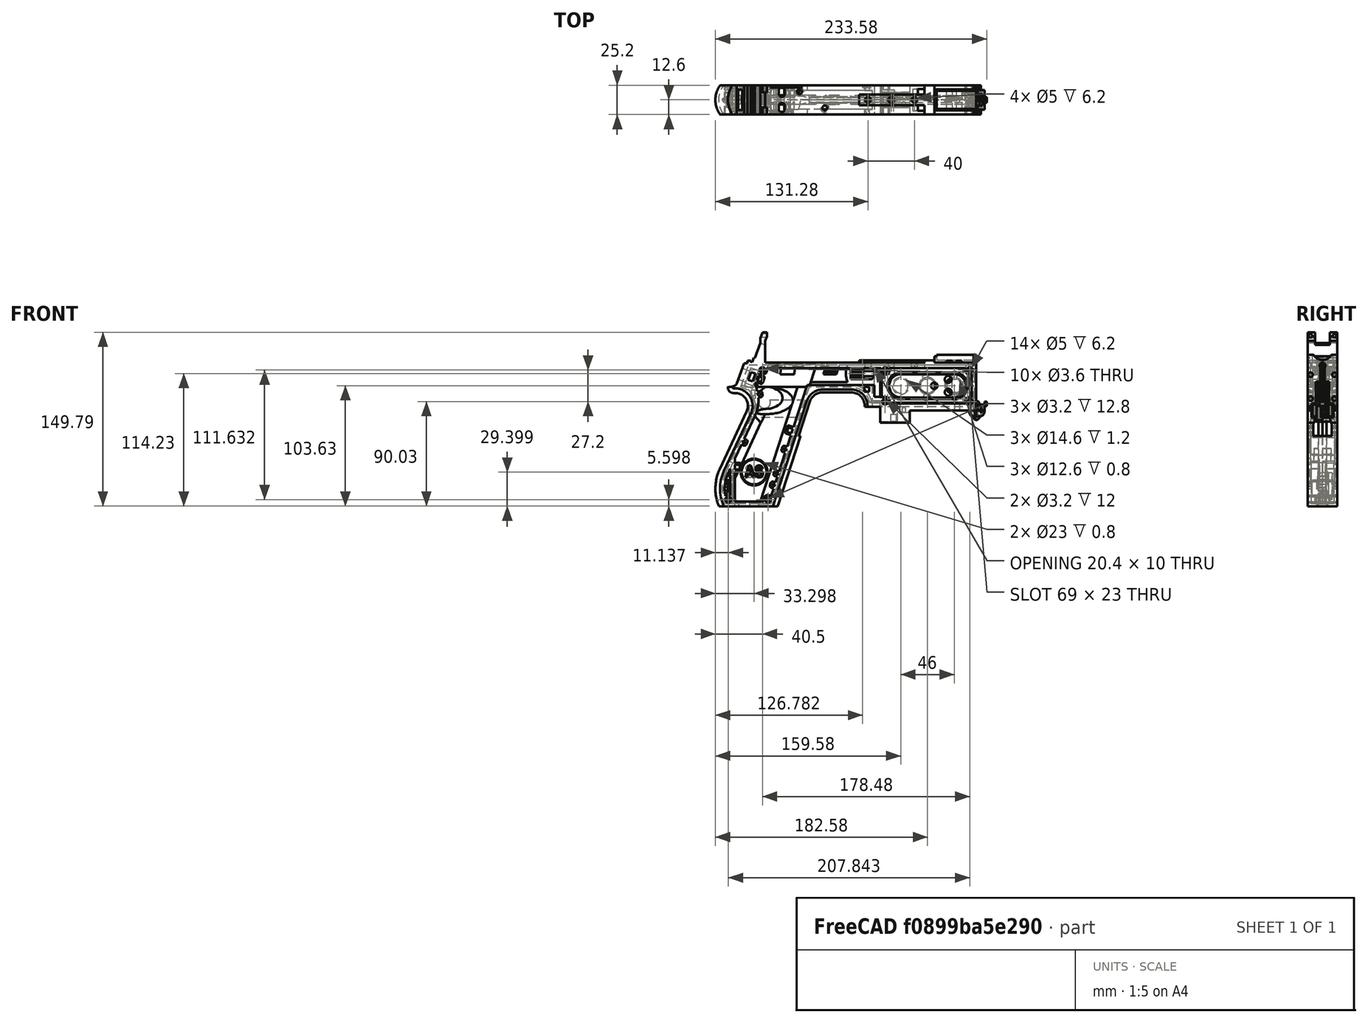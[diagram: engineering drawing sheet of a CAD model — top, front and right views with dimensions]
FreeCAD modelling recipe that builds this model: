
FCSTD DOCUMENT  (FreeCAD 1.0R39319 (Git))
Label: PICON-OF_ver_57
License: All rights reserved
LicenseURL: https://en.wikipedia.org/wiki/All_rights_reserved
objects: Sketcher::SketchObject×124, Part::Extrusion×63, Part::Cut×48, PartDesign::Pad×29, PartDesign::Pocket×21, PartDesign::Chamfer×15, PartDesign::Body×10, PartDesign::Fillet×6, Part::MultiFuse×5, Part::Part2DObjectPython×4, PartDesign::SubtractivePipe×4, PartDesign::SubtractiveLoft×4, PartDesign::Plane×3, PartDesign::SubShapeBinder×2, Part::Sweep×1, PartDesign::ShapeBinder×1, Mesh::Feature×1, PartDesign::Point×1, PartDesign::Groove×1
note: 626 computed .brp shape members not serialized (recipe doc carries the construction recipe); baked Part::Feature solids carry a one-line shape summary decoded from their .brp

FEATURE [Sketcher::SketchObject] Sketch  label="corpo principale"
  ArcFitTolerance = 1e-06
  AttacherType = Attacher::AttachEngine3D
  AttachmentSupport = -> [XZ_Plane]
  FullyConstrained = true
  MakeInternals = false
  MapMode = 5
  Placement = pos=(0,0,0) rot=(1,0,0;1.5708rad)
  sketch-geometry (65):
    g0: LineSegment StartX=0 StartY=0 StartZ=0 EndX=-57.2 EndY=0 EndZ=0
    g1: LineSegment StartX=-57.2 StartY=0 StartZ=0 EndX=-57.2 EndY=-10.4 EndZ=0
    g2: LineSegment StartX=-57.2 StartY=-10.4 StartZ=0 EndX=-82.8 EndY=-10.4 EndZ=0
    g3: LineSegment StartX=-82.8 StartY=-10.4 StartZ=0 EndX=-82.8 EndY=3.2 EndZ=0
    g4: LineSegment StartX=-82.8 StartY=3.2 StartZ=0 EndX=-93.6 EndY=3.2 EndZ=0
    g5: LineSegment StartX=-93.6 StartY=3.2 StartZ=0 EndX=-93.6 EndY=4 EndZ=0
    g6: LineSegment StartX=-107.6 StartY=18 StartZ=0 EndX=-132.428 EndY=18 EndZ=0
    g7: LineSegment StartX=-145.743 StartY=8.32624 StartZ=0 EndX=-175.232 EndY=-82.4316 EndZ=0
    g8: LineSegment StartX=-175.232 StartY=-82.4316 StartZ=0 EndX=-217.232 EndY=-82.4316 EndZ=0
    g9: LineSegment StartX=-217.232 StartY=-52.1862 StartZ=0 EndX=-193.988 EndY=-2.33927 EndZ=0
    g10: LineSegment StartX=-206.196 StartY=23.0857 StartZ=0 EndX=-199.861 EndY=40.4914 EndZ=0
    g11: LineSegment StartX=-199.861 StartY=40.4914 StartZ=0 EndX=-197.061 EndY=40.4914 EndZ=0
    g12: LineSegment StartX=-197.061 StartY=40.4914 StartZ=0 EndX=-197.061 EndY=42.8914 EndZ=0
    g13: LineSegment StartX=-197.061 StartY=42.8914 StartZ=0 EndX=-194.261 EndY=42.8914 EndZ=0
    g14: LineSegment StartX=-194.261 StartY=42.8914 StartZ=0 EndX=-194.535 EndY=42.1397 EndZ=0
    g15: LineSegment StartX=-194.535 StartY=42.1397 StartZ=0 EndX=-193.031 EndY=41.5924 EndZ=0
    g16: LineSegment StartX=-193.031 StartY=41.5924 StartZ=0 EndX=-191.663 EndY=45.3512 EndZ=0
    g17: LineSegment StartX=-191.663 StartY=45.3512 StartZ=0 EndX=-190.536 EndY=44.9408 EndZ=0
    g18: LineSegment StartX=-190.536 StartY=44.9408 StartZ=0 EndX=-185.747 EndY=58.0965 EndZ=0
    g19: LineSegment StartX=-185.747 StartY=58.0965 StartZ=0 EndX=-185.747 EndY=62.0965 EndZ=0
    g20: LineSegment StartX=-185.747 StartY=62.0965 StartZ=0 EndX=-183.832 EndY=67.3588 EndZ=0
    g21: LineSegment StartX=-183.832 StartY=67.3588 StartZ=0 EndX=-180.232 EndY=67.3588 EndZ=0
    g22: LineSegment StartX=-180.232 StartY=67.3588 StartZ=0 EndX=-180.232 EndY=63.7588 EndZ=0
    g23: LineSegment StartX=-180.232 StartY=63.7588 StartZ=0 EndX=-181.6 EndY=60 EndZ=0
    g24: LineSegment StartX=-181.6 StartY=60 StartZ=0 EndX=-181.6 EndY=41.2 EndZ=0
    g25: LineSegment StartX=-181.6 StartY=41.2 StartZ=0 EndX=-100.8 EndY=41.2 EndZ=0
    g26: LineSegment StartX=-36 StartY=43.2 StartZ=0 EndX=-36 EndY=41.2 EndZ=0
    g27: LineSegment StartX=0 StartY=48 StartZ=0 EndX=0 EndY=0 EndZ=0
    g28: LineSegment StartX=-209.901 StartY=19.85 StartZ=0 EndX=-209.901 EndY=20.1 EndZ=0
    g29: LineSegment StartX=-208.001 StartY=22 StartZ=0 EndX=-207.747 EndY=22 EndZ=0
    g30: LineSegment StartX=-207.583 StartY=19 StartZ=0 EndX=-209.051 EndY=19 EndZ=0
    g31: ArcOfCircle CenterX=-208.001 CenterY=20.1 CenterZ=0 NormalX=0 NormalY=0 NormalZ=1 AngleXU=0 Radius=1.9 StartAngle=1.5708 EndAngle=3.14159
    g32: GeomPoint [constr] X=-209.901 Y=22 Z=0
    g33: ArcOfCircle CenterX=-209.051 CenterY=19.85 CenterZ=0 NormalX=0 NormalY=0 NormalZ=1 AngleXU=0 Radius=0.85 StartAngle=3.14159 EndAngle=4.71239
    g34: GeomPoint [constr] X=-209.901 Y=19 Z=0
    g35: ArcOfCircle CenterX=-207.747 CenterY=23.65 CenterZ=0 NormalX=0 NormalY=0 NormalZ=1 AngleXU=0 Radius=1.65 StartAngle=4.71239 EndAngle=5.93412
    g36: GeomPoint [constr] X=-206.591 Y=22 Z=0
    g37: LineSegment StartX=-4 StartY=6 StartZ=0 EndX=-4 EndY=36.4 EndZ=0
    g38: LineSegment StartX=-4 StartY=36.4 StartZ=0 EndX=-185.2 EndY=36.4 EndZ=0
    g39: LineSegment StartX=-185.2 StartY=36.4 StartZ=0 EndX=-190.441 EndY=22 EndZ=0
    g40: LineSegment StartX=-214.575 StartY=-78.4316 StartZ=0 EndX=-178.142 EndY=-78.4316 EndZ=0
    g41: LineSegment StartX=-178.142 StartY=-78.4316 StartZ=0 EndX=-145.51 EndY=22 EndZ=0
    g42: LineSegment StartX=-145.51 StartY=22 StartZ=0 EndX=-87.91 EndY=22 EndZ=0
    g43: LineSegment StartX=-87.91 StartY=22 StartZ=0 EndX=-87.91 EndY=11.6 EndZ=0
    g44: LineSegment StartX=-87.91 StartY=11.6 StartZ=0 EndX=-80.11 EndY=11.6 EndZ=0
    g45: LineSegment StartX=-80.11 StartY=11.6 StartZ=0 EndX=-80.11 EndY=6 EndZ=0
    g46: LineSegment StartX=-80.11 StartY=6 StartZ=0 EndX=-4 EndY=6 EndZ=0
    g47: LineSegment StartX=-190.363 StartY=-4.02975 StartZ=0 EndX=-213.607 EndY=-53.8767 EndZ=0
    g48: ArcOfCircle CenterX=-132.428 CenterY=4 CenterZ=0 NormalX=0 NormalY=0 NormalZ=1 AngleXU=0 Radius=14 StartAngle=1.5708 EndAngle=2.82743
    g49: GeomPoint [constr] X=-142.6 Y=18 Z=0
    g50: ArcOfCircle CenterX=-107.6 CenterY=4 CenterZ=0 NormalX=0 NormalY=0 NormalZ=1 AngleXU=0 Radius=14 StartAngle=0 EndAngle=1.5708
    g51: GeomPoint [constr] X=-93.6 Y=18 Z=0
    g52: ArcOfCircle CenterX=-184.801 CenterY=-67.3089 CenterZ=0 NormalX=0 NormalY=0 NormalZ=1 AngleXU=0 Radius=35.7833 StartAngle=2.70526 EndAngle=3.57792
    g53: ArcOfCircle CenterX=-207.583 CenterY=4 CenterZ=0 NormalX=0 NormalY=0 NormalZ=1 AngleXU=0 Radius=15 StartAngle=5.84685 EndAngle=7.85398
    g54: LineSegment [constr] StartX=-213.607 StartY=-53.8767 StartZ=0 EndX=-217.232 EndY=-52.1862 EndZ=0
    g55: ArcOfCircle CenterX=-184.801 CenterY=-67.3089 CenterZ=0 NormalX=0 NormalY=0 NormalZ=1 AngleXU=0 Radius=31.7833 StartAngle=2.70526 EndAngle=3.49911
    g56: ArcOfCircle CenterX=-218.095 CenterY=8.90192 CenterZ=0 NormalX=0 NormalY=0 NormalZ=1 AngleXU=0 Radius=30.5989 StartAngle=5.84685 EndAngle=6.72553
    g57: LineSegment StartX=-44.6 StartY=43.2 StartZ=0 EndX=-36 EndY=43.2 EndZ=0
    g58: LineSegment StartX=-100.8 StartY=41.2 StartZ=0 EndX=-44.6 EndY=41.2 EndZ=0
    g59: LineSegment StartX=-44.6 StartY=41.2 StartZ=0 EndX=-44.6 EndY=43.2 EndZ=0
    g60: LineSegment StartX=-2.4 StartY=48 StartZ=0 EndX=0 EndY=48 EndZ=0
    g61: LineSegment StartX=-36 StartY=41.2 StartZ=0 EndX=-2.4 EndY=41.2 EndZ=0
    g62: LineSegment StartX=-2.4 StartY=41.2 StartZ=0 EndX=-2.4 EndY=48 EndZ=0
    g63: LineSegment [constr] StartX=-181.6 StartY=36.4 StartZ=0 EndX=-152.209 EndY=36.4 EndZ=0
    g64: LineSegment [constr] StartX=-181.6 StartY=36.4 StartZ=0 EndX=-130.41 EndY=36.4 EndZ=0
  constraints (183):
    c: Coincident(g-1,g0)
    c: PointOnObject(g0,g-1)
    c: Coincident(g0,g1)
    c: Vertical(g1)
    c: Coincident(g1,g2)
    c: Horizontal(g2)
    c: Coincident(g2,g3)
    c: Vertical(g3)
    c: Coincident(g3,g4)
    c: Coincident(g4,g5)
    c: Vertical(g5)
    c: Horizontal(g6)
    c: Coincident(g7,g8)
    c: Horizontal(g8)
    c: Coincident(g10,g11)
    c: Horizontal(g11)
    c: Coincident(g11,g12)
    c: Vertical(g12)
    c: Coincident(g12,g13)
    c: Horizontal(g13)
    c: Coincident(g13,g14)
    c: Coincident(g14,g15)
    c: Coincident(g15,g16)
    c: Coincident(g16,g17)
    c: Coincident(g17,g18)
    c: Coincident(g18,g19)
    c: Vertical(g19)
    c: Coincident(g19,g20)
    c: Coincident(g20,g21)
    c: Horizontal(g21)
    c: Coincident(g21,g22)
    c: Vertical(g22)
    c: Coincident(g22,g23)
    c: Coincident(g23,g24)
    c: Vertical(g24)
    c: Coincident(g24,g25)
    c: Horizontal(g25)
    c: Coincident(g57,g26)
    c: Vertical(g26)
    c: Coincident(g26,g61)
    c: PointOnObject(g60,g-2)
    c: Coincident(g60,g27)
    c: Coincident(g27,g0)
    c: DistanceY(g27,g27) = 48
    c: DistanceY(g1,g1) = 10.4
    c: DistanceX(g0,g0) = 57.2
    c: DistanceX(g2,g2) = 25.6
    c: Horizontal(g4)
    c: DistanceY(g3,g3) = 13.6
    c: DistanceX(g4,g4) = 10.8
    c: DistanceY(g5,g51) = 14.8
    c: DistanceX(g49,g51) = 49
    c: Distance(g7,g49) = 105.6
    c: DistanceX(g61,g60) = 36
    c: DistanceX(g25,g25) = 80.8
    c: DistanceY(g24,g24) = 18.8
    c: DistanceY(g22,g22) = 3.6
    c: Distance(g23) = 4
    c: Angle(g-1,g23) = 1.22173
    c: DistanceX(g21,g21) = 3.6
    c: Distance(g20) = 5.6
    c: Angle(g-1,g20) = 1.22173
    c: DistanceY(g19,g19) = 4
    c: Distance(g18) = 14
    c: Angle(g-1,g18) = 1.22173
    c: Distance(g17) = 1.2
    c: Distance(g16) = 4
    c: Angle(g16) = 1.22173
    c: Perpendicular(g18,g17)
    c: Distance(g15) = 1.6
    c: Perpendicular(g16,g15)
    c: Distance(g14) = 0.8
    c: DistanceX(g13,g13) = 2.8
    c: Perpendicular(g15,g14)
    c: DistanceY(g12,g12) = 2.4
    c: DistanceX(g11,g11) = 2.8
    c: Distance(g9) = 55
    c: Angle(g9,g-1) = 2.00713
    c: Horizontal(g29)
    c: Vertical(g28)
    c: Horizontal(g30)
    c: PointOnObject(g32,g29)
    c: PointOnObject(g32,g28)
    c: Tangent(g29,g31) = 1.5708
    c: Tangent(g28,g31) = 1.5708
    c: PointOnObject(g34,g28)
    c: PointOnObject(g34,g30)
    c: Tangent(g28,g33) = 1.5708
    c: Tangent(g30,g33) = 1.5708
    c: PointOnObject(g36,g29)
    c: PointOnObject(g36,g10)
    c: Tangent(g29,g35) = -1.5708
    c: Tangent(g10,g35) = -1.5708
    c: Angle(g-1,g10) = 1.22173
    c: Radius(g35) = 1.65
    c: Vertical(g37)
    c: Coincident(g37,g38)
    c: Horizontal(g38)
    c: Coincident(g38,g39)
    c: Horizontal(g40)
    c: Coincident(g40,g41)
    c: Coincident(g41,g42)
    c: Horizontal(g42)
    c: Coincident(g42,g43)
    c: Vertical(g43)
    c: Coincident(g43,g44)
    c: Horizontal(g44)
    c: Coincident(g44,g45)
    c: Vertical(g45)
    c: Coincident(g45,g46)
    c: Coincident(g46,g37)
    c: Horizontal(g46)
    c: DistanceY(g0,g37) = 6
    c: DistanceX(g37,g0) = 4
    c: DistanceY(g37,g25) = 4.8
    c: DistanceX(g38,g38) = 181.2
    c: DistanceX(g42,g42) = 57.6
    c: DistanceY(g49,g41) = 4
    c: DistanceX(g41,g49) = 2.91
    c: DistanceY(g43,g43) = 10.4
    c: DistanceX(g44,g44) = 7.8
    c: DistanceY(g7,g40) = 4
    c: Distance(g47) = 55
    c: Angle(g-1,g39) = 1.22173
    c: PointOnObject(g49,g7)
    c: PointOnObject(g49,g6)
    c: Tangent(g7,g48) = -1.5708
    c: Tangent(g6,g48) = -1.5708
    c: PointOnObject(g51,g5)
    c: PointOnObject(g51,g6)
    c: Tangent(g5,g50) = -1.5708
    c: Tangent(g6,g50) = -1.5708
    c: Radius(g50) = 14
    c: Radius(g48) = 14
    c: DistanceX(g8,g8) = 42
    c: Angle(g7,g-1) = 1.88496
    c: Parallel(g41,g7)
    c: Parallel(g47,g9)
    c: Coincident(g52,g8)
    c: Tangent(g52,g9) = 1.5708
    c: DistanceX(g9,g8) = 0
    c: Tangent(g53,g9) = -1.5708
    c: Tangent(g53,g30) = -1.5708
    c: Diameter(g53) = 30
    c: DistanceY(g53,g0) = -4
    c: Coincident(g54,g47)
    c: Distance(g54) = 4
    c: Coincident(g54,g9)
    c: Coincident(g55,g40)
    c: Tangent(g55,g47) = -1.5708
    c: Coincident(g52,g55)
    c: Coincident(g56,g39)
    c: Tangent(g56,g47) = 1.5708
    c: Horizontal(g57)
    c: DistanceX(g57,g57) = 8.6
    c: Coincident(g58,g25)
    c: Horizontal(g58)
    c: Coincident(g59,g58)
    c: Vertical(g59)
    c: DistanceY(g58,g57) = 2
    c: DistanceX(g58,g58) = 56.2
    c: Coincident(g59,g57)
    c: DistanceY(g41,g36) = 0
    c: DistanceY(g36,g39) = 0
    c: DistanceY(g28,g28) = 0.25
    c: DistanceX(g30,g36) = 2.46
    c: DistanceX(g28,g29) = 1.9
    c: Coincident(g62,g60)
    c: Horizontal(g60)
    c: DistanceX(g62,g27) = 2.4
    c: Coincident(g61,g62)
    c: DistanceY(g26,g26) = 2
    c: Vertical(g62)
    c: DistanceY(g61,g60) = 6.8
    c: Horizontal(g61)
    c: Distance(g63) = 29.391
    c: PointOnObject(g63,g38)
    c: PointOnObject(g63,g38)
    c: Distance(g64) = 51.19
    c: PointOnObject(g64,g38)
    c: PointOnObject(g64,g38)
    c: DistanceX(g24,g63) = 0
    c: DistanceX(g24,g64) = 0
FEATURE [Part::Extrusion] Extrude  label="Extrude corpo principale"
  Base = -> Sketch
  Dir = (0,-1,2e-16)
  DirMode = 2
  FaceMakerClass = Part::FaceMakerBullseye
  FaceMakerMode = 3
  LengthFwd = 25.2
  LengthRev = 12.6
  Solid = true
  Symmetric = true
FEATURE [Sketcher::SketchObject] Sketch002  label="scavo grilletto"
  ArcFitTolerance = 1e-06
  AttachmentSupport = -> [XZ_Plane]
  ExternalGeometry = -> [Sketch]
  FullyConstrained = true
  MakeInternals = false
  MapMode = 5
  Placement = pos=(0,0,0) rot=(1,0,0;1.5708rad)
  sketch-geometry (4):
    g0: LineSegment StartX=-89.51 StartY=22 StartZ=0 EndX=-152.71 EndY=22 EndZ=0
    g1: LineSegment StartX=-152.71 StartY=22 StartZ=0 EndX=-167.006 EndY=-22 EndZ=0
    g2: LineSegment StartX=-167.006 StartY=-22 StartZ=0 EndX=-89.51 EndY=-22 EndZ=0
    g3: LineSegment StartX=-89.51 StartY=-22 StartZ=0 EndX=-89.51 EndY=22 EndZ=0
  constraints (12):
    c: Horizontal(g0)
    c: Coincident(g0,g1)
    c: Coincident(g1,g2)
    c: Horizontal(g2)
    c: Coincident(g2,g3)
    c: Coincident(g3,g0)
    c: Vertical(g3)
    c: Angle(g1,g0) = 1.88496
    c: DistanceY(g3,g3) = 44
    c: DistanceX(g0,g0) = 63.2
    c: DistanceX(g0,g-3) = 1.6
    c: DistanceY(g-3,g0) = 0
FEATURE [Sketcher::SketchObject] Sketch004  label="traiettoria arrotondamento impugnatura anteriore"
  ArcFitTolerance = 1e-06
  AttachmentSupport = -> [XZ_Plane]
  ExternalGeometry = -> [Sketch]
  FullyConstrained = true
  MakeInternals = false
  MapMode = 5
  Placement = pos=(0,0,0) rot=(1,0,0;1.5708rad)
  sketch-geometry (13):
    g0: LineSegment StartX=-175.232 StartY=-82.4316 StartZ=0 EndX=-145.743 EndY=8.32624 EndZ=0
    g1: LineSegment StartX=-93.6 StartY=3.2 StartZ=0 EndX=-93.6 EndY=4 EndZ=0
    g2: LineSegment StartX=-132.428 StartY=18 StartZ=0 EndX=-107.6 EndY=18 EndZ=0
    g3: ArcOfCircle CenterX=-132.428 CenterY=4 CenterZ=0 NormalX=0 NormalY=0 NormalZ=1 AngleXU=0 Radius=14 StartAngle=1.5708 EndAngle=2.82743
    g4: ArcOfCircle CenterX=-107.6 CenterY=4 CenterZ=0 NormalX=0 NormalY=0 NormalZ=1 AngleXU=0 Radius=14 StartAngle=0 EndAngle=1.5708
    g5: LineSegment StartX=-175.232 StartY=-82.4316 StartZ=0 EndX=-217.232 EndY=-82.4316 EndZ=0
    g6: LineSegment StartX=-217.232 StartY=-52.1862 StartZ=0 EndX=-193.988 EndY=-2.33927 EndZ=0
    g7: LineSegment StartX=-209.051 StartY=19 StartZ=0 EndX=-207.583 EndY=19 EndZ=0
    g8: LineSegment StartX=-209.901 StartY=20.1 StartZ=0 EndX=-209.901 EndY=19.85 EndZ=0
    g9: ArcOfCircle CenterX=-184.801 CenterY=-67.3089 CenterZ=0 NormalX=0 NormalY=0 NormalZ=1 AngleXU=0 Radius=35.7833 StartAngle=2.70526 EndAngle=3.57792
    g10: ArcOfCircle CenterX=-207.583 CenterY=4 CenterZ=0 NormalX=0 NormalY=0 NormalZ=1 AngleXU=0 Radius=15 StartAngle=5.84685 EndAngle=7.85398
    g11: ArcOfCircle CenterX=-209.051 CenterY=19.85 CenterZ=0 NormalX=0 NormalY=0 NormalZ=1 AngleXU=0 Radius=0.85 StartAngle=3.14159 EndAngle=4.71239
    g12: ArcOfCircle CenterX=-208.001 CenterY=20.1 CenterZ=0 NormalX=0 NormalY=0 NormalZ=1 AngleXU=0 Radius=1.9 StartAngle=1.5708 EndAngle=3.14159
  constraints (26):
    c: Coincident(g0,g-3)
    c: Coincident(g0,g-6)
    c: Coincident(g1,g-8)
    c: Coincident(g1,g-7)
    c: Coincident(g2,g-5)
    c: Coincident(g2,g-4)
    c: Coincident(g3,g2)
    c: Tangent(g3,g0) = 1.5708
    c: Coincident(g4,g1)
    c: Tangent(g4,g2) = 1.5708
    c: Coincident(g5,g0)
    c: Coincident(g5,g-9)
    c: Coincident(g6,g-12)
    c: Coincident(g6,g-11)
    c: Coincident(g7,g-15)
    c: Coincident(g7,g-14)
    c: Coincident(g8,g-16)
    c: Coincident(g8,g-17)
    c: Tangent(g9,g6) = 1.5708
    c: Coincident(g9,g5)
    c: Coincident(g10,g7)
    c: Tangent(g10,g6) = -1.5708
    c: Tangent(g11,g7) = -1.5708
    c: Coincident(g11,g8)
    c: Tangent(g12,g8) = -1.5708
    c: Coincident(g12,g-17)
FEATURE [PartDesign::Plane] DatumPlane  label="Piano per disegno arrotondamento impugnatura"
  AttachmentSupport = -> [Sketch]
  Length = 73.6581
  MapMode = 7
  Placement = pos=(-145.743,1.8e-15,8.32624) rot=(0.154555,0.154555,0.97582;1.59527rad)
  ResizeMode = 0
  Width = 303.511
FEATURE [Sketcher::SketchObject] Sketch005  label="forma arrotondamento impugnatura anteriore"
  ArcFitTolerance = 1e-06
  AttachmentSupport = -> [DatumPlane]
  FullyConstrained = true
  MakeInternals = false
  MapMode = 5
  Placement = pos=(-145.743,1.8e-15,8.32624) rot=(0.154555,0.154555,0.97582;1.59527rad)
  sketch-geometry (5):
    g0: GeomPoint [constr] X=0 Y=-4 Z=0
    g1: GeomPoint [constr] X=-12.6 Y=7.1e-15 Z=0
    g2: GeomPoint [constr] X=12.6 Y=4.97e-14 Z=0
    g3: LineSegment StartX=-12.6 StartY=7.1e-15 StartZ=0 EndX=12.6 EndY=4.97e-14 EndZ=0
    g4: ArcOfCircle CenterX=-3.88e-14 CenterY=17.845 CenterZ=0 NormalX=0 NormalY=0 NormalZ=1 AngleXU=0 Radius=21.845 StartAngle=4.09759 EndAngle=5.32718
  constraints (11):
    c: DistanceY(g0,g-1) = 4
    c: DistanceX(g-1,g0) = 0
    c: DistanceX(g1,g-1) = 12.6
    c: DistanceX(g-1,g2) = 12.6
    c: DistanceY(g-1,g2) = 0
    c: DistanceY(g-1,g1) = 0
    c: Coincident(g3,g1)
    c: Coincident(g3,g2)
    c: Coincident(g4,g1)
    c: Coincident(g4,g2)
    c: PointOnObject(g0,g4)
FEATURE [Part::Sweep] Sweep  label="Sweep impugnatura"
  Frenet = true
  Sections = -> [Sketch005]
  Solid = true
  Spine = -> Sketch [Edge32,Edge33,Edge34,Edge35,Edge36,Edge37,Edge38,Edge39,Edge40,Edge41,Edge42,Edge43,Edge44]
  Transition = 1
FEATURE [Sketcher::SketchObject] Sketch008  label="buchi e pulizie varie"
  ArcFitTolerance = 1e-06
  AttachmentSupport = -> [XZ_Plane]
  ExternalGeometry = -> [Sketch]
  FullyConstrained = true
  MakeInternals = false
  MapMode = 5
  Placement = pos=(0,0,0) rot=(1,0,0;1.5708rad)
  sketch-geometry (26):
    g0: LineSegment StartX=-96.278 StartY=20.155 StartZ=0 EndX=-92.278 EndY=20.155 EndZ=0
    g1: LineSegment StartX=-92.278 StartY=20.155 StartZ=0 EndX=-92.278 EndY=16.155 EndZ=0
    g2: LineSegment StartX=-92.278 StartY=16.155 StartZ=0 EndX=-96.278 EndY=16.155 EndZ=0
    g3: LineSegment StartX=-96.278 StartY=16.155 StartZ=0 EndX=-96.278 EndY=20.155 EndZ=0
    g4: LineSegment StartX=-222.232 StartY=-82.4316 StartZ=0 EndX=-170.232 EndY=-82.4316 EndZ=0
    g5: LineSegment StartX=-170.232 StartY=-82.4316 StartZ=0 EndX=-170.232 EndY=-86.4316 EndZ=0
    g6: LineSegment StartX=-170.232 StartY=-86.4316 StartZ=0 EndX=-222.232 EndY=-86.4316 EndZ=0
    g7: LineSegment StartX=-222.232 StartY=-86.4316 StartZ=0 EndX=-222.232 EndY=-82.4316 EndZ=0
    g8: LineSegment StartX=-213.901 StartY=20.1 StartZ=0 EndX=-213.901 EndY=26 EndZ=0
    g9: LineSegment StartX=-213.901 StartY=26 StartZ=0 EndX=-206.196 EndY=26 EndZ=0
    g10: LineSegment StartX=-17.4 StartY=42.8 StartZ=0 EndX=-12.4 EndY=42.8 EndZ=0
    g11: LineSegment StartX=-12.4 StartY=42.8 StartZ=0 EndX=-12.4 EndY=41.2 EndZ=0
    g12: LineSegment StartX=-12.4 StartY=41.2 StartZ=0 EndX=-17.4 EndY=41.2 EndZ=0
    g13: LineSegment StartX=-17.4 StartY=41.2 StartZ=0 EndX=-17.4 EndY=42.8 EndZ=0
    g14: LineSegment StartX=-25.9 StartY=42.8 StartZ=0 EndX=-20.9 EndY=42.8 EndZ=0
    g15: LineSegment StartX=-20.9 StartY=42.8 StartZ=0 EndX=-20.9 EndY=41.2 EndZ=0
    g16: LineSegment StartX=-20.9 StartY=41.2 StartZ=0 EndX=-25.9 EndY=41.2 EndZ=0
    g17: LineSegment StartX=-25.9 StartY=41.2 StartZ=0 EndX=-25.9 EndY=42.8 EndZ=0
    g18: GeomPoint [constr] X=-206.196 Y=23.0857 Z=0
    g19: GeomPoint [constr] X=-213.901 Y=20.1 Z=0
    g20: BSplineCurve PolesCount=4 KnotsCount=2 Degree=3 IsPeriodic=0
    g21-g24: Circle [constr] x4 (B-spline internal-alignment scaffolding for g20; pole/knot coordinates omitted)
    g25: LineSegment StartX=-206.196 StartY=26 StartZ=0 EndX=-206.196 EndY=23.0857 EndZ=0
  constraints (73):
    c: Horizontal(g0)
    c: Coincident(g1,g0)
    c: Vertical(g1)
    c: Coincident(g2,g1)
    c: Horizontal(g2)
    c: Coincident(g3,g2)
    c: Coincident(g3,g0)
    c: Vertical(g3)
    c: DistanceX(g0,g-4) = 4.368
    c: DistanceY(g0,g-4) = 1.845
    c: DistanceY(g1,g1) = 4
    c: DistanceX(g2,g2) = 4
    c: Horizontal(g4)
    c: Coincident(g5,g4)
    c: Vertical(g5)
    c: Coincident(g6,g5)
    c: Horizontal(g6)
    c: Coincident(g7,g6)
    c: Coincident(g7,g4)
    c: Vertical(g7)
    c: DistanceY(g7,g7) = 4
    c: DistanceX(g4,g-5) = 5
    c: DistanceX(g-5,g4) = 5
    c: DistanceY(g4,g-5) = 0
    c: Coincident(g9,g8)
    c: Parallel(g9,g-6)
    c: DistanceX(g8,g-8) = 4
    c: Horizontal(g10)
    c: Coincident(g11,g10)
    c: Vertical(g11)
    c: Coincident(g12,g11)
    c: Horizontal(g12)
    c: Coincident(g13,g12)
    c: Coincident(g13,g10)
    c: Vertical(g13)
    c: Horizontal(g14)
    c: Coincident(g15,g14)
    c: Vertical(g15)
    c: Coincident(g16,g15)
    c: Horizontal(g16)
    c: Coincident(g17,g16)
    c: Coincident(g17,g14)
    c: Vertical(g17)
    c: DistanceY(g11,g10) = 1.6
    c: DistanceX(g10,g10) = 5
    c: DistanceY(g15,g14) = 1.6
    c: DistanceX(g14,g14) = 5
    c: DistanceX(g15,g12) = 3.5
    c: DistanceX(g11,g-9) = 10
    c: DistanceY(g-9,g11) = 0
    c: DistanceY(g-9,g15) = 0
    c: Perpendicular(g8,g9)
    c: DistanceY(g-7,g9) = 4
    c: DistanceY(g8,g-8) = 0
    c: InternalAlignment(g18,g20)
    c: InternalAlignment(g19,g20)
    c: InternalAlignment(g21,g20)
    c: Weight(g21) = 1
    c: InternalAlignment(g22,g20)
    c: Equal(g22,g21)
    c: InternalAlignment(g23,g20)
    c: Equal(g23,g21)
    c: InternalAlignment(g24,g20)
    c: Equal(g24,g21)
    c: Coincident(g18,g-12)
    c: Coincident(g19,g8)
    c: Coincident(g25,g9)
    c: Coincident(g25,g20)
    c: Vertical(g25)
    c: DistanceY(g20,g23) = 0
    c: DistanceY(g22,g18) = 2.26
    c: DistanceX(g22,g18) = 0.93
    c: DistanceX(g20,g23) = 2.9
FEATURE [Part::Extrusion] Extrude004  label="Extrude Buchi e pulizie varie"
  Base = -> Sketch008
  Dir = (0,-1,2e-16)
  DirMode = 2
  FaceMakerClass = Part::FaceMakerBullseye
  FaceMakerMode = 3
  LengthFwd = 25.2
  LengthRev = 0
  Solid = true
  Symmetric = true
FEATURE [Sketcher::SketchObject] Sketch009  label="rinforzi"
  ArcFitTolerance = 1e-06
  AttachmentSupport = -> [XZ_Plane]
  ExternalGeometry = -> [Sketch]
  FullyConstrained = true
  MakeInternals = false
  MapMode = 5
  Placement = pos=(0,0,0) rot=(1,0,0;1.5708rad)
  sketch-geometry (9):
    g0: LineSegment StartX=-87.91 StartY=22 StartZ=0 EndX=-87.91 EndY=36.4 EndZ=0
    g1: LineSegment StartX=-87.91 StartY=36.4 StartZ=0 EndX=-97.91 EndY=36.4 EndZ=0
    g2: LineSegment StartX=-97.91 StartY=36.4 StartZ=0 EndX=-97.91 EndY=22 EndZ=0
    g3: LineSegment StartX=-97.91 StartY=22 StartZ=0 EndX=-87.91 EndY=22 EndZ=0
    g4: LineSegment StartX=-149.713 StartY=9.06563 StartZ=0 EndX=-154.586 EndY=-5.93437 EndZ=0
    g5: LineSegment StartX=-154.586 StartY=-5.93437 StartZ=0 EndX=-191.863 EndY=-5.93437 EndZ=0
    g6: LineSegment StartX=-191.863 StartY=-5.93437 StartZ=0 EndX=-191.863 EndY=9.06563 EndZ=0
    g7: LineSegment StartX=-191.863 StartY=9.06563 StartZ=0 EndX=-149.713 EndY=9.06563 EndZ=0
    g8: LineSegment [constr] StartX=-145.51 StartY=22 StartZ=0 EndX=-149.713 EndY=9.06563 EndZ=0
  constraints (25):
    c: Vertical(g0)
    c: Coincident(g1,g0)
    c: Horizontal(g1)
    c: Coincident(g2,g1)
    c: Vertical(g2)
    c: Coincident(g3,g2)
    c: Coincident(g3,g0)
    c: Horizontal(g3)
    c: Coincident(g0,g-4)
    c: DistanceX(g3,g3) = 10
    c: DistanceY(g0,g-3) = 0
    c: Coincident(g5,g4)
    c: Horizontal(g5)
    c: Coincident(g6,g5)
    c: Vertical(g6)
    c: Coincident(g7,g6)
    c: Coincident(g7,g4)
    c: Horizontal(g7)
    c: Distance(g8) = 13.6
    c: Parallel(g-6,g8)
    c: Coincident(g-6,g8)
    c: Parallel(g4,g-6)
    c: DistanceY(g4,g4) = 15
    c: Coincident(g4,g8)
    c: DistanceX(g-5,g5) = -1.5
FEATURE [Part::Extrusion] Extrude001  label="Extrude scavo grilletto"
  Base = -> Sketch002
  Dir = (0,-1,2e-16)
  DirMode = 2
  FaceMakerClass = Part::FaceMakerBullseye
  FaceMakerMode = 3
  LengthFwd = 16
  LengthRev = 0
  Solid = true
  Symmetric = true
FEATURE [Part::Extrusion] Extrude005  label="Extrude Rinforzi"
  Base = -> Sketch009
  Dir = (0,-1,2e-16)
  DirMode = 2
  FaceMakerClass = Part::FaceMakerBullseye
  FaceMakerMode = 3
  LengthFwd = 2
  LengthRev = 0
  Placement = pos=(0,12.6,0) rot=(0,0,1;0rad)
  Solid = true
  Symmetric = false
FEATURE [PartDesign::ShapeBinder] CopyCut
  TraceSupport = false
FEATURE [PartDesign::Plane] DatumPlane001
  AttachmentSupport = -> [CopyCut]
  Length = 283.944
  MapMode = 5
  Placement = pos=(0,12.6,0) rot=(0,0.707107,0.707107;3.14159rad)
  ResizeMode = 0
  Width = 188.15
FEATURE [Sketcher::SketchObject] Sketch010  label="buco neopixel"
  ArcFitTolerance = 1e-06
  AttachmentSupport = -> [XZ_Plane]
  ExternalGeometry = -> [Sketch]
  FullyConstrained = true
  MakeInternals = false
  MapMode = 5
  Placement = pos=(0,0,0) rot=(1,0,0;1.5708rad)
  sketch-geometry (5):
    g0: LineSegment [constr] StartX=-199.861 StartY=40.4914 StartZ=0 EndX=-201.368 EndY=36.3521 EndZ=0
    g1: LineSegment StartX=-201.368 StartY=36.3521 StartZ=0 EndX=-204.932 EndY=26.5605 EndZ=0
    g2: LineSegment StartX=-201.368 StartY=36.3521 StartZ=0 EndX=-180.2 EndY=28.6477 EndZ=0
    g3: LineSegment StartX=-180.2 StartY=28.6477 StartZ=0 EndX=-183.764 EndY=18.8561 EndZ=0
    g4: LineSegment StartX=-183.764 StartY=18.8561 StartZ=0 EndX=-204.932 EndY=26.5605 EndZ=0
  constraints (14):
    c: Parallel(g0,g-3)
    c: Distance(g0) = 4.405
    c: Coincident(g0,g-3)
    c: Coincident(g2,g1)
    c: Coincident(g3,g2)
    c: Coincident(g4,g3)
    c: Coincident(g4,g1)
    c: Parallel(g1,g-3)
    c: Distance(g1) = 10.42
    c: Coincident(g1,g0)
    c: Parallel(g2,g4)
    c: Perpendicular(g1,g2)
    c: DistanceX(g-4,g2) = 5
    c: Parallel(g3,g1)
FEATURE [Part::Extrusion] Extrude006  label="Extrude buco neopixel"
  Base = -> Sketch010
  Dir = (0,-1,2e-16)
  DirMode = 2
  FaceMakerClass = Part::FaceMakerBullseye
  FaceMakerMode = 3
  LengthFwd = 17.2
  LengthRev = 0
  Solid = true
  Symmetric = true
FEATURE [Sketcher::SketchObject] Sketch011  label="fermo grilletto"
  ArcFitTolerance = 1e-06
  AttachmentSupport = -> [XZ_Plane]
  ExternalGeometry = -> [Sketch]
  FullyConstrained = true
  MakeInternals = false
  MapMode = 5
  Placement = pos=(0,0,0) rot=(1,0,0;1.5708rad)
  sketch-geometry (18):
    g0: LineSegment [constr] StartX=-145.51 StartY=22 StartZ=0 EndX=-157.347 EndY=-14.4293 EndZ=0
    g1: LineSegment [constr] StartX=-157.347 StartY=-14.4293 StartZ=0 EndX=-157.841 EndY=-15.951 EndZ=0
    g2: LineSegment StartX=-161.151 StartY=-13.1932 StartZ=0 EndX=-155.825 EndY=-14.9237 EndZ=0
    g3: LineSegment StartX=-163.167 StartY=-14.2205 StartZ=0 EndX=-164.403 EndY=-18.0247 EndZ=0
    g4: LineSegment StartX=-163.376 StartY=-20.0408 StartZ=0 EndX=-158.05 EndY=-21.7713 EndZ=0
    g5: LineSegment StartX=-158.05 StartY=-21.7713 StartZ=0 EndX=-155.825 EndY=-14.9237 EndZ=0
    g6: LineSegment StartX=-161.645 StartY=-14.7149 StartZ=0 EndX=-157.841 EndY=-15.951 EndZ=0
    g7: LineSegment StartX=-157.841 StartY=-15.951 StartZ=0 EndX=-159.077 EndY=-19.7552 EndZ=0
    g8: LineSegment StartX=-159.077 StartY=-19.7552 StartZ=0 EndX=-162.881 EndY=-18.5191 EndZ=0
    g9: LineSegment StartX=-162.881 StartY=-18.5191 StartZ=0 EndX=-161.645 EndY=-14.7149 EndZ=0
    g10: LineSegment [constr] StartX=-161.645 StartY=-14.7149 StartZ=0 EndX=-161.151 EndY=-13.1932 EndZ=0
    g11: LineSegment [constr] StartX=-159.077 StartY=-19.7552 StartZ=0 EndX=-157.555 EndY=-20.2496 EndZ=0
    g12: LineSegment [constr] StartX=-159.077 StartY=-19.7552 StartZ=0 EndX=-159.572 EndY=-21.2769 EndZ=0
    g13: LineSegment [constr] StartX=-161.645 StartY=-14.7149 StartZ=0 EndX=-163.167 EndY=-14.2205 EndZ=0
    g14: ArcOfCircle CenterX=-161.645 CenterY=-14.7149 CenterZ=0 NormalX=0 NormalY=0 NormalZ=1 AngleXU=0 Radius=1.6 StartAngle=1.25664 EndAngle=2.82743
    g15: GeomPoint [constr] X=-162.673 Y=-12.6988 Z=0
    g16: ArcOfCircle CenterX=-162.881 CenterY=-18.5191 CenterZ=0 NormalX=0 NormalY=0 NormalZ=1 AngleXU=0 Radius=1.6 StartAngle=2.82743 EndAngle=4.39823
    g17: GeomPoint [constr] X=-164.897 Y=-19.5464 Z=0
  constraints (48):
    c: Parallel(g0,g-3)
    c: Distance(g0) = 38.304
    c: Coincident(g0,g-3)
    c: Parallel(g1,g-3)
    c: Distance(g1) = 1.6
    c: Coincident(g1,g0)
    c: Coincident(g5,g4)
    c: Coincident(g5,g2)
    c: Coincident(g7,g6)
    c: Coincident(g8,g7)
    c: Coincident(g9,g8)
    c: Coincident(g9,g6)
    c: Parallel(g7,g-3)
    c: Parallel(g9,g7)
    c: Perpendicular(g6,g7)
    c: Parallel(g6,g8)
    c: Distance(g6) = 4
    c: Distance(g9) = 4
    c: Parallel(g5,g7)
    c: Parallel(g9,g3)
    c: Parallel(g2,g6)
    c: Parallel(g4,g8)
    c: Parallel(g13,g6)
    c: Parallel(g10,g9)
    c: Parallel(g11,g8)
    c: Parallel(g12,g7)
    c: Distance(g10) = 1.6
    c: Distance(g13) = 1.6
    c: Distance(g12) = 1.6
    c: Distance(g11) = 1.6
    c: Coincident(g10,g6)
    c: Coincident(g13,g6)
    c: Coincident(g12,g7)
    c: Coincident(g11,g7)
    c: Distance(g10,g15) = 1.6
    c: Distance(g15,g13) = 1.6
    c: Distance(g4,g12) = 1.6
    c: Distance(g4,g11) = 1.6
    c: PointOnObject(g15,g2)
    c: Tangent(g3,g14) = -1.5708
    c: Tangent(g2,g14) = 1.5708
    c: PointOnObject(g17,g4)
    c: PointOnObject(g17,g3)
    c: Tangent(g4,g16) = -1.5708
    c: Tangent(g3,g16) = -1.5708
    c: Equal(g16,g14)
    c: Coincident(g16,g8)
    c: Coincident(g6,g1)
FEATURE [Part::Extrusion] Extrude007  label="Extrude fermo grilletto"
  Base = -> Sketch011
  Dir = (0,-1,2e-16)
  DirMode = 2
  FaceMakerClass = Part::FaceMakerBullseye
  FaceMakerMode = 3
  LengthFwd = 25.2
  LengthRev = 0
  Solid = true
  Symmetric = true
FEATURE [Sketcher::SketchObject] Sketch012  label="buco oled"
  ArcFitTolerance = 1e-06
  AttachmentSupport = -> [XZ_Plane]
  ExternalGeometry = -> [Sketch]
  FullyConstrained = true
  MakeInternals = false
  MapMode = 5
  Placement = pos=(0,0,0) rot=(1,0,0;1.5708rad)
  sketch-geometry (4):
    g0: LineSegment StartX=-185.747 StartY=58.0965 StartZ=0 EndX=-180.232 EndY=56.0891 EndZ=0
    g1: LineSegment StartX=-185.747 StartY=58.0965 StartZ=0 EndX=-185.747 EndY=67.3588 EndZ=0
    g2: LineSegment StartX=-185.747 StartY=67.3588 StartZ=0 EndX=-180.232 EndY=67.3588 EndZ=0
    g3: LineSegment StartX=-180.232 StartY=67.3588 StartZ=0 EndX=-180.232 EndY=56.0891 EndZ=0
  constraints (10):
    c: Coincident(g1,g0)
    c: Coincident(g2,g1)
    c: Coincident(g3,g2)
    c: Coincident(g3,g0)
    c: Parallel(g1,g-5)
    c: Perpendicular(g-3,g0)
    c: Parallel(g2,g-6)
    c: Parallel(g3,g-4)
    c: Coincident(g0,g-5)
    c: Coincident(g2,g-6)
FEATURE [Part::Extrusion] Extrude008  label="Extrude buco oled"
  Base = -> Sketch012
  Dir = (0,-1,2e-16)
  DirMode = 2
  FaceMakerClass = Part::FaceMakerBullseye
  FaceMakerMode = 3
  LengthFwd = 12.8
  LengthRev = 0
  Solid = true
  Symmetric = true
FEATURE [Sketcher::SketchObject] Sketch013  label="buco pompa"
  ArcFitTolerance = 1e-06
  AttachmentSupport = -> [XZ_Plane]
  ExternalGeometry = -> [Sketch]
  FullyConstrained = true
  MakeInternals = false
  MapMode = 5
  Placement = pos=(0,0,0) rot=(1,0,0;1.5708rad)
  sketch-geometry (8):
    g0: LineSegment StartX=-82.8 StartY=-10.4 StartZ=0 EndX=-82.8 EndY=-9.6 EndZ=0
    g1: LineSegment StartX=-82.8 StartY=-9.6 StartZ=0 EndX=-67.9 EndY=-9.6 EndZ=0
    g2: LineSegment StartX=-67.9 StartY=-9.6 StartZ=0 EndX=-67.9 EndY=6 EndZ=0
    g3: LineSegment StartX=-67.9 StartY=6 StartZ=0 EndX=-65.9 EndY=6 EndZ=0
    g4: LineSegment StartX=-65.9 StartY=6 StartZ=0 EndX=-65.9 EndY=-1.7 EndZ=0
    g5: LineSegment StartX=-65.9 StartY=-1.7 StartZ=0 EndX=-57.2 EndY=-1.7 EndZ=0
    g6: LineSegment StartX=-57.2 StartY=-1.7 StartZ=0 EndX=-57.2 EndY=-10.4 EndZ=0
    g7: LineSegment StartX=-57.2 StartY=-10.4 StartZ=0 EndX=-82.8 EndY=-10.4 EndZ=0
  constraints (22):
    c: Vertical(g0)
    c: Coincident(g1,g0)
    c: Horizontal(g1)
    c: Coincident(g2,g1)
    c: Vertical(g2)
    c: Coincident(g3,g2)
    c: Horizontal(g3)
    c: Coincident(g4,g3)
    c: Vertical(g4)
    c: Coincident(g5,g4)
    c: Horizontal(g5)
    c: Coincident(g6,g5)
    c: Vertical(g6)
    c: Coincident(g7,g6)
    c: Coincident(g7,g0)
    c: DistanceY(g0,g0) = 0.8
    c: DistanceY(g6,g6) = 8.7
    c: DistanceX(g1,g1) = 14.9
    c: DistanceX(g3,g3) = 2
    c: Coincident(g0,g-4)
    c: DistanceY(g2,g-6) = 0
    c: Coincident(g6,g-5)
FEATURE [Part::Extrusion] Extrude009  label="Extrude buco pompa"
  Base = -> Sketch013
  Dir = (0,-1,2e-16)
  DirMode = 2
  FaceMakerClass = Part::FaceMakerBullseye
  FaceMakerMode = 3
  LengthFwd = 13.2
  LengthRev = 0
  Solid = true
  Symmetric = true
FEATURE [Sketcher::SketchObject] Sketch014  label="buco frontale"
  ArcFitTolerance = 1e-06
  AttachmentSupport = -> [XZ_Plane]
  ExternalGeometry = -> [Sketch]
  FullyConstrained = true
  MakeInternals = false
  MapMode = 5
  Placement = pos=(0,0,0) rot=(1,0,0;1.5708rad)
  sketch-geometry (10):
    g0: LineSegment StartX=0 StartY=0 StartZ=0 EndX=0 EndY=24.671 EndZ=0
    g1: LineSegment StartX=0 StartY=24.671 StartZ=0 EndX=-4 EndY=24.671 EndZ=0
    g2: LineSegment StartX=-4 StartY=24.671 StartZ=0 EndX=-4 EndY=16 EndZ=0
    g3: LineSegment StartX=-4 StartY=16 StartZ=0 EndX=-2.4 EndY=16 EndZ=0
    g4: LineSegment StartX=-2.4 StartY=16 StartZ=0 EndX=-2.4 EndY=10 EndZ=0
    g5: LineSegment StartX=-2.4 StartY=10 StartZ=0 EndX=-12 EndY=10 EndZ=0
    g6: LineSegment StartX=-12 StartY=10 StartZ=0 EndX=-12 EndY=6 EndZ=0
    g7: LineSegment StartX=-12 StartY=6 StartZ=0 EndX=-2.4 EndY=6 EndZ=0
    g8: LineSegment StartX=-2.4 StartY=6 StartZ=0 EndX=-2.4 EndY=0 EndZ=0
    g9: LineSegment StartX=-2.4 StartY=0 StartZ=0 EndX=0 EndY=0 EndZ=0
  constraints (29):
    c: Vertical(g0)
    c: Coincident(g1,g0)
    c: Horizontal(g1)
    c: Coincident(g2,g1)
    c: Vertical(g2)
    c: Coincident(g3,g2)
    c: Horizontal(g3)
    c: Coincident(g4,g3)
    c: Vertical(g4)
    c: Coincident(g5,g4)
    c: Horizontal(g5)
    c: Coincident(g6,g5)
    c: Vertical(g6)
    c: Coincident(g7,g6)
    c: Coincident(g8,g7)
    c: Vertical(g8)
    c: Coincident(g9,g8)
    c: Coincident(g9,g0)
    c: Horizontal(g9)
    c: DistanceY(g0,g0) = 24.671
    c: Horizontal(g7)
    c: DistanceY(g6,g6) = 4
    c: DistanceY(g4,g4) = 6
    c: DistanceX(g9,g9) = 2.4
    c: Coincident(g0,g-1)
    c: DistanceY(g-3,g7) = 0
    c: DistanceX(g8,g4) = 0
    c: DistanceX(g-3,g1) = 0
    c: DistanceX(g6,g-3) = 8
FEATURE [Part::Extrusion] Extrude010  label="Extrude buco frontale"
  Base = -> Sketch014
  Dir = (0,-1,2e-16)
  DirMode = 2
  FaceMakerClass = Part::FaceMakerBullseye
  FaceMakerMode = 3
  LengthFwd = 11.2
  LengthRev = 0
  Solid = true
  Symmetric = true
FEATURE [Sketcher::SketchObject] Sketch015  label="guida rail"
  ArcFitTolerance = 1e-06
  AttachmentSupport = -> [XZ_Plane]
  ExternalGeometry = -> [Sketch]
  FullyConstrained = true
  MakeInternals = false
  MapMode = 5
  Placement = pos=(0,0,0) rot=(1,0,0;1.5708rad)
  sketch-geometry (4):
    g0: LineSegment StartX=-100.8 StartY=43.2 StartZ=0 EndX=-44.6 EndY=43.2 EndZ=0
    g1: LineSegment StartX=-44.6 StartY=43.2 StartZ=0 EndX=-44.6 EndY=41.2 EndZ=0
    g2: LineSegment StartX=-44.6 StartY=41.2 StartZ=0 EndX=-100.8 EndY=41.2 EndZ=0
    g3: LineSegment StartX=-100.8 StartY=41.2 StartZ=0 EndX=-100.8 EndY=43.2 EndZ=0
  constraints (9):
    c: Horizontal(g0)
    c: Coincident(g1,g0)
    c: Coincident(g2,g1)
    c: Coincident(g3,g2)
    c: Coincident(g3,g0)
    c: Vertical(g3)
    c: Coincident(g2,g-3)
    c: Coincident(g1,g-3)
    c: Coincident(g0,g-4)
FEATURE [Part::Extrusion] Extrude011  label="Extrude guida rail"
  Base = -> Sketch015
  Dir = (0,-1,2e-16)
  DirMode = 2
  FaceMakerClass = Part::FaceMakerBullseye
  FaceMakerMode = 3
  LengthFwd = 9
  LengthRev = 0
  Solid = true
  Symmetric = true
FEATURE [Sketcher::SketchObject] Sketch016  label="guide per coperture laterali"
  ArcFitTolerance = 1e-06
  AttachmentSupport = -> [XZ_Plane]
  ExternalGeometry = -> [Sketch]
  FullyConstrained = true
  MakeInternals = false
  MapMode = 5
  Placement = pos=(0,0,0) rot=(1,0,0;1.5708rad)
  sketch-geometry (14):
    g0: Circle CenterX=-5.6 CenterY=7.6 CenterZ=0 NormalX=0 NormalY=0 NormalZ=1 AngleXU=0 Radius=1.6
    g1: Circle CenterX=-5.6 CenterY=7.6 CenterZ=0 NormalX=0 NormalY=0 NormalZ=1 AngleXU=0 Radius=4
    g2: Circle CenterX=-5.6 CenterY=34.8 CenterZ=0 NormalX=0 NormalY=0 NormalZ=1 AngleXU=0 Radius=1.6
    g3: Circle CenterX=-5.6 CenterY=34.8 CenterZ=0 NormalX=0 NormalY=0 NormalZ=1 AngleXU=0 Radius=4
    g4: Circle CenterX=-184.08 CenterY=34.8 CenterZ=0 NormalX=0 NormalY=0 NormalZ=1 AngleXU=0 Radius=1.6
    g5: Circle CenterX=-184.08 CenterY=34.8 CenterZ=0 NormalX=0 NormalY=0 NormalZ=1 AngleXU=0 Radius=4
    g6: Circle CenterX=-179.305 CenterY=-76.8316 CenterZ=0 NormalX=0 NormalY=0 NormalZ=1 AngleXU=0 Radius=1.6
    g7: Circle CenterX=-179.305 CenterY=-76.8316 CenterZ=0 NormalX=0 NormalY=0 NormalZ=1 AngleXU=0 Radius=4
    g8: Circle CenterX=-213.443 CenterY=-76.8316 CenterZ=0 NormalX=0 NormalY=0 NormalZ=1 AngleXU=0 Radius=1.6
    g9: Circle CenterX=-213.443 CenterY=-76.8316 CenterZ=0 NormalX=0 NormalY=0 NormalZ=1 AngleXU=0 Radius=4
    g10: Circle CenterX=-78.51 CenterY=7.6 CenterZ=0 NormalX=0 NormalY=0 NormalZ=1 AngleXU=0 Radius=1.6
    g11: Circle CenterX=-78.51 CenterY=7.6 CenterZ=0 NormalX=0 NormalY=0 NormalZ=1 AngleXU=0 Radius=4
    g12: Circle CenterX=-78.51 CenterY=34.8 CenterZ=0 NormalX=0 NormalY=0 NormalZ=1 AngleXU=0 Radius=1.6
    g13: Circle CenterX=-78.51 CenterY=34.8 CenterZ=0 NormalX=0 NormalY=0 NormalZ=1 AngleXU=0 Radius=4
  constraints (35):
    c: Diameter(g0) = 3.2
    c: Diameter(g1) = 8
    c: Coincident(g0,g1)
    c: Diameter(g2) = 3.2
    c: Diameter(g3) = 8
    c: Coincident(g3,g2)
    c: Tangent(g2,g-7)
    c: Diameter(g4) = 3.2
    c: Diameter(g5) = 8
    c: Coincident(g5,g4)
    c: Tangent(g4,g-7)
    c: Tangent(g4,g-8)
    c: Diameter(g6) = 3.2
    c: Diameter(g7) = 8
    c: Coincident(g7,g6)
    c: Tangent(g6,g-9)
    c: Tangent(g6,g-10)
    c: Diameter(g8) = 3.2
    c: Diameter(g9) = 8
    c: Coincident(g9,g8)
    c: Tangent(g8,g-10)
    c: Tangent(g8,g-11)
    c: Diameter(g10) = 3.2
    c: Diameter(g11) = 8
    c: Diameter(g12) = 3.2
    c: Diameter(g13) = 8
    c: Coincident(g12,g13)
    c: Coincident(g10,g11)
    c: Tangent(g12,g-7)
    c: DistanceX(g12,g10) = 0
    c: Tangent(g2,g-6)
    c: Tangent(g0,g-6)
    c: Tangent(g0,g-3)
    c: Tangent(g10,g-3)
    c: Tangent(g10,g-4)
FEATURE [Part::Extrusion] Extrude012  label="extrude guide per coperture laterali"
  Base = -> Sketch016
  Dir = (0,-1,2e-16)
  DirMode = 2
  FaceMakerClass = Part::FaceMakerBullseye
  FaceMakerMode = 3
  LengthFwd = 25.2
  LengthRev = 0
  Solid = true
  Symmetric = true
FEATURE [Sketcher::SketchObject] Sketch017  label="supporto CAM"
  ArcFitTolerance = 1e-06
  AttachmentSupport = -> [XZ_Plane]
  ExternalGeometry = -> [Sketch]
  FullyConstrained = true
  MakeInternals = false
  MapMode = 5
  Placement = pos=(0,0,0) rot=(1,0,0;1.5708rad)
  sketch-geometry (6):
    g0: LineSegment StartX=-2.4 StartY=48 StartZ=0 EndX=-2.4 EndY=41.2 EndZ=0
    g1: LineSegment StartX=-2.4 StartY=48 StartZ=0 EndX=-34 EndY=48 EndZ=0
    g2: LineSegment StartX=-34 StartY=48 StartZ=0 EndX=-34 EndY=46.72 EndZ=0
    g3: LineSegment StartX=-34 StartY=46.72 StartZ=0 EndX=-36 EndY=46.72 EndZ=0
    g4: LineSegment StartX=-36 StartY=46.72 StartZ=0 EndX=-36 EndY=41.2 EndZ=0
    g5: LineSegment StartX=-36 StartY=41.2 StartZ=0 EndX=-2.4 EndY=41.2 EndZ=0
  constraints (15):
    c: Coincident(g1,g0)
    c: Horizontal(g1)
    c: Coincident(g2,g1)
    c: Vertical(g2)
    c: Coincident(g3,g2)
    c: Horizontal(g3)
    c: Coincident(g4,g3)
    c: Coincident(g5,g4)
    c: DistanceX(g1,g0) = 31.6
    c: Coincident(g5,g0)
    c: Vertical(g4)
    c: DistanceY(g2,g1) = 1.28
    c: Coincident(g0,g-3)
    c: Coincident(g0,g-3)
    c: Coincident(g4,g-4)
FEATURE [Part::Extrusion] Extrude013  label="Extrude supporto CAM"
  Base = -> Sketch017
  Dir = (0,-1,2e-16)
  DirMode = 2
  FaceMakerClass = Part::FaceMakerBullseye
  FaceMakerMode = 3
  LengthFwd = 17.8
  LengthRev = 0
  Solid = true
  Symmetric = true
FEATURE [Sketcher::SketchObject] Sketch018  label="Scavo CAM"
  ArcFitTolerance = 1e-06
  AttachmentSupport = -> [YZ_Plane]
  ExternalGeometry = -> [Sketch]
  FullyConstrained = true
  MakeInternals = false
  MapMode = 5
  Placement = pos=(0,0,0) rot=(0.57735,0.57735,0.57735;2.0944rad)
  sketch-geometry (4):
    g0: LineSegment StartX=-7.73 StartY=48 StartZ=0 EndX=7.73 EndY=48 EndZ=0
    g1: LineSegment [constr] StartX=1.07e-14 StartY=48 StartZ=0 EndX=0 EndY=43.5155 EndZ=0
    g2: ArcOfCircle CenterX=9e-15 CenterY=52.42 CenterZ=0 NormalX=0 NormalY=0 NormalZ=1 AngleXU=0 Radius=8.90445 StartAngle=3.66102 EndAngle=5.76376
    g3: Circle [constr] CenterX=9e-15 CenterY=52.42 CenterZ=0 NormalX=0 NormalY=0 NormalZ=1 AngleXU=0 Radius=8.9
  constraints (13):
    c: Horizontal(g0)
    c: DistanceY(g-3,g0) = 0
    c: DistanceX(g0,g0) = 15.46
    c: DistanceX(g0,g-3) = 7.73
    c: DistanceX(g-3) = 0
    c: Coincident(g1,g-3)
    c: PointOnObject(g1,g-2)
    c: Coincident(g2,g0)
    c: Coincident(g2,g0)
    c: PointOnObject(g1,g2)
    c: Diameter(g3) = 17.8
    c: DistanceY(g1,g3) = 4.42
    c: Coincident(g2,g3)
FEATURE [Part::Extrusion] Extrude014  label="Extrude Scavo CAM"
  Base = -> Sketch018
  Dir = (1,0,0)
  DirMode = 2
  FaceMakerClass = Part::FaceMakerBullseye
  FaceMakerMode = 3
  LengthFwd = -34
  LengthRev = 0
  Solid = true
  Symmetric = false
FEATURE [Sketcher::SketchObject] Sketch019  label="scavo rumble"
  ArcFitTolerance = 1e-06
  AttachmentSupport = -> [XZ_Plane]
  ExternalGeometry = -> [Sketch]
  FullyConstrained = true
  MakeInternals = false
  MapMode = 5
  Placement = pos=(0,0,0) rot=(1,0,0;1.5708rad)
  sketch-geometry (6):
    g0: LineSegment StartX=-168.716 StartY=-37.1227 StartZ=0 EndX=-163.58 EndY=-38.7914 EndZ=0
    g1: LineSegment StartX=-163.58 StartY=-38.7914 StartZ=0 EndX=-170.687 EndY=-60.6657 EndZ=0
    g2: LineSegment StartX=-170.687 StartY=-60.6657 StartZ=0 EndX=-175.823 EndY=-58.997 EndZ=0
    g3: LineSegment StartX=-175.823 StartY=-58.997 StartZ=0 EndX=-168.716 EndY=-37.1227 EndZ=0
    g4: LineSegment [constr] StartX=-145.51 StartY=22 StartZ=0 EndX=-165.102 EndY=-38.297 EndZ=0
    g5: LineSegment [constr] StartX=-163.58 StartY=-38.7914 StartZ=0 EndX=-165.102 EndY=-38.297 EndZ=0
  constraints (17):
    c: Coincident(g1,g0)
    c: Coincident(g2,g1)
    c: Coincident(g3,g2)
    c: Coincident(g3,g0)
    c: Parallel(g3,g-3)
    c: Parallel(g3,g1)
    c: Perpendicular(g3,g0)
    c: Perpendicular(g2,g3)
    c: Distance(g2,g0) = 23
    c: Parallel(g4,g-3)
    c: Distance(g4) = 63.4
    c: Coincident(g4,g-3)
    c: Parallel(g5,g0)
    c: Coincident(g5,g0)
    c: Coincident(g5,g4)
    c: Distance(g4,g0) = 3.8
    c: Distance(g4,g0) = 1.6
FEATURE [Part::Extrusion] Extrude015  label="scavo rumble001"
  Base = -> Sketch019
  Dir = (0,-1,2e-16)
  DirMode = 2
  FaceMakerClass = Part::FaceMakerBullseye
  FaceMakerMode = 3
  LengthFwd = 21
  LengthRev = 0
  Solid = true
  Symmetric = true
FEATURE [Sketcher::SketchObject] Sketch020  label="fermo rumble"
  ArcFitTolerance = 1e-06
  AttachmentSupport = -> [XZ_Plane]
  ExternalGeometry = -> [Sketch019,Sketch]
  FullyConstrained = true
  MakeInternals = false
  MapMode = 5
  Placement = pos=(0,0,0) rot=(1,0,0;1.5708rad)
  sketch-geometry (16):
    g0: LineSegment [constr] StartX=-170.849 StartY=-55.9866 StartZ=0 EndX=-172.209 EndY=-60.1713 EndZ=0
    g1: LineSegment [constr] StartX=-172.209 StartY=-60.1713 StartZ=0 EndX=-170.687 EndY=-60.6657 EndZ=0
    g2: LineSegment StartX=-172.262 StartY=-53.2145 StartZ=0 EndX=-170.17 EndY=-53.8943 EndZ=0
    g3: LineSegment StartX=-170.17 StartY=-53.8943 StartZ=0 EndX=-170.849 EndY=-55.9866 EndZ=0
    g4: LineSegment StartX=-170.849 StartY=-55.9866 StartZ=0 EndX=-172.942 EndY=-55.3068 EndZ=0
    g5: LineSegment StartX=-172.942 StartY=-55.3068 StartZ=0 EndX=-172.262 EndY=-53.2145 EndZ=0
    g6: LineSegment StartX=-171.767 StartY=-51.6928 StartZ=0 EndX=-168.344 EndY=-52.8052 EndZ=0
    g7: LineSegment StartX=-168.344 StartY=-52.8052 StartZ=0 EndX=-169.951 EndY=-57.7507 EndZ=0
    g8: LineSegment StartX=-169.951 StartY=-57.7507 StartZ=0 EndX=-173.374 EndY=-56.6383 EndZ=0
    g9: LineSegment StartX=-174.402 StartY=-54.6222 StartZ=0 EndX=-173.784 EndY=-52.72 EndZ=0
    g10: LineSegment [constr] StartX=-173.784 StartY=-52.72 StartZ=0 EndX=-173.289 EndY=-51.1984 EndZ=0
    g11: LineSegment [constr] StartX=-173.289 StartY=-51.1984 StartZ=0 EndX=-171.767 EndY=-51.6928 EndZ=0
    g12: ArcOfCircle CenterX=-172.88 CenterY=-55.1166 CenterZ=0 NormalX=0 NormalY=0 NormalZ=1 AngleXU=0 Radius=1.6 StartAngle=2.82743 EndAngle=4.39823
    g13: GeomPoint [constr] X=-174.896 Y=-56.1438 Z=0
    g14: ArcOfCircle CenterX=-172.262 CenterY=-53.2145 CenterZ=0 NormalX=0 NormalY=0 NormalZ=1 AngleXU=0 Radius=1.6 StartAngle=1.25664 EndAngle=2.82743
    g15: GeomPoint [constr] X=-173.289 Y=-51.1984 Z=0
  constraints (42):
    c: Parallel(g0,g-4)
    c: Distance(g0) = 4.4
    c: Coincident(g1,g0)
    c: Perpendicular(g0,g1)
    c: Distance(g1) = 1.6
    c: Coincident(g1,g-5)
    c: Coincident(g3,g2)
    c: Coincident(g4,g3)
    c: Coincident(g5,g4)
    c: Coincident(g5,g2)
    c: Parallel(g3,g-4)
    c: Parallel(g3,g5)
    c: Perpendicular(g2,g3)
    c: Parallel(g4,g2)
    c: Distance(g2) = 2.2
    c: Distance(g3) = 2.2
    c: Coincident(g7,g6)
    c: Coincident(g8,g7)
    c: Parallel(g7,g-4)
    c: Parallel(g7,g9)
    c: Perpendicular(g6,g7)
    c: Parallel(g6,g8)
    c: Distance(g6,g15) = 5.2
    c: Distance(g7) = 5.2
    c: Coincident(g11,g10)
    c: Parallel(g10,g9)
    c: Parallel(g11,g6)
    c: Distance(g10) = 1.6
    c: Distance(g11) = 1.6
    c: Coincident(g10,g15)
    c: Distance(g11,g2) = 1.6
    c: Distance(g2,g10) = 1.6
    c: PointOnObject(g13,g8)
    c: PointOnObject(g13,g9)
    c: Tangent(g8,g12) = 1.5708
    c: Tangent(g9,g12) = 1.5708
    c: PointOnObject(g15,g9)
    c: Tangent(g6,g14) = 1.5708
    c: Tangent(g9,g14) = 1.5708
    c: Equal(g12,g14)
    c: Coincident(g6,g11)
    c: Coincident(g3,g0)
FEATURE [Part::Extrusion] Extrude016  label="Extrude fermo rumble"
  Base = -> Sketch020
  Dir = (0,-1,2e-16)
  DirMode = 2
  FaceMakerClass = Part::FaceMakerBullseye
  FaceMakerMode = 3
  LengthFwd = 25.2
  LengthRev = 0
  Solid = true
  Symmetric = true
FEATURE [Sketcher::SketchObject] Sketch021  label="perno fermo rumble001"
  ArcFitTolerance = 1e-06
  AttachmentSupport = -> [XZ_Plane001]
  FullyConstrained = true
  MakeInternals = false
  MapMode = 5
  Placement = pos=(0,0,0) rot=(1,0,0;1.5708rad)
  sketch-geometry (16):
    g0: LineSegment StartX=0 StartY=0.45 StartZ=0 EndX=0 EndY=1.55 EndZ=0
    g1: LineSegment StartX=0.45 StartY=2 StartZ=0 EndX=1.55 EndY=2 EndZ=0
    g2: LineSegment StartX=2 StartY=1.55 StartZ=0 EndX=2 EndY=0.45 EndZ=0
    g3: LineSegment StartX=1.55 StartY=0 StartZ=0 EndX=0.45 EndY=0 EndZ=0
    g4: ArcOfCircle [constr] CenterX=0.45 CenterY=1.55 CenterZ=0 NormalX=0 NormalY=0 NormalZ=1 AngleXU=0 Radius=0.45 StartAngle=1.5708 EndAngle=3.14159
    g5: GeomPoint [constr] X=0 Y=2 Z=0
    g6: LineSegment StartX=0.45 StartY=2 StartZ=0 EndX=0 EndY=1.55 EndZ=0
    g7: ArcOfCircle [constr] CenterX=1.55 CenterY=1.55 CenterZ=0 NormalX=0 NormalY=0 NormalZ=1 AngleXU=0 Radius=0.45 StartAngle=0 EndAngle=1.5708
    g8: GeomPoint [constr] X=2 Y=2 Z=0
    g9: LineSegment StartX=2 StartY=1.55 StartZ=0 EndX=1.55 EndY=2 EndZ=0
    g10: ArcOfCircle [constr] CenterX=1.55 CenterY=0.45 CenterZ=0 NormalX=0 NormalY=0 NormalZ=1 AngleXU=0 Radius=0.45 StartAngle=4.71239 EndAngle=6.28319
    g11: GeomPoint [constr] X=2 Y=0 Z=0
    g12: LineSegment StartX=1.55 StartY=0 StartZ=0 EndX=2 EndY=0.45 EndZ=0
    g13: ArcOfCircle [constr] CenterX=0.45 CenterY=0.45 CenterZ=0 NormalX=0 NormalY=0 NormalZ=1 AngleXU=0 Radius=0.45 StartAngle=3.14159 EndAngle=4.71239
    g14: GeomPoint [constr] X=0 Y=0 Z=0
    g15: LineSegment StartX=0 StartY=0.45 StartZ=0 EndX=0.45 EndY=0 EndZ=0
  constraints (35):
    c: Coincident(g14,g-1)
    c: PointOnObject(g5,g-2)
    c: Horizontal(g1)
    c: Vertical(g2)
    c: Horizontal(g3)
    c: DistanceX(g5,g8) = 2
    c: DistanceY(g11,g8) = 2
    c: PointOnObject(g5,g0)
    c: PointOnObject(g5,g1)
    c: Tangent(g0,g4) = 1.5708
    c: Tangent(g1,g4) = 1.5708
    c: Coincident(g6,g0)
    c: Coincident(g6,g1)
    c: PointOnObject(g8,g2)
    c: PointOnObject(g8,g1)
    c: Tangent(g2,g7) = 1.5708
    c: Tangent(g1,g7) = 1.5708
    c: Coincident(g9,g2)
    c: Coincident(g9,g1)
    c: PointOnObject(g11,g2)
    c: PointOnObject(g11,g3)
    c: Tangent(g2,g10) = 1.5708
    c: Tangent(g3,g10) = 1.5708
    c: Coincident(g12,g2)
    c: Coincident(g12,g3)
    c: PointOnObject(g14,g0)
    c: PointOnObject(g14,g3)
    c: Tangent(g0,g13) = 1.5708
    c: Tangent(g3,g13) = 1.5708
    c: Coincident(g15,g0)
    c: Coincident(g15,g3)
    c: Equal(g6,g9)
    c: Equal(g9,g12)
    c: Equal(g12,g15)
    c: DistanceX(g14,g3) = 0.45
FEATURE [Sketcher::SketchObject] Sketch022  label="fori per M3x5(OD)x6(L)"
  ArcFitTolerance = 1e-06
  AttachmentSupport = -> [XZ_Plane]
  ExternalGeometry = -> [Sketch016]
  FullyConstrained = true
  MakeInternals = false
  MapMode = 5
  Placement = pos=(0,0,0) rot=(1,0,0;1.5708rad)
  sketch-geometry (7):
    g0: Circle CenterX=-5.6 CenterY=34.8 CenterZ=0 NormalX=0 NormalY=0 NormalZ=1 AngleXU=0 Radius=2.5
    g1: Circle CenterX=-5.6 CenterY=7.6 CenterZ=0 NormalX=0 NormalY=0 NormalZ=1 AngleXU=0 Radius=2.5
    g2: Circle CenterX=-78.51 CenterY=34.8 CenterZ=0 NormalX=0 NormalY=0 NormalZ=1 AngleXU=0 Radius=2.5
    g3: Circle CenterX=-78.51 CenterY=7.6 CenterZ=0 NormalX=0 NormalY=0 NormalZ=1 AngleXU=0 Radius=2.5
    g4: Circle CenterX=-184.08 CenterY=34.8 CenterZ=0 NormalX=0 NormalY=0 NormalZ=1 AngleXU=0 Radius=2.5
    g5: Circle CenterX=-179.305 CenterY=-76.8316 CenterZ=0 NormalX=0 NormalY=0 NormalZ=1 AngleXU=0 Radius=2.5
    g6: Circle CenterX=-213.443 CenterY=-76.8316 CenterZ=0 NormalX=0 NormalY=0 NormalZ=1 AngleXU=0 Radius=2.5
  constraints (14):
    c: Diameter(g0) = 5
    c: Diameter(g1) = 5
    c: Diameter(g2) = 5
    c: Diameter(g3) = 5
    c: Diameter(g4) = 5
    c: Diameter(g5) = 5
    c: Diameter(g6) = 5
    c: Coincident(g0,g-8)
    c: Coincident(g1,g-9)
    c: Coincident(g2,g-6)
    c: Coincident(g3,g-7)
    c: Coincident(g4,g-5)
    c: Coincident(g5,g-4)
    c: Coincident(g6,g-3)
FEATURE [Part::Extrusion] Extrude018  label="Extrude fori M3x5x6 - dx"
  Base = -> Sketch022
  Dir = (0,-1,2e-16)
  DirMode = 2
  FaceMakerClass = Part::FaceMakerBullseye
  FaceMakerMode = 3
  LengthFwd = 6.2
  LengthRev = 0
  Placement = pos=(0,-9.5,0) rot=(0,0,1;0rad)
  Solid = true
  Symmetric = true
FEATURE [Part::Extrusion] Extrude019  label="Extrude fori M3x5x6 - sx"
  Base = -> Sketch022
  Dir = (0,-1,2e-16)
  DirMode = 2
  FaceMakerClass = Part::FaceMakerBullseye
  FaceMakerMode = 3
  LengthFwd = 6.2
  LengthRev = 0
  Placement = pos=(0,9.5,0) rot=(0,0,1;0rad)
  Solid = true
  Symmetric = true
FEATURE [Sketcher::SketchObject] Sketch023  label="foro anteriore M3x5x6"
  ArcFitTolerance = 1e-06
  AttachmentSupport = -> [YZ_Plane]
  FullyConstrained = true
  MakeInternals = false
  MapMode = 5
  Placement = pos=(0,0,0) rot=(0.57735,0.57735,0.57735;2.0944rad)
  sketch-geometry (2):
    g0: LineSegment [constr] StartX=0 StartY=0 StartZ=0 EndX=0 EndY=38.6 EndZ=0
    g1: Circle CenterX=0 CenterY=38.6 CenterZ=0 NormalX=0 NormalY=0 NormalZ=1 AngleXU=0 Radius=2.5
  constraints (5):
    c: Coincident(g0,g-1)
    c: PointOnObject(g0,g-2)
    c: DistanceY(g0,g0) = 38.6
    c: Diameter(g1) = 5
    c: Coincident(g1,g0)
FEATURE [Part::Extrusion] Extrude020  label="Extrude foro anteriore M3x5x6"
  Base = -> Sketch023
  Dir = (1,0,0)
  DirMode = 2
  FaceMakerClass = Part::FaceMakerBullseye
  FaceMakerMode = 3
  LengthFwd = -6.2
  LengthRev = 0
  Solid = true
  Symmetric = false
FEATURE [Sketcher::SketchObject] Sketch024  label="fori per viti frontale"
  ArcFitTolerance = 1e-06
  AttachmentSupport = -> [YZ_Plane]
  FullyConstrained = true
  MakeInternals = false
  MapMode = 5
  Placement = pos=(0,0,0) rot=(0.57735,0.57735,0.57735;2.0944rad)
  sketch-geometry (9):
    g0: LineSegment [constr] StartX=-10.3 StartY=30.721 StartZ=0 EndX=10.3 EndY=30.721 EndZ=0
    g1: LineSegment [constr] StartX=10.3 StartY=30.721 StartZ=0 EndX=10.3 EndY=10.121 EndZ=0
    g2: LineSegment [constr] StartX=10.3 StartY=10.121 StartZ=0 EndX=-10.3 EndY=10.121 EndZ=0
    g3: LineSegment [constr] StartX=-10.3 StartY=10.121 StartZ=0 EndX=-10.3 EndY=30.721 EndZ=0
    g4: LineSegment [constr] StartX=0 StartY=0 StartZ=0 EndX=0 EndY=10.121 EndZ=0
    g5: Circle CenterX=-10.3 CenterY=30.721 CenterZ=0 NormalX=0 NormalY=0 NormalZ=1 AngleXU=0 Radius=2
    g6: Circle CenterX=10.3 CenterY=30.721 CenterZ=0 NormalX=0 NormalY=0 NormalZ=1 AngleXU=0 Radius=2
    g7: Circle CenterX=-10.3 CenterY=10.121 CenterZ=0 NormalX=0 NormalY=0 NormalZ=1 AngleXU=0 Radius=2
    g8: Circle CenterX=10.3 CenterY=10.121 CenterZ=0 NormalX=0 NormalY=0 NormalZ=1 AngleXU=0 Radius=2
  constraints (22):
    c: Horizontal(g0)
    c: Coincident(g1,g0)
    c: Vertical(g1)
    c: Coincident(g2,g1)
    c: Horizontal(g2)
    c: Coincident(g3,g2)
    c: Coincident(g3,g0)
    c: Vertical(g3)
    c: DistanceX(g0,g0) = 20.6
    c: DistanceY(g3,g3) = 20.6
    c: Coincident(g4,g-1)
    c: PointOnObject(g4,g-2)
    c: DistanceY(g4,g4) = 10.121
    c: Symmetric(g2,g2,g4)
    c: Diameter(g5) = 4
    c: Diameter(g6) = 4
    c: Diameter(g7) = 4
    c: Diameter(g8) = 4
    c: Coincident(g5,g0)
    c: Coincident(g6,g0)
    c: Coincident(g7,g2)
    c: Coincident(g8,g1)
FEATURE [Part::Extrusion] Extrude021  label="Extrude fori per viti frontale"
  Base = -> Sketch024
  Dir = (1,0,0)
  DirMode = 2
  FaceMakerClass = Part::FaceMakerBullseye
  FaceMakerMode = 3
  LengthFwd = -2.4
  LengthRev = 0
  Solid = true
  Symmetric = false
FEATURE [Sketcher::SketchObject] Sketch025  label="foro per filo CAM"
  ArcFitTolerance = 1e-06
  AttachmentSupport = -> [XZ_Plane]
  ExternalGeometry = -> [Sketch]
  FullyConstrained = true
  MakeInternals = false
  MapMode = 5
  Placement = pos=(0,0,0) rot=(1,0,0;1.5708rad)
  sketch-geometry (4):
    g0: LineSegment StartX=-44.6 StartY=41.2 StartZ=0 EndX=-44.6 EndY=36.4 EndZ=0
    g1: LineSegment StartX=-44.6 StartY=36.4 StartZ=0 EndX=-54.6 EndY=36.4 EndZ=0
    g2: LineSegment StartX=-54.6 StartY=36.4 StartZ=0 EndX=-50.4 EndY=41.2 EndZ=0
    g3: LineSegment StartX=-50.4 StartY=41.2 StartZ=0 EndX=-44.6 EndY=41.2 EndZ=0
  constraints (11):
    c: Vertical(g0)
    c: Coincident(g1,g0)
    c: Horizontal(g1)
    c: Coincident(g2,g1)
    c: Coincident(g3,g2)
    c: Coincident(g3,g0)
    c: Horizontal(g3)
    c: Coincident(g0,g-3)
    c: DistanceY(g0,g-4) = 0
    c: DistanceX(g3,g3) = 5.8
    c: DistanceX(g1,g1) = 10
FEATURE [Part::Extrusion] Extrude022  label="Extrude foro per filo CAM dx"
  Base = -> Sketch025
  Dir = (0,-1,2e-16)
  DirMode = 2
  FaceMakerClass = Part::FaceMakerBullseye
  FaceMakerMode = 3
  LengthFwd = 4.9
  LengthRev = 0
  Placement = pos=(0,6.95,0) rot=(0,0,1;0rad)
  Solid = true
  Symmetric = true
FEATURE [Part::Extrusion] Extrude023  label="Extrude foro per filo CAM sx"
  Base = -> Sketch025
  Dir = (0,-1,2e-16)
  DirMode = 2
  FaceMakerClass = Part::FaceMakerBullseye
  FaceMakerMode = 3
  LengthFwd = 4.9
  LengthRev = 0
  Placement = pos=(0,-6.95,0) rot=(0,0,1;0rad)
  Solid = true
  Symmetric = true
FEATURE [Sketcher::SketchObject] Sketch026  label="foro sotto anteriore M3x5x6"
  ArcFitTolerance = 1e-06
  AttachmentSupport = -> [XY_Plane]
  FullyConstrained = true
  MakeInternals = false
  MapMode = 5
  sketch-geometry (2):
    g0: LineSegment [constr] StartX=0 StartY=0 StartZ=0 EndX=-16.5 EndY=0 EndZ=0
    g1: Circle CenterX=-16.5 CenterY=0 CenterZ=0 NormalX=0 NormalY=0 NormalZ=1 AngleXU=0 Radius=2.5
  constraints (5):
    c: Distance(g0) = 16.5
    c: Coincident(g0,g-1)
    c: PointOnObject(g0,g-1)
    c: Diameter(g1) = 5
    c: Coincident(g0,g1)
FEATURE [Sketcher::SketchObject] Sketch027  label="foro sotto posteriore M3x5x6"
  ArcFitTolerance = 1e-06
  AttachmentSupport = -> [XY_Plane]
  ExternalGeometry = -> [Sketch]
  FullyConstrained = true
  MakeInternals = false
  MapMode = 5
  sketch-geometry (2):
    g0: LineSegment [constr] StartX=-82.8 StartY=2e-16 StartZ=0 EndX=-71.3 EndY=2e-16 EndZ=0
    g1: Circle CenterX=-71.3 CenterY=2e-16 CenterZ=0 NormalX=0 NormalY=0 NormalZ=1 AngleXU=0 Radius=2.5
  constraints (5):
    c: Distance(g0) = 11.5
    c: Coincident(g0,g-3)
    c: PointOnObject(g0,g-3)
    c: Diameter(g1) = 5
    c: Coincident(g1,g0)
FEATURE [Sketcher::SketchObject] Sketch029  label="fori sotto impugnatura"
  ArcFitTolerance = 1e-06
  AttachmentSupport = -> [XY_Plane]
  ExternalGeometry = -> [Sketch]
  FullyConstrained = true
  MakeInternals = false
  MapMode = 5
  sketch-geometry (15):
    g0: LineSegment [constr] StartX=-175.232 StartY=-1.83e-14 StartZ=0 EndX=-191.232 EndY=0 EndZ=0
    g1: Circle CenterX=-191.232 CenterY=0 CenterZ=0 NormalX=0 NormalY=0 NormalZ=1 AngleXU=0 Radius=3.95
    g2: LineSegment [constr] StartX=-175.232 StartY=-1.83e-14 StartZ=0 EndX=-204.275 EndY=0 EndZ=0
    g3: LineSegment StartX=-204.275 StartY=3.525 StartZ=0 EndX=-204.275 EndY=-3.525 EndZ=0
    g4: LineSegment StartX=-205.4 StartY=-4.65 StartZ=0 EndX=-206.65 EndY=-4.65 EndZ=0
    g5: LineSegment StartX=-207.775 StartY=-3.525 StartZ=0 EndX=-207.775 EndY=3.525 EndZ=0
    g6: LineSegment StartX=-206.65 StartY=4.65 StartZ=0 EndX=-205.4 EndY=4.65 EndZ=0
    g7: ArcOfCircle CenterX=-206.65 CenterY=3.525 CenterZ=0 NormalX=0 NormalY=0 NormalZ=1 AngleXU=0 Radius=1.125 StartAngle=1.5708 EndAngle=3.14159
    g8: GeomPoint [constr] X=-207.775 Y=4.65 Z=0
    g9: ArcOfCircle CenterX=-205.4 CenterY=3.525 CenterZ=0 NormalX=0 NormalY=0 NormalZ=1 AngleXU=0 Radius=1.125 StartAngle=0 EndAngle=1.5708
    g10: GeomPoint [constr] X=-204.275 Y=4.65 Z=0
    g11: ArcOfCircle CenterX=-205.4 CenterY=-3.525 CenterZ=0 NormalX=0 NormalY=0 NormalZ=1 AngleXU=0 Radius=1.125 StartAngle=4.71239 EndAngle=6.28319
    g12: GeomPoint [constr] X=-204.275 Y=-4.65 Z=0
    g13: ArcOfCircle CenterX=-206.65 CenterY=-3.525 CenterZ=0 NormalX=0 NormalY=0 NormalZ=1 AngleXU=0 Radius=1.125 StartAngle=3.14159 EndAngle=4.71239
    g14: GeomPoint [constr] X=-207.775 Y=-4.65 Z=0
  constraints (35):
    c: Distance(g0) = 16
    c: Coincident(g0,g-3)
    c: PointOnObject(g0,g-1)
    c: Diameter(g1) = 7.9
    c: Coincident(g1,g0)
    c: Coincident(g2,g0)
    c: PointOnObject(g2,g-1)
    c: Vertical(g3)
    c: Horizontal(g4)
    c: Vertical(g5)
    c: Horizontal(g6)
    c: DistanceY(g12,g10) = 9.3
    c: DistanceX(g8,g10) = 3.5
    c: Symmetric(g10,g12,g2)
    c: PointOnObject(g8,g5)
    c: PointOnObject(g8,g6)
    c: Tangent(g5,g7) = 1.5708
    c: Tangent(g6,g7) = 1.5708
    c: PointOnObject(g10,g3)
    c: PointOnObject(g10,g6)
    c: Tangent(g3,g9) = 1.5708
    c: Tangent(g6,g9) = 1.5708
    c: PointOnObject(g12,g3)
    c: PointOnObject(g12,g4)
    c: Tangent(g3,g11) = 1.5708
    c: Tangent(g4,g11) = 1.5708
    c: PointOnObject(g14,g4)
    c: PointOnObject(g14,g5)
    c: Tangent(g4,g13) = 1.5708
    c: Tangent(g5,g13) = 1.5708
    c: Equal(g7,g9)
    c: Equal(g9,g11)
    c: Equal(g11,g13)
    c: DistanceX(g6,g6) = 1.25
    c: DistanceX(g-5,g5) = 6.8
FEATURE [Sketcher::SketchObject] Sketch030  label="fori superiori per solenoide e oled"
  ArcFitTolerance = 1e-06
  AttachmentSupport = -> [XY_Plane]
  ExternalGeometry = -> [Sketch]
  FullyConstrained = true
  MakeInternals = false
  MapMode = 5
  sketch-geometry (33):
    g0: LineSegment [constr] StartX=-181.6 StartY=1.12e-14 StartZ=0 EndX=-169.91 EndY=0 EndZ=0
    g1: LineSegment [constr] StartX=-169.91 StartY=0 StartZ=0 EndX=-169.91 EndY=-2.6 EndZ=0
    g2: LineSegment [constr] StartX=-169.91 StartY=0 StartZ=0 EndX=-169.91 EndY=2.6 EndZ=0
    g3: LineSegment StartX=-169.91 StartY=4.975 StartZ=0 EndX=-169.91 EndY=8.225 EndZ=0
    g4: LineSegment StartX=-167.535 StartY=10.6 StartZ=0 EndX=-167.285 EndY=10.6 EndZ=0
    g5: LineSegment StartX=-164.91 StartY=8.225 StartZ=0 EndX=-164.91 EndY=4.975 EndZ=0
    g6: LineSegment StartX=-167.285 StartY=2.6 StartZ=0 EndX=-167.535 EndY=2.6 EndZ=0
    g7: LineSegment StartX=-169.91 StartY=-4.975 StartZ=0 EndX=-169.91 EndY=-8.225 EndZ=0
    g8: LineSegment StartX=-167.535 StartY=-10.6 StartZ=0 EndX=-167.285 EndY=-10.6 EndZ=0
    g9: LineSegment StartX=-164.91 StartY=-8.225 StartZ=0 EndX=-164.91 EndY=-4.975 EndZ=0
    g10: LineSegment StartX=-167.285 StartY=-2.6 StartZ=0 EndX=-167.535 EndY=-2.6 EndZ=0
    g11: ArcOfCircle CenterX=-167.535 CenterY=8.225 CenterZ=0 NormalX=0 NormalY=0 NormalZ=1 AngleXU=0 Radius=2.375 StartAngle=1.5708 EndAngle=3.14159
    g12: GeomPoint [constr] X=-169.91 Y=10.6 Z=0
    g13: ArcOfCircle CenterX=-167.285 CenterY=8.225 CenterZ=0 NormalX=0 NormalY=0 NormalZ=1 AngleXU=0 Radius=2.375 StartAngle=0 EndAngle=1.5708
    g14: GeomPoint [constr] X=-164.91 Y=10.6 Z=0
    g15: ArcOfCircle CenterX=-167.285 CenterY=4.975 CenterZ=0 NormalX=0 NormalY=0 NormalZ=1 AngleXU=0 Radius=2.375 StartAngle=4.71239 EndAngle=6.28319
    g16: GeomPoint [constr] X=-164.91 Y=2.6 Z=0
    g17: ArcOfCircle CenterX=-167.535 CenterY=4.975 CenterZ=0 NormalX=0 NormalY=0 NormalZ=1 AngleXU=0 Radius=2.375 StartAngle=3.14159 EndAngle=4.71239
    g18: GeomPoint [constr] X=-169.91 Y=2.6 Z=0
    g19: ArcOfCircle CenterX=-167.535 CenterY=-4.975 CenterZ=0 NormalX=0 NormalY=0 NormalZ=1 AngleXU=0 Radius=2.375 StartAngle=1.5708 EndAngle=3.14159
    g20: GeomPoint [constr] X=-169.91 Y=-2.6 Z=0
    g21: ArcOfCircle CenterX=-167.285 CenterY=-4.975 CenterZ=0 NormalX=0 NormalY=0 NormalZ=1 AngleXU=0 Radius=2.375 StartAngle=0 EndAngle=1.5708
    g22: GeomPoint [constr] X=-164.91 Y=-2.6 Z=0
    g23: ArcOfCircle CenterX=-167.285 CenterY=-8.225 CenterZ=0 NormalX=0 NormalY=0 NormalZ=1 AngleXU=0 Radius=2.375 StartAngle=4.71239 EndAngle=6.28319
    g24: GeomPoint [constr] X=-164.91 Y=-10.6 Z=0
    g25: ArcOfCircle CenterX=-167.535 CenterY=-8.225 CenterZ=0 NormalX=0 NormalY=0 NormalZ=1 AngleXU=0 Radius=2.375 StartAngle=3.14159 EndAngle=4.71239
    g26: GeomPoint [constr] X=-169.91 Y=-10.6 Z=0
    g27: LineSegment [constr] StartX=-181.6 StartY=1.12e-14 StartZ=0 EndX=-152.209 EndY=0 EndZ=0
    g28: LineSegment [constr] StartX=-181.6 StartY=1.12e-14 StartZ=0 EndX=-130.41 EndY=0 EndZ=0
    g29: LineSegment [constr] StartX=-152.209 StartY=0 StartZ=0 EndX=-152.209 EndY=6.95 EndZ=0
    g30: LineSegment [constr] StartX=-130.41 StartY=0 StartZ=0 EndX=-130.41 EndY=-6.95 EndZ=0
    g31: Circle CenterX=-152.209 CenterY=6.95 CenterZ=0 NormalX=0 NormalY=0 NormalZ=1 AngleXU=0 Radius=2.1
    g32: Circle CenterX=-130.41 CenterY=-6.95 CenterZ=0 NormalX=0 NormalY=0 NormalZ=1 AngleXU=0 Radius=2.1
  constraints (79):
    c: Distance(g0) = 11.69
    c: PointOnObject(g0,g-1)
    c: Coincident(g-4,g0)
    c: Distance(g1) = 2.6
    c: Coincident(g1,g0)
    c: Vertical(g1)
    c: Distance(g2) = 2.6
    c: Coincident(g2,g0)
    c: Vertical(g2)
    c: Distance(g18,g12) = 8
    c: Coincident(g18,g2)
    c: Vertical(g3)
    c: Distance(g14,g12) = 5
    c: Horizontal(g4)
    c: Distance(g16,g14) = 8
    c: Vertical(g5)
    c: Distance(g26,g20) = 8
    c: Coincident(g20,g1)
    c: Vertical(g7)
    c: Distance(g26,g24) = 5
    c: Horizontal(g8)
    c: Distance(g24,g22) = 8
    c: Vertical(g9)
    c: PointOnObject(g12,g3)
    c: PointOnObject(g12,g4)
    c: Tangent(g3,g11) = 1.5708
    c: Tangent(g4,g11) = 1.5708
    c: PointOnObject(g14,g5)
    c: PointOnObject(g14,g4)
    c: Tangent(g5,g13) = 1.5708
    c: Tangent(g4,g13) = 1.5708
    c: PointOnObject(g16,g5)
    c: PointOnObject(g16,g6)
    c: Tangent(g5,g15) = 1.5708
    c: Tangent(g6,g15) = 1.5708
    c: PointOnObject(g18,g3)
    c: PointOnObject(g18,g6)
    c: Tangent(g3,g17) = 1.5708
    c: Tangent(g6,g17) = 1.5708
    c: Equal(g11,g13)
    c: Equal(g13,g15)
    c: Equal(g15,g17)
    c: DistanceX(g4,g4) = 0.25
    c: PointOnObject(g20,g7)
    c: PointOnObject(g20,g10)
    c: Tangent(g7,g19) = -1.5708
    c: Tangent(g10,g19) = -1.5708
    c: PointOnObject(g22,g9)
    c: PointOnObject(g22,g10)
    c: Tangent(g9,g21) = -1.5708
    c: Tangent(g10,g21) = -1.5708
    c: PointOnObject(g24,g9)
    c: PointOnObject(g24,g8)
    c: Tangent(g9,g23) = -1.5708
    c: Tangent(g8,g23) = -1.5708
    c: PointOnObject(g26,g8)
    c: PointOnObject(g26,g7)
    c: Tangent(g8,g25) = -1.5708
    c: Tangent(g7,g25) = -1.5708
    c: Equal(g19,g21)
    c: Equal(g21,g23)
    c: Equal(g23,g25)
    c: DistanceX(g10,g10) = 0.25
    c: Distance(g27) = 29.391
    c: Coincident(g27,g0)
    c: PointOnObject(g27,g-1)
    c: Distance(g28) = 51.19
    c: Coincident(g28,g0)
    c: PointOnObject(g28,g-1)
    c: Distance(g29) = 6.95
    c: Coincident(g29,g27)
    c: Vertical(g29)
    c: Distance(g30) = 6.95
    c: Coincident(g30,g28)
    c: Vertical(g30)
    c: Diameter(g31) = 4.2
    c: Diameter(g32) = 4.2
    c: Coincident(g32,g30)
    c: Coincident(g31,g29)
FEATURE [Sketcher::SketchObject] Sketch031  label="fori inferiori switch pompa"
  ArcFitTolerance = 1e-06
  AttachmentSupport = -> [XY_Plane]
  ExternalGeometry = -> [Sketch]
  FullyConstrained = true
  MakeInternals = false
  MapMode = 5
  sketch-geometry (4):
    g0: LineSegment [constr] StartX=-57.2 StartY=1.9e-15 StartZ=0 EndX=-62.45 EndY=1.9e-15 EndZ=0
    g1: LineSegment [constr] StartX=-62.45 StartY=3.25 StartZ=0 EndX=-62.45 EndY=-3.25 EndZ=0
    g2: Circle CenterX=-62.45 CenterY=3.25 CenterZ=0 NormalX=0 NormalY=0 NormalZ=1 AngleXU=0 Radius=1.6
    g3: Circle CenterX=-62.45 CenterY=-3.25 CenterZ=0 NormalX=0 NormalY=0 NormalZ=1 AngleXU=0 Radius=1.6
  constraints (10):
    c: Distance(g0) = 5.25
    c: Coincident(g0,g-3)
    c: PointOnObject(g0,g-3)
    c: Vertical(g1)
    c: DistanceY(g1,g1) = 6.5
    c: Symmetric(g1,g1,g0)
    c: Diameter(g2) = 3.2
    c: Diameter(g3) = 3.2
    c: Coincident(g2,g1)
    c: Coincident(g3,g1)
FEATURE [Sketcher::SketchObject] Sketch032  label="spazio per PILA 18650"
  ArcFitTolerance = 1e-06
  AttachmentSupport = -> [XY_Plane]
  ExternalGeometry = -> [Sketch]
  FullyConstrained = true
  MakeInternals = false
  MapMode = 5
  sketch-geometry (2):
    g0: LineSegment [constr] StartX=-178.142 StartY=-1.74e-14 StartZ=0 EndX=-191.142 EndY=-1.83e-14 EndZ=0
    g1: Circle CenterX=-191.142 CenterY=-1.83e-14 CenterZ=0 NormalX=0 NormalY=0 NormalZ=1 AngleXU=0 Radius=10.5
  constraints (5):
    c: Distance(g0) = 13
    c: Coincident(g0,g-3)
    c: PointOnObject(g0,g-4)
    c: Diameter(g1) = 21
    c: Coincident(g1,g0)
FEATURE [Part::Extrusion] Extrude030  label="Extrude spazio per PILA 18650"
  Base = -> Sketch032
  Dir = (0,0,1)
  DirLink = -> Sketch [Edge45]
  DirMode = 2
  FaceMakerClass = Part::FaceMakerBullseye
  FaceMakerMode = 3
  LengthFwd = 76
  LengthRev = 0
  Placement = pos=(6,0,-72) rot=(0,0,1;0rad)
  Solid = true
  Symmetric = false
FEATURE [Sketcher::SketchObject] Sketch033  label="fermo per scheda micro"
  ArcFitTolerance = 1e-06
  AttachmentSupport = -> [XZ_Plane]
  ExternalGeometry = -> [Sketch]
  FullyConstrained = true
  MakeInternals = false
  MapMode = 5
  Placement = pos=(0,0,0) rot=(1,0,0;1.5708rad)
  sketch-geometry (12):
    g0: LineSegment StartX=-11.6 StartY=6 StartZ=0 EndX=-4 EndY=6 EndZ=0
    g1: LineSegment StartX=-4 StartY=6 StartZ=0 EndX=-4 EndY=36.4 EndZ=0
    g2: LineSegment StartX=-4 StartY=36.4 StartZ=0 EndX=-11.6 EndY=36.4 EndZ=0
    g3: LineSegment StartX=-11.6 StartY=36.4 StartZ=0 EndX=-11.6 EndY=6 EndZ=0
    g4: LineSegment StartX=-80.11 StartY=11.6 StartZ=0 EndX=-70.51 EndY=11.6 EndZ=0
    g5: LineSegment StartX=-70.51 StartY=11.6 StartZ=0 EndX=-70.51 EndY=6 EndZ=0
    g6: LineSegment StartX=-70.51 StartY=6 StartZ=0 EndX=-80.11 EndY=6 EndZ=0
    g7: LineSegment StartX=-80.11 StartY=6 StartZ=0 EndX=-80.11 EndY=11.6 EndZ=0
    g8: LineSegment StartX=-78.51 StartY=36.4 StartZ=0 EndX=-70.51 EndY=36.4 EndZ=0
    g9: LineSegment StartX=-70.51 StartY=36.4 StartZ=0 EndX=-70.51 EndY=30.8 EndZ=0
    g10: LineSegment StartX=-70.51 StartY=30.8 StartZ=0 EndX=-78.51 EndY=30.8 EndZ=0
    g11: LineSegment StartX=-78.51 StartY=30.8 StartZ=0 EndX=-78.51 EndY=36.4 EndZ=0
  constraints (33):
    c: Horizontal(g0)
    c: Coincident(g1,g0)
    c: Coincident(g2,g1)
    c: Horizontal(g2)
    c: Coincident(g3,g2)
    c: Coincident(g3,g0)
    c: Vertical(g3)
    c: DistanceX(g2,g2) = 7.6
    c: Coincident(g1,g-3)
    c: Coincident(g0,g-3)
    c: Horizontal(g4)
    c: Coincident(g5,g4)
    c: Vertical(g5)
    c: Coincident(g6,g5)
    c: Horizontal(g6)
    c: Coincident(g7,g6)
    c: Coincident(g7,g4)
    c: Vertical(g7)
    c: DistanceY(g5,g5) = 5.6
    c: DistanceX(g4,g4) = 9.6
    c: Coincident(g9,g8)
    c: Vertical(g9)
    c: Coincident(g10,g9)
    c: Horizontal(g10)
    c: Coincident(g11,g10)
    c: Coincident(g11,g8)
    c: Vertical(g11)
    c: DistanceY(g9,g9) = 5.6
    c: DistanceX(g10,g10) = 8
    c: Coincident(g4,g-4)
    c: DistanceX(g4,g10) = 1.6
    c: Horizontal(g8)
    c: DistanceY(g8,g1) = 0
FEATURE [Sketcher::SketchObject] Sketch034  label="buchi guida rail"
  ArcFitTolerance = 1e-06
  AttachmentSupport = -> [XY_Plane]
  ExternalGeometry = -> [Sketch]
  FullyConstrained = true
  MakeInternals = false
  MapMode = 5
  sketch-geometry (6):
    g0: LineSegment [constr] StartX=-100.8 StartY=9.1e-15 StartZ=0 EndX=-93.3 EndY=0 EndZ=0
    g1: LineSegment [constr] StartX=-93.3 StartY=0 StartZ=0 EndX=-73.3 EndY=0 EndZ=0
    g2: LineSegment [constr] StartX=-73.3 StartY=0 StartZ=0 EndX=-53.3 EndY=0 EndZ=0
    g3: Circle CenterX=-93.3 CenterY=0 CenterZ=0 NormalX=0 NormalY=0 NormalZ=1 AngleXU=0 Radius=2.5
    g4: Circle CenterX=-73.3 CenterY=0 CenterZ=0 NormalX=0 NormalY=0 NormalZ=1 AngleXU=0 Radius=2.5
    g5: Circle CenterX=-53.3 CenterY=0 CenterZ=0 NormalX=0 NormalY=0 NormalZ=1 AngleXU=0 Radius=2.5
  constraints (15):
    c: Distance(g0) = 7.5
    c: Coincident(g0,g-3)
    c: PointOnObject(g0,g-1)
    c: Distance(g1) = 20
    c: Coincident(g1,g0)
    c: PointOnObject(g1,g-1)
    c: Distance(g2) = 20
    c: Coincident(g2,g1)
    c: PointOnObject(g2,g-1)
    c: Diameter(g3) = 5
    c: Diameter(g4) = 5
    c: Diameter(g5) = 5
    c: Coincident(g3,g0)
    c: Coincident(g4,g1)
    c: Coincident(g5,g2)
FEATURE [Part::Extrusion] Extrude032  label="Extrude buchi guida rail"
  Base = -> Sketch034
  Dir = (0,0,1)
  DirMode = 2
  FaceMakerClass = Part::FaceMakerBullseye
  FaceMakerMode = 3
  LengthFwd = -6.2
  LengthRev = 0
  Placement = pos=(0,0,43.2) rot=(0,0,1;0rad)
  Solid = true
  Symmetric = false
FEATURE [Part::Extrusion] Extrude033  label="Extrude fori superiori per solenoide e oled001"
  Base = -> Sketch030
  Dir = (0,0,1)
  DirMode = 2
  FaceMakerClass = Part::FaceMakerBullseye
  FaceMakerMode = 3
  LengthFwd = -4.8
  LengthRev = 0
  Placement = pos=(0,0,41.2) rot=(0,0,1;0rad)
  Solid = true
  Symmetric = false
FEATURE [Part::Extrusion] Extrude034  label="Extrude fori sotto impugnatura001"
  Base = -> Sketch029
  Dir = (0,0,1)
  DirMode = 2
  FaceMakerClass = Part::FaceMakerBullseye
  FaceMakerMode = 3
  LengthFwd = 5
  LengthRev = 0
  Placement = pos=(0,0,-83) rot=(0,0,1;0rad)
  Solid = true
  Symmetric = false
FEATURE [Part::Extrusion] Extrude035  label="Extrude fori inferiori switch pompa001"
  Base = -> Sketch031
  Dir = (0,0,1)
  DirMode = 2
  FaceMakerClass = Part::FaceMakerBullseye
  FaceMakerMode = 3
  LengthFwd = 4
  LengthRev = 0
  Placement = pos=(0,0,-1.7) rot=(0,0,1;0rad)
  Solid = true
  Symmetric = false
FEATURE [Part::Extrusion] Extrude036  label="Extrude foro sotto posteriore M3x5x007"
  Base = -> Sketch027
  Dir = (0,0,1)
  DirMode = 2
  FaceMakerClass = Part::FaceMakerBullseye
  FaceMakerMode = 3
  LengthFwd = 6.2
  LengthRev = 0
  Placement = pos=(0,0,-9.6) rot=(0,0,1;0rad)
  Solid = true
  Symmetric = false
FEATURE [Part::Extrusion] Extrude037  label="Extrude foro sotto anteriore M3x5x007"
  Base = -> Sketch026
  Dir = (0,0,1)
  DirMode = 2
  FaceMakerClass = Part::FaceMakerBullseye
  FaceMakerMode = 3
  LengthFwd = 6.2
  LengthRev = 0
  Solid = true
  Symmetric = false
FEATURE [Sketcher::SketchObject] Sketch035  label="foro per fissaggio micro"
  ArcFitTolerance = 1e-06
  AttachmentSupport = -> [XZ_Plane]
  ExternalGeometry = -> [Sketch,Sketch033]
  FullyConstrained = true
  MakeInternals = false
  MapMode = 5
  Placement = pos=(0,0,0) rot=(1,0,0;1.5708rad)
  sketch-geometry (3):
    g0: Circle CenterX=-7.8 CenterY=21.2 CenterZ=0 NormalX=0 NormalY=0 NormalZ=1 AngleXU=0 Radius=1.6
    g1: GeomPoint [constr] X=-4 Y=21.2 Z=0
    g2: LineSegment [constr] StartX=-4 StartY=21.2 StartZ=0 EndX=-11.6 EndY=21.2 EndZ=0
  constraints (6):
    c: Diameter(g0) = 3.2
    c: Symmetric(g-3,g-3,g1)
    c: Coincident(g2,g1)
    c: Horizontal(g2)
    c: DistanceX(g-4,g2) = 0
    c: Symmetric(g2,g1,g0)
FEATURE [Part::Extrusion] Extrude038  label="Extrude foro per fissaggio micro"
  Base = -> Sketch035
  Dir = (0,-1,2e-16)
  DirMode = 2
  FaceMakerClass = Part::FaceMakerBullseye
  FaceMakerMode = 3
  LengthFwd = 3
  LengthRev = 0
  Placement = pos=(0,8.6,0) rot=(0,0,1;0rad)
  Solid = true
  Symmetric = false
FEATURE [Sketcher::SketchObject] Sketch036  label="supporto per alimentatore"
  ArcFitTolerance = 1e-06
  AttachmentSupport = -> [XZ_Plane]
  ExternalGeometry = -> [Sketch,Sketch016,Sketch022]
  FullyConstrained = true
  MakeInternals = false
  MapMode = 5
  Placement = pos=(0,0,0) rot=(1,0,0;1.5708rad)
  sketch-geometry (5):
    g0: LineSegment StartX=-211.843 StartY=-50.0944 StartZ=0 EndX=-211.843 EndY=-80.4316 EndZ=0
    g1: LineSegment StartX=-211.843 StartY=-50.0944 StartZ=0 EndX=-207.775 EndY=-41.3701 EndZ=0
    g2: LineSegment [constr] StartX=-209.443 StartY=-50.0944 StartZ=0 EndX=-209.443 EndY=-80.4316 EndZ=0
    g3: LineSegment StartX=-207.775 StartY=-41.3701 StartZ=0 EndX=-207.775 EndY=-80.4316 EndZ=0
    g4: LineSegment StartX=-211.843 StartY=-80.4316 StartZ=0 EndX=-207.775 EndY=-80.4316 EndZ=0
  constraints (15):
    c: Vertical(g0)
    c: Coincident(g1,g0)
    c: Vertical(g2)
    c: Tangent(g2,g-5)
    c: Coincident(g3,g1)
    c: Vertical(g3)
    c: DistanceY(g-3,g3) = -2
    c: Tangent(g1,g-8)
    c: DistanceY(g-3,g0) = -2
    c: Coincident(g4,g0)
    c: Coincident(g4,g3)
    c: Tangent(g0,g-6)
    c: DistanceY(g-3,g2) = -2
    c: DistanceY(g2,g0) = 0
    c: DistanceX(g-3,g3) = 6.8
FEATURE [Part::Extrusion] Extrude039  label="Extrude039 supporto alimentatore"
  Base = -> Sketch036
  Dir = (0,-1,2e-16)
  DirMode = 2
  FaceMakerClass = Part::FaceMakerBullseye
  FaceMakerMode = 3
  LengthFwd = 25.2
  LengthRev = 0
  Solid = true
  Symmetric = true
FEATURE [Sketcher::SketchObject] Sketch037  label="scavo per alimentatore"
  ArcFitTolerance = 1e-06
  AttachmentSupport = -> [XZ_Plane]
  ExternalGeometry = -> [Sketch036]
  FullyConstrained = true
  MakeInternals = false
  MapMode = 5
  Placement = pos=(0,0,0) rot=(1,0,0;1.5708rad)
  sketch-geometry (4):
    g0: LineSegment StartX=-209.575 StartY=-50.4316 StartZ=0 EndX=-209.575 EndY=-80.4316 EndZ=0
    g1: LineSegment StartX=-209.575 StartY=-50.4316 StartZ=0 EndX=-207.775 EndY=-50.4316 EndZ=0
    g2: LineSegment StartX=-207.775 StartY=-50.4316 StartZ=0 EndX=-207.775 EndY=-80.4316 EndZ=0
    g3: LineSegment StartX=-207.775 StartY=-80.4316 StartZ=0 EndX=-209.575 EndY=-80.4316 EndZ=0
  constraints (11):
    c: Vertical(g0)
    c: Coincident(g1,g0)
    c: Horizontal(g1)
    c: Coincident(g2,g1)
    c: Vertical(g2)
    c: Coincident(g3,g2)
    c: Coincident(g3,g0)
    c: Horizontal(g3)
    c: DistanceX(g1,g1) = 1.8
    c: Coincident(g2,g-3)
    c: DistanceY(g2,g2) = 30
FEATURE [Part::Extrusion] Extrude040  label="Extrude040 scavo alimentatore"
  Base = -> Sketch037
  Dir = (0,-1,2e-16)
  DirMode = 2
  FaceMakerClass = Part::FaceMakerBullseye
  FaceMakerMode = 3
  LengthFwd = 19.5
  LengthRev = 0
  Solid = true
  Symmetric = true
FEATURE [Part::Extrusion] Extrude031  label="Extrude fermo per scheda micro"
  Base = -> Sketch033
  Dir = (0,-1,2e-16)
  DirMode = 2
  FaceMakerClass = Part::FaceMakerBullseye
  FaceMakerMode = 3
  LengthFwd = 3
  LengthRev = 0
  Placement = pos=(0,8.6,0) rot=(0,0,1;0rad)
  Solid = true
  Symmetric = false
FEATURE [Sketcher::SketchObject] Sketch038  label="scavo driver solenoide"
  ArcFitTolerance = 1e-06
  AttachmentSupport = -> [XZ_Plane]
  ExternalGeometry = -> [Sketch,Sketch036]
  FullyConstrained = true
  MakeInternals = false
  MapMode = 5
  Placement = pos=(0,0,0) rot=(1,0,0;1.5708rad)
  sketch-geometry (7):
    g0: LineSegment StartX=-192.222 StartY=-8.0175 StartZ=0 EndX=-194.941 EndY=-6.74965 EndZ=0
    g1: LineSegment StartX=-194.941 StartY=-6.74965 StartZ=0 EndX=-212.269 EndY=-43.9083 EndZ=0
    g2: LineSegment StartX=-192.222 StartY=-8.0175 StartZ=0 EndX=-188.779 EndY=-9.62345 EndZ=0
    g3: LineSegment StartX=-188.779 StartY=-9.62345 StartZ=0 EndX=-205.357 EndY=-45.1761 EndZ=0
    g4: LineSegment StartX=-205.357 StartY=-45.1761 StartZ=0 EndX=-209.55 EndY=-45.1761 EndZ=0
    g5: LineSegment [constr] StartX=-212.269 StartY=-43.9083 StartZ=0 EndX=-209.55 EndY=-45.1761 EndZ=0
    g6: LineSegment StartX=-212.269 StartY=-43.9083 StartZ=0 EndX=-209.55 EndY=-45.1761 EndZ=0
  constraints (20):
    c: Coincident(g1,g0)
    c: Coincident(g3,g2)
    c: Coincident(g4,g3)
    c: Distance(g2) = 3.8
    c: Distance(g1) = 41
    c: Coincident(g5,g1)
    c: Distance(g5) = 3
    c: Perpendicular(g5,g-3)
    c: Parallel(g1,g-3)
    c: Perpendicular(g1,g0)
    c: Distance(g0) = 3
    c: Coincident(g6,g1)
    c: Parallel(g3,g-3)
    c: Perpendicular(g2,g3)
    c: Coincident(g2,g0)
    c: Perpendicular(g-4,g4)
    c: PointOnObject(g5,g-3)
    c: Distance(g-3,g5) = 9.6
    c: Coincident(g4,g5)
    c: Coincident(g6,g4)
FEATURE [Part::Extrusion] Extrude041  label="Extrude scavo driver solenoide"
  Base = -> Sketch038
  Dir = (0,-1,2e-16)
  DirMode = 2
  FaceMakerClass = Part::FaceMakerBullseye
  FaceMakerMode = 3
  LengthFwd = 20.6
  LengthRev = 0
  Solid = true
  Symmetric = true
FEATURE [Sketcher::SketchObject] Sketch039  label="scavo per cavo usb per micro"
  ArcFitTolerance = 1e-06
  AttachmentSupport = -> [XZ_Plane]
  ExternalGeometry = -> [Sketch,Sketch016]
  FullyConstrained = true
  MakeInternals = false
  MapMode = 5
  Placement = pos=(0,0,0) rot=(1,0,0;1.5708rad)
  sketch-geometry (4):
    g0: LineSegment StartX=-82.51 StartY=36.4 StartZ=0 EndX=-74.51 EndY=36.4 EndZ=0
    g1: LineSegment StartX=-74.51 StartY=36.4 StartZ=0 EndX=-74.51 EndY=30.8 EndZ=0
    g2: LineSegment StartX=-74.51 StartY=30.8 StartZ=0 EndX=-82.51 EndY=30.8 EndZ=0
    g3: LineSegment StartX=-82.51 StartY=30.8 StartZ=0 EndX=-82.51 EndY=36.4 EndZ=0
  constraints (11):
    c: Coincident(g1,g0)
    c: Vertical(g1)
    c: Coincident(g2,g1)
    c: Horizontal(g2)
    c: Coincident(g3,g2)
    c: Coincident(g3,g0)
    c: Vertical(g3)
    c: Tangent(g0,g-3)
    c: Tangent(g2,g-4)
    c: Tangent(g3,g-4)
    c: Tangent(g1,g-4)
FEATURE [Part::Extrusion] Extrude042  label="Extrude scavo per cavo usb per micro"
  Base = -> Sketch039
  Dir = (0,-1,2e-16)
  DirMode = 2
  FaceMakerClass = Part::FaceMakerBullseye
  FaceMakerMode = 3
  LengthFwd = 11.2
  LengthRev = 0
  Solid = true
  Symmetric = true
FEATURE [Sketcher::SketchObject] Sketch040  label="scavo saldature alimentatore connettore 5v"
  ArcFitTolerance = 1e-06
  AttachmentSupport = -> [XZ_Plane]
  ExternalGeometry = -> [Sketch037]
  FullyConstrained = true
  MakeInternals = false
  MapMode = 5
  Placement = pos=(0,0,0) rot=(1,0,0;1.5708rad)
  sketch-geometry (4):
    g0: LineSegment StartX=-211.175 StartY=-52.4316 StartZ=0 EndX=-211.175 EndY=-56.4316 EndZ=0
    g1: LineSegment StartX=-211.175 StartY=-52.4316 StartZ=0 EndX=-209.575 EndY=-52.4316 EndZ=0
    g2: LineSegment StartX=-209.575 StartY=-52.4316 StartZ=0 EndX=-209.575 EndY=-56.4316 EndZ=0
    g3: LineSegment StartX=-209.575 StartY=-56.4316 StartZ=0 EndX=-211.175 EndY=-56.4316 EndZ=0
  constraints (11):
    c: Vertical(g0)
    c: Coincident(g1,g0)
    c: Horizontal(g1)
    c: Coincident(g2,g1)
    c: Coincident(g3,g2)
    c: Coincident(g3,g0)
    c: Horizontal(g3)
    c: DistanceX(g1,g1) = 1.6
    c: DistanceY(g2,g2) = 4
    c: Tangent(g2,g-3)
    c: DistanceY(g1,g-3) = 2
FEATURE [Part::Extrusion] Extrude043  label="Extrude scavo saldature alimentatore connettore 5v"
  Base = -> Sketch040
  Dir = (0,-1,2e-16)
  DirMode = 2
  FaceMakerClass = Part::FaceMakerBullseye
  FaceMakerMode = 3
  LengthFwd = 8
  LengthRev = 0
  Solid = true
  Symmetric = true
FEATURE [Sketcher::SketchObject] Sketch041  label="scavo saldature alimentatore connettore 5v verticali"
  ArcFitTolerance = 1e-06
  AttachmentSupport = -> [XZ_Plane]
  ExternalGeometry = -> [Sketch037]
  FullyConstrained = true
  MakeInternals = false
  MapMode = 5
  Placement = pos=(0,0,0) rot=(1,0,0;1.5708rad)
  sketch-geometry (4):
    g0: LineSegment StartX=-211.175 StartY=-53.6316 StartZ=0 EndX=-209.575 EndY=-53.6316 EndZ=0
    g1: LineSegment StartX=-209.575 StartY=-53.6316 StartZ=0 EndX=-209.575 EndY=-76.6316 EndZ=0
    g2: LineSegment StartX=-209.575 StartY=-76.6316 StartZ=0 EndX=-211.175 EndY=-76.6316 EndZ=0
    g3: LineSegment StartX=-211.175 StartY=-76.6316 StartZ=0 EndX=-211.175 EndY=-53.6316 EndZ=0
  constraints (11):
    c: Horizontal(g0)
    c: Coincident(g1,g0)
    c: Coincident(g2,g1)
    c: Horizontal(g2)
    c: Coincident(g3,g2)
    c: Coincident(g3,g0)
    c: Vertical(g3)
    c: DistanceY(g3,g3) = 23
    c: DistanceX(g0,g0) = 1.6
    c: Tangent(g1,g-3)
    c: DistanceY(g0,g-3) = 3.2
FEATURE [Part::Extrusion] Extrude044  label="Extrude scavo saldature alimentatore connettore 5v verticali"
  Base = -> Sketch041
  Dir = (0,-1,2e-16)
  DirMode = 2
  FaceMakerClass = Part::FaceMakerBullseye
  FaceMakerMode = 3
  LengthFwd = 3.2
  LengthRev = 0
  Placement = pos=(0,8.3,0) rot=(0,0,1;0rad)
  Solid = true
  Symmetric = false
FEATURE [Sketcher::SketchObject] Sketch042  label="fermi per driver solenoide e alimentatore"
  ArcFitTolerance = 1e-06
  AttachmentSupport = -> [XZ_Plane]
  ExternalGeometry = -> [Sketch036,Sketch037,Sketch,Sketch038]
  FullyConstrained = true
  MakeInternals = false
  MapMode = 5
  Placement = pos=(0,0,0) rot=(1,0,0;1.5708rad)
  sketch-geometry (27):
    g0: LineSegment StartX=-200.506 StartY=-25.7811 StartZ=0 EndX=-201.436 EndY=-27.775 EndZ=0
    g1: LineSegment StartX=-201.436 StartY=-27.775 StartZ=0 EndX=-199.442 EndY=-28.7048 EndZ=0
    g2: LineSegment StartX=-199.442 StartY=-28.7048 StartZ=0 EndX=-198.512 EndY=-26.7109 EndZ=0
    g3: LineSegment StartX=-198.512 StartY=-26.7109 StartZ=0 EndX=-200.506 EndY=-25.7811 EndZ=0
    g4: LineSegment StartX=-201.28 StartY=-23.6549 StartZ=0 EndX=-203.562 EndY=-28.5489 EndZ=0
    g5: LineSegment StartX=-203.562 StartY=-28.5489 StartZ=0 EndX=-200.118 EndY=-30.1549 EndZ=0
    g6: LineSegment StartX=-197.992 StartY=-29.381 StartZ=0 EndX=-197.062 EndY=-27.3871 EndZ=0
    g7: LineSegment StartX=-197.836 StartY=-25.2608 StartZ=0 EndX=-201.28 EndY=-23.6549 EndZ=0
    g8: LineSegment [constr] StartX=-198.668 StartY=-30.8311 StartZ=0 EndX=-197.992 EndY=-29.381 EndZ=0
    g9: LineSegment [constr] StartX=-198.668 StartY=-30.8311 StartZ=0 EndX=-200.118 EndY=-30.1549 EndZ=0
    g10: ArcOfCircle CenterX=-198.512 CenterY=-26.7109 CenterZ=0 NormalX=0 NormalY=0 NormalZ=1 AngleXU=0 Radius=1.6 StartAngle=5.84685 EndAngle=7.41765
    g11: GeomPoint [constr] X=-196.386 Y=-25.937 Z=0
    g12: ArcOfCircle CenterX=-199.442 CenterY=-28.7048 CenterZ=0 NormalX=0 NormalY=0 NormalZ=1 AngleXU=0 Radius=1.6 StartAngle=4.27606 EndAngle=5.84685
    g13: GeomPoint [constr] X=-198.668 Y=-30.8311 Z=0
    g14: LineSegment StartX=-207.775 StartY=-46.8316 StartZ=0 EndX=-207.775 EndY=-50.8316 EndZ=0
    g15: LineSegment StartX=-207.775 StartY=-46.8316 StartZ=0 EndX=-203.775 EndY=-46.8316 EndZ=0
    g16: LineSegment StartX=-203.775 StartY=-46.8316 StartZ=0 EndX=-203.775 EndY=-50.8316 EndZ=0
    g17: LineSegment StartX=-207.775 StartY=-50.8316 StartZ=0 EndX=-203.775 EndY=-50.8316 EndZ=0
    g18: LineSegment StartX=-209.375 StartY=-52.4316 StartZ=0 EndX=-203.775 EndY=-52.4316 EndZ=0
    g19: LineSegment StartX=-202.175 StartY=-50.8316 StartZ=0 EndX=-202.175 EndY=-46.8316 EndZ=0
    g20: LineSegment StartX=-203.775 StartY=-45.2316 StartZ=0 EndX=-209.375 EndY=-45.2316 EndZ=0
    g21: LineSegment StartX=-209.375 StartY=-45.2316 StartZ=0 EndX=-209.375 EndY=-52.4316 EndZ=0
    g22: ArcOfCircle CenterX=-203.775 CenterY=-46.8316 CenterZ=0 NormalX=0 NormalY=0 NormalZ=1 AngleXU=0 Radius=1.6 StartAngle=1.8e-15 EndAngle=1.5708
    g23: GeomPoint [constr] X=-202.175 Y=-45.2316 Z=0
    g24: ArcOfCircle CenterX=-203.775 CenterY=-50.8316 CenterZ=0 NormalX=0 NormalY=0 NormalZ=1 AngleXU=0 Radius=1.6 StartAngle=4.71239 EndAngle=6.28319
    g25: GeomPoint [constr] X=-202.175 Y=-52.4316 Z=0
    g26: LineSegment [constr] StartX=-207.775 StartY=-50.4316 StartZ=0 EndX=-207.775 EndY=-50.8316 EndZ=0
  constraints (69):
    c: Coincident(g1,g0)
    c: Coincident(g2,g1)
    c: Coincident(g3,g2)
    c: Coincident(g3,g0)
    c: Parallel(g0,g2)
    c: Perpendicular(g3,g0)
    c: Perpendicular(g1,g0)
    c: Coincident(g5,g4)
    c: Coincident(g7,g4)
    c: Distance(g3) = 2.2
    c: Distance(g2) = 2.2
    c: Parallel(g6,g2)
    c: Parallel(g6,g4)
    c: Perpendicular(g5,g6)
    c: Perpendicular(g7,g6)
    c: Distance(g13,g11) = 5.4
    c: Distance(g5,g13) = 5.4
    c: Coincident(g9,g8)
    c: Distance(g8) = 1.6
    c: Distance(g9) = 1.6
    c: Perpendicular(g9,g8)
    c: Parallel(g8,g6)
    c: Coincident(g8,g13)
    c: Distance(g8,g1) = 1.6
    c: Distance(g9,g1) = 1.6
    c: Tangent(g0,g-5)
    c: Distance(g0,g-6) = 19.2
    c: PointOnObject(g11,g7)
    c: PointOnObject(g11,g6)
    c: Tangent(g7,g10) = -1.5708
    c: Tangent(g6,g10) = -1.5708
    c: PointOnObject(g13,g5)
    c: Tangent(g5,g12) = -1.5708
    c: Tangent(g6,g12) = -1.5708
    c: Equal(g10,g12)
    c: Coincident(g10,g2)
    c: Vertical(g14)
    c: Coincident(g15,g14)
    c: Horizontal(g15)
    c: Coincident(g16,g15)
    c: Vertical(g16)
    c: Coincident(g17,g14)
    c: Coincident(g17,g16)
    c: Horizontal(g17)
    c: Distance(g16) = 4
    c: Distance(g15) = 4
    c: Horizontal(g18)
    c: Vertical(g19)
    c: Horizontal(g20)
    c: Coincident(g21,g20)
    c: Coincident(g21,g18)
    c: Vertical(g21)
    c: Distance(g20,g23) = 7.2
    c: Distance(g25,g23) = 7.2
    c: DistanceY(g18,g14) = 1.6
    c: DistanceX(g18,g14) = 1.6
    c: PointOnObject(g23,g20)
    c: PointOnObject(g23,g19)
    c: Tangent(g20,g22) = -1.5708
    c: Tangent(g19,g22) = -1.5708
    c: PointOnObject(g25,g19)
    c: Tangent(g18,g24) = -1.5708
    c: Tangent(g19,g24) = -1.5708
    c: Equal(g22,g24)
    c: Coincident(g22,g15)
    c: Vertical(g26)
    c: Distance(g26) = 0.4
    c: Coincident(g26,g-4)
    c: Coincident(g14,g26)
FEATURE [Part::Extrusion] Extrude045  label="Extrude fermi per driver solenoide e alimentatore"
  Base = -> Sketch042
  Dir = (0,-1,2e-16)
  DirMode = 2
  FaceMakerClass = Part::FaceMakerBullseye
  FaceMakerMode = 3
  LengthFwd = 25.2
  LengthRev = 0
  Solid = true
  Symmetric = true
FEATURE [Sketcher::SketchObject] Sketch043  label="scavo pulizia fermo alimentatore"
  ArcFitTolerance = 1e-06
  AttachmentSupport = -> [XZ_Plane]
  ExternalGeometry = -> [Sketch042,Sketch036,Sketch037]
  FullyConstrained = true
  MakeInternals = false
  MapMode = 5
  Placement = pos=(0,0,0) rot=(1,0,0;1.5708rad)
  sketch-geometry (6):
    g0: LineSegment StartX=-209.375 StartY=-52.4316 StartZ=0 EndX=-209.375 EndY=-50.4316 EndZ=0
    g1: LineSegment StartX=-209.375 StartY=-50.4316 StartZ=0 EndX=-207.775 EndY=-50.4316 EndZ=0
    g2: LineSegment StartX=-207.775 StartY=-50.4316 StartZ=0 EndX=-207.775 EndY=-45.2316 EndZ=0
    g3: LineSegment StartX=-207.775 StartY=-45.2316 StartZ=0 EndX=-202.175 EndY=-45.2316 EndZ=0
    g4: LineSegment StartX=-202.175 StartY=-45.2316 StartZ=0 EndX=-202.175 EndY=-52.4316 EndZ=0
    g5: LineSegment StartX=-202.175 StartY=-52.4316 StartZ=0 EndX=-209.375 EndY=-52.4316 EndZ=0
  constraints (13):
    c: Vertical(g0)
    c: Coincident(g1,g0)
    c: Coincident(g2,g1)
    c: Coincident(g3,g2)
    c: Coincident(g4,g3)
    c: Coincident(g5,g4)
    c: Coincident(g5,g0)
    c: Horizontal(g5)
    c: Coincident(g0,g-6)
    c: Tangent(g1,g-8)
    c: Tangent(g2,g-4)
    c: Tangent(g3,g-7)
    c: Tangent(g4,g-3)
FEATURE [Part::Extrusion] Extrude046  label="Extrude scavo pulizia fermo alimentatore"
  Base = -> Sketch043
  Dir = (0,-1,2e-16)
  DirMode = 2
  FaceMakerClass = Part::FaceMakerBullseye
  FaceMakerMode = 3
  LengthFwd = 19.5
  LengthRev = 0
  Solid = true
  Symmetric = true
FEATURE [Sketcher::SketchObject] Sketch044  label="buchini per fissaggio oled"
  ArcFitTolerance = 1e-06
  AttachmentSupport = -> [YZ_Plane]
  ExternalGeometry = -> [Sketch]
  FullyConstrained = true
  MakeInternals = false
  MapMode = 5
  Placement = pos=(0,0,0) rot=(0.57735,0.57735,0.57735;2.0944rad)
  sketch-geometry (5):
    g0: LineSegment [constr] StartX=1.5e-14 StartY=67.3588 StartZ=0 EndX=0 EndY=64.3588 EndZ=0
    g1: LineSegment [constr] StartX=0 StartY=64.3588 StartZ=0 EndX=10.4 EndY=64.3588 EndZ=0
    g2: LineSegment [constr] StartX=0 StartY=64.3588 StartZ=0 EndX=-10.4 EndY=64.3588 EndZ=0
    g3: Circle CenterX=10.4 CenterY=64.3588 CenterZ=0 NormalX=0 NormalY=0 NormalZ=1 AngleXU=0 Radius=1.5
    g4: Circle CenterX=-10.4 CenterY=64.3588 CenterZ=0 NormalX=0 NormalY=0 NormalZ=1 AngleXU=0 Radius=1.5
  constraints (13):
    c: Distance(g0) = 3
    c: PointOnObject(g0,g-2)
    c: Coincident(g1,g0)
    c: Horizontal(g1)
    c: Coincident(g2,g0)
    c: Horizontal(g2)
    c: DistanceX(g1,g1) = 10.4
    c: Coincident(g3,g1)
    c: Diameter(g4) = 3
    c: Coincident(g4,g2)
    c: Coincident(g0,g-7)
    c: Equal(g1,g2)
    c: Equal(g4,g3)
FEATURE [Part::Extrusion] Extrude047  label="Extrude buchini per fissaggio oled"
  Base = -> Sketch044
  Dir = (1,0,0)
  DirMode = 2
  FaceMakerClass = Part::FaceMakerBullseye
  FaceMakerMode = 3
  LengthFwd = 10
  LengthRev = 0
  Placement = pos=(-186,0,0) rot=(0,0,1;0rad)
  Solid = true
  Symmetric = false
FEATURE [Sketcher::SketchObject] Sketch046  label="scavo 5x5 neopixel"
  ArcFitTolerance = 1e-06
  AttachmentSupport = -> [YZ_Plane002]
  FullyConstrained = true
  MakeInternals = false
  MapMode = 5
  Placement = pos=(0,0,0) rot=(0.57735,0.57735,0.57735;2.0944rad)
  sketch-geometry (4):
    g0: LineSegment StartX=-2.7 StartY=2.7 StartZ=0 EndX=2.7 EndY=2.7 EndZ=0
    g1: LineSegment StartX=2.7 StartY=2.7 StartZ=0 EndX=2.7 EndY=-2.7 EndZ=0
    g2: LineSegment StartX=2.7 StartY=-2.7 StartZ=0 EndX=-2.7 EndY=-2.7 EndZ=0
    g3: LineSegment StartX=-2.7 StartY=-2.7 StartZ=0 EndX=-2.7 EndY=2.7 EndZ=0
  constraints (11):
    c: Horizontal(g0)
    c: Coincident(g1,g0)
    c: Vertical(g1)
    c: Coincident(g2,g1)
    c: Horizontal(g2)
    c: Coincident(g3,g2)
    c: Coincident(g3,g0)
    c: Vertical(g3)
    c: DistanceX(g0,g0) = 5.4
    c: DistanceY(g1,g1) = 5.4
    c: Symmetric(g0,g1,g-1)
FEATURE [Sketcher::SketchObject] Sketch047  label="scavo 10x10 neopixel corpo"
  ArcFitTolerance = 1e-06
  AttachmentOffset = pos=(0,0,1) rot=(0,0,1;0rad)
  AttachmentSupport = -> [YZ_Plane002]
  FullyConstrained = true
  MakeInternals = false
  MapMode = 5
  Placement = pos=(1,0,0) rot=(0.57735,0.57735,0.57735;2.0944rad)
  sketch-geometry (4):
    g0: LineSegment StartX=-5 StartY=5.1 StartZ=0 EndX=5 EndY=5.1 EndZ=0
    g1: LineSegment StartX=5 StartY=5.1 StartZ=0 EndX=5 EndY=-5.1 EndZ=0
    g2: LineSegment StartX=5 StartY=-5.1 StartZ=0 EndX=-5 EndY=-5.1 EndZ=0
    g3: LineSegment StartX=-5 StartY=-5.1 StartZ=0 EndX=-5 EndY=5.1 EndZ=0
  constraints (11):
    c: Horizontal(g0)
    c: Coincident(g1,g0)
    c: Vertical(g1)
    c: Coincident(g2,g1)
    c: Horizontal(g2)
    c: Coincident(g3,g2)
    c: Coincident(g3,g0)
    c: Vertical(g3)
    c: DistanceX(g0,g0) = 10
    c: DistanceY(g1,g1) = 10.2
    c: Symmetric(g0,g2,g-1)
FEATURE [Sketcher::SketchObject] Sketch048  label="buco per perno blocco neopixel"
  ArcFitTolerance = 1e-06
  AttachmentSupport = -> [XZ_Plane002]
  FullyConstrained = true
  MakeInternals = false
  MapMode = 5
  Placement = pos=(0,0,0) rot=(1,0,0;1.5708rad)
  sketch-geometry (4):
    g0: LineSegment StartX=3 StartY=1.2 StartZ=0 EndX=3 EndY=-1.2 EndZ=0
    g1: LineSegment StartX=3 StartY=-1.2 StartZ=0 EndX=5.4 EndY=-1.2 EndZ=0
    g2: LineSegment StartX=5.4 StartY=-1.2 StartZ=0 EndX=5.4 EndY=1.2 EndZ=0
    g3: LineSegment StartX=5.4 StartY=1.2 StartZ=0 EndX=3 EndY=1.2 EndZ=0
  constraints (11):
    c: Coincident(g1,g0)
    c: Horizontal(g1)
    c: Coincident(g2,g1)
    c: Vertical(g2)
    c: Coincident(g3,g2)
    c: Coincident(g3,g0)
    c: Horizontal(g3)
    c: DistanceX(g1,g1) = 2.4
    c: DistanceY(g2,g2) = 2.4
    c: Symmetric(g0,g0,g-1)
    c: DistanceX(g-1,g0) = 3
FEATURE [Sketcher::SketchObject] Sketch045  label="blocco principale per neopixel"
  ArcFitTolerance = 1e-06
  AttachmentSupport = -> [XZ_Plane002]
  ExternalGeometry = -> [Sketch048]
  FullyConstrained = true
  MakeInternals = false
  MapMode = 5
  Placement = pos=(0,0,0) rot=(1,0,0;1.5708rad)
  sketch-geometry (6):
    g0: LineSegment StartX=0 StartY=5.1 StartZ=0 EndX=0 EndY=-5.1 EndZ=0
    g1: LineSegment StartX=0 StartY=-5.1 StartZ=0 EndX=3 EndY=-5.1 EndZ=0
    g2: LineSegment StartX=7 StartY=-1.1 StartZ=0 EndX=7 EndY=5.1 EndZ=0
    g3: LineSegment StartX=7 StartY=5.1 StartZ=0 EndX=0 EndY=5.1 EndZ=0
    g4: ArcOfCircle CenterX=3 CenterY=-1.1 CenterZ=0 NormalX=0 NormalY=0 NormalZ=1 AngleXU=0 Radius=4 StartAngle=4.71239 EndAngle=6.28319
    g5: GeomPoint [constr] X=7 Y=-5.1 Z=0
  constraints (15):
    c: Vertical(g0)
    c: Coincident(g1,g0)
    c: Horizontal(g1)
    c: Vertical(g2)
    c: Coincident(g3,g2)
    c: Coincident(g3,g0)
    c: Horizontal(g3)
    c: DistanceY(g0,g0) = 10.2
    c: Symmetric(g0,g0,g-1)
    c: DistanceX(g3,g3) = 7
    c: PointOnObject(g5,g2)
    c: PointOnObject(g5,g1)
    c: Tangent(g2,g4) = -1.5708
    c: Tangent(g1,g4) = -1.5708
    c: DistanceX(g-3,g1) = 0
FEATURE [Sketcher::SketchObject] Sketch049  label="rinforzi esterni per corpo neopoixel"
  ArcFitTolerance = 1e-06
  AttachmentSupport = -> [XZ_Plane002]
  ExternalGeometry = -> [Sketch045]
  FullyConstrained = true
  MakeInternals = false
  MapMode = 5
  Placement = pos=(0,0,0) rot=(1,0,0;1.5708rad)
  sketch-geometry (8):
    g0: LineSegment StartX=1 StartY=-4.1 StartZ=0 EndX=2 EndY=-4.1 EndZ=0
    g1: LineSegment StartX=2 StartY=-4.1 StartZ=0 EndX=2 EndY=-5.1 EndZ=0
    g2: LineSegment StartX=2 StartY=-5.1 StartZ=0 EndX=1 EndY=-5.1 EndZ=0
    g3: LineSegment StartX=1 StartY=-5.1 StartZ=0 EndX=1 EndY=-4.1 EndZ=0
    g4: LineSegment StartX=1 StartY=5.1 StartZ=0 EndX=2 EndY=5.1 EndZ=0
    g5: LineSegment StartX=2 StartY=5.1 StartZ=0 EndX=2 EndY=4.1 EndZ=0
    g6: LineSegment StartX=2 StartY=4.1 StartZ=0 EndX=1 EndY=4.1 EndZ=0
    g7: LineSegment StartX=1 StartY=4.1 StartZ=0 EndX=1 EndY=5.1 EndZ=0
  constraints (24):
    c: Horizontal(g0)
    c: Coincident(g1,g0)
    c: Vertical(g1)
    c: Coincident(g2,g1)
    c: Horizontal(g2)
    c: Coincident(g3,g2)
    c: Coincident(g3,g0)
    c: Vertical(g3)
    c: Horizontal(g4)
    c: Coincident(g5,g4)
    c: Vertical(g5)
    c: Coincident(g6,g5)
    c: Horizontal(g6)
    c: Coincident(g7,g6)
    c: Coincident(g7,g4)
    c: Vertical(g7)
    c: DistanceX(g4,g4) = 1
    c: DistanceY(g5,g5) = 1
    c: DistanceX(g0,g0) = 1
    c: DistanceY(g1,g1) = 1
    c: DistanceX(g-3,g4) = 1
    c: DistanceY(g-3,g4) = 0
    c: DistanceX(g-4,g2) = 1
    c: DistanceY(g2,g-4) = 0
FEATURE [Sketcher::SketchObject] Sketch052  label="scavo saldature driver solenoide"
  ArcFitTolerance = 1e-06
  AttachmentSupport = -> [XZ_Plane]
  ExternalGeometry = -> [Sketch038]
  FullyConstrained = true
  MakeInternals = false
  MapMode = 5
  Placement = pos=(0,0,0) rot=(1,0,0;1.5708rad)
  sketch-geometry (4):
    g0: LineSegment StartX=-195.304 StartY=-6.5806 StartZ=0 EndX=-196.994 EndY=-10.2058 EndZ=0
    g1: LineSegment StartX=-196.994 StartY=-10.2058 StartZ=0 EndX=-196.632 EndY=-10.3749 EndZ=0
    g2: LineSegment StartX=-196.632 StartY=-10.3749 StartZ=0 EndX=-194.941 EndY=-6.74965 EndZ=0
    g3: LineSegment StartX=-194.941 StartY=-6.74965 StartZ=0 EndX=-195.304 EndY=-6.5806 EndZ=0
  constraints (11):
    c: Coincident(g1,g0)
    c: Coincident(g2,g1)
    c: Coincident(g3,g2)
    c: Coincident(g3,g0)
    c: Parallel(g2,g0)
    c: Perpendicular(g2,g3)
    c: Perpendicular(g1,g2,g1) = 1.5708
    c: Parallel(g2,g-3)
    c: Distance(g2) = 4
    c: Distance(g3) = 0.4
    c: Coincident(g2,g-3)
FEATURE [Part::Extrusion] Extrude055  label="Extrude scavo saldature driver solenoide"
  Base = -> Sketch052
  Dir = (0,-1,2e-16)
  DirMode = 2
  FaceMakerClass = Part::FaceMakerBullseye
  FaceMakerMode = 3
  LengthFwd = 6
  LengthRev = 0
  Solid = true
  Symmetric = true
FEATURE [Sketcher::SketchObject] Sketch053  label="scavo saldature rumble"
  ArcFitTolerance = 1e-06
  AttachmentSupport = -> [XZ_Plane]
  ExternalGeometry = -> [Sketch019]
  FullyConstrained = true
  MakeInternals = false
  MapMode = 5
  Placement = pos=(0,0,0) rot=(1,0,0;1.5708rad)
  sketch-geometry (4):
    g0: LineSegment StartX=-169.451 StartY=-56.8615 StartZ=0 EndX=-170.687 EndY=-60.6657 EndZ=0
    g1: LineSegment StartX=-170.687 StartY=-60.6657 StartZ=0 EndX=-169.546 EndY=-61.0365 EndZ=0
    g2: LineSegment StartX=-169.546 StartY=-61.0365 StartZ=0 EndX=-168.31 EndY=-57.2323 EndZ=0
    g3: LineSegment StartX=-168.31 StartY=-57.2323 StartZ=0 EndX=-169.451 EndY=-56.8615 EndZ=0
  constraints (11):
    c: Coincident(g1,g0)
    c: Coincident(g2,g1)
    c: Coincident(g3,g2)
    c: Coincident(g3,g0)
    c: Parallel(g0,g2)
    c: Perpendicular(g3,g0)
    c: Perpendicular(g1,g0)
    c: Parallel(g0,g-3)
    c: Distance(g0) = 4
    c: Coincident(g0,g-3)
    c: Distance(g1) = 1.2
FEATURE [Part::Extrusion] Extrude056  label="Extrude scavo saldature rumble"
  Base = -> Sketch053
  Dir = (0,-1,2e-16)
  DirMode = 2
  FaceMakerClass = Part::FaceMakerBullseye
  FaceMakerMode = 3
  LengthFwd = 8.4
  LengthRev = 0
  Solid = true
  Symmetric = true
FEATURE [Sketcher::SketchObject] Sketch054  label="scavo saldature alimentatore connettore USB"
  ArcFitTolerance = 1e-06
  AttachmentSupport = -> [XZ_Plane]
  ExternalGeometry = -> [Sketch037]
  FullyConstrained = true
  MakeInternals = false
  MapMode = 5
  Placement = pos=(0,0,0) rot=(1,0,0;1.5708rad)
  sketch-geometry (4):
    g0: LineSegment StartX=-209.575 StartY=-80.4316 StartZ=0 EndX=-210.375 EndY=-80.4316 EndZ=0
    g1: LineSegment StartX=-210.375 StartY=-80.4316 StartZ=0 EndX=-210.375 EndY=-72.4316 EndZ=0
    g2: LineSegment StartX=-210.375 StartY=-72.4316 StartZ=0 EndX=-209.575 EndY=-72.4316 EndZ=0
    g3: LineSegment StartX=-209.575 StartY=-72.4316 StartZ=0 EndX=-209.575 EndY=-80.4316 EndZ=0
  constraints (11):
    c: Horizontal(g0)
    c: Coincident(g1,g0)
    c: Vertical(g1)
    c: Coincident(g2,g1)
    c: Horizontal(g2)
    c: Coincident(g3,g2)
    c: Coincident(g3,g0)
    c: Vertical(g3)
    c: DistanceX(g0,g0) = 0.8
    c: DistanceY(g3,g3) = 8
    c: Coincident(g0,g-4)
FEATURE [Part::Extrusion] Extrude057  label="Extrude scavo saldature alimentatore connettore USB"
  Base = -> Sketch054
  Dir = (0,-1,2e-16)
  DirMode = 2
  FaceMakerClass = Part::FaceMakerBullseye
  FaceMakerMode = 3
  LengthFwd = 11
  LengthRev = 0
  Solid = true
  Symmetric = true
FEATURE [Sketcher::SketchObject] Sketch055  label="buco interno per micro switch"
  ArcFitTolerance = 1e-06
  AttachmentSupport = -> [XZ_Plane]
  ExternalGeometry = -> [Sketch]
  FullyConstrained = true
  MakeInternals = false
  MapMode = 5
  Placement = pos=(0,0,0) rot=(1,0,0;1.5708rad)
  sketch-geometry (11):
    g0: LineSegment [constr] StartX=-194.483 StartY=34.2854 StartZ=0 EndX=-196.022 EndY=30.0568 EndZ=0
    g1: LineSegment [constr] StartX=-196.022 StartY=30.0568 StartZ=0 EndX=-197.561 EndY=25.8282 EndZ=0
    g2: LineSegment [constr] StartX=-196.022 StartY=30.0568 StartZ=0 EndX=-194.143 EndY=29.3727 EndZ=0
    g3: LineSegment [constr] StartX=-196.022 StartY=30.0568 StartZ=0 EndX=-197.902 EndY=30.7408 EndZ=0
    g4: LineSegment StartX=-196.362 StartY=34.9694 StartZ=0 EndX=-192.604 EndY=33.6014 EndZ=0
    g5: LineSegment StartX=-199.441 StartY=26.5122 StartZ=0 EndX=-195.682 EndY=25.1441 EndZ=0
    g6: LineSegment StartX=-192.604 StartY=33.6014 StartZ=0 EndX=-195.682 EndY=25.1441 EndZ=0
    g7: LineSegment StartX=-196.362 StartY=34.9694 StartZ=0 EndX=-199.441 EndY=26.5122 EndZ=0
    g8: GeomPoint [constr] X=-187.821 Y=29.2 Z=0
    g9: LineSegment [constr] StartX=-188.505 StartY=27.3206 StartZ=0 EndX=-196.022 EndY=30.0568 EndZ=0
    g10: LineSegment [constr] StartX=-187.821 StartY=29.2 StartZ=0 EndX=-188.505 EndY=27.3206 EndZ=0
  constraints (27):
    c: Coincident(g2,g0)
    c: Parallel(g0,g-3)
    c: Tangent(g1,g0) = -1.5708
    c: Perpendicular(g0,g2)
    c: Tangent(g2,g3)
    c: Distance(g0,g1) = 9
    c: Equal(g0,g1)
    c: Distance(g3,g2) = 4
    c: Equal(g2,g3)
    c: Parallel(g3,g4)
    c: Symmetric(g4,g4,g0)
    c: Parallel(g6,g1)
    c: Parallel(g7,g1)
    c: Symmetric(g6,g6,g2)
    c: Symmetric(g5,g5,g1)
    c: Symmetric(g7,g7,g3)
    c: Coincident(g7,g4)
    c: Coincident(g6,g4)
    c: Coincident(g5,g6)
    c: Symmetric(g-3,g-3,g8)
    c: Perpendicular(g-3,g9)
    c: Distance(g9) = 8
    c: Coincident(g3,g9)
    c: Coincident(g10,g8)
    c: Parallel(g10,g-3)
    c: Distance(g10) = 2
    c: Coincident(g10,g9)
FEATURE [Sketcher::SketchObject] Sketch056  label="buco esterno per micro switch"
  ArcFitTolerance = 1e-06
  AttachmentSupport = -> [XZ_Plane]
  ExternalGeometry = -> [Sketch055]
  FullyConstrained = true
  MakeInternals = false
  MapMode = 5
  Placement = pos=(0,0,0) rot=(1,0,0;1.5708rad)
  sketch-geometry (17):
    g0: GeomPoint [constr] X=-194.143 Y=29.3727 Z=0
    g1: GeomPoint [constr] X=-194.483 Y=34.2854 Z=0
    g2: GeomPoint [constr] X=-197.902 Y=30.7408 Z=0
    g3: GeomPoint [constr] X=-197.561 Y=25.8282 Z=0
    g4: GeomPoint [constr] X=-196.022 Y=30.0568 Z=0
    g5: LineSegment [constr] StartX=-194.483 StartY=34.2854 StartZ=0 EndX=-196.022 EndY=30.0568 EndZ=0
    g6: LineSegment [constr] StartX=-196.022 StartY=30.0568 StartZ=0 EndX=-197.561 EndY=25.8282 EndZ=0
    g7: LineSegment [constr] StartX=-197.902 StartY=30.7408 StartZ=0 EndX=-196.022 EndY=30.0568 EndZ=0
    g8: LineSegment [constr] StartX=-196.022 StartY=30.0568 StartZ=0 EndX=-194.143 EndY=29.3727 EndZ=0
    g9: LineSegment [constr] StartX=-195.338 StartY=31.9362 StartZ=0 EndX=-196.022 EndY=30.0568 EndZ=0
    g10: LineSegment [constr] StartX=-196.022 StartY=30.0568 StartZ=0 EndX=-196.706 EndY=28.1774 EndZ=0
    g11: LineSegment [constr] StartX=-196.022 StartY=30.0568 StartZ=0 EndX=-196.821 EndY=30.3475 EndZ=0
    g12: LineSegment [constr] StartX=-196.022 StartY=30.0568 StartZ=0 EndX=-195.223 EndY=29.7661 EndZ=0
    g13: LineSegment StartX=-194.539 StartY=31.6454 StartZ=0 EndX=-195.907 EndY=27.8867 EndZ=0
    g14: LineSegment StartX=-196.137 StartY=32.2269 StartZ=0 EndX=-197.505 EndY=28.4681 EndZ=0
    g15: LineSegment StartX=-196.137 StartY=32.2269 StartZ=0 EndX=-194.539 EndY=31.6454 EndZ=0
    g16: LineSegment StartX=-197.505 StartY=28.4681 StartZ=0 EndX=-195.907 EndY=27.8867 EndZ=0
  constraints (34):
    c: Symmetric(g-5,g-5,g1)
    c: Symmetric(g-5,g-6,g0)
    c: Symmetric(g-6,g-6,g3)
    c: Symmetric(g-5,g-6,g2)
    c: Coincident(g5,g1)
    c: Coincident(g5,g4)
    c: Coincident(g6,g4)
    c: Coincident(g6,g3)
    c: Equal(g5,g6)
    c: Coincident(g7,g2)
    c: Coincident(g7,g4)
    c: Coincident(g8,g4)
    c: Coincident(g8,g0)
    c: Equal(g7,g8)
    c: Coincident(g11,g9)
    c: Coincident(g12,g9)
    c: Tangent(g10,g9) = -1.5708
    c: Perpendicular(g11,g9)
    c: Parallel(g9,g-4)
    c: Equal(g9,g10)
    c: Parallel(g12,g11)
    c: Equal(g11,g12)
    c: Distance(g11,g12) = 1.7
    c: Distance(g9,g10) = 4
    c: Symmetric(g13,g13,g12)
    c: Parallel(g13,g9)
    c: Symmetric(g14,g14,g11)
    c: Symmetric(g15,g15,g9)
    c: Parallel(g15,g11)
    c: Symmetric(g16,g16,g10)
    c: Coincident(g16,g14)
    c: Coincident(g15,g14)
    c: Coincident(g13,g15)
    c: Coincident(g9,g4)
FEATURE [Sketcher::SketchObject] Sketch057  label="buco interno per SWITCH"
  ArcFitTolerance = 1e-06
  AttachmentSupport = -> [XZ_Plane]
  ExternalGeometry = -> [Sketch]
  FullyConstrained = true
  MakeInternals = false
  MapMode = 5
  Placement = pos=(0,0,0) rot=(1,0,0;1.5708rad)
  sketch-geometry (10):
    g0: GeomPoint [constr] X=-187.821 Y=29.2 Z=0
    g1: LineSegment [constr] StartX=-188.505 StartY=27.3206 StartZ=0 EndX=-193.203 EndY=29.0307 EndZ=0
    g2: LineSegment [constr] StartX=-190.809 StartY=35.6086 StartZ=0 EndX=-195.597 EndY=22.4529 EndZ=0
    g3: GeomPoint [constr] X=-193.203 Y=29.0307 Z=0
    g4: LineSegment [constr] StartX=-196.492 StartY=30.2278 StartZ=0 EndX=-189.914 EndY=27.8336 EndZ=0
    g5: LineSegment StartX=-194.098 StartY=36.8056 StartZ=0 EndX=-187.52 EndY=34.4115 EndZ=0
    g6: LineSegment StartX=-194.098 StartY=36.8056 StartZ=0 EndX=-198.886 EndY=23.6499 EndZ=0
    g7: LineSegment StartX=-187.52 StartY=34.4115 StartZ=0 EndX=-192.308 EndY=21.2558 EndZ=0
    g8: LineSegment StartX=-198.886 StartY=23.6499 StartZ=0 EndX=-192.308 EndY=21.2558 EndZ=0
    g9: LineSegment [constr] StartX=-187.821 StartY=29.2 StartZ=0 EndX=-188.505 EndY=27.3206 EndZ=0
  constraints (23):
    c: Symmetric(g-3,g-3,g0)
    c: Perpendicular(g1,g-3)
    c: Parallel(g2,g-3)
    c: Symmetric(g2,g2,g3)
    c: Perpendicular(g2,g4)
    c: Symmetric(g4,g4,g3)
    c: Distance(g2) = 14
    c: Distance(g4) = 7
    c: Distance(g1) = 5
    c: Parallel(g5,g4)
    c: Parallel(g7,g2)
    c: Symmetric(g5,g5,g2)
    c: Symmetric(g6,g6,g4)
    c: Symmetric(g7,g7,g4)
    c: Symmetric(g8,g8,g2)
    c: Coincident(g6,g5)
    c: Coincident(g7,g5)
    c: Coincident(g8,g7)
    c: Coincident(g3,g1)
    c: Coincident(g9,g0)
    c: Parallel(g9,g-3)
    c: Distance(g9) = 2
    c: Coincident(g1,g9)
FEATURE [Sketcher::SketchObject] Sketch058  label="buco esterno per SWITCH"
  ArcFitTolerance = 1e-06
  AttachmentSupport = -> [XZ_Plane]
  ExternalGeometry = -> [Sketch057]
  FullyConstrained = true
  MakeInternals = false
  MapMode = 5
  Placement = pos=(0,0,0) rot=(1,0,0;1.5708rad)
  sketch-geometry (12):
    g0: GeomPoint [constr] X=-190.809 Y=35.6086 Z=0
    g1: GeomPoint [constr] X=-196.492 Y=30.2278 Z=0
    g2: GeomPoint [constr] X=-189.914 Y=27.8336 Z=0
    g3: GeomPoint [constr] X=-195.597 Y=22.4529 Z=0
    g4: GeomPoint [constr] X=-193.203 Y=29.0307 Z=0
    g5: LineSegment [constr] StartX=-192.006 StartY=32.3196 StartZ=0 EndX=-194.4 EndY=25.7418 EndZ=0
    g6: GeomPoint [constr] X=-193.203 Y=29.0307 Z=0
    g7: LineSegment [constr] StartX=-195.082 StartY=29.7148 StartZ=0 EndX=-191.324 EndY=28.3467 EndZ=0
    g8: LineSegment StartX=-193.885 StartY=33.0037 StartZ=0 EndX=-190.127 EndY=31.6356 EndZ=0
    g9: LineSegment StartX=-190.127 StartY=31.6356 StartZ=0 EndX=-192.521 EndY=25.0578 EndZ=0
    g10: LineSegment StartX=-196.28 StartY=26.4258 StartZ=0 EndX=-192.521 EndY=25.0578 EndZ=0
    g11: LineSegment StartX=-193.885 StartY=33.0037 StartZ=0 EndX=-196.28 EndY=26.4258 EndZ=0
  constraints (21):
    c: Symmetric(g-6,g-6,g3)
    c: Symmetric(g-4,g-6,g2)
    c: Symmetric(g-5,g-4,g0)
    c: Symmetric(g-5,g-6,g1)
    c: Symmetric(g1,g2,g4)
    c: Parallel(g5,g-4)
    c: Symmetric(g5,g5,g6)
    c: Perpendicular(g7,g5)
    c: Symmetric(g7,g7,g6)
    c: Distance(g5) = 7
    c: Distance(g7) = 4
    c: Parallel(g8,g7)
    c: Parallel(g11,g5)
    c: Symmetric(g8,g8,g5)
    c: Symmetric(g9,g9,g7)
    c: Symmetric(g10,g10,g5)
    c: Symmetric(g11,g11,g7)
    c: Coincident(g11,g8)
    c: Coincident(g9,g8)
    c: Coincident(g9,g10)
    c: Coincident(g6,g4)
FEATURE [Part::Extrusion] Extrude060  label="Extrude buco interno per SWITCH destro"
  Base = -> Sketch057
  Dir = (0,-1,2e-16)
  DirMode = 2
  FaceMakerClass = Part::FaceMakerBullseye
  FaceMakerMode = 3
  LengthFwd = 13.2
  LengthRev = 0
  Placement = pos=(0,2.6,0) rot=(0,0,1;0rad)
  Solid = true
  Symmetric = false
FEATURE [Part::Extrusion] Extrude061  label="Extrude buco esterno per SWITCH destro"
  Base = -> Sketch058
  Dir = (0,-1,2e-16)
  DirMode = 2
  FaceMakerClass = Part::FaceMakerBullseye
  FaceMakerMode = 3
  LengthFwd = 2
  LengthRev = 0
  Placement = pos=(0,-10.6,0) rot=(0,0,1;0rad)
  Solid = true
  Symmetric = false
FEATURE [Sketcher::SketchObject] Sketch059  label="buco per spazio introduzione SWITCH"
  ArcFitTolerance = 1e-06
  AttachmentSupport = -> [XZ_Plane]
  ExternalGeometry = -> [Sketch057,Sketch010]
  FullyConstrained = true
  MakeInternals = false
  MapMode = 5
  Placement = pos=(0,0,0) rot=(1,0,0;1.5708rad)
  sketch-geometry (8):
    g0: LineSegment [constr] StartX=-201.368 StartY=36.3521 StartZ=0 EndX=-195.094 EndY=34.0687 EndZ=0
    g1: LineSegment [constr] StartX=-194.098 StartY=36.8056 StartZ=0 EndX=-195.094 EndY=34.0687 EndZ=0
    g2: LineSegment StartX=-198.658 StartY=24.2771 StartZ=0 EndX=-199.654 EndY=21.5401 EndZ=0
    g3: LineSegment StartX=-199.654 StartY=21.5401 StartZ=0 EndX=-181.196 EndY=14.822 EndZ=0
    g4: LineSegment StartX=-181.196 StartY=14.822 StartZ=0 EndX=-180.2 EndY=17.559 EndZ=0
    g5: LineSegment StartX=-180.2 StartY=17.559 StartZ=0 EndX=-198.658 EndY=24.2771 EndZ=0
    g6: LineSegment [constr] StartX=-204.932 StartY=26.5605 StartZ=0 EndX=-198.658 EndY=24.2771 EndZ=0
    g7: LineSegment [constr] StartX=-198.658 StartY=24.2771 StartZ=0 EndX=-199.654 EndY=21.5401 EndZ=0
  constraints (20):
    c: Parallel(g1,g-3)
    c: Parallel(g0,g-4)
    c: Coincident(g0,g-4)
    c: Coincident(g1,g-3)
    c: Coincident(g0,g1)
    c: Coincident(g3,g2)
    c: Coincident(g4,g3)
    c: Coincident(g5,g4)
    c: Coincident(g5,g2)
    c: Parallel(g5,g-5)
    c: Parallel(g3,g-5)
    c: Parallel(g4,g-6)
    c: DistanceX(g-6,g4) = 0
    c: Coincident(g6,g-5)
    c: Equal(g6,g0)
    c: Coincident(g7,g6)
    c: Equal(g7,g1)
    c: Tangent(g7,g-3)
    c: Coincident(g2,g6)
    c: Coincident(g2,g7)
FEATURE [Part::Extrusion] Extrude062  label="Extrude buco per spazio introduzione SWITCH"
  Base = -> Sketch059
  Dir = (0,-1,2e-16)
  DirMode = 2
  FaceMakerClass = Part::FaceMakerBullseye
  FaceMakerMode = 3
  LengthFwd = 13.2
  LengthRev = 0
  Solid = true
  Symmetric = true
FEATURE [Part::Extrusion] Extrude063  label="Extrude buco interno per SWITCH sinistro"
  Base = -> Sketch057
  Dir = (0,-1,2e-16)
  DirMode = 2
  FaceMakerClass = Part::FaceMakerBullseye
  FaceMakerMode = 3
  LengthFwd = 13.2
  LengthRev = 0
  Placement = pos=(0,10.6,0) rot=(0,0,1;0rad)
  Solid = true
  Symmetric = false
FEATURE [Part::Extrusion] Extrude064  label="Extrude buco esterno per SWITCH sinistro"
  Base = -> Sketch058
  Dir = (0,-1,2e-16)
  DirMode = 2
  FaceMakerClass = Part::FaceMakerBullseye
  FaceMakerMode = 3
  LengthFwd = 2
  LengthRev = 0
  Placement = pos=(0,12.6,0) rot=(0,0,1;0rad)
  Solid = true
  Symmetric = false
FEATURE [Sketcher::SketchObject] Sketch061  label="struttura esterna blocco switch"
  ArcFitTolerance = 1e-06
  AttachmentSupport = -> [XZ_Plane003]
  FullyConstrained = true
  MakeInternals = false
  MapMode = 5
  Placement = pos=(0,0,0) rot=(1,0,0;1.5708rad)
  sketch-geometry (5):
    g0: LineSegment StartX=-1 StartY=-5.1 StartZ=0 EndX=1 EndY=-5.1 EndZ=0
    g1: LineSegment StartX=1 StartY=-5.1 StartZ=0 EndX=1 EndY=5.1 EndZ=0
    g2: LineSegment StartX=1 StartY=5.1 StartZ=0 EndX=-1 EndY=5.1 EndZ=0
    g3: LineSegment StartX=-1 StartY=5.1 StartZ=0 EndX=-1 EndY=-5.1 EndZ=0
    g4: GeomPoint [constr] X=0 Y=0 Z=0
  constraints (12):
    c: Coincident(g0,g1)
    c: Coincident(g1,g2)
    c: Coincident(g2,g3)
    c: Coincident(g3,g0)
    c: Horizontal(g0)
    c: Horizontal(g2)
    c: Vertical(g1)
    c: Vertical(g3)
    c: Symmetric(g2,g0,g4)
    c: Distance(g1,g3) = 2
    c: Distance(g0,g2) = 10.2
    c: Coincident(g4,g-1)
FEATURE [Sketcher::SketchObject] Sketch062  label="struttura interna blocco switch"
  ArcFitTolerance = 1e-06
  AttachmentSupport = -> [XZ_Plane003]
  ExternalGeometry = -> [Sketch061]
  FullyConstrained = true
  MakeInternals = false
  MapMode = 5
  Placement = pos=(0,0,0) rot=(1,0,0;1.5708rad)
  sketch-geometry (5):
    g0: LineSegment StartX=-1 StartY=3.1 StartZ=0 EndX=-1 EndY=-3.1 EndZ=0
    g1: LineSegment StartX=-1 StartY=-3.1 StartZ=0 EndX=1 EndY=-3.1 EndZ=0
    g2: LineSegment StartX=1 StartY=-3.1 StartZ=0 EndX=1 EndY=3.1 EndZ=0
    g3: LineSegment StartX=1 StartY=3.1 StartZ=0 EndX=-1 EndY=3.1 EndZ=0
    g4: GeomPoint [constr] X=0 Y=0 Z=0
  constraints (12):
    c: Coincident(g0,g1)
    c: Coincident(g1,g2)
    c: Coincident(g2,g3)
    c: Coincident(g3,g0)
    c: Vertical(g0)
    c: Vertical(g2)
    c: Horizontal(g1)
    c: Horizontal(g3)
    c: Symmetric(g2,g0,g4)
    c: Coincident(g4,g-1)
    c: Distance(g0) = 6.2
    c: Equal(g3,g-3)
FEATURE [Sketcher::SketchObject] Sketch063  label="blocchi tra switch"
  ArcFitTolerance = 1e-06
  AttachmentSupport = -> [XZ_Plane003]
  ExternalGeometry = -> [Sketch061,Sketch062]
  FullyConstrained = true
  MakeInternals = false
  MapMode = 5
  Placement = pos=(0,0,0) rot=(1,0,0;1.5708rad)
  sketch-geometry (8):
    g0: LineSegment StartX=-3 StartY=5.1 StartZ=0 EndX=-1 EndY=5.1 EndZ=0
    g1: LineSegment StartX=-1 StartY=5.1 StartZ=0 EndX=-1 EndY=3.1 EndZ=0
    g2: LineSegment StartX=-1 StartY=3.1 StartZ=0 EndX=-3 EndY=3.1 EndZ=0
    g3: LineSegment StartX=-3 StartY=3.1 StartZ=0 EndX=-3 EndY=5.1 EndZ=0
    g4: LineSegment StartX=-3 StartY=-3.1 StartZ=0 EndX=-1 EndY=-3.1 EndZ=0
    g5: LineSegment StartX=-1 StartY=-3.1 StartZ=0 EndX=-1 EndY=-5.1 EndZ=0
    g6: LineSegment StartX=-1 StartY=-5.1 StartZ=0 EndX=-3 EndY=-5.1 EndZ=0
    g7: LineSegment StartX=-3 StartY=-5.1 StartZ=0 EndX=-3 EndY=-3.1 EndZ=0
  constraints (20):
    c: Horizontal(g0)
    c: Coincident(g1,g0)
    c: Coincident(g2,g1)
    c: Horizontal(g2)
    c: Coincident(g3,g2)
    c: Coincident(g3,g0)
    c: Vertical(g3)
    c: Horizontal(g4)
    c: Coincident(g5,g4)
    c: Coincident(g6,g5)
    c: Horizontal(g6)
    c: Coincident(g7,g6)
    c: Coincident(g7,g4)
    c: Vertical(g7)
    c: Coincident(g0,g-4)
    c: Coincident(g1,g-5)
    c: Coincident(g4,g-6)
    c: Coincident(g5,g-7)
    c: Distance(g0) = 2
    c: Distance(g4) = 2
FEATURE [Sketcher::SketchObject] Sketch066  label="piano per rampino"
  ArcFitTolerance = 1e-06
  AttachmentSupport = -> [XZ_Plane002]
  ExternalGeometry = -> [Sketch045]
  FullyConstrained = true
  MakeInternals = false
  MapMode = 5
  Placement = pos=(0,0,0) rot=(1,0,0;1.5708rad)
  sketch-geometry (4):
    g0: LineSegment StartX=5.4 StartY=5.1 StartZ=0 EndX=5.4 EndY=3.9 EndZ=0
    g1: LineSegment StartX=5.4 StartY=3.9 StartZ=0 EndX=7 EndY=3.9 EndZ=0
    g2: LineSegment StartX=7 StartY=3.9 StartZ=0 EndX=7 EndY=5.1 EndZ=0
    g3: LineSegment StartX=7 StartY=5.1 StartZ=0 EndX=5.4 EndY=5.1 EndZ=0
  constraints (11):
    c: Coincident(g0,g1)
    c: Coincident(g1,g2)
    c: Coincident(g2,g3)
    c: Coincident(g3,g0)
    c: Vertical(g0)
    c: Vertical(g2)
    c: Horizontal(g1)
    c: Horizontal(g3)
    c: Distance(g0,g2) = 1.6
    c: Distance(g1,g3) = 1.2
    c: Coincident(g2,g-3)
FEATURE [Sketcher::SketchObject] Sketch064  label="rampini_per_serraggio_struttura"
  ArcFitTolerance = 1e-06
  AttachmentSupport = -> [XZ_Plane002]
  ExternalGeometry = -> [Sketch066,Sketch045]
  FullyConstrained = true
  MakeInternals = false
  MapMode = 5
  Placement = pos=(0,0,0) rot=(1,0,0;1.5708rad)
  sketch-geometry (7):
    g0: LineSegment StartX=7 StartY=5.1 StartZ=0 EndX=7 EndY=3.9 EndZ=0
    g1: LineSegment StartX=7 StartY=3.9 StartZ=0 EndX=9 EndY=3.9 EndZ=0
    g2: LineSegment StartX=7 StartY=5.1 StartZ=0 EndX=7 EndY=5.1 EndZ=0
    g3: LineSegment StartX=7 StartY=5.1 StartZ=0 EndX=7 EndY=7.5 EndZ=0
    g4: LineSegment StartX=9 StartY=5.1 StartZ=0 EndX=9 EndY=3.9 EndZ=0
    g5: LineSegment StartX=7 StartY=7.5 StartZ=0 EndX=9 EndY=7.5 EndZ=0
    g6: LineSegment StartX=9 StartY=7.5 StartZ=0 EndX=9 EndY=5.1 EndZ=0
  constraints (20):
    c: Vertical(g0)
    c: Coincident(g1,g0)
    c: Horizontal(g1)
    c: Coincident(g2,g0)
    c: Horizontal(g2)
    c: Coincident(g3,g2)
    c: Vertical(g3)
    c: Coincident(g5,g3)
    c: Coincident(g4,g6)
    c: Coincident(g4,g1)
    c: Vertical(g4)
    c: Coincident(g0,g-3)
    c: DistanceY(g-4,g3) = 2.4
    c: DistanceX(g1,g1) = 2
    c: DistanceY(g2,g6) = 0
    c: DistanceX(g2,g2) = 0
    c: DistanceY(g0,g0) = 1.2
    c: Coincident(g5,g6)
    c: Horizontal(g5)
    c: Vertical(g6)
FEATURE [Sketcher::SketchObject] Sketch067  label="perno per blocco switch"
  ArcFitTolerance = 1e-06
  AttachmentSupport = -> [XZ_Plane]
  ExternalGeometry = -> [Sketch,Sketch010]
  FullyConstrained = true
  MakeInternals = false
  MapMode = 5
  Placement = pos=(0,0,0) rot=(1,0,0;1.5708rad)
  sketch-geometry (14):
    g0: LineSegment StartX=-191.073 StartY=24.9429 StartZ=0 EndX=-185.81 EndY=23.0276 EndZ=0
    g1: LineSegment StartX=-183.76 StartY=23.9839 StartZ=0 EndX=-182.392 EndY=27.7427 EndZ=0
    g2: LineSegment StartX=-183.348 StartY=29.7934 StartZ=0 EndX=-188.61 EndY=31.7087 EndZ=0
    g3: LineSegment StartX=-188.61 StartY=31.7087 StartZ=0 EndX=-191.073 EndY=24.9429 EndZ=0
    g4: GeomPoint [constr] X=-186.459 Y=27.0946 Z=0
    g5: LineSegment StartX=-189.022 StartY=25.8992 StartZ=0 EndX=-185.263 EndY=24.5311 EndZ=0
    g6: LineSegment StartX=-185.263 StartY=24.5311 StartZ=0 EndX=-183.895 EndY=28.2899 EndZ=0
    g7: LineSegment StartX=-183.895 StartY=28.2899 StartZ=0 EndX=-187.654 EndY=29.658 EndZ=0
    g8: LineSegment StartX=-187.654 StartY=29.658 StartZ=0 EndX=-189.022 EndY=25.8992 EndZ=0
    g9: GeomPoint [constr] X=-186.459 Y=27.0946 Z=0
    g10: ArcOfCircle CenterX=-185.263 CenterY=24.5311 CenterZ=0 NormalX=0 NormalY=0 NormalZ=1 AngleXU=0 Radius=1.6 StartAngle=4.36332 EndAngle=5.93412
    g11: GeomPoint [constr] X=-184.307 Y=22.4804 Z=0
    g12: ArcOfCircle CenterX=-183.895 CenterY=28.2899 CenterZ=0 NormalX=0 NormalY=0 NormalZ=1 AngleXU=0 Radius=1.6 StartAngle=5.93412 EndAngle=7.50492
    g13: GeomPoint [constr] X=-181.844 Y=29.2462 Z=0
  constraints (30):
    c: Coincident(g2,g3)
    c: Coincident(g3,g0)
    c: Symmetric(g13,g0,g4)
    c: Distance(g11,g3) = 7.2
    c: Distance(g0,g2) = 7.2
    c: Parallel(g3,g1)
    c: Parallel(g2,g0)
    c: Perpendicular(g2,g3)
    c: Coincident(g5,g6)
    c: Coincident(g6,g7)
    c: Coincident(g7,g8)
    c: Coincident(g8,g5)
    c: Symmetric(g7,g5,g9)
    c: Distance(g6,g8) = 4
    c: Distance(g5,g7) = 4
    c: Coincident(g9,g4)
    c: Parallel(g8,g6)
    c: Parallel(g7,g5)
    c: Perpendicular(g7,g8)
    c: Tangent(g8,g-3)
    c: Tangent(g2,g-4)
    c: PointOnObject(g11,g1)
    c: PointOnObject(g11,g0)
    c: Tangent(g1,g10) = -1.5708
    c: Tangent(g0,g10) = -1.5708
    c: PointOnObject(g13,g1)
    c: Tangent(g1,g12) = -1.5708
    c: Tangent(g2,g12) = -1.5708
    c: Equal(g10,g12)
    c: Coincident(g10,g5)
FEATURE [Part::Extrusion] Extrude072  label="Extrude perno per blocco switch"
  Base = -> Sketch067
  Dir = (0,-1,2e-16)
  DirMode = 2
  FaceMakerClass = Part::FaceMakerBullseye
  FaceMakerMode = 3
  LengthFwd = 25.2
  LengthRev = 0
  Solid = true
  Symmetric = true
FEATURE [Part::MultiFuse] Fusion
  Refine = true
  Shapes = -> [Extrude,Sweep,Extrude007,Extrude011,Extrude005,Extrude012,Extrude013,Extrude016,Extrude031,Extrude039,Extrude045,Extrude072]
FEATURE [Part::Cut] Cut
  Base = -> Fusion
  Refine = true
  Tool = -> Extrude001
FEATURE [Part::Cut] Cut001
  Base = -> Cut
  Refine = true
  Tool = -> Extrude004
FEATURE [Part::Cut] Cut002
  Base = -> Cut001
  Refine = true
  Tool = -> Extrude006
FEATURE [Part::Cut] Cut003
  Base = -> Cut002
  Refine = true
  Tool = -> Extrude008
FEATURE [Part::Cut] Cut004
  Base = -> Cut003
  Refine = true
  Tool = -> Extrude009
FEATURE [Part::Cut] Cut005
  Base = -> Cut004
  Refine = true
  Tool = -> Extrude010
FEATURE [Part::Cut] Cut006
  Base = -> Cut005
  Refine = true
  Tool = -> Extrude014
FEATURE [Part::Cut] Cut007
  Base = -> Cut006
  Refine = true
  Tool = -> Extrude015
FEATURE [Part::Cut] Cut008
  Base = -> Cut007
  Refine = true
  Tool = -> Extrude018
FEATURE [Part::Cut] Cut009
  Base = -> Cut008
  Refine = true
  Tool = -> Extrude019
FEATURE [Part::Cut] Cut010
  Base = -> Cut009
  Refine = true
  Tool = -> Extrude020
FEATURE [Part::Cut] Cut011
  Base = -> Cut010
  Refine = true
  Tool = -> Extrude021
FEATURE [Part::Cut] Cut012
  Base = -> Cut011
  Refine = true
  Tool = -> Extrude022
FEATURE [Part::Cut] Cut013
  Base = -> Cut012
  Refine = true
  Tool = -> Extrude023
FEATURE [Part::Cut] Cut014
  Base = -> Cut013
  Refine = true
  Tool = -> Extrude032
FEATURE [Part::Cut] Cut015
  Base = -> Cut014
  Refine = true
  Tool = -> Extrude033
FEATURE [Part::Cut] Cut016
  Base = -> Cut015
  Refine = true
  Tool = -> Extrude034
FEATURE [Part::Cut] Cut017
  Base = -> Cut016
  Refine = true
  Tool = -> Extrude035
FEATURE [Part::Cut] Cut018
  Base = -> Cut017
  Refine = true
  Tool = -> Extrude036
FEATURE [Part::Cut] Cut019
  Base = -> Cut018
  Refine = true
  Tool = -> Extrude037
FEATURE [Part::Cut] Cut020
  Base = -> Cut019
  Refine = true
  Tool = -> Extrude030
FEATURE [Part::Cut] Cut022
  Base = -> Cut020
  Refine = true
  Tool = -> Extrude038
FEATURE [Part::Cut] Cut023
  Base = -> Cut022
  Refine = true
  Tool = -> Extrude041
FEATURE [Part::Cut] Cut024
  Base = -> Cut023
  Refine = true
  Tool = -> Extrude040
FEATURE [Part::Cut] Cut025
  Base = -> Cut024
  Refine = true
  Tool = -> Extrude042
FEATURE [Part::Cut] Cut026
  Base = -> Cut025
  Refine = true
  Tool = -> Extrude043
FEATURE [Part::Cut] Cut027
  Base = -> Cut026
  Refine = true
  Tool = -> Extrude044
FEATURE [Part::Cut] Cut028
  Base = -> Cut027
  Refine = true
  Tool = -> Extrude046
FEATURE [Part::Cut] Cut029
  Base = -> Cut028
  Refine = true
  Tool = -> Extrude047
FEATURE [Part::Cut] Cut033
  Base = -> Cut029
  Refine = true
  Tool = -> Extrude055
FEATURE [Part::Cut] Cut034
  Base = -> Cut033
  Refine = true
  Tool = -> Extrude056
FEATURE [Part::Cut] Cut035
  Base = -> Cut034
  Refine = true
  Tool = -> Extrude057
FEATURE [Part::Cut] Cut037
  Base = -> Cut035
  Refine = true
  Tool = -> Extrude060
FEATURE [Part::Cut] Cut038
  Base = -> Cut037
  Refine = true
  Tool = -> Extrude061
FEATURE [Part::Cut] Cut039
  Base = -> Cut038
  Refine = true
  Tool = -> Extrude063
FEATURE [Part::Cut] Cut040
  Base = -> Cut039
  Refine = true
  Tool = -> Extrude064
FEATURE [Part::Cut] Cut041
  Base = -> Cut040
  Refine = true
  Tool = -> Extrude062
FEATURE [Sketcher::SketchObject] Sketch068  label="base con smusso sopra neopixel"
  ArcFitTolerance = 1e-06
  AttachmentSupport = -> [YZ_Plane002]
  FullyConstrained = true
  MakeInternals = false
  MapMode = 5
  Placement = pos=(0,0,0) rot=(0.57735,0.57735,0.57735;2.0944rad)
  sketch-geometry (5):
    g0: LineSegment StartX=-9.5 StartY=-6.1 StartZ=0 EndX=9.5 EndY=-6.1 EndZ=0
    g1: LineSegment StartX=9.5 StartY=-6.1 StartZ=0 EndX=9.5 EndY=6.1 EndZ=0
    g2: LineSegment StartX=9.5 StartY=6.1 StartZ=0 EndX=-9.5 EndY=6.1 EndZ=0
    g3: LineSegment StartX=-9.5 StartY=6.1 StartZ=0 EndX=-9.5 EndY=-6.1 EndZ=0
    g4: GeomPoint [constr] X=0 Y=0 Z=0
  constraints (12):
    c: Coincident(g0,g1)
    c: Coincident(g1,g2)
    c: Coincident(g2,g3)
    c: Coincident(g3,g0)
    c: Horizontal(g0)
    c: Horizontal(g2)
    c: Vertical(g1)
    c: Vertical(g3)
    c: Symmetric(g2,g0,g4)
    c: Distance(g1,g3) = 19
    c: Distance(g0,g2) = 12.2
    c: Coincident(g4,g-1)
FEATURE [Sketcher::SketchObject] Sketch069  label="cilindro minore"
  ArcFitTolerance = 1e-06
  AttachmentSupport = -> [XZ_Plane004]
  FullyConstrained = true
  MakeInternals = false
  MapMode = 5
  Placement = pos=(0,0,0) rot=(1,0,0;1.5708rad)
  sketch-geometry (1):
    g0: Circle CenterX=0 CenterY=0 CenterZ=0 NormalX=0 NormalY=0 NormalZ=1 AngleXU=0 Radius=5.8
  constraints (2):
    c: Diameter(g0) = 11.6
    c: Coincident(g0,g-1)
FEATURE [Sketcher::SketchObject] Sketch070  label="cilindro maggiore"
  ArcFitTolerance = 1e-06
  AttachmentSupport = -> [XZ_Plane004]
  ExternalGeometry = -> [Sketch069]
  FullyConstrained = true
  MakeInternals = false
  MapMode = 5
  Placement = pos=(0,0,0) rot=(1,0,0;1.5708rad)
  sketch-geometry (1):
    g0: Circle CenterX=0 CenterY=0 CenterZ=0 NormalX=0 NormalY=0 NormalZ=1 AngleXU=0 Radius=6.5
  constraints (2):
    c: Coincident(g0,g-1)
    c: Diameter(g0) = 13
FEATURE [Sketcher::SketchObject] Sketch071  label="buco interno"
  ArcFitTolerance = 1e-06
  AttachmentSupport = -> [XZ_Plane004]
  ExternalGeometry = -> [Sketch069]
  FullyConstrained = true
  MakeInternals = false
  MapMode = 5
  Placement = pos=(0,0,0) rot=(1,0,0;1.5708rad)
  sketch-geometry (1):
    g0: Circle CenterX=0 CenterY=0 CenterZ=0 NormalX=0 NormalY=0 NormalZ=1 AngleXU=0 Radius=5
  constraints (2):
    c: Coincident(g0,g-1)
    c: Diameter(g0) = 10
FEATURE [PartDesign::Pad] Pad
  Direction = (0,-1,2e-16)
  Length = 1.2
  Length2 = 10
  Placement = pos=(0,0,0) rot=(1,0,0;1.5708rad)
  Profile = -> Sketch070
  ReferenceAxis = -> Sketch070 [N_Axis]
  Refine = true
  Suppressed = false
  Type = 0
FEATURE [PartDesign::Pad] Pad001
  BaseFeature = -> Pad
  Direction = (0,-1,2e-16)
  Length = 5.6
  Length2 = 10
  Placement = pos=(0,0,0) rot=(1,0,0;1.5708rad)
  Profile = -> Sketch069
  ReferenceAxis = -> Sketch069 [N_Axis]
  Refine = true
  Suppressed = false
  Type = 0
FEATURE [PartDesign::Pocket] Pocket
  BaseFeature = -> Pad001
  Direction = (0,1,-2e-16)
  Length = 7
  Length2 = 5
  Midplane = true
  Placement = pos=(0,0,0) rot=(1,0,0;1.5708rad)
  Profile = -> Sketch071
  ReferenceAxis = -> Sketch071 [N_Axis]
  Refine = true
  Suppressed = false
  Type = 0
FEATURE [PartDesign::Fillet] Fillet
  Base = -> Pocket [Face7]
  BaseFeature = -> Pocket
  Placement = pos=(0,0,0) rot=(1,0,0;1.5708rad)
  Radius = 1
  Refine = true
  SupportTransform = false
  Suppressed = false
  UseAllEdges = false
FEATURE [PartDesign::Body] Body004  label="pulsanti lato sinistro"
  AllowCompound = false
  Group = -> [Sketch069,Sketch070,Sketch071,Pad,Pad001,Pocket,Fillet]
  Origin = -> Origin004
  Tip = -> Fillet
FEATURE [Sketcher::SketchObject] Sketch072  label="buco per saldature e diodo driver solenoide"
  ArcFitTolerance = 1e-06
  AttachmentSupport = -> [XZ_Plane]
  ExternalGeometry = -> [Sketch038]
  FullyConstrained = true
  MakeInternals = false
  MapMode = 5
  Placement = pos=(0,0,0) rot=(1,0,0;1.5708rad)
  sketch-geometry (4):
    g0: LineSegment StartX=-212.269 StartY=-43.9083 StartZ=0 EndX=-207.197 EndY=-33.0326 EndZ=0
    g1: LineSegment StartX=-207.197 StartY=-33.0326 StartZ=0 EndX=-207.56 EndY=-32.8635 EndZ=0
    g2: LineSegment StartX=-207.56 StartY=-32.8635 StartZ=0 EndX=-212.631 EndY=-43.7392 EndZ=0
    g3: LineSegment StartX=-212.631 StartY=-43.7392 StartZ=0 EndX=-212.269 EndY=-43.9083 EndZ=0
  constraints (11):
    c: Coincident(g1,g0)
    c: Coincident(g2,g1)
    c: Coincident(g3,g2)
    c: Coincident(g3,g0)
    c: Parallel(g-3,g0)
    c: Parallel(g0,g2)
    c: Perpendicular(g0,g3)
    c: Perpendicular(g1,g0)
    c: Distance(g3) = 0.4
    c: Distance(g2) = 12
    c: Coincident(g0,g-3)
FEATURE [Part::Extrusion] Extrude074  label="Extrude buco per saldature e diodo driver solenoide"
  Base = -> Sketch072
  Dir = (0,-1,2e-16)
  DirMode = 2
  FaceMakerClass = Part::FaceMakerBullseye
  FaceMakerMode = 3
  LengthFwd = 14.6
  LengthRev = 0
  Solid = true
  Symmetric = true
FEATURE [Part::Cut] Cut042
  Base = -> Cut041
  Refine = true
  Tool = -> Extrude074
FEATURE [Sketcher::SketchObject] Sketch073  label="fori slargati blocco solenoide"
  ArcFitTolerance = 1e-06
  AttachmentSupport = -> [XY_Plane]
  ExternalGeometry = -> [Sketch030]
  FullyConstrained = true
  MakeInternals = false
  MapMode = 5
  sketch-geometry (2):
    g0: Circle CenterX=-152.209 CenterY=6.95 CenterZ=0 NormalX=0 NormalY=0 NormalZ=1 AngleXU=0 Radius=3.7
    g1: Circle CenterX=-130.41 CenterY=-6.95 CenterZ=0 NormalX=0 NormalY=0 NormalZ=1 AngleXU=0 Radius=3.7
  constraints (4):
    c: Diameter(g0) = 7.4
    c: Coincident(g0,g-3)
    c: Diameter(g1) = 7.4
    c: Coincident(g1,g-4)
FEATURE [Part::Extrusion] Extrude075  label="Extrude fori slargati blocco solenoide"
  Base = -> Sketch073
  Dir = (0,0,1)
  DirMode = 2
  FaceMakerClass = Part::FaceMakerBullseye
  FaceMakerMode = 3
  LengthFwd = 1.5
  LengthRev = 0
  Placement = pos=(0,0,36.4) rot=(0,0,1;0rad)
  Solid = true
  Symmetric = false
FEATURE [Part::Cut] Cut043
  Base = -> Cut042
  Refine = true
  Tool = -> Extrude075
FEATURE [Sketcher::SketchObject] Sketch074  label="lato sx pistola"
  ArcFitTolerance = 1e-06
  AttachmentSupport = -> [XZ_Plane]
  ExternalGeometry = -> [Sketch016,Sketch,Sketch058]
  FullyConstrained = true
  MakeInternals = false
  MapMode = 5
  Placement = pos=(0,0,0) rot=(1,0,0;1.5708rad)
  sketch-geometry (37):
    g0: LineSegment StartX=-82.8 StartY=3.2 StartZ=0 EndX=0 EndY=3.2 EndZ=0
    g1: LineSegment StartX=-82.8 StartY=3.2 StartZ=0 EndX=-82.8 EndY=6.2 EndZ=0
    g2: LineSegment [constr] StartX=-107.6 StartY=18 StartZ=0 EndX=-107.6 EndY=20 EndZ=0
    g3: LineSegment [constr] StartX=-132.428 StartY=18 StartZ=0 EndX=-132.428 EndY=20 EndZ=0
    g4: LineSegment StartX=-132.428 StartY=20 StartZ=0 EndX=-107.6 EndY=20 EndZ=0
    g5: ArcOfCircle CenterX=-107.6 CenterY=4 CenterZ=0 NormalX=0 NormalY=0 NormalZ=1 AngleXU=0 Radius=16 StartAngle=0.137937 EndAngle=1.5708
    g6: LineSegment StartX=-82.8 StartY=6.2 StartZ=0 EndX=-91.752 EndY=6.2 EndZ=0
    g7: LineSegment [constr] StartX=-145.743 StartY=8.32624 StartZ=0 EndX=-147.645 EndY=8.94427 EndZ=0
    g8: ArcOfCircle CenterX=-132.428 CenterY=4 CenterZ=0 NormalX=0 NormalY=0 NormalZ=1 AngleXU=0 Radius=16 StartAngle=1.5708 EndAngle=2.82743
    g9: LineSegment StartX=-215.932 StartY=-80.4316 StartZ=0 EndX=-176.685 EndY=-80.4316 EndZ=0
    g10: LineSegment StartX=-147.645 StartY=8.94427 StartZ=0 EndX=-176.685 EndY=-80.4316 EndZ=0
    g11: LineSegment [constr] StartX=-193.988 StartY=-2.33927 StartZ=0 EndX=-192.176 EndY=-3.18451 EndZ=0
    g12: LineSegment [constr] StartX=-217.232 StartY=-52.1862 StartZ=0 EndX=-215.42 EndY=-53.0314 EndZ=0
    g13: LineSegment StartX=-192.176 StartY=-3.18451 StartZ=0 EndX=-215.42 EndY=-53.0314 EndZ=0
    g14: ArcOfCircle CenterX=-184.801 CenterY=-67.3089 CenterZ=0 NormalX=0 NormalY=0 NormalZ=1 AngleXU=0 Radius=33.7833 StartAngle=2.70526 EndAngle=3.54053
    g15: ArcOfCircle CenterX=-207.583 CenterY=4 CenterZ=0 NormalX=0 NormalY=0 NormalZ=1 AngleXU=0 Radius=17 StartAngle=5.84685 EndAngle=7.56663
    g16: LineSegment StartX=-202.765 StartY=20.303 StartZ=0 EndX=-195.887 EndY=39.2 EndZ=0
    g17: LineSegment [constr] StartX=-193.885 StartY=33.0037 StartZ=0 EndX=-197.644 EndY=34.3718 EndZ=0
    g18: LineSegment StartX=-195.887 StartY=39.2 StartZ=0 EndX=0 EndY=39.2 EndZ=0
    g19: LineSegment StartX=0 StartY=3.2 StartZ=0 EndX=0 EndY=39.2 EndZ=0
    g20: LineSegment StartX=-189.939 StartY=31.5672 StartZ=0 EndX=-192.333 EndY=24.9893 EndZ=0
    g21: LineSegment StartX=-196.467 StartY=26.4942 StartZ=0 EndX=-194.073 EndY=33.0721 EndZ=0
    g22: Circle CenterX=-213.443 CenterY=-76.8316 CenterZ=0 NormalX=0 NormalY=0 NormalZ=1 AngleXU=0 Radius=1.8
    g23: Circle CenterX=-179.305 CenterY=-76.8316 CenterZ=0 NormalX=0 NormalY=0 NormalZ=1 AngleXU=0 Radius=1.8
    g24: Circle CenterX=-184.08 CenterY=34.8 CenterZ=0 NormalX=0 NormalY=0 NormalZ=1 AngleXU=0 Radius=1.8
    g25: Circle CenterX=-78.51 CenterY=34.8 CenterZ=0 NormalX=0 NormalY=0 NormalZ=1 AngleXU=0 Radius=1.8
    g26: Circle CenterX=-78.51 CenterY=7.6 CenterZ=0 NormalX=0 NormalY=0 NormalZ=1 AngleXU=0 Radius=1.8
    g27: Circle CenterX=-5.6 CenterY=34.8 CenterZ=0 NormalX=0 NormalY=0 NormalZ=1 AngleXU=0 Radius=1.8
    g28: Circle CenterX=-5.6 CenterY=7.6 CenterZ=0 NormalX=0 NormalY=0 NormalZ=1 AngleXU=0 Radius=1.8
    g29: LineSegment StartX=-190.127 StartY=31.6356 StartZ=0 EndX=-189.939 EndY=31.5672 EndZ=0
    g30: LineSegment StartX=-194.073 StartY=33.0721 StartZ=0 EndX=-193.885 EndY=33.0037 EndZ=0
    g31: LineSegment StartX=-193.885 StartY=33.0037 StartZ=0 EndX=-190.127 EndY=31.6356 EndZ=0
    g32: LineSegment StartX=-196.467 StartY=26.4942 StartZ=0 EndX=-192.333 EndY=24.9893 EndZ=0
    g33: Circle CenterX=-19 CenterY=21.2 CenterZ=0 NormalX=0 NormalY=0 NormalZ=1 AngleXU=0 Radius=6.3
    g34: Circle CenterX=-42 CenterY=21.2 CenterZ=0 NormalX=0 NormalY=0 NormalZ=1 AngleXU=0 Radius=6.3
    g35: Circle CenterX=-65 CenterY=21.2 CenterZ=0 NormalX=0 NormalY=0 NormalZ=1 AngleXU=0 Radius=6.3
    g36: LineSegment [constr] StartX=-4 StartY=21.2 StartZ=0 EndX=-65 EndY=21.2 EndZ=0
  constraints (96):
    c: Coincident(g0,g-41)
    c: Horizontal(g0)
    c: PointOnObject(g0,g-39)
    c: Coincident(g1,g0)
    c: Vertical(g1)
    c: DistanceY(g1,g1) = 3
    c: Coincident(g2,g-17)
    c: Vertical(g2)
    c: Coincident(g3,g-16)
    c: Vertical(g3)
    c: DistanceY(g2,g2) = 2
    c: DistanceY(g3,g3) = 2
    c: Coincident(g4,g3)
    c: Coincident(g4,g2)
    c: Coincident(g5,g-17)
    c: Coincident(g5,g2)
    c: Coincident(g6,g1)
    c: Horizontal(g6)
    c: Coincident(g6,g5)
    c: Coincident(g7,g-15)
    c: Coincident(g8,g7)
    c: Coincident(g8,g3)
    c: Coincident(g8,g-15)
    c: Horizontal(g9)
    c: DistanceY(g-13,g9) = 2
    c: Coincident(g10,g7)
    c: Parallel(g10,g-14)
    c: Coincident(g9,g10)
    c: Distance(g11) = 2
    c: Coincident(g11,g-11)
    c: Perpendicular(g-11,g11)
    c: Distance(g12) = 2
    c: Coincident(g12,g-12)
    c: Perpendicular(g-11,g12)
    c: Coincident(g13,g11)
    c: Coincident(g13,g12)
    c: Coincident(g14,g-32)
    c: Coincident(g14,g12)
    c: Coincident(g14,g9)
    c: Coincident(g15,g-10)
    c: Coincident(g15,g11)
    c: Parallel(g16,g-22)
    c: Distance(g17) = 4
    c: PointOnObject(g17,g16)
    c: Coincident(g15,g16)
    c: Horizontal(g18)
    c: Coincident(g18,g16)
    c: Coincident(g19,g0)
    c: PointOnObject(g19,g-39)
    c: DistanceY(g19,g-36) = 2
    c: Coincident(g18,g19)
    c: Diameter(g22) = 3.6
    c: Coincident(g22,g-9)
    c: Diameter(g23) = 3.6
    c: Coincident(g23,g-8)
    c: Diameter(g24) = 3.6
    c: Diameter(g25) = 3.6
    c: Diameter(g26) = 3.6
    c: Diameter(g27) = 3.6
    c: Diameter(g28) = 3.6
    c: Coincident(g27,g-4)
    c: Coincident(g28,g-3)
    c: Coincident(g25,g-6)
    c: Coincident(g26,g-5)
    c: Coincident(g24,g-7)
    c: Parallel(g20,g-21)
    c: Equal(g20,g-21)
    c: Parallel(g21,g-19)
    c: Equal(g21,g-19)
    c: Distance(g29) = 0.2
    c: Distance(g30) = 0.2
    c: Parallel(g29,g-20)
    c: Parallel(g31,g-20)
    c: Equal(g31,g-20)
    c: Coincident(g30,g31)
    c: Coincident(g31,g29)
    c: Coincident(g29,g-21)
    c: Parallel(g30,g31)
    c: Coincident(g17,g30)
    c: Coincident(g20,g29)
    c: Coincident(g21,g30)
    c: Perpendicular(g16,g17)
    c: Coincident(g32,g21)
    c: Coincident(g32,g20)
    c: Perpendicular(g10,g7)
    c: Diameter(g33) = 12.6
    c: Diameter(g34) = 12.6
    c: Diameter(g35) = 12.6
    c: Horizontal(g36)
    c: PointOnObject(g33,g36)
    c: PointOnObject(g34,g36)
    c: DistanceX(g34,g33) = 23
    c: DistanceX(g35,g34) = 23
    c: DistanceX(g33,g36) = 15
    c: Symmetric(g-24,g-24,g36)
    c: Coincident(g36,g35)
FEATURE [Sketcher::SketchObject] Sketch075  label="lato dx pistola"
  ArcFitTolerance = 1e-06
  AttachmentSupport = -> [XZ_Plane]
  ExternalGeometry = -> [Sketch016,Sketch,Sketch058,Sketch074]
  FullyConstrained = true
  MakeInternals = false
  MapMode = 5
  Placement = pos=(0,0,0) rot=(1,0,0;1.5708rad)
  sketch-geometry (61):
    g0: LineSegment StartX=-82.8 StartY=3.2 StartZ=0 EndX=0 EndY=3.2 EndZ=0
    g1: LineSegment StartX=-82.8 StartY=3.2 StartZ=0 EndX=-82.8 EndY=6.2 EndZ=0
    g2: LineSegment [constr] StartX=-107.6 StartY=18 StartZ=0 EndX=-107.6 EndY=20 EndZ=0
    g3: LineSegment [constr] StartX=-132.428 StartY=18 StartZ=0 EndX=-132.428 EndY=20 EndZ=0
    g4: LineSegment StartX=-132.428 StartY=20 StartZ=0 EndX=-107.6 EndY=20 EndZ=0
    g5: ArcOfCircle CenterX=-107.6 CenterY=4 CenterZ=0 NormalX=0 NormalY=0 NormalZ=1 AngleXU=0 Radius=16 StartAngle=0.137937 EndAngle=1.5708
    g6: LineSegment StartX=-82.8 StartY=6.2 StartZ=0 EndX=-91.752 EndY=6.2 EndZ=0
    g7: LineSegment [constr] StartX=-145.743 StartY=8.32624 StartZ=0 EndX=-147.645 EndY=8.94427 EndZ=0
    g8: ArcOfCircle CenterX=-132.428 CenterY=4 CenterZ=0 NormalX=0 NormalY=0 NormalZ=1 AngleXU=0 Radius=16 StartAngle=1.5708 EndAngle=2.82743
    g9: LineSegment StartX=-215.932 StartY=-80.4316 StartZ=0 EndX=-176.685 EndY=-80.4316 EndZ=0
    g10: LineSegment StartX=-147.645 StartY=8.94427 StartZ=0 EndX=-176.685 EndY=-80.4316 EndZ=0
    g11: LineSegment [constr] StartX=-193.988 StartY=-2.33927 StartZ=0 EndX=-192.176 EndY=-3.18451 EndZ=0
    g12: LineSegment [constr] StartX=-217.232 StartY=-52.1862 StartZ=0 EndX=-215.42 EndY=-53.0314 EndZ=0
    g13: LineSegment StartX=-192.176 StartY=-3.18451 StartZ=0 EndX=-215.42 EndY=-53.0314 EndZ=0
    g14: ArcOfCircle CenterX=-184.801 CenterY=-67.3089 CenterZ=0 NormalX=0 NormalY=0 NormalZ=1 AngleXU=0 Radius=33.7833 StartAngle=2.70526 EndAngle=3.54053
    g15: ArcOfCircle CenterX=-207.583 CenterY=4 CenterZ=0 NormalX=0 NormalY=0 NormalZ=1 AngleXU=0 Radius=17 StartAngle=5.84685 EndAngle=7.56663
    g16: LineSegment StartX=-202.765 StartY=20.303 StartZ=0 EndX=-195.887 EndY=39.2 EndZ=0
    g17: LineSegment [constr] StartX=-193.885 StartY=33.0037 StartZ=0 EndX=-197.644 EndY=34.3718 EndZ=0
    g18: LineSegment StartX=-195.887 StartY=39.2 StartZ=0 EndX=0 EndY=39.2 EndZ=0
    g19: LineSegment StartX=0 StartY=3.2 StartZ=0 EndX=0 EndY=39.2 EndZ=0
    g20: LineSegment StartX=-189.939 StartY=31.5672 StartZ=0 EndX=-192.333 EndY=24.9893 EndZ=0
    g21: LineSegment StartX=-196.467 StartY=26.4942 StartZ=0 EndX=-194.073 EndY=33.0721 EndZ=0
    g22: Circle CenterX=-213.443 CenterY=-76.8316 CenterZ=0 NormalX=0 NormalY=0 NormalZ=1 AngleXU=0 Radius=1.8
    g23: Circle CenterX=-179.305 CenterY=-76.8316 CenterZ=0 NormalX=0 NormalY=0 NormalZ=1 AngleXU=0 Radius=1.8
    g24: Circle CenterX=-184.08 CenterY=34.8 CenterZ=0 NormalX=0 NormalY=0 NormalZ=1 AngleXU=0 Radius=1.8
    g25: Circle CenterX=-78.51 CenterY=34.8 CenterZ=0 NormalX=0 NormalY=0 NormalZ=1 AngleXU=0 Radius=1.8
    g26: Circle CenterX=-78.51 CenterY=7.6 CenterZ=0 NormalX=0 NormalY=0 NormalZ=1 AngleXU=0 Radius=1.8
    g27: Circle CenterX=-5.6 CenterY=34.8 CenterZ=0 NormalX=0 NormalY=0 NormalZ=1 AngleXU=0 Radius=1.8
    g28: Circle CenterX=-5.6 CenterY=7.6 CenterZ=0 NormalX=0 NormalY=0 NormalZ=1 AngleXU=0 Radius=1.8
    g29: LineSegment StartX=-190.127 StartY=31.6356 StartZ=0 EndX=-189.939 EndY=31.5672 EndZ=0
    g30: LineSegment StartX=-194.073 StartY=33.0721 StartZ=0 EndX=-193.885 EndY=33.0037 EndZ=0
    g31: LineSegment StartX=-193.885 StartY=33.0037 StartZ=0 EndX=-190.127 EndY=31.6356 EndZ=0
    g32: LineSegment StartX=-196.467 StartY=26.4942 StartZ=0 EndX=-192.333 EndY=24.9893 EndZ=0
    g33: LineSegment [constr] StartX=-4 StartY=21.2 StartZ=0 EndX=-87.91 EndY=21.2 EndZ=0
    g34: GeomPoint [constr] X=-4 Y=21.2 Z=0
    g35: LineSegment [constr] StartX=-15.2 StartY=33.7 StartZ=0 EndX=-15.2 EndY=8.7 EndZ=0
    g36: LineSegment [constr] StartX=-15.2 StartY=33.7 StartZ=0 EndX=-56.2 EndY=33.7 EndZ=0
    g37: LineSegment [constr] StartX=-15.2 StartY=8.7 StartZ=0 EndX=-56.2 EndY=8.7 EndZ=0
    g38: LineSegment [constr] StartX=-56.2 StartY=33.7 StartZ=0 EndX=-56.2 EndY=8.7 EndZ=0
    g39: Circle CenterX=-18.6 CenterY=30.3 CenterZ=0 NormalX=0 NormalY=0 NormalZ=1 AngleXU=0 Radius=3.4
    g40: Circle CenterX=-18.6 CenterY=12.1 CenterZ=0 NormalX=0 NormalY=0 NormalZ=1 AngleXU=0 Radius=3.4
    g41: Circle CenterX=-43.2 CenterY=30.3 CenterZ=0 NormalX=0 NormalY=0 NormalZ=1 AngleXU=0 Radius=3.4
    g42: Circle CenterX=-43.2 CenterY=12.1 CenterZ=0 NormalX=0 NormalY=0 NormalZ=1 AngleXU=0 Radius=3.4
    g43: LineSegment [constr] StartX=-4 StartY=21.2 StartZ=0 EndX=-15.2 EndY=21.2 EndZ=0
    g44: LineSegment [constr] StartX=-15.2 StartY=21.2 StartZ=0 EndX=-36.2 EndY=21.2 EndZ=0
    g45: LineSegment [constr] StartX=-41.5 StartY=16.2 StartZ=0 EndX=-30.9 EndY=16.2 EndZ=0
    g46: LineSegment [constr] StartX=-30.9 StartY=16.2 StartZ=0 EndX=-30.9 EndY=26.2 EndZ=0
    g47: LineSegment [constr] StartX=-30.9 StartY=26.2 StartZ=0 EndX=-41.5 EndY=26.2 EndZ=0
    g48: LineSegment [constr] StartX=-41.5 StartY=26.2 StartZ=0 EndX=-41.5 EndY=16.2 EndZ=0
    g49: GeomPoint [constr] X=-36.2 Y=21.2 Z=0
    g50: Circle CenterX=-36.2 CenterY=21.2 CenterZ=0 NormalX=0 NormalY=0 NormalZ=1 AngleXU=0 Radius=2.8
    g51: LineSegment [constr] StartX=-24.2 StartY=26.7 StartZ=0 EndX=-24.2 EndY=15.7 EndZ=0
    g52: Circle CenterX=-24.2 CenterY=26.7 CenterZ=0 NormalX=0 NormalY=0 NormalZ=1 AngleXU=0 Radius=3
    g53: Circle CenterX=-24.2 CenterY=15.7 CenterZ=0 NormalX=0 NormalY=0 NormalZ=1 AngleXU=0 Radius=3
    g54: GeomPoint X=-18.6 Y=30.3 Z=0
    g55: GeomPoint X=-18.6 Y=12.1 Z=0
    g56: GeomPoint X=-43.2 Y=12.1 Z=0
    g57: GeomPoint X=-43.2 Y=30.3 Z=0
    g58: Circle CenterX=-65 CenterY=21.2 CenterZ=0 NormalX=0 NormalY=0 NormalZ=1 AngleXU=0 Radius=1.5
    g59: Circle CenterX=-42 CenterY=21.2 CenterZ=0 NormalX=0 NormalY=0 NormalZ=1 AngleXU=0 Radius=1.5
    g60: Circle CenterX=-19 CenterY=21.2 CenterZ=0 NormalX=0 NormalY=0 NormalZ=1 AngleXU=0 Radius=1.5
  constraints (149):
    c: Coincident(g0,g-41)
    c: Horizontal(g0)
    c: PointOnObject(g0,g-39)
    c: Coincident(g1,g0)
    c: Vertical(g1)
    c: DistanceY(g1,g1) = 3
    c: Coincident(g2,g-17)
    c: Vertical(g2)
    c: Coincident(g3,g-16)
    c: Vertical(g3)
    c: DistanceY(g2,g2) = 2
    c: DistanceY(g3,g3) = 2
    c: Coincident(g4,g3)
    c: Coincident(g4,g2)
    c: Coincident(g5,g-17)
    c: Coincident(g5,g2)
    c: Coincident(g6,g1)
    c: Horizontal(g6)
    c: Coincident(g6,g5)
    c: Coincident(g7,g-15)
    c: Coincident(g8,g7)
    c: Coincident(g8,g3)
    c: Coincident(g8,g-15)
    c: Horizontal(g9)
    c: DistanceY(g-13,g9) = 2
    c: Coincident(g10,g7)
    c: Parallel(g10,g-14)
    c: Coincident(g9,g10)
    c: Distance(g11) = 2
    c: Coincident(g11,g-11)
    c: Perpendicular(g-11,g11)
    c: Distance(g12) = 2
    c: Coincident(g12,g-12)
    c: Perpendicular(g-11,g12)
    c: Coincident(g13,g11)
    c: Coincident(g13,g12)
    c: Coincident(g14,g-32)
    c: Coincident(g14,g12)
    c: Coincident(g14,g9)
    c: Coincident(g15,g-10)
    c: Coincident(g15,g11)
    c: Parallel(g16,g-22)
    c: Distance(g17) = 4
    c: PointOnObject(g17,g16)
    c: Coincident(g15,g16)
    c: Horizontal(g18)
    c: Coincident(g18,g16)
    c: Coincident(g19,g0)
    c: PointOnObject(g19,g-39)
    c: DistanceY(g19,g-36) = 2
    c: Coincident(g18,g19)
    c: Diameter(g22) = 3.6
    c: Coincident(g22,g-9)
    c: Diameter(g23) = 3.6
    c: Coincident(g23,g-8)
    c: Diameter(g24) = 3.6
    c: Diameter(g25) = 3.6
    c: Diameter(g26) = 3.6
    c: Diameter(g27) = 3.6
    c: Diameter(g28) = 3.6
    c: Coincident(g27,g-4)
    c: Coincident(g28,g-3)
    c: Coincident(g25,g-6)
    c: Coincident(g26,g-5)
    c: Coincident(g24,g-7)
    c: Parallel(g20,g-21)
    c: Equal(g20,g-21)
    c: Parallel(g21,g-19)
    c: Equal(g21,g-19)
    c: Distance(g29) = 0.2
    c: Distance(g30) = 0.2
    c: Parallel(g29,g-20)
    c: Parallel(g31,g-20)
    c: Equal(g31,g-20)
    c: Coincident(g30,g31)
    c: Coincident(g31,g29)
    c: Coincident(g29,g-21)
    c: Parallel(g30,g31)
    c: Coincident(g17,g30)
    c: Coincident(g20,g29)
    c: Coincident(g21,g30)
    c: Perpendicular(g16,g17)
    c: Coincident(g32,g21)
    c: Coincident(g32,g20)
    c: Perpendicular(g10,g7)
    c: Horizontal(g33)
    c: Symmetric(g-24,g-24,g33)
    c: PointOnObject(g33,g-28)
    c: Symmetric(g-24,g-24,g34)
    c: DistanceY(g35,g35) = 25
    c: Symmetric(g35,g35,g33)
    c: Distance(g36) = 41
    c: Coincident(g36,g35)
    c: Horizontal(g36)
    c: Coincident(g37,g35)
    c: Horizontal(g37)
    c: Coincident(g38,g36)
    c: Vertical(g38)
    c: Coincident(g37,g38)
    c: Diameter(g39) = 6.8
    c: Diameter(g40) = 6.8
    c: Tangent(g39,g36)
    c: Tangent(g40,g37)
    c: Tangent(g39,g35)
    c: Tangent(g40,g35)
    c: Diameter(g41) = 6.8
    c: Diameter(g42) = 6.8
    c: Tangent(g41,g36)
    c: Tangent(g42,g37)
    c: DistanceX(g41,g39) = 24.6
    c: DistanceX(g42,g40) = 24.6
    c: Distance(g43) = 11.2
    c: Coincident(g43,g33)
    c: PointOnObject(g43,g33)
    c: PointOnObject(g43,g35)
    c: Distance(g44) = 21
    c: Coincident(g44,g43)
    c: PointOnObject(g44,g33)
    c: Coincident(g45,g46)
    c: Coincident(g46,g47)
    c: Coincident(g47,g48)
    c: Coincident(g48,g45)
    c: Horizontal(g45)
    c: Horizontal(g47)
    c: Vertical(g46)
    c: Vertical(g48)
    c: Symmetric(g47,g45,g49)
    c: Distance(g46,g48) = 10.6
    c: Distance(g45,g47) = 10
    c: Coincident(g49,g44)
    c: Diameter(g50) = 5.6
    c: Coincident(g50,g44)
    c: Distance(g51) = 11
    c: Symmetric(g51,g51,g33)
    c: DistanceX(g51,g43) = 9
    c: Diameter(g52) = 6
    c: Coincident(g52,g51)
    c: Diameter(g53) = 6
    c: Coincident(g53,g51)
    c: Coincident(g40,g55)
    c: Coincident(g39,g54)
    c: Coincident(g41,g57)
    c: Coincident(g42,g56)
    c: Diameter(g58) = 3
    c: Diameter(g59) = 3
    c: Diameter(g60) = 3
    c: Coincident(g58,g-44)
    c: Coincident(g59,g-46)
    c: Coincident(g60,g-45)
FEATURE [Sketcher::SketchObject] Sketch078
  ArcFitTolerance = 1e-06
  AttachmentSupport = -> [XZ_Plane005]
  FullyConstrained = true
  MakeInternals = false
  MapMode = 5
  Placement = pos=(0,0,0) rot=(1,0,0;1.5708rad)
  sketch-geometry (5):
    g0: LineSegment [constr] StartX=0 StartY=5.5 StartZ=0 EndX=0 EndY=-5.5 EndZ=0
    g1: ArcOfCircle CenterX=0 CenterY=5.5 CenterZ=0 NormalX=0 NormalY=0 NormalZ=1 AngleXU=0 Radius=2.7 StartAngle=0 EndAngle=3.14159
    g2: ArcOfCircle CenterX=0 CenterY=-5.5 CenterZ=0 NormalX=0 NormalY=0 NormalZ=1 AngleXU=0 Radius=2.7 StartAngle=3.1416 EndAngle=6.28318
    g3: LineSegment StartX=-2.7 StartY=5.5 StartZ=0 EndX=-2.7 EndY=-5.50001 EndZ=0
    g4: LineSegment StartX=2.7 StartY=5.5 StartZ=0 EndX=2.7 EndY=-5.50001 EndZ=0
  constraints (13):
    c: Distance(g0) = 11
    c: Vertical(g0)
    c: Symmetric(g0,g0,g-1)
    c: Radius(g1) = 2.7
    c: Coincident(g1,g0)
    c: Radius(g2) = 2.7
    c: Coincident(g2,g0)
    c: Vertical(g3)
    c: Vertical(g4)
    c: Coincident(g2,g4)
    c: Coincident(g2,g3)
    c: Tangent(g3,g1) = -1.5708
    c: Tangent(g4,g1) = 1.5708
FEATURE [PartDesign::Pad] Pad002
  Direction = (0,-1,2e-16)
  Length = 0.8
  Length2 = 10
  Placement = pos=(0,0,0) rot=(1,0,0;1.5708rad)
  Profile = -> Sketch078
  ReferenceAxis = -> Sketch078 [N_Axis]
  Refine = true
  Suppressed = false
  Type = 0
FEATURE [Sketcher::SketchObject] Sketch079
  ArcFitTolerance = 1e-06
  AttachmentSupport = -> [XZ_Plane005]
  ExternalGeometry = -> [Sketch078]
  FullyConstrained = true
  MakeInternals = false
  MapMode = 5
  Placement = pos=(0,0,0) rot=(1,0,0;1.5708rad)
  sketch-geometry (2):
    g0: Circle CenterX=-1e-16 CenterY=5.5 CenterZ=0 NormalX=0 NormalY=0 NormalZ=1 AngleXU=0 Radius=2.7
    g1: Circle CenterX=0 CenterY=-5.5 CenterZ=0 NormalX=0 NormalY=0 NormalZ=1 AngleXU=0 Radius=2.7
  constraints (4):
    c: Coincident(g0,g-3)
    c: PointOnObject(g-3,g0)
    c: Coincident(g1,g-4)
    c: Equal(g1,g-4)
FEATURE [PartDesign::Pad] Pad003
  BaseFeature = -> Pad002
  Direction = (0,-1,2e-16)
  Length = 5
  Length2 = 10
  Placement = pos=(0,0,0) rot=(1,0,0;1.5708rad)
  Profile = -> Sketch079
  ReferenceAxis = -> Sketch079 [N_Axis]
  Refine = true
  Suppressed = false
  Type = 0
FEATURE [PartDesign::Fillet] Fillet001
  Base = -> Pad003 [Edge16,Edge14]
  BaseFeature = -> Pad003
  Placement = pos=(0,0,0) rot=(1,0,0;1.5708rad)
  Radius = 0.4
  Refine = true
  SupportTransform = false
  Suppressed = false
  UseAllEdges = false
FEATURE [PartDesign::Body] Body005  label="pulsanti lato destro"
  AllowCompound = false
  Group = -> [Sketch078,Pad002,Sketch079,Pad003,Fillet001]
  Origin = -> Origin005
  Tip = -> Fillet001
FEATURE [PartDesign::SubShapeBinder] Binder
  BindCopyOnChange = 0
  BindMode = 0
  ClaimChildren = false
  Context = -> Body006 [Binder.]
  Fuse = false
  MakeFace = true
  OffsetFill = false
  OffsetIntersection = false
  OffsetJoinType = 0
  OffsetOpenResult = false
  PartialLoad = false
  Refine = true
  Relative = true
  Support = -> [Body[Sketch074.]]
  _Version = 2
FEATURE [PartDesign::SubShapeBinder] Binder001
  BindCopyOnChange = 0
  BindMode = 0
  ClaimChildren = false
  Context = -> Body007 [Binder001.]
  Fuse = false
  MakeFace = true
  OffsetFill = false
  OffsetIntersection = false
  OffsetJoinType = 0
  OffsetOpenResult = false
  PartialLoad = false
  Refine = true
  Relative = true
  Support = -> [Body[Sketch075.]]
  _Version = 2
FEATURE [Mesh::Feature] logo_per_PCB_definitivo_positivo
  Placement = pos=(-191,17,-66) rot=(0,1,1;0rad)
FEATURE [Sketcher::SketchObject] Sketch114  label="Sketch114 - base lato DX"
  ArcFitTolerance = 1e-06
  AttachmentSupport = -> [Binder001]
  ExternalGeometry = -> [Binder001]
  FullyConstrained = true
  MakeInternals = false
  MapMode = 5
  Placement = pos=(0,1e-15,0) rot=(0,0.707107,0.707107;3.14159rad)
  sketch-geometry (30):
    g0: Circle CenterX=5.6 CenterY=34.8 CenterZ=0 NormalX=0 NormalY=0 NormalZ=1 AngleXU=0 Radius=1.8
    g1: Circle CenterX=5.6 CenterY=7.6 CenterZ=0 NormalX=0 NormalY=0 NormalZ=1 AngleXU=0 Radius=1.8
    g2: Circle CenterX=24.2 CenterY=26.7 CenterZ=0 NormalX=0 NormalY=0 NormalZ=1 AngleXU=0 Radius=3
    g3: Circle CenterX=24.2 CenterY=15.7 CenterZ=0 NormalX=0 NormalY=0 NormalZ=1 AngleXU=0 Radius=3
    g4: Circle CenterX=36.2 CenterY=21.2 CenterZ=0 NormalX=0 NormalY=0 NormalZ=1 AngleXU=0 Radius=2.8
    g5: Circle CenterX=78.51 CenterY=34.8 CenterZ=0 NormalX=0 NormalY=0 NormalZ=1 AngleXU=0 Radius=1.8
    g6: Circle CenterX=78.51 CenterY=7.6 CenterZ=0 NormalX=0 NormalY=0 NormalZ=1 AngleXU=0 Radius=1.8
    g7: Circle CenterX=184.08 CenterY=34.8 CenterZ=0 NormalX=0 NormalY=0 NormalZ=1 AngleXU=0 Radius=1.8
    g8: Circle CenterX=213.443 CenterY=-76.8316 CenterZ=0 NormalX=0 NormalY=0 NormalZ=1 AngleXU=0 Radius=1.8
    g9: Circle CenterX=179.305 CenterY=-76.8316 CenterZ=0 NormalX=0 NormalY=0 NormalZ=1 AngleXU=0 Radius=1.8
    g10: ArcOfCircle [constr] CenterX=132.428 CenterY=4 CenterZ=0 NormalX=0 NormalY=0 NormalZ=1 AngleXU=0 Radius=16 StartAngle=0.314159 EndAngle=1.5708
    g11: ArcOfCircle CenterX=107.6 CenterY=4 CenterZ=0 NormalX=0 NormalY=0 NormalZ=1 AngleXU=0 Radius=16 StartAngle=1.5708 EndAngle=3.00366
    g12: ArcOfCircle CenterX=207.583 CenterY=4 CenterZ=0 NormalX=0 NormalY=0 NormalZ=1 AngleXU=0 Radius=17 StartAngle=1.85815 EndAngle=3.57792
    g13: ArcOfCircle CenterX=184.801 CenterY=-67.3089 CenterZ=0 NormalX=0 NormalY=0 NormalZ=1 AngleXU=0 Radius=33.7833 StartAngle=5.88425 EndAngle=6.71952
    g14: LineSegment StartX=0 StartY=39.2 StartZ=0 EndX=0 EndY=3.2 EndZ=0
    g15: LineSegment StartX=0 StartY=3.2 StartZ=0 EndX=82.8 EndY=3.2 EndZ=0
    g16: LineSegment StartX=82.8 StartY=3.2 StartZ=0 EndX=82.8 EndY=6.2 EndZ=0
    g17: LineSegment StartX=82.8 StartY=6.2 StartZ=0 EndX=91.752 EndY=6.2 EndZ=0
    g18: LineSegment StartX=107.6 StartY=20 StartZ=0 EndX=132.428 EndY=20 EndZ=0
    g19: LineSegment StartX=147.645 StartY=8.94427 StartZ=0 EndX=176.685 EndY=-80.4316 EndZ=0
    g20: LineSegment StartX=176.685 StartY=-80.4316 StartZ=0 EndX=215.932 EndY=-80.4316 EndZ=0
    g21: LineSegment StartX=215.42 StartY=-53.0314 StartZ=0 EndX=192.176 EndY=-3.18451 EndZ=0
    g22: LineSegment StartX=202.765 StartY=20.303 StartZ=0 EndX=195.887 EndY=39.2 EndZ=0
    g23: LineSegment StartX=195.887 StartY=39.2 StartZ=0 EndX=0 EndY=39.2 EndZ=0
    g24: LineSegment StartX=196.467 StartY=26.4942 StartZ=0 EndX=194.073 EndY=33.0721 EndZ=0
    g25: LineSegment StartX=194.073 StartY=33.0721 StartZ=0 EndX=189.939 EndY=31.5672 EndZ=0
    g26: LineSegment StartX=189.939 StartY=31.5672 StartZ=0 EndX=192.333 EndY=24.9893 EndZ=0
    g27: LineSegment StartX=192.333 StartY=24.9893 StartZ=0 EndX=196.467 EndY=26.4942 EndZ=0
    g28: LineSegment StartX=132.428 StartY=20 StartZ=0 EndX=144.053 EndY=20 EndZ=0
    g29: LineSegment StartX=144.053 StartY=20 StartZ=0 EndX=147.645 EndY=8.94427 EndZ=0
  constraints (65):
    c: Equal(g0,g-25)
    c: Equal(g2,g-29)
    c: Equal(g3,g-30)
    c: Equal(g4,g-28)
    c: Equal(g1,g-26)
    c: Coincident(g0,g-25)
    c: Coincident(g1,g-26)
    c: Coincident(g2,g-29)
    c: Coincident(g3,g-30)
    c: Coincident(g4,g-28)
    c: Equal(g5,g-23)
    c: Equal(g6,g-24)
    c: Coincident(g5,g-23)
    c: Coincident(g6,g-24)
    c: Equal(g7,g-20)
    c: Coincident(g7,g-20)
    c: Equal(g9,g-22)
    c: Coincident(g9,g-22)
    c: Equal(g8,g-21)
    c: Coincident(g8,g-21)
    c: Equal(g13,g-12)
    c: Equal(g12,g-14)
    c: Equal(g10,g-9)
    c: Equal(g11,g-7)
    c: Coincident(g14,g-27)
    c: Coincident(g14,g-27)
    c: Coincident(g15,g14)
    c: Coincident(g15,g-5)
    c: Coincident(g16,g15)
    c: Coincident(g16,g-6)
    c: Coincident(g17,g16)
    c: Coincident(g17,g-7)
    c: Coincident(g11,g17)
    c: Coincident(g11,g-8)
    c: Coincident(g18,g11)
    c: Coincident(g18,g-9)
    c: Coincident(g10,g18)
    c: Coincident(g10,g-10)
    c: Coincident(g19,g10)
    c: Coincident(g19,g-11)
    c: Coincident(g20,g19)
    c: Coincident(g20,g-12)
    c: Coincident(g13,g20)
    c: Coincident(g13,g-13)
    c: Coincident(g21,g13)
    c: Coincident(g21,g-14)
    c: Coincident(g12,g21)
    c: Coincident(g12,g-15)
    c: Coincident(g22,g12)
    c: Coincident(g22,g-15)
    c: Coincident(g23,g22)
    c: Coincident(g23,g14)
    c: Coincident(g24,g-18)
    c: Coincident(g24,g-16)
    c: Coincident(g25,g24)
    c: Coincident(g25,g-19)
    c: Coincident(g26,g25)
    c: Coincident(g26,g-19)
    c: Coincident(g27,g26)
    c: Coincident(g27,g24)
    c: Coincident(g29,g10)
    c: Coincident(g28,g10)
    c: Coincident(g29,g28)
    c: Parallel(g28,g18)
    c: Parallel(g29,g19)
FEATURE [PartDesign::Pad] Pad011
  Direction = (0,1,-2e-16)
  Length = 2
  Length2 = 10
  Profile = -> Sketch114
  ReferenceAxis = -> Sketch114 [N_Axis]
  Refine = true
  Reversed = true
  Suppressed = false
  Type = 0
FEATURE [Sketcher::SketchObject] Sketch115
  ArcFitTolerance = 1e-06
  AttachmentSupport = -> [Pad011]
  ExternalGeometry = -> [Binder001]
  FullyConstrained = true
  MakeInternals = false
  MapMode = 5
  Placement = pos=(0,1.7e-15,0) rot=(0,0.707107,0.707107;3.14159rad)
  sketch-geometry (4):
    g0: ArcOfCircle CenterX=24.2 CenterY=26.7 CenterZ=0 NormalX=0 NormalY=0 NormalZ=1 AngleXU=0 Radius=3 StartAngle=4.48384e-08 EndAngle=3.14159
    g1: ArcOfCircle CenterX=24.2 CenterY=15.7 CenterZ=0 NormalX=0 NormalY=0 NormalZ=1 AngleXU=0 Radius=3 StartAngle=3.14159 EndAngle=6.28318
    g2: LineSegment StartX=21.2 StartY=26.7 StartZ=0 EndX=21.2 EndY=15.7 EndZ=0
    g3: LineSegment StartX=27.2 StartY=26.7 StartZ=0 EndX=27.2 EndY=15.7 EndZ=0
  constraints (12):
    c: Equal(g1,g-4)
    c: Equal(g0,g-3)
    c: Coincident(g0,g-3)
    c: Coincident(g1,g-4)
    c: Vertical(g2)
    c: Vertical(g3)
    c: Tangent(g3,g-3)
    c: Tangent(g2,g-3)
    c: Coincident(g0,g2)
    c: Coincident(g0,g3)
    c: Coincident(g1,g2)
    c: Coincident(g3,g1)
FEATURE [Sketcher::SketchObject] Sketch117  label="Sketch117 - fori per inserto M3 x 3 x 4.5"
  ArcFitTolerance = 1e-06
  AttachmentSupport = -> [Pad011]
  ExternalGeometry = -> [Binder001]
  FullyConstrained = true
  MakeInternals = false
  MapMode = 5
  Placement = pos=(0,1.7e-15,0) rot=(0,0.707107,0.707107;3.14159rad)
  sketch-geometry (4):
    g0: Circle CenterX=43.2 CenterY=30.3 CenterZ=0 NormalX=0 NormalY=0 NormalZ=1 AngleXU=0 Radius=2.25
    g1: Circle CenterX=43.2 CenterY=12.1 CenterZ=0 NormalX=0 NormalY=0 NormalZ=1 AngleXU=0 Radius=2.25
    g2: Circle CenterX=18.6 CenterY=30.3 CenterZ=0 NormalX=0 NormalY=0 NormalZ=1 AngleXU=0 Radius=2.25
    g3: Circle CenterX=18.6 CenterY=12.1 CenterZ=0 NormalX=0 NormalY=0 NormalZ=1 AngleXU=0 Radius=2.25
  constraints (8):
    c: Diameter(g0) = 4.5
    c: Diameter(g1) = 4.5
    c: Diameter(g2) = 4.5
    c: Diameter(g3) = 4.5
    c: Coincident(g2,g-3)
    c: Coincident(g3,g-6)
    c: Coincident(g0,g-4)
    c: Coincident(g1,g-5)
FEATURE [Sketcher::SketchObject] Sketch118
  ArcFitTolerance = 1e-06
  AttachmentSupport = -> [Pad011]
  ExternalGeometry = -> [Binder001]
  FullyConstrained = true
  MakeInternals = false
  MapMode = 5
  Placement = pos=(0,-2,0) rot=(1,0,0;1.5708rad)
  sketch-geometry (12):
    g0: Circle CenterX=-78.51 CenterY=34.8 CenterZ=0 NormalX=0 NormalY=0 NormalZ=1 AngleXU=0 Radius=1.8
    g1: Circle CenterX=-78.51 CenterY=7.6 CenterZ=0 NormalX=0 NormalY=0 NormalZ=1 AngleXU=0 Radius=1.8
    g2: Circle CenterX=-5.6 CenterY=34.8 CenterZ=0 NormalX=0 NormalY=0 NormalZ=1 AngleXU=0 Radius=1.8
    g3: Circle CenterX=-5.6 CenterY=7.6 CenterZ=0 NormalX=0 NormalY=0 NormalZ=1 AngleXU=0 Radius=1.8
    g4: LineSegment StartX=0 StartY=39.2 StartZ=0 EndX=0 EndY=3.2 EndZ=0
    g5: LineSegment StartX=0 StartY=3.2 StartZ=0 EndX=-82.8 EndY=3.2 EndZ=0
    g6: LineSegment StartX=-82.8 StartY=3.2 StartZ=0 EndX=-82.8 EndY=39.2 EndZ=0
    g7: LineSegment StartX=-82.8 StartY=39.2 StartZ=0 EndX=0 EndY=39.2 EndZ=0
    g8: ArcOfCircle CenterX=-65 CenterY=21.2 CenterZ=0 NormalX=0 NormalY=0 NormalZ=1 AngleXU=0 Radius=10 StartAngle=1.5708 EndAngle=4.71239
    g9: ArcOfCircle CenterX=-19 CenterY=21.2 CenterZ=0 NormalX=0 NormalY=0 NormalZ=1 AngleXU=0 Radius=10 StartAngle=4.71239 EndAngle=7.85398
    g10: LineSegment StartX=-65 StartY=31.2 StartZ=0 EndX=-19 EndY=31.2 EndZ=0
    g11: LineSegment StartX=-65 StartY=11.2 StartZ=0 EndX=-19 EndY=11.2 EndZ=0
  constraints (25):
    c: Equal(g2,g-5)
    c: Equal(g3,g-7)
    c: Equal(g1,g-6)
    c: Equal(g0,g-4)
    c: Coincident(g0,g-4)
    c: Coincident(g1,g-6)
    c: Coincident(g3,g-7)
    c: Coincident(g2,g-5)
    c: Coincident(g4,g-8)
    c: Coincident(g4,g-9)
    c: Coincident(g5,g4)
    c: Coincident(g5,g-10)
    c: Coincident(g6,g5)
    c: PointOnObject(g6,g-3)
    c: Vertical(g6)
    c: Coincident(g7,g6)
    c: Coincident(g7,g4)
    c: Tangent(g8,g10) = 1.5708
    c: Tangent(g8,g11) = -1.5708
    c: Tangent(g9,g10) = 1.5708
    c: Tangent(g9,g11) = -1.5708
    c: Equal(g8,g9)
    c: Radius(g8) = 10
    c: Coincident(g8,g-11)
    c: Coincident(g9,g-12)
FEATURE [Sketcher::SketchObject] Sketch120
  ArcFitTolerance = 1e-06
  AttachmentSupport = -> [Pad011]
  ExternalGeometry = -> [Binder001]
  FullyConstrained = true
  MakeInternals = false
  MapMode = 5
  Placement = pos=(0,-2,0) rot=(1,0,0;1.5708rad)
  sketch-geometry (4):
    g0: LineSegment StartX=-137.815 StartY=39.2 StartZ=0 EndX=-142.655 EndY=24.303 EndZ=0
    g1: LineSegment StartX=-137.815 StartY=39.2 StartZ=0 EndX=-110.815 EndY=39.2 EndZ=0
    g2: LineSegment StartX=-142.655 StartY=24.303 StartZ=0 EndX=-110.815 EndY=24.303 EndZ=0
    g3: ArcOfCircle CenterX=-92.2534 CenterY=31.7515 CenterZ=0 NormalX=0 NormalY=0 NormalZ=1 AngleXU=0 Radius=20 StartAngle=2.75997 EndAngle=3.52321
  constraints (12):
    c: PointOnObject(g0,g-3)
    c: Coincident(g1,g0)
    c: PointOnObject(g1,g-3)
    c: Coincident(g2,g0)
    c: Horizontal(g2)
    c: Tangent(g0,g-4)
    c: Vertical(g2,g1)
    c: DistanceX(g1,g1) = 27
    c: DistanceY(g-6,g0) = 4
    c: Radius(g3) = 20
    c: Coincident(g3,g1)
    c: Coincident(g3,g2)
FEATURE [Sketcher::SketchObject] Sketch121
  ArcFitTolerance = 1e-06
  AttachmentSupport = -> [Pad011]
  ExternalGeometry = -> [Binder001]
  FullyConstrained = true
  MakeInternals = false
  MapMode = 5
  Placement = pos=(0,-2,0) rot=(1,0,0;1.5708rad)
  sketch-geometry (15):
    g0: LineSegment StartX=-137.815 StartY=39.2 StartZ=0 EndX=-143.955 EndY=20.303 EndZ=0
    g1: LineSegment StartX=-143.955 StartY=20.303 StartZ=0 EndX=-190.141 EndY=20.303 EndZ=0
    g2: LineSegment StartX=-190.141 StartY=20.303 StartZ=0 EndX=-186.139 EndY=31.3 EndZ=0
    g3: LineSegment StartX=-178.754 StartY=39.2 StartZ=0 EndX=-180.791 EndY=33.6029 EndZ=0
    g4: ArcOfCircle CenterX=-184.08 CenterY=34.8 CenterZ=0 NormalX=0 NormalY=0 NormalZ=1 AngleXU=0 Radius=3.5 StartAngle=4.71239 EndAngle=5.93412
    g5: LineSegment StartX=-184.08 StartY=31.3 StartZ=0 EndX=-186.139 EndY=31.3 EndZ=0
    g6: LineSegment StartX=-137.815 StartY=39.2 StartZ=0 EndX=-156.815 EndY=39.2 EndZ=0
    g7: LineSegment StartX=-168.815 StartY=39.2 StartZ=0 EndX=-178.754 EndY=39.2 EndZ=0
    g8: LineSegment StartX=-157.815 StartY=39.2 StartZ=0 EndX=-167.815 EndY=39.2 EndZ=0
    g9: LineSegment StartX=-168.815 StartY=31.2 StartZ=0 EndX=-156.815 EndY=31.2 EndZ=0
    g10: LineSegment StartX=-167.436 StartY=36.2 StartZ=0 EndX=-157.436 EndY=36.2 EndZ=0
    g11: ArcOfCircle CenterX=-176.411 CenterY=35.2 CenterZ=0 NormalX=0 NormalY=0 NormalZ=1 AngleXU=0 Radius=20 StartAngle=6.08183 EndAngle=6.48454
    g12: ArcOfCircle CenterX=-188.411 CenterY=35.2 CenterZ=0 NormalX=0 NormalY=0 NormalZ=1 AngleXU=0 Radius=20 StartAngle=6.08183 EndAngle=6.48454
    g13: ArcOfCircle CenterX=-177.411 CenterY=35.2 CenterZ=0 NormalX=0 NormalY=0 NormalZ=1 AngleXU=0 Radius=20 StartAngle=0.0500209 EndAngle=0.201358
    g14: ArcOfCircle CenterX=-187.411 CenterY=35.2 CenterZ=0 NormalX=0 NormalY=0 NormalZ=1 AngleXU=0 Radius=20 StartAngle=0.0500209 EndAngle=0.201358
  constraints (46):
    c: PointOnObject(g0,g-3)
    c: Tangent(g0,g-5)
    c: Coincident(g1,g0)
    c: Horizontal(g1)
    c: Coincident(g2,g1)
    c: PointOnObject(g3,g-3)
    c: Parallel(g3,g-6)
    c: Parallel(g2,g-6)
    c: Radius(g4) = 3.5
    c: Coincident(g4,g-7)
    c: Tangent(g3,g4) = 1.5708
    c: Horizontal(g5)
    c: Tangent(g5,g4) = 1.5708
    c: DistanceX(g-8,g5) = 3.8
    c: Coincident(g2,g5)
    c: Coincident(g6,g0)
    c: PointOnObject(g6,g-3)
    c: DistanceX(g6,g6) = 19
    c: PointOnObject(g7,g-3)
    c: DistanceX(g7,g6) = 12
    c: Coincident(g7,g3)
    c: PointOnObject(g8,g-3)
    c: PointOnObject(g8,g-3)
    c: DistanceX(g8,g8) = 10
    c: DistanceX(g8,g6) = 1
    c: Horizontal(g9)
    c: Vertical(g7,g9)
    c: Vertical(g6,g9)
    c: DistanceY(g9,g7) = 8
    c: Horizontal(g10)
    c: Equal(g8,g10)
    c: DistanceY(g10,g8) = 3
    c: Radius(g11) = 20
    c: Coincident(g11,g6)
    c: Coincident(g11,g9)
    c: Radius(g12) = 20
    c: Coincident(g12,g7)
    c: Coincident(g12,g9)
    c: Equal(g13,g11)
    c: Coincident(g13,g8)
    c: Coincident(g13,g10)
    c: Horizontal(g13,g11)
    c: Equal(g14,g12)
    c: Coincident(g14,g8)
    c: Coincident(g14,g10)
    c: Horizontal(g1,g-6)
FEATURE [Sketcher::SketchObject] Sketch122
  ArcFitTolerance = 1e-06
  AttachmentSupport = -> [Pad011]
  ExternalGeometry = -> [Binder001]
  FullyConstrained = true
  MakeInternals = false
  MapMode = 5
  Placement = pos=(0,-2,0) rot=(1,0,0;1.5708rad)
  sketch-geometry (8):
    g0: ArcOfCircle CenterX=-184.801 CenterY=-67.3089 CenterZ=0 NormalX=0 NormalY=0 NormalZ=1 AngleXU=0 Radius=33.7833 StartAngle=2.70526 EndAngle=3.54053
    g1: LineSegment StartX=-176.685 StartY=-80.4316 StartZ=0 EndX=-215.932 EndY=-80.4316 EndZ=0
    g2: LineSegment StartX=-215.42 StartY=-53.0314 StartZ=0 EndX=-192.176 EndY=-3.18454 EndZ=0
    g3: ArcOfCircle CenterX=-207.583 CenterY=4 CenterZ=0 NormalX=0 NormalY=0 NormalZ=1 AngleXU=0 Radius=17 StartAngle=5.84685 EndAngle=7.56663
    g4: Circle CenterX=-213.443 CenterY=-76.8316 CenterZ=0 NormalX=0 NormalY=0 NormalZ=1 AngleXU=0 Radius=3
    g5: Circle CenterX=-179.305 CenterY=-76.8316 CenterZ=0 NormalX=0 NormalY=0 NormalZ=1 AngleXU=0 Radius=3
    g6: LineSegment StartX=-143.955 StartY=20.303 StartZ=0 EndX=-176.685 EndY=-80.4316 EndZ=0
    g7: LineSegment StartX=-202.765 StartY=20.303 StartZ=0 EndX=-143.955 EndY=20.303 EndZ=0
  constraints (18):
    c: Coincident(g0,g-7)
    c: Coincident(g0,g-8)
    c: Coincident(g1,g0)
    c: Tangent(g2,g-5)
    c: Coincident(g3,g-6)
    c: Coincident(g2,g3)
    c: Coincident(g0,g2)
    c: Diameter(g4) = 6
    c: Diameter(g5) = 6
    c: Coincident(g4,g-9)
    c: Coincident(g5,g-10)
    c: Horizontal(g1)
    c: Coincident(g6,g1)
    c: Tangent(g6,g-4)
    c: Coincident(g3,g-6)
    c: Coincident(g7,g3)
    c: Horizontal(g7)
    c: Coincident(g7,g6)
FEATURE [Sketcher::SketchObject] Sketch123
  ArcFitTolerance = 1e-06
  AttachmentSupport = -> [Pad011]
  ExternalGeometry = -> [Binder001]
  FullyConstrained = true
  MakeInternals = false
  MapMode = 5
  Placement = pos=(0,-2,0) rot=(1,0,0;1.5708rad)
  sketch-geometry (4):
    g0: LineSegment StartX=-108 StartY=36.8 StartZ=0 EndX=-90 EndY=36.8 EndZ=0
    g1: LineSegment StartX=-108 StartY=36.8 StartZ=0 EndX=-108 EndY=26.8 EndZ=0
    g2: LineSegment StartX=-108 StartY=26.8 StartZ=0 EndX=-90 EndY=26.8 EndZ=0
    g3: ArcOfCircle CenterX=-94 CenterY=31.8 CenterZ=0 NormalX=0 NormalY=0 NormalZ=1 AngleXU=0 Radius=6.40312 StartAngle=5.38713 EndAngle=7.17924
  constraints (13):
    c: Horizontal(g0)
    c: Coincident(g1,g0)
    c: Vertical(g1)
    c: Coincident(g2,g1)
    c: Horizontal(g2)
    c: DistanceX(g0,g0) = 18
    c: DistanceY(g1,g1) = 10
    c: Equal(g0,g2)
    c: DistanceX(g0,g-3) = 90
    c: DistanceY(g0,g-3) = 2.4
    c: Coincident(g3,g0)
    c: Coincident(g3,g2)
    c: DistanceX(g3,g0) = 4
FEATURE [PartDesign::Chamfer] Chamfer014
  Angle = 45
  Base = -> Pad011 [Edge80,Edge4,Edge7]
  BaseFeature = -> Pad011
  ChamferType = 0
  FlipDirection = false
  Refine = true
  Size = 1.9
  Size2 = 1
  SupportTransform = false
  Suppressed = false
  UseAllEdges = false
FEATURE [PartDesign::Pocket] Pocket006
  BaseFeature = -> Chamfer014
  Direction = (0,-1,2e-16)
  Length = 1.2
  Length2 = 5
  Profile = -> Sketch115
  ReferenceAxis = -> Sketch115 [N_Axis]
  Refine = true
  Suppressed = false
  Type = 0
FEATURE [Sketcher::SketchObject] Sketch116  label="Sketch116 - pieno per inserto M3 x 3 x 4,5"
  ArcFitTolerance = 1e-06
  AttachmentSupport = -> [Pocket006]
  ExternalGeometry = -> [Binder001]
  FullyConstrained = true
  MakeInternals = false
  MapMode = 5
  Placement = pos=(0,1.7e-15,0) rot=(0,0.707107,0.707107;3.14159rad)
  sketch-geometry (4):
    g0: Circle CenterX=43.2 CenterY=30.3 CenterZ=0 NormalX=0 NormalY=0 NormalZ=1 AngleXU=0 Radius=3.4
    g1: Circle CenterX=43.2 CenterY=12.1 CenterZ=0 NormalX=0 NormalY=0 NormalZ=1 AngleXU=0 Radius=3.4
    g2: Circle CenterX=18.6 CenterY=30.3 CenterZ=0 NormalX=0 NormalY=0 NormalZ=1 AngleXU=0 Radius=3.4
    g3: Circle CenterX=18.6 CenterY=12.1 CenterZ=0 NormalX=0 NormalY=0 NormalZ=1 AngleXU=0 Radius=3.4
  constraints (8):
    c: Diameter(g0) = 6.8
    c: Diameter(g1) = 6.8
    c: Diameter(g2) = 6.8
    c: Diameter(g3) = 6.8
    c: Coincident(g2,g-3)
    c: Coincident(g0,g-4)
    c: Coincident(g3,g-6)
    c: Coincident(g1,g-5)
FEATURE [PartDesign::Pad] Pad012
  BaseFeature = -> Pocket006
  Direction = (0,1,-2e-16)
  Length = 2.4
  Length2 = 10
  Profile = -> Sketch116
  ReferenceAxis = -> Sketch116 [N_Axis]
  Refine = true
  Suppressed = false
  Type = 0
FEATURE [PartDesign::Pocket] Pocket007
  BaseFeature = -> Pad012
  Direction = (0,-1,2e-16)
  Length = 0.6
  Length2 = 2.4
  Profile = -> Sketch117
  ReferenceAxis = -> Sketch117 [N_Axis]
  Refine = true
  Suppressed = false
  Type = 4
FEATURE [PartDesign::Pad] Pad013
  BaseFeature = -> Pocket007
  Direction = (0,-1,2e-16)
  Length = 1.6
  Length2 = 10
  Profile = -> Sketch118
  ReferenceAxis = -> Sketch118 [N_Axis]
  Refine = true
  Suppressed = false
  Type = 0
FEATURE [Sketcher::SketchObject] Sketch119
  ArcFitTolerance = 1e-06
  AttachmentSupport = -> [Pad013]
  ExternalGeometry = -> [Binder001]
  FullyConstrained = true
  MakeInternals = false
  MapMode = 5
  Placement = pos=(0,-3.6,0) rot=(1,0,0;1.5708rad)
  sketch-geometry (21):
    g0: LineSegment [constr] StartX=-82.8 StartY=3.2 StartZ=0 EndX=-82.8 EndY=39.2 EndZ=0
    g1: ArcOfCircle CenterX=-78.51 CenterY=34.8 CenterZ=0 NormalX=0 NormalY=0 NormalZ=1 AngleXU=0 Radius=3.5 StartAngle=4.71239 EndAngle=6.28319
    g2: ArcOfCircle CenterX=-78.51 CenterY=7.6 CenterZ=0 NormalX=0 NormalY=0 NormalZ=1 AngleXU=0 Radius=3.5 StartAngle=0 EndAngle=1.5708
    g3: ArcOfCircle CenterX=-5.6 CenterY=34.8 CenterZ=0 NormalX=0 NormalY=0 NormalZ=1 AngleXU=0 Radius=3.5 StartAngle=3.14159 EndAngle=4.71239
    g4: ArcOfCircle CenterX=-5.6 CenterY=7.6 CenterZ=0 NormalX=0 NormalY=0 NormalZ=1 AngleXU=0 Radius=3.5 StartAngle=1.5708 EndAngle=3.14159
    g5: LineSegment StartX=0 StartY=39.2 StartZ=0 EndX=0 EndY=31.3 EndZ=0
    g6: LineSegment StartX=0 StartY=39.2 StartZ=0 EndX=-9.1 EndY=39.2 EndZ=0
    g7: LineSegment StartX=0 StartY=3.2 StartZ=0 EndX=0 EndY=11.1 EndZ=0
    g8: LineSegment StartX=0 StartY=3.2 StartZ=0 EndX=-9.1 EndY=3.2 EndZ=0
    g9: LineSegment StartX=-82.8 StartY=3.2 StartZ=0 EndX=-75.01 EndY=3.2 EndZ=0
    g10: LineSegment StartX=-82.8 StartY=3.2 StartZ=0 EndX=-82.8 EndY=11.1 EndZ=0
    g11: LineSegment StartX=-82.8 StartY=39.2 StartZ=0 EndX=-82.8 EndY=31.3 EndZ=0
    g12: LineSegment StartX=-82.8 StartY=39.2 StartZ=0 EndX=-75.01 EndY=39.2 EndZ=0
    g13: LineSegment StartX=-82.8 StartY=31.3 StartZ=0 EndX=-78.51 EndY=31.3 EndZ=0
    g14: LineSegment StartX=-75.01 StartY=39.2 StartZ=0 EndX=-75.01 EndY=34.8 EndZ=0
    g15: LineSegment StartX=-82.8 StartY=11.1 StartZ=0 EndX=-78.51 EndY=11.1 EndZ=0
    g16: LineSegment StartX=-75.01 StartY=3.2 StartZ=0 EndX=-75.01 EndY=7.6 EndZ=0
    g17: LineSegment StartX=-9.1 StartY=39.2 StartZ=0 EndX=-9.1 EndY=34.8 EndZ=0
    g18: LineSegment StartX=0 StartY=31.3 StartZ=0 EndX=-5.6 EndY=31.3 EndZ=0
    g19: LineSegment StartX=0 StartY=11.1 StartZ=0 EndX=-5.6 EndY=11.1 EndZ=0
    g20: LineSegment StartX=-9.1 StartY=3.2 StartZ=0 EndX=-9.1 EndY=7.6 EndZ=0
  constraints (51):
    c: Coincident(g0,g-10)
    c: PointOnObject(g0,g-8)
    c: Vertical(g0)
    c: Coincident(g1,g-3)
    c: Coincident(g2,g-4)
    c: Coincident(g3,g-5)
    c: Coincident(g4,g-6)
    c: Radius(g4) = 3.5
    c: Radius(g3) = 3.5
    c: Radius(g1) = 3.5
    c: Radius(g2) = 3.5
    c: Coincident(g5,g-9)
    c: PointOnObject(g5,g-9)
    c: Coincident(g6,g5)
    c: PointOnObject(g6,g-8)
    c: Coincident(g7,g-9)
    c: PointOnObject(g7,g-9)
    c: Coincident(g8,g7)
    c: PointOnObject(g8,g-7)
    c: Coincident(g9,g0)
    c: PointOnObject(g9,g-7)
    c: Coincident(g10,g0)
    c: PointOnObject(g10,g0)
    c: Coincident(g11,g0)
    c: PointOnObject(g11,g0)
    c: Coincident(g12,g0)
    c: PointOnObject(g12,g-8)
    c: Coincident(g13,g11)
    c: Horizontal(g13)
    c: Coincident(g14,g12)
    c: Vertical(g14)
    c: Coincident(g15,g10)
    c: Horizontal(g15)
    c: Coincident(g16,g9)
    c: Vertical(g16)
    c: Coincident(g17,g6)
    c: Vertical(g17)
    c: Coincident(g18,g5)
    c: Horizontal(g18)
    c: Coincident(g19,g7)
    c: Horizontal(g19)
    c: Coincident(g20,g8)
    c: Vertical(g20)
    c: Tangent(g20,g4) = 1.5708
    c: Tangent(g4,g19) = -1.5708
    c: Tangent(g18,g3) = 1.5708
    c: Tangent(g3,g17) = -1.5708
    c: Tangent(g13,g1) = -1.5708
    c: Tangent(g1,g14) = 1.5708
    c: Tangent(g16,g2) = -1.5708
    c: Tangent(g2,g15) = 1.5708
FEATURE [PartDesign::Pocket] Pocket008
  BaseFeature = -> Pad013
  Direction = (0,1,-2e-16)
  Length = 1.6
  Length2 = 5
  Profile = -> Sketch119
  ReferenceAxis = -> Sketch119 [N_Axis]
  Refine = true
  Suppressed = false
  Type = 0
FEATURE [PartDesign::Pad] Pad017
  BaseFeature = -> Pocket008
  Direction = (0,-1,2e-16)
  Length = 1.6
  Length2 = 10
  Profile = -> Sketch123
  ReferenceAxis = -> Sketch123 [N_Axis]
  Refine = true
  Suppressed = false
  Type = 0
FEATURE [Sketcher::SketchObject] Sketch125
  ArcFitTolerance = 1e-06
  AttachmentSupport = -> [Pad017]
  ExternalGeometry = -> [Pad017]
  FullyConstrained = true
  MakeInternals = false
  MapMode = 5
  Placement = pos=(0,-3.6,8e-16) rot=(1,0,0;1.5708rad)
  sketch-geometry (20):
    g0: LineSegment StartX=-108 StartY=35.8 StartZ=0 EndX=-108 EndY=35 EndZ=0
    g1: LineSegment StartX=-108 StartY=35 StartZ=0 EndX=-97 EndY=35 EndZ=0
    g2: LineSegment StartX=-97 StartY=35 StartZ=0 EndX=-97 EndY=35.8 EndZ=0
    g3: LineSegment StartX=-97 StartY=35.8 StartZ=0 EndX=-108 EndY=35.8 EndZ=0
    g4: LineSegment StartX=-108 StartY=28.6 StartZ=0 EndX=-108 EndY=27.8 EndZ=0
    g5: LineSegment StartX=-108 StartY=27.8 StartZ=0 EndX=-97 EndY=27.8 EndZ=0
    g6: LineSegment StartX=-97 StartY=27.8 StartZ=0 EndX=-97 EndY=28.6 EndZ=0
    g7: LineSegment StartX=-97 StartY=28.6 StartZ=0 EndX=-108 EndY=28.6 EndZ=0
    g8: LineSegment StartX=-108 StartY=30.4 StartZ=0 EndX=-108 EndY=29.6 EndZ=0
    g9: LineSegment StartX=-108 StartY=29.6 StartZ=0 EndX=-97 EndY=29.6 EndZ=0
    g10: LineSegment StartX=-97 StartY=29.6 StartZ=0 EndX=-97 EndY=30.4 EndZ=0
    g11: LineSegment StartX=-97 StartY=30.4 StartZ=0 EndX=-108 EndY=30.4 EndZ=0
    g12: LineSegment StartX=-108 StartY=32.2 StartZ=0 EndX=-108 EndY=31.4 EndZ=0
    g13: LineSegment StartX=-108 StartY=31.4 StartZ=0 EndX=-97 EndY=31.4 EndZ=0
    g14: LineSegment StartX=-97 StartY=31.4 StartZ=0 EndX=-97 EndY=32.2 EndZ=0
    g15: LineSegment StartX=-97 StartY=32.2 StartZ=0 EndX=-108 EndY=32.2 EndZ=0
    g16: LineSegment StartX=-108 StartY=34 StartZ=0 EndX=-108 EndY=33.2 EndZ=0
    g17: LineSegment StartX=-108 StartY=33.2 StartZ=0 EndX=-97 EndY=33.2 EndZ=0
    g18: LineSegment StartX=-97 StartY=33.2 StartZ=0 EndX=-97 EndY=34 EndZ=0
    g19: LineSegment StartX=-97 StartY=34 StartZ=0 EndX=-108 EndY=34 EndZ=0
  constraints (55):
    c: Coincident(g1,g0)
    c: Horizontal(g1)
    c: Coincident(g2,g1)
    c: Vertical(g2)
    c: Coincident(g3,g2)
    c: Horizontal(g3)
    c: Coincident(g3,g0)
    c: DistanceX(g1,g1) = 11
    c: DistanceY(g2,g2) = 0.8
    c: Coincident(g5,g4)
    c: Horizontal(g5)
    c: Coincident(g6,g5)
    c: Vertical(g6)
    c: Coincident(g7,g6)
    c: Horizontal(g7)
    c: Coincident(g7,g4)
    c: Coincident(g9,g8)
    c: Horizontal(g9)
    c: Coincident(g10,g9)
    c: Vertical(g10)
    c: Coincident(g11,g10)
    c: Horizontal(g11)
    c: Coincident(g11,g8)
    c: Coincident(g13,g12)
    c: Horizontal(g13)
    c: Coincident(g14,g13)
    c: Vertical(g14)
    c: Coincident(g15,g14)
    c: Horizontal(g15)
    c: Coincident(g15,g12)
    c: Coincident(g17,g16)
    c: Horizontal(g17)
    c: Coincident(g18,g17)
    c: Vertical(g18)
    c: Coincident(g19,g18)
    c: Horizontal(g19)
    c: Coincident(g19,g16)
    c: Equal(g3,g19)
    c: Equal(g3,g15)
    c: Equal(g3,g11)
    c: Equal(g3,g7)
    c: Equal(g2,g18)
    c: Equal(g2,g14)
    c: Equal(g2,g10)
    c: Equal(g2,g6)
    c: DistanceY(g-4,g4) = 1
    c: DistanceY(g4,g8) = 1
    c: DistanceY(g8,g12) = 1
    c: DistanceY(g12,g16) = 1
    c: DistanceY(g16,g0) = 1
    c: Tangent(g0,g-5)
    c: Tangent(g16,g-5)
    c: Tangent(g12,g-5)
    c: Tangent(g8,g-5)
    c: Tangent(g4,g-5)
FEATURE [PartDesign::Chamfer] Chamfer009
  Angle = 45
  Base = -> Pad017 [Edge151,Edge154]
  BaseFeature = -> Pad017
  ChamferType = 1
  FlipDirection = false
  Refine = true
  Size = 1.5
  Size2 = 2.8
  SupportTransform = false
  Suppressed = false
  UseAllEdges = false
FEATURE [PartDesign::Pocket] Pocket009
  BaseFeature = -> Chamfer009
  Direction = (0,1,-2e-16)
  Length = 1
  Length2 = 5
  Profile = -> Sketch125
  ReferenceAxis = -> Sketch125 [N_Axis]
  Refine = true
  Suppressed = false
  Type = 0
FEATURE [PartDesign::Pad] Pad014
  BaseFeature = -> Pocket009
  Direction = (0,-1,2e-16)
  Length = 0.8
  Length2 = 10
  Profile = -> Sketch120
  ReferenceAxis = -> Sketch120 [N_Axis]
  Refine = true
  Suppressed = false
  Type = 0
FEATURE [Sketcher::SketchObject] Sketch124
  ArcFitTolerance = 1e-06
  AttachmentSupport = -> [Pad014]
  ExternalGeometry = -> [Binder001]
  FullyConstrained = true
  MakeInternals = false
  MapMode = 5
  Placement = pos=(0,-2.8,6e-16) rot=(1,0,0;1.5708rad)
  sketch-geometry (4):
    g0: LineSegment StartX=-129 StartY=39.2 StartZ=0 EndX=-131.599 EndY=31.2 EndZ=0
    g1: LineSegment StartX=-118 StartY=39.2 StartZ=0 EndX=-120.599 EndY=31.2 EndZ=0
    g2: LineSegment StartX=-129 StartY=39.2 StartZ=0 EndX=-118 EndY=39.2 EndZ=0
    g3: LineSegment StartX=-120.599 StartY=31.2 StartZ=0 EndX=-131.599 EndY=31.2 EndZ=0
  constraints (12):
    c: PointOnObject(g0,g-3)
    c: PointOnObject(g1,g-3)
    c: Parallel(g-4,g0)
    c: Parallel(g-4,g1)
    c: Coincident(g2,g0)
    c: Coincident(g2,g1)
    c: DistanceX(g2,g2) = 11
    c: DistanceY(g1,g1) = 8
    c: Coincident(g3,g1)
    c: Horizontal(g3)
    c: Coincident(g3,g0)
    c: DistanceX(g1,g-3) = 118
FEATURE [PartDesign::Pad] Pad018
  BaseFeature = -> Pad014
  Direction = (0,-1,2e-16)
  Length = 1.2
  Length2 = 10
  Profile = -> Sketch124
  ReferenceAxis = -> Sketch124 [N_Axis]
  Refine = true
  Suppressed = false
  Type = 0
FEATURE [Sketcher::SketchObject] Sketch126
  ArcFitTolerance = 1e-06
  AttachmentSupport = -> [Pad018]
  ExternalGeometry = -> [Pad018]
  FullyConstrained = true
  MakeInternals = false
  MapMode = 5
  Placement = pos=(0,-4,0) rot=(1,0,0;1.5708rad)
  sketch-geometry (8):
    g0: LineSegment StartX=-129.877 StartY=36.5 StartZ=0 EndX=-130.137 EndY=35.7 EndZ=0
    g1: LineSegment StartX=-130.69 StartY=34 StartZ=0 EndX=-130.95 EndY=33.2 EndZ=0
    g2: LineSegment StartX=-129.877 StartY=36.5 StartZ=0 EndX=-118.877 EndY=36.5 EndZ=0
    g3: LineSegment StartX=-130.137 StartY=35.7 StartZ=0 EndX=-119.137 EndY=35.7 EndZ=0
    g4: LineSegment StartX=-130.69 StartY=34 StartZ=0 EndX=-119.69 EndY=34 EndZ=0
    g5: LineSegment StartX=-130.95 StartY=33.2 StartZ=0 EndX=-119.95 EndY=33.2 EndZ=0
    g6: LineSegment StartX=-118.877 StartY=36.5 StartZ=0 EndX=-119.137 EndY=35.7 EndZ=0
    g7: LineSegment StartX=-119.69 StartY=34 StartZ=0 EndX=-119.95 EndY=33.2 EndZ=0
  constraints (20):
    c: Coincident(g2,g0)
    c: Horizontal(g2)
    c: Coincident(g3,g0)
    c: Horizontal(g3)
    c: Coincident(g4,g1)
    c: Horizontal(g4)
    c: Coincident(g5,g1)
    c: Horizontal(g5)
    c: Coincident(g6,g2)
    c: Coincident(g6,g3)
    c: Coincident(g7,g4)
    c: Coincident(g7,g5)
    c: Tangent(g0,g-4)
    c: Tangent(g6,g-5)
    c: Tangent(g1,g-4)
    c: Tangent(g7,g-5)
    c: DistanceY(g3,g2) = 0.8
    c: DistanceY(g5,g4) = 0.8
    c: DistanceY(g-6,g1) = 2
    c: DistanceY(g-6,g0) = 4.5
FEATURE [PartDesign::Chamfer] Chamfer008
  Angle = 45
  Base = -> Pad018 [Edge257]
  BaseFeature = -> Pad018
  ChamferType = 1
  FlipDirection = false
  Refine = true
  Size = 1
  Size2 = 6
  SupportTransform = false
  Suppressed = false
  UseAllEdges = false
FEATURE [PartDesign::Pocket] Pocket010
  BaseFeature = -> Chamfer008
  Direction = (0,1,-2e-16)
  Length = 1
  Length2 = 5
  Profile = -> Sketch126
  ReferenceAxis = -> Sketch126 [N_Axis]
  Refine = true
  Suppressed = false
  Type = 0
FEATURE [PartDesign::Pad] Pad015
  BaseFeature = -> Pocket010
  Direction = (0,-1,2e-16)
  Length = 2
  Length2 = 10
  Profile = -> Sketch121
  ReferenceAxis = -> Sketch121 [N_Axis]
  Refine = true
  Suppressed = false
  Type = 0
FEATURE [PartDesign::Pad] Pad016
  BaseFeature = -> Pad015
  Direction = (0,-1,2e-16)
  Length = 1.6
  Length2 = 10
  Profile = -> Sketch122
  ReferenceAxis = -> Sketch122 [N_Axis]
  Refine = true
  Suppressed = false
  Type = 0
FEATURE [Sketcher::SketchObject] Sketch129
  ArcFitTolerance = 1e-06
  AttachmentSupport = -> [Pad016]
  ExternalGeometry = -> [Binder001]
  FullyConstrained = true
  MakeInternals = false
  MapMode = 5
  Placement = pos=(0,-3.6,0) rot=(1,0,0;1.5708rad)
  sketch-geometry (12):
    g0: LineSegment [constr] StartX=-192.176 StartY=-3.18451 StartZ=0 EndX=-181.223 EndY=20.303 EndZ=0
    g1: LineSegment [constr] StartX=-202.765 StartY=20.303 StartZ=0 EndX=-181.223 EndY=20.303 EndZ=0
    g2: LineSegment StartX=-202.765 StartY=20.303 StartZ=0 EndX=-181.223 EndY=20.303 EndZ=0
    g3: LineSegment StartX=-192.176 StartY=-3.18451 StartZ=0 EndX=-196.804 EndY=-13.1107 EndZ=0
    g4: ArcOfCircle CenterX=-207.583 CenterY=4 CenterZ=0 NormalX=0 NormalY=0 NormalZ=1 AngleXU=0 Radius=17 StartAngle=5.84685 EndAngle=7.56663
    g5: ArcOfEllipse CenterX=-181.223 CenterY=8.55923 CenterZ=0 NormalX=0 NormalY=0 NormalZ=1 MajorRadius=23.4779 MinorRadius=11.7437 AngleXU=2e-16 StartAngle=4.71239 EndAngle=7.85398
    g6: LineSegment [constr] StartX=-157.745 StartY=8.55923 StartZ=0 EndX=-204.701 EndY=8.55923 EndZ=0
    g7: LineSegment [constr] StartX=-181.223 StartY=20.303 StartZ=0 EndX=-181.223 EndY=-3.18451 EndZ=0
    g8: GeomPoint [constr] X=-160.894 Y=8.55923 Z=0
    g9: GeomPoint [constr] X=-201.553 Y=8.55923 Z=0
    g10: ArcOfCircle CenterX=-181.223 CenterY=-20.3763 CenterZ=0 NormalX=0 NormalY=0 NormalZ=1 AngleXU=0 Radius=17.1918 StartAngle=1.57079 EndAngle=2.70526
    g11: GeomPoint [constr] X=-181.223 Y=-3.18451 Z=0
  constraints (23):
    c: Coincident(g0,g-5)
    c: Coincident(g1,g-6)
    c: Horizontal(g1)
    c: Coincident(g1,g0)
    c: Parallel(g0,g-4)
    c: Coincident(g2,g1)
    c: Coincident(g2,g0)
    c: Coincident(g3,g0)
    c: Equal(g4,g-5)
    c: Coincident(g4,g1)
    c: Coincident(g4,g0)
    c: InternalAlignment(g6-g9 -> g5) x4
    c: Vertical(g5,g0)
    c: Horizontal(g6)
    c: Coincident(g5,g0)
    c: DistanceX(g6,g-3) = 10.1
    c: Tangent(g10,g3) = -1.5708
    c: PointOnObject(g11,g10)
    c: Tangent(g5,g10,g11) = 1.5708
    c: Coincident(g10,g5)
    c: Coincident(g11,g7)
    c: Parallel(g3,g-4)
    c: Horizontal(g5,g0)
FEATURE [Sketcher::SketchObject] Sketch130
  ArcFitTolerance = 1e-06
  AttachmentOffset = pos=(0,0,-1.6) rot=(0,0,1;0rad)
  AttachmentSupport = -> [Pad016]
  ExternalGeometry = -> [Binder001]
  FullyConstrained = true
  MakeInternals = false
  MapMode = 5
  Placement = pos=(0,-2,-4e-16) rot=(1,0,0;1.5708rad)
  sketch-geometry (12):
    g0: LineSegment [constr] StartX=-192.176 StartY=-3.18451 StartZ=0 EndX=-181.223 EndY=20.303 EndZ=0
    g1: LineSegment [constr] StartX=-202.765 StartY=20.303 StartZ=0 EndX=-181.223 EndY=20.303 EndZ=0
    g2: LineSegment StartX=-202.765 StartY=20.303 StartZ=0 EndX=-181.223 EndY=20.303 EndZ=0
    g3: LineSegment StartX=-192.176 StartY=-3.18451 StartZ=0 EndX=-193.827 EndY=-6.72678 EndZ=0
    g4: ArcOfCircle CenterX=-207.583 CenterY=4 CenterZ=0 NormalX=0 NormalY=0 NormalZ=1 AngleXU=0 Radius=17 StartAngle=5.84685 EndAngle=7.56663
    g5: ArcOfEllipse CenterX=-181.223 CenterY=10.803 CenterZ=0 NormalX=0 NormalY=0 NormalZ=1 MajorRadius=14.4779 MinorRadius=9.5 AngleXU=0 StartAngle=4.71239 EndAngle=7.85398
    g6: LineSegment [constr] StartX=-166.745 StartY=10.803 StartZ=0 EndX=-195.701 EndY=10.803 EndZ=0
    g7: LineSegment [constr] StartX=-181.223 StartY=20.303 StartZ=0 EndX=-181.223 EndY=1.30297 EndZ=0
    g8: GeomPoint [constr] X=-170.298 Y=10.803 Z=0
    g9: GeomPoint [constr] X=-192.148 Y=10.803 Z=0
    g10: ArcOfCircle CenterX=-181.223 CenterY=-12.6042 CenterZ=0 NormalX=0 NormalY=0 NormalZ=1 AngleXU=0 Radius=13.9072 StartAngle=1.5708 EndAngle=2.70526
    g11: GeomPoint [constr] X=-181.223 Y=1.30297 Z=0
  constraints (23):
    c: Coincident(g0,g-5)
    c: Coincident(g1,g-6)
    c: Horizontal(g1)
    c: Coincident(g1,g0)
    c: Parallel(g0,g-4)
    c: Coincident(g2,g1)
    c: Coincident(g2,g0)
    c: Coincident(g3,g0)
    c: Equal(g4,g-5)
    c: Coincident(g4,g1)
    c: Coincident(g4,g0)
    c: InternalAlignment(g6-g9 -> g5) x4
    c: Vertical(g5,g0)
    c: Horizontal(g6)
    c: Coincident(g5,g0)
    c: DistanceX(g6,g-3) = 19.1
    c: Tangent(g10,g3) = -1.5708
    c: PointOnObject(g11,g10)
    c: Tangent(g5,g10,g11) = 1.5708
    c: Coincident(g10,g5)
    c: Coincident(g11,g7)
    c: Parallel(g3,g-4)
    c: DistanceY(g5,g0) = 19
FEATURE [Part::Part2DObjectPython] Clone2D001  label="Sketch130 (2D)"  # Draft 2D object (typed FeaturePython)
  Fuse = false
  Objects = -> [Sketch130]
  Placement = pos=(0,-2,-4e-16) rot=(1,0,0;1.5708rad)
  Scale = (1,1,1)
FEATURE [Sketcher::SketchObject] Sketch131
  ArcFitTolerance = 1e-06
  AttachmentOffset = pos=(0,0,-3.5) rot=(0,0,1;0rad)
  AttachmentSupport = -> [Pad016]
  ExternalGeometry = -> [Binder001]
  FullyConstrained = true
  MakeInternals = false
  MapMode = 5
  Placement = pos=(0,-0.1,-8e-16) rot=(1,0,0;1.5708rad)
  sketch-geometry (1):
    g0: GeomPoint X=-197.47 Y=8.55923 Z=0
  constraints (1):
    c: Symmetric(g-6,g-4,g0)
FEATURE [Sketcher::SketchObject] Sketch132
  ArcFitTolerance = 1e-06
  AttachmentSupport = -> [Pad016]
  ExternalGeometry = -> [Binder001]
  FullyConstrained = true
  MakeInternals = false
  MapMode = 5
  Placement = pos=(0,-3.6,0) rot=(1,0,0;1.5708rad)
  sketch-geometry (3):
    g0: LineSegment [constr] StartX=-215.42 StartY=-53.0314 StartZ=0 EndX=-167.782 EndY=-53.0314 EndZ=0
    g1: Circle CenterX=-191.282 CenterY=-53.0314 CenterZ=0 NormalX=0 NormalY=0 NormalZ=1 AngleXU=0 Radius=11.5
    g2: Circle CenterX=-191.282 CenterY=-53.0314 CenterZ=0 NormalX=0 NormalY=0 NormalZ=1 AngleXU=0 Radius=10.7
  constraints (8):
    c: Coincident(g0,g-3)
    c: PointOnObject(g0,g-4)
    c: Horizontal(g0)
    c: Diameter(g1) = 23
    c: PointOnObject(g1,g0)
    c: DistanceX(g1,g0) = 23.5
    c: Diameter(g2) = 21.4
    c: Coincident(g2,g1)
FEATURE [Part::Part2DObjectPython] ShapeString  # Draft 2D object (typed FeaturePython)
  FontFile = <path>
  Fuse = false
  Justification = 6
  JustificationReference = 0
  KeepLeftMargin = false
  MakeFace = true
  ObliqueAngle = 0
  Placement = pos=(-199,-3.6,-57.5) rot=(1,0,0;1.5708rad)
  ScaleToSize = true
  Size = 10
  String = AS
  Tracking = 0
FEATURE [Sketcher::SketchObject] Sketch133
  ArcFitTolerance = 1e-06
  AttachmentSupport = -> [Binder]
  ExternalGeometry = -> [Binder]
  FullyConstrained = true
  MakeInternals = false
  MapMode = 5
  Placement = pos=(0,9e-16,0) rot=(0,0.707107,0.707107;3.14159rad)
  sketch-geometry (30):
    g0: LineSegment StartX=0 StartY=39.2 StartZ=0 EndX=0 EndY=3.2 EndZ=0
    g1: LineSegment StartX=0 StartY=3.2 StartZ=0 EndX=82.8 EndY=3.2 EndZ=0
    g2: LineSegment StartX=82.8 StartY=3.2 StartZ=0 EndX=82.8 EndY=6.2 EndZ=0
    g3: LineSegment StartX=82.8 StartY=6.2 StartZ=0 EndX=91.752 EndY=6.2 EndZ=0
    g4: LineSegment StartX=0 StartY=39.2 StartZ=0 EndX=195.887 EndY=39.2 EndZ=0
    g5: LineSegment StartX=195.887 StartY=39.2 StartZ=0 EndX=202.765 EndY=20.303 EndZ=0
    g6: LineSegment StartX=192.333 StartY=24.9893 StartZ=0 EndX=196.467 EndY=26.4942 EndZ=0
    g7: LineSegment StartX=196.467 StartY=26.4942 StartZ=0 EndX=194.073 EndY=33.0721 EndZ=0
    g8: LineSegment StartX=194.073 StartY=33.0721 StartZ=0 EndX=189.939 EndY=31.5672 EndZ=0
    g9: LineSegment StartX=189.939 StartY=31.5672 StartZ=0 EndX=192.333 EndY=24.9893 EndZ=0
    g10: ArcOfCircle CenterX=107.6 CenterY=4 CenterZ=0 NormalX=0 NormalY=0 NormalZ=1 AngleXU=0 Radius=16 StartAngle=1.5708 EndAngle=3.00366
    g11: LineSegment StartX=107.6 StartY=20 StartZ=0 EndX=132.428 EndY=20 EndZ=0
    g12: ArcOfCircle [constr] CenterX=132.428 CenterY=4 CenterZ=0 NormalX=0 NormalY=0 NormalZ=1 AngleXU=0 Radius=16 StartAngle=0.314159 EndAngle=1.5708
    g13: LineSegment StartX=147.645 StartY=8.94427 StartZ=0 EndX=176.685 EndY=-80.4316 EndZ=0
    g14: LineSegment StartX=176.685 StartY=-80.4316 StartZ=0 EndX=215.932 EndY=-80.4316 EndZ=0
    g15: ArcOfCircle CenterX=207.583 CenterY=4 CenterZ=0 NormalX=0 NormalY=0 NormalZ=1 AngleXU=0 Radius=17 StartAngle=1.85815 EndAngle=3.57792
    g16: ArcOfCircle CenterX=184.801 CenterY=-67.3089 CenterZ=0 NormalX=0 NormalY=0 NormalZ=1 AngleXU=0 Radius=33.7833 StartAngle=5.88425 EndAngle=6.71952
    g17: LineSegment StartX=192.176 StartY=-3.18451 StartZ=0 EndX=215.42 EndY=-53.0314 EndZ=0
    g18: Circle CenterX=5.6 CenterY=34.8 CenterZ=0 NormalX=0 NormalY=0 NormalZ=1 AngleXU=0 Radius=1.8
    g19: Circle CenterX=5.6 CenterY=7.6 CenterZ=0 NormalX=0 NormalY=0 NormalZ=1 AngleXU=0 Radius=1.8
    g20: Circle CenterX=78.51 CenterY=34.8 CenterZ=0 NormalX=0 NormalY=0 NormalZ=1 AngleXU=0 Radius=1.8
    g21: Circle CenterX=78.51 CenterY=7.6 CenterZ=0 NormalX=0 NormalY=0 NormalZ=1 AngleXU=0 Radius=1.8
    g22: Circle CenterX=184.08 CenterY=34.8 CenterZ=0 NormalX=0 NormalY=0 NormalZ=1 AngleXU=0 Radius=1.8
    g23: Circle CenterX=179.305 CenterY=-76.8316 CenterZ=0 NormalX=0 NormalY=0 NormalZ=1 AngleXU=0 Radius=1.8
    g24: Circle CenterX=213.443 CenterY=-76.8316 CenterZ=0 NormalX=0 NormalY=0 NormalZ=1 AngleXU=0 Radius=1.8
    g25: Circle CenterX=19 CenterY=21.2 CenterZ=0 NormalX=0 NormalY=0 NormalZ=1 AngleXU=0 Radius=6.3
    g26: Circle CenterX=42 CenterY=21.2 CenterZ=0 NormalX=0 NormalY=0 NormalZ=1 AngleXU=0 Radius=6.3
    g27: Circle CenterX=65 CenterY=21.2 CenterZ=0 NormalX=0 NormalY=0 NormalZ=1 AngleXU=0 Radius=6.3
    g28: LineSegment StartX=132.428 StartY=20 StartZ=0 EndX=144.053 EndY=20 EndZ=0
    g29: LineSegment StartX=147.645 StartY=8.94427 StartZ=0 EndX=144.053 EndY=20 EndZ=0
  constraints (65):
    c: Coincident(g0,g-4)
    c: Coincident(g0,g-5)
    c: Coincident(g1,g0)
    c: Coincident(g1,g-6)
    c: Coincident(g2,g1)
    c: Coincident(g2,g-7)
    c: Coincident(g3,g2)
    c: Coincident(g3,g-8)
    c: Coincident(g4,g0)
    c: Coincident(g4,g-16)
    c: Coincident(g5,g4)
    c: Coincident(g5,g-16)
    c: Coincident(g6,g-20)
    c: Coincident(g6,g-21)
    c: Coincident(g7,g6)
    c: Coincident(g7,g-23)
    c: Coincident(g8,g7)
    c: Coincident(g8,g-22)
    c: Coincident(g9,g8)
    c: Coincident(g9,g6)
    c: Equal(g10,g-8)
    c: Coincident(g10,g3)
    c: Coincident(g10,g-9)
    c: Coincident(g11,g10)
    c: Coincident(g11,g-10)
    c: Equal(g12,g-10)
    c: Coincident(g12,g11)
    c: Coincident(g12,g-11)
    c: Coincident(g13,g12)
    c: Coincident(g13,g-12)
    c: Coincident(g14,g13)
    c: Coincident(g14,g-13)
    c: Equal(g15,g-15)
    c: Coincident(g15,g5)
    c: Coincident(g15,g-15)
    c: Equal(g16,g-13)
    c: Coincident(g16,g14)
    c: Coincident(g16,g-14)
    c: Coincident(g17,g15)
    c: Coincident(g17,g16)
    c: Equal(g18,g-28)
    c: Equal(g19,g-29)
    c: Equal(g20,g-26)
    c: Equal(g21,g-27)
    c: Equal(g22,g-17)
    c: Equal(g24,g-25)
    c: Equal(g23,g-24)
    c: Coincident(g23,g-24)
    c: Coincident(g24,g-25)
    c: Coincident(g22,g-17)
    c: Coincident(g20,g-26)
    c: Coincident(g21,g-27)
    c: Coincident(g18,g-28)
    c: Coincident(g19,g-29)
    c: Equal(g25,g-30)
    c: Equal(g26,g-31)
    c: Equal(g27,g-32)
    c: Coincident(g25,g-30)
    c: Coincident(g26,g-31)
    c: Coincident(g27,g-32)
    c: Parallel(g28,g11)
    c: Parallel(g29,g13)
    c: Coincident(g28,g11)
    c: Coincident(g29,g12)
    c: Coincident(g29,g28)
FEATURE [PartDesign::Pad] Pad019
  Direction = (0,1,-2e-16)
  Length = 2
  Length2 = 10
  Profile = -> Sketch133
  ReferenceAxis = -> Sketch133 [N_Axis]
  Refine = true
  Suppressed = false
  Type = 0
FEATURE [Sketcher::SketchObject] Sketch091  label="Sketch091 - forma anteriore"
  ArcFitTolerance = 1e-06
  AttachmentSupport = -> [Pad019]
  ExternalGeometry = -> [Binder]
  FullyConstrained = true
  MakeInternals = false
  MapMode = 5
  Placement = pos=(0,2,0) rot=(0,0.707107,0.707107;3.14159rad)
  sketch-geometry (12):
    g0: Circle CenterX=5.6 CenterY=34.8 CenterZ=0 NormalX=0 NormalY=0 NormalZ=1 AngleXU=0 Radius=1.8
    g1: Circle CenterX=5.6 CenterY=7.6 CenterZ=0 NormalX=0 NormalY=0 NormalZ=1 AngleXU=0 Radius=1.8
    g2: Circle CenterX=78.51 CenterY=34.8 CenterZ=0 NormalX=0 NormalY=0 NormalZ=1 AngleXU=0 Radius=1.8
    g3: Circle CenterX=78.51 CenterY=7.6 CenterZ=0 NormalX=0 NormalY=0 NormalZ=1 AngleXU=0 Radius=1.8
    g4: LineSegment StartX=0 StartY=39.2 StartZ=0 EndX=0 EndY=3.2 EndZ=0
    g5: LineSegment StartX=0 StartY=3.2 StartZ=0 EndX=82.8 EndY=3.2 EndZ=0
    g6: LineSegment StartX=82.8 StartY=3.2 StartZ=0 EndX=82.8 EndY=39.2 EndZ=0
    g7: LineSegment StartX=82.8 StartY=39.2 StartZ=0 EndX=0 EndY=39.2 EndZ=0
    g8: ArcOfCircle CenterX=19 CenterY=21.2 CenterZ=0 NormalX=0 NormalY=0 NormalZ=1 AngleXU=0 Radius=10 StartAngle=1.5708 EndAngle=4.71239
    g9: ArcOfCircle CenterX=65 CenterY=21.2 CenterZ=0 NormalX=0 NormalY=0 NormalZ=1 AngleXU=0 Radius=10 StartAngle=4.71239 EndAngle=7.85398
    g10: LineSegment StartX=19 StartY=31.2 StartZ=0 EndX=65 EndY=31.2 EndZ=0
    g11: LineSegment StartX=19 StartY=11.2 StartZ=0 EndX=65 EndY=11.2 EndZ=0
  constraints (25):
    c: Equal(g2,g-7)
    c: Equal(g3,g-8)
    c: Equal(g1,g-13)
    c: Equal(g0,g-12)
    c: Coincident(g0,g-12)
    c: Coincident(g1,g-13)
    c: Coincident(g3,g-8)
    c: Coincident(g2,g-7)
    c: Coincident(g4,g-4)
    c: Coincident(g4,g-5)
    c: Coincident(g5,g4)
    c: Coincident(g5,g-6)
    c: Coincident(g6,g5)
    c: PointOnObject(g6,g-3)
    c: Vertical(g6)
    c: Coincident(g7,g6)
    c: Coincident(g7,g4)
    c: Tangent(g8,g10) = 1.5708
    c: Tangent(g8,g11) = -1.5708
    c: Tangent(g9,g10) = 1.5708
    c: Tangent(g9,g11) = -1.5708
    c: Equal(g8,g9)
    c: Radius(g8) = 10
    c: Coincident(g8,g-11)
    c: Coincident(g9,g-9)
FEATURE [Sketcher::SketchObject] Sketch093  label="Sketch093 - scavi interni pulsanti"
  ArcFitTolerance = 1e-06
  AttachmentSupport = -> [Pad019]
  ExternalGeometry = -> [Binder]
  FullyConstrained = true
  MakeInternals = false
  MapMode = 5
  Placement = pos=(0,1.8e-15,0) rot=(1,0,0;1.5708rad)
  sketch-geometry (3):
    g0: Circle CenterX=-65 CenterY=21.2 CenterZ=0 NormalX=0 NormalY=0 NormalZ=1 AngleXU=0 Radius=7.3
    g1: Circle CenterX=-42 CenterY=21.2 CenterZ=0 NormalX=0 NormalY=0 NormalZ=1 AngleXU=0 Radius=7.3
    g2: Circle CenterX=-19 CenterY=21.2 CenterZ=0 NormalX=0 NormalY=0 NormalZ=1 AngleXU=0 Radius=7.3
  constraints (6):
    c: Coincident(g0,g-3)
    c: Coincident(g1,g-4)
    c: Coincident(g2,g-5)
    c: Diameter(g0) = 14.6
    c: Diameter(g1) = 14.6
    c: Diameter(g2) = 14.6
FEATURE [Sketcher::SketchObject] Sketch094  label="Sketch094 - forma centrale"
  ArcFitTolerance = 1e-06
  AttachmentSupport = -> [Pad019]
  ExternalGeometry = -> [Binder]
  FullyConstrained = true
  MakeInternals = false
  MapMode = 5
  Placement = pos=(0,2,0) rot=(0,0.707107,0.707107;3.14159rad)
  sketch-geometry (4):
    g0: LineSegment StartX=137.815 StartY=39.2 StartZ=0 EndX=142.655 EndY=24.303 EndZ=0
    g1: LineSegment StartX=110.815 StartY=24.303 StartZ=0 EndX=142.655 EndY=24.303 EndZ=0
    g2: LineSegment StartX=137.815 StartY=39.2 StartZ=0 EndX=110.815 EndY=39.2 EndZ=0
    g3: ArcOfCircle CenterX=92.2534 CenterY=31.7515 CenterZ=0 NormalX=0 NormalY=0 NormalZ=1 AngleXU=0 Radius=20 StartAngle=5.90156 EndAngle=6.66481
  constraints (12):
    c: PointOnObject(g0,g-3)
    c: Tangent(g0,g-5)
    c: Horizontal(g1)
    c: Coincident(g1,g0)
    c: Coincident(g2,g0)
    c: PointOnObject(g2,g-3)
    c: DistanceX(g2,g2) = 27
    c: Vertical(g1,g2)
    c: Coincident(g3,g2)
    c: Radius(g3) = 20
    c: Coincident(g3,g1)
    c: DistanceY(g-6,g0) = 4
FEATURE [Sketcher::SketchObject] Sketch095  label="Sketch095 - forma posteriore"
  ArcFitTolerance = 1e-06
  AttachmentSupport = -> [Pad019]
  ExternalGeometry = -> [Binder]
  FullyConstrained = true
  MakeInternals = false
  MapMode = 5
  Placement = pos=(0,2,0) rot=(0,0.707107,0.707107;3.14159rad)
  sketch-geometry (15):
    g0: LineSegment StartX=137.815 StartY=39.2 StartZ=0 EndX=143.955 EndY=20.303 EndZ=0
    g1: LineSegment StartX=143.955 StartY=20.303 StartZ=0 EndX=190.141 EndY=20.303 EndZ=0
    g2: ArcOfCircle CenterX=184.08 CenterY=34.8 CenterZ=0 NormalX=0 NormalY=0 NormalZ=1 AngleXU=0 Radius=3.5 StartAngle=3.49066 EndAngle=4.71239
    g3: LineSegment StartX=180.791 StartY=33.6029 StartZ=0 EndX=178.754 EndY=39.2 EndZ=0
    g4: LineSegment StartX=184.08 StartY=31.3 StartZ=0 EndX=186.139 EndY=31.3 EndZ=0
    g5: LineSegment StartX=190.141 StartY=20.303 StartZ=0 EndX=186.139 EndY=31.3 EndZ=0
    g6: LineSegment StartX=137.815 StartY=39.2 StartZ=0 EndX=156.815 EndY=39.2 EndZ=0
    g7: LineSegment StartX=178.754 StartY=39.2 StartZ=0 EndX=168.815 EndY=39.2 EndZ=0
    g8: LineSegment StartX=156.815 StartY=31.2 StartZ=0 EndX=168.815 EndY=31.2 EndZ=0
    g9: ArcOfCircle CenterX=176.411 CenterY=35.2 CenterZ=0 NormalX=0 NormalY=0 NormalZ=1 AngleXU=0 Radius=20 StartAngle=2.94023 EndAngle=3.34295
    g10: ArcOfCircle CenterX=188.411 CenterY=35.2 CenterZ=0 NormalX=0 NormalY=0 NormalZ=1 AngleXU=0 Radius=20 StartAngle=2.94023 EndAngle=3.34295
    g11: LineSegment StartX=157.815 StartY=39.2 StartZ=0 EndX=167.815 EndY=39.2 EndZ=0
    g12: LineSegment StartX=157.436 StartY=36.2 StartZ=0 EndX=167.436 EndY=36.2 EndZ=0
    g13: ArcOfCircle CenterX=177.411 CenterY=35.2 CenterZ=0 NormalX=0 NormalY=0 NormalZ=1 AngleXU=0 Radius=20 StartAngle=2.94023 EndAngle=3.09157
    g14: ArcOfCircle CenterX=187.411 CenterY=35.2 CenterZ=0 NormalX=0 NormalY=0 NormalZ=1 AngleXU=0 Radius=20 StartAngle=2.94023 EndAngle=3.09157
  constraints (46):
    c: PointOnObject(g0,g-3)
    c: Tangent(g0,g-6)
    c: Coincident(g1,g0)
    c: Horizontal(g1)
    c: Radius(g2) = 3.5
    c: Coincident(g2,g-5)
    c: PointOnObject(g3,g-3)
    c: Parallel(g3,g-4)
    c: Tangent(g3,g2) = 1.5708
    c: Horizontal(g4)
    c: Tangent(g4,g2) = -1.5708
    c: Coincident(g5,g1)
    c: Parallel(g5,g-4)
    c: Coincident(g5,g4)
    c: DistanceX(g4,g-8) = 3.8
    c: Coincident(g6,g0)
    c: PointOnObject(g6,g-3)
    c: Coincident(g7,g3)
    c: PointOnObject(g7,g-3)
    c: Horizontal(g8)
    c: DistanceX(g6,g7) = 12
    c: Vertical(g8,g6)
    c: Vertical(g7,g8)
    c: DistanceY(g8,g6) = 8
    c: Coincident(g9,g8)
    c: Coincident(g9,g6)
    c: Coincident(g10,g7)
    c: Coincident(g10,g8)
    c: Radius(g9) = 20
    c: Radius(g10) = 20
    c: PointOnObject(g11,g-3)
    c: PointOnObject(g11,g-3)
    c: DistanceX(g11,g11) = 10
    c: DistanceX(g6,g11) = 1
    c: Horizontal(g12)
    c: Equal(g12,g11)
    c: DistanceY(g12,g11) = 3
    c: Coincident(g13,g11)
    c: Coincident(g13,g12)
    c: Radius(g13) = 20
    c: Coincident(g14,g11)
    c: Coincident(g14,g12)
    c: Radius(g14) = 20
    c: DistanceX(g0,g6) = 19
    c: Horizontal(g9,g13)
    c: Horizontal(g0,g-4)
FEATURE [Sketcher::SketchObject] Sketch096  label="Sketch096 - forma impugnatura"
  ArcFitTolerance = 1e-06
  AttachmentSupport = -> [Pad019]
  ExternalGeometry = -> [Binder]
  FullyConstrained = true
  MakeInternals = false
  MapMode = 5
  Placement = pos=(0,2,0) rot=(0,0.707107,0.707107;3.14159rad)
  sketch-geometry (8):
    g0: LineSegment StartX=176.685 StartY=-80.4316 StartZ=0 EndX=143.955 EndY=20.303 EndZ=0
    g1: LineSegment StartX=176.685 StartY=-80.4316 StartZ=0 EndX=215.932 EndY=-80.4316 EndZ=0
    g2: Circle CenterX=179.305 CenterY=-76.8316 CenterZ=0 NormalX=0 NormalY=0 NormalZ=1 AngleXU=0 Radius=3
    g3: Circle CenterX=213.443 CenterY=-76.8316 CenterZ=0 NormalX=0 NormalY=0 NormalZ=1 AngleXU=0 Radius=3
    g4: LineSegment StartX=143.955 StartY=20.303 StartZ=0 EndX=202.765 EndY=20.303 EndZ=0
    g5: LineSegment StartX=215.42 StartY=-53.0314 StartZ=0 EndX=192.176 EndY=-3.18451 EndZ=0
    g6: ArcOfCircle CenterX=184.801 CenterY=-67.3089 CenterZ=0 NormalX=0 NormalY=0 NormalZ=1 AngleXU=0 Radius=33.7833 StartAngle=5.88425 EndAngle=6.71952
    g7: ArcOfCircle CenterX=207.583 CenterY=4 CenterZ=0 NormalX=0 NormalY=0 NormalZ=1 AngleXU=0 Radius=17 StartAngle=1.85815 EndAngle=3.57792
  constraints (19):
    c: Coincident(g0,g-4)
    c: PointOnObject(g0,g-3)
    c: Horizontal(g0,g-7)
    c: Coincident(g1,g0)
    c: Coincident(g1,g-5)
    c: Diameter(g2) = 6
    c: Diameter(g3) = 6
    c: Coincident(g2,g-9)
    c: Coincident(g3,g-10)
    c: Coincident(g4,g0)
    c: Coincident(g5,g-6)
    c: Coincident(g6,g1)
    c: Coincident(g6,g5)
    c: Equal(g-5,g6)
    c: Coincident(g5,g-7)
    c: Coincident(g4,g-7)
    c: Tangent(g7,g-7)
    c: Coincident(g7,g4)
    c: Coincident(g7,g5)
FEATURE [Sketcher::SketchObject] Sketch097
  ArcFitTolerance = 1e-06
  AttachmentSupport = -> [Pad019]
  ExternalGeometry = -> [Binder]
  FullyConstrained = true
  MakeInternals = false
  MapMode = 5
  Placement = pos=(0,2,0) rot=(0,0.707107,0.707107;3.14159rad)
  sketch-geometry (4):
    g0: LineSegment StartX=90 StartY=36.8 StartZ=0 EndX=108 EndY=36.8 EndZ=0
    g1: LineSegment StartX=108 StartY=36.8 StartZ=0 EndX=108 EndY=26.8 EndZ=0
    g2: LineSegment StartX=108 StartY=26.8 StartZ=0 EndX=90 EndY=26.8 EndZ=0
    g3: ArcOfCircle CenterX=94 CenterY=31.8 CenterZ=0 NormalX=0 NormalY=0 NormalZ=1 AngleXU=0 Radius=6.40312 StartAngle=2.24554 EndAngle=4.03765
  constraints (13):
    c: Horizontal(g0)
    c: Coincident(g1,g0)
    c: Vertical(g1)
    c: DistanceX(g0,g0) = 18
    c: DistanceY(g1,g1) = 10
    c: Coincident(g2,g1)
    c: Horizontal(g2)
    c: Equal(g2,g0)
    c: DistanceY(g0,g-3) = 2.4
    c: Coincident(g3,g0)
    c: Coincident(g3,g2)
    c: DistanceX(g2,g3) = 4
    c: DistanceX(g-3,g0) = 90
FEATURE [PartDesign::Chamfer] Chamfer015
  Angle = 45
  Base = -> Pad019 [Edge19,Edge22,Edge79]
  BaseFeature = -> Pad019
  ChamferType = 0
  FlipDirection = false
  Refine = true
  Size = 1.9
  Size2 = 1
  SupportTransform = false
  Suppressed = false
  UseAllEdges = false
FEATURE [PartDesign::Pocket] Pocket002
  BaseFeature = -> Chamfer015
  Direction = (0,1,-2e-16)
  Length = 1.2
  Length2 = 5
  Profile = -> Sketch093
  ReferenceAxis = -> Sketch093 [N_Axis]
  Refine = true
  Suppressed = false
  Type = 0
FEATURE [PartDesign::Pad] Pad005
  BaseFeature = -> Pocket002
  Direction = (0,1,-2e-16)
  Length = 1.6
  Length2 = 10
  Profile = -> Sketch091
  ReferenceAxis = -> Sketch091 [N_Axis]
  Refine = true
  Suppressed = false
  Type = 0
FEATURE [Sketcher::SketchObject] Sketch092  label="Sketch092 - scavi per viti anteriori"
  ArcFitTolerance = 1e-06
  AttachmentSupport = -> [Pad005]
  ExternalGeometry = -> [Binder]
  FullyConstrained = true
  MakeInternals = false
  MapMode = 5
  Placement = pos=(0,3.6,0) rot=(0,0.707107,0.707107;3.14159rad)
  sketch-geometry (20):
    g0: ArcOfCircle CenterX=5.6 CenterY=7.6 CenterZ=0 NormalX=0 NormalY=0 NormalZ=1 AngleXU=0 Radius=3.5 StartAngle=0 EndAngle=1.5708
    g1: ArcOfCircle CenterX=5.6 CenterY=34.8 CenterZ=0 NormalX=0 NormalY=0 NormalZ=1 AngleXU=0 Radius=3.5 StartAngle=4.71239 EndAngle=6.28319
    g2: ArcOfCircle CenterX=78.51 CenterY=34.8 CenterZ=0 NormalX=0 NormalY=0 NormalZ=1 AngleXU=0 Radius=3.5 StartAngle=3.14159 EndAngle=4.71239
    g3: ArcOfCircle CenterX=78.51 CenterY=7.6 CenterZ=0 NormalX=0 NormalY=0 NormalZ=1 AngleXU=0 Radius=3.5 StartAngle=1.5708 EndAngle=3.14159
    g4: LineSegment StartX=0 StartY=3.2 StartZ=0 EndX=0 EndY=11.1 EndZ=0
    g5: LineSegment StartX=0 StartY=11.1 StartZ=0 EndX=5.6 EndY=11.1 EndZ=0
    g6: LineSegment StartX=0 StartY=3.2 StartZ=0 EndX=9.1 EndY=3.2 EndZ=0
    g7: LineSegment StartX=9.1 StartY=3.2 StartZ=0 EndX=9.1 EndY=7.6 EndZ=0
    g8: LineSegment StartX=0 StartY=39.2 StartZ=0 EndX=0 EndY=31.3 EndZ=0
    g9: LineSegment StartX=0 StartY=31.3 StartZ=0 EndX=5.6 EndY=31.3 EndZ=0
    g10: LineSegment StartX=0 StartY=39.2 StartZ=0 EndX=9.1 EndY=39.2 EndZ=0
    g11: LineSegment StartX=9.1 StartY=39.2 StartZ=0 EndX=9.1 EndY=34.8 EndZ=0
    g12: LineSegment StartX=82.8 StartY=39.2 StartZ=0 EndX=75.01 EndY=39.2 EndZ=0
    g13: LineSegment StartX=82.8 StartY=39.2 StartZ=0 EndX=82.8 EndY=31.3 EndZ=0
    g14: LineSegment StartX=82.8 StartY=31.3 StartZ=0 EndX=78.51 EndY=31.3 EndZ=0
    g15: LineSegment StartX=82.8 StartY=3.2 StartZ=0 EndX=75.01 EndY=3.2 EndZ=0
    g16: LineSegment StartX=75.01 StartY=3.2 StartZ=0 EndX=75.01 EndY=7.6 EndZ=0
    g17: LineSegment StartX=82.8 StartY=3.2 StartZ=0 EndX=82.8 EndY=11.1 EndZ=0
    g18: LineSegment StartX=82.8 StartY=11.1 StartZ=0 EndX=78.51 EndY=11.1 EndZ=0
    g19: LineSegment StartX=75.01 StartY=39.2 StartZ=0 EndX=75.01 EndY=34.8 EndZ=0
  constraints (48):
    c: Radius(g0) = 3.5
    c: Coincident(g0,g-10)
    c: Radius(g1) = 3.5
    c: Coincident(g1,g-9)
    c: Radius(g2) = 3.5
    c: Coincident(g2,g-8)
    c: Radius(g3) = 3.5
    c: Coincident(g3,g-7)
    c: Coincident(g4,g-5)
    c: PointOnObject(g4,g-4)
    c: Coincident(g5,g4)
    c: Horizontal(g5)
    c: Coincident(g6,g4)
    c: PointOnObject(g6,g-5)
    c: Coincident(g7,g6)
    c: Vertical(g7)
    c: Coincident(g8,g-4)
    c: PointOnObject(g8,g-4)
    c: Coincident(g9,g8)
    c: Horizontal(g9)
    c: Coincident(g10,g8)
    c: PointOnObject(g10,g-3)
    c: Coincident(g11,g10)
    c: Vertical(g11)
    c: PointOnObject(g12,g-3)
    c: PointOnObject(g12,g-3)
    c: Coincident(g13,g12)
    c: Vertical(g13)
    c: Coincident(g14,g13)
    c: Horizontal(g14)
    c: Coincident(g15,g-6)
    c: PointOnObject(g15,g-5)
    c: Coincident(g16,g15)
    c: Vertical(g16)
    c: Coincident(g17,g15)
    c: Coincident(g18,g17)
    c: Horizontal(g18)
    c: Tangent(g3,g18) = -1.5708
    c: Tangent(g16,g3) = 1.5708
    c: Coincident(g19,g12)
    c: Vertical(g19)
    c: Tangent(g2,g19) = -1.5708
    c: Tangent(g2,g14) = 1.5708
    c: Tangent(g0,g7) = -1.5708
    c: Tangent(g0,g5) = 1.5708
    c: Tangent(g9,g1) = -1.5708
    c: Tangent(g1,g11) = 1.5708
    c: Tangent(g17,g13)
FEATURE [PartDesign::Pocket] Pocket001
  BaseFeature = -> Pad005
  Direction = (0,-1,2e-16)
  Length = 1.6
  Length2 = 5
  Profile = -> Sketch092
  ReferenceAxis = -> Sketch092 [N_Axis]
  Refine = true
  Suppressed = false
  Type = 0
FEATURE [PartDesign::Pad] Pad006
  BaseFeature = -> Pocket001
  Direction = (0,1,-2e-16)
  Length = 0.8
  Length2 = 10
  Profile = -> Sketch094
  ReferenceAxis = -> Sketch094 [N_Axis]
  Refine = true
  Suppressed = false
  Type = 0
FEATURE [PartDesign::Pad] Pad007
  BaseFeature = -> Pad006
  Direction = (0,1,-2e-16)
  Length = 2
  Length2 = 10
  Profile = -> Sketch095
  ReferenceAxis = -> Sketch095 [N_Axis]
  Refine = true
  Suppressed = false
  Type = 0
FEATURE [PartDesign::Pad] Pad008  label="Pad008 - forma impugnatura"
  BaseFeature = -> Pad007
  Direction = (0,1,-2e-16)
  Length = 1.6
  Length2 = 10
  Profile = -> Sketch096
  ReferenceAxis = -> Sketch096 [N_Axis]
  Refine = true
  Suppressed = false
  Type = 0
FEATURE [PartDesign::Pad] Pad009
  BaseFeature = -> Pad008
  Direction = (0,1,-2e-16)
  Length = 1.6
  Length2 = 10
  Profile = -> Sketch097
  ReferenceAxis = -> Sketch097 [N_Axis]
  Refine = true
  Suppressed = false
  Type = 0
FEATURE [Sketcher::SketchObject] Sketch098
  ArcFitTolerance = 1e-06
  AttachmentSupport = -> [Pad006]
  ExternalGeometry = -> [Binder]
  FullyConstrained = true
  MakeInternals = false
  MapMode = 5
  Placement = pos=(0,2.8,-7e-16) rot=(0,0.707107,0.707107;3.14159rad)
  sketch-geometry (4):
    g0: LineSegment StartX=118 StartY=39.2 StartZ=0 EndX=129 EndY=39.2 EndZ=0
    g1: LineSegment StartX=120.599 StartY=31.2 StartZ=0 EndX=131.599 EndY=31.2 EndZ=0
    g2: LineSegment StartX=129 StartY=39.2 StartZ=0 EndX=131.599 EndY=31.2 EndZ=0
    g3: LineSegment StartX=118 StartY=39.2 StartZ=0 EndX=120.599 EndY=31.2 EndZ=0
  constraints (12):
    c: PointOnObject(g0,g-3)
    c: PointOnObject(g0,g-3)
    c: DistanceX(g0,g0) = 11
    c: Horizontal(g1)
    c: Equal(g1,g0)
    c: Coincident(g2,g0)
    c: Coincident(g3,g0)
    c: Parallel(g-4,g2)
    c: Coincident(g1,g2)
    c: Coincident(g1,g3)
    c: DistanceY(g1,g0) = 8
    c: DistanceX(g-3,g0) = 118
FEATURE [Sketcher::SketchObject] Sketch099
  ArcFitTolerance = 1e-06
  AttachmentSupport = -> [Pad008]
  ExternalGeometry = -> [Binder]
  FullyConstrained = true
  MakeInternals = false
  MapMode = 5
  Placement = pos=(0,3.6,0) rot=(0,0.707107,0.707107;3.14159rad)
  sketch-geometry (13):
    g0: LineSegment StartX=192.176 StartY=-3.18451 StartZ=0 EndX=196.804 EndY=-13.1108 EndZ=0
    g1: LineSegment [constr] StartX=202.765 StartY=20.303 StartZ=0 EndX=181.223 EndY=20.303 EndZ=0
    g2: LineSegment [constr] StartX=181.223 StartY=20.303 StartZ=0 EndX=181.223 EndY=-3.18451 EndZ=0
    g3: ArcOfCircle CenterX=181.223 CenterY=-20.3764 CenterZ=0 NormalX=0 NormalY=0 NormalZ=1 AngleXU=0 Radius=17.1918 StartAngle=0.436332 EndAngle=1.57079
    g4: ArcOfEllipse CenterX=181.223 CenterY=8.55923 CenterZ=0 NormalX=0 NormalY=0 NormalZ=1 MajorRadius=23.4779 MinorRadius=11.7437 AngleXU=0 StartAngle=1.5708 EndAngle=4.71239
    g5: LineSegment [constr] StartX=204.701 StartY=8.55923 StartZ=0 EndX=157.745 EndY=8.55923 EndZ=0
    g6: LineSegment [constr] StartX=181.223 StartY=20.303 StartZ=0 EndX=181.223 EndY=-3.18451 EndZ=0
    g7: GeomPoint [constr] X=201.553 Y=8.55923 Z=0
    g8: GeomPoint [constr] X=160.894 Y=8.55923 Z=0
    g9: GeomPoint [constr] X=181.223 Y=-3.18451 Z=0
    g10: LineSegment StartX=181.223 StartY=20.303 StartZ=0 EndX=202.765 EndY=20.303 EndZ=0
    g11: ArcOfCircle CenterX=207.583 CenterY=4 CenterZ=0 NormalX=0 NormalY=0 NormalZ=1 AngleXU=0 Radius=17 StartAngle=1.85815 EndAngle=3.57792
    g12: LineSegment [constr] StartX=172.411 StartY=39.2 StartZ=0 EndX=192.176 EndY=-3.18451 EndZ=0
  constraints (27):
    c: Coincident(g1,g-7)
    c: Horizontal(g1)
    c: Coincident(g2,g1)
    c: Vertical(g2)
    c: Horizontal(g2,g0)
    c: Coincident(g3,g0)
    c: Coincident(g3,g2)
    c: InternalAlignment(g5-g8 -> g4) x4
    c: Horizontal(g5)
    c: PointOnObject(g4,g2)
    c: Coincident(g4,g1)
    c: DistanceX(g-3,g5) = 10.1
    c: Coincident(g4,g2)
    c: Tangent(g3,g-5)
    c: PointOnObject(g9,g4)
    c: PointOnObject(g9,g3)
    c: Tangent(g4,g3,g9) = 1.5708
    c: Coincident(g10,g1)
    c: Coincident(g10,g1)
    c: Equal(g11,g-4)
    c: Coincident(g11,g1)
    c: Coincident(g11,g0)
    c: PointOnObject(g12,g-6)
    c: PointOnObject(g1,g12)
    c: Tangent(g12,g-5) = -1.5708
    c: Tangent(g0,g-5) = -1.5708
    c: Horizontal(g9,g12)
FEATURE [Sketcher::SketchObject] Sketch106  label="Sketch106 - smusso impuniatura interno"
  ArcFitTolerance = 1e-06
  AttachmentSupport = -> [Pad008]
  ExternalGeometry = -> [Pad008]
  FullyConstrained = true
  MakeInternals = false
  MapMode = 5
  Placement = pos=(0,-1.586e-13,-80.4316) rot=(1,0,0;3.14159rad)
  sketch-geometry (9):
    g0: LineSegment StartX=-176.685 StartY=-3.6 StartZ=0 EndX=-176.685 EndY=-1.15e-13 EndZ=0
    g1: LineSegment [constr] StartX=-176.685 StartY=-1.416e-13 StartZ=0 EndX=-176.685 EndY=-1.149e-13 EndZ=0
    g2: LineSegment [constr] StartX=-186.685 StartY=-3.6 StartZ=0 EndX=-186.685 EndY=-1.15e-13 EndZ=0
    g3: ArcOfEllipse CenterX=-186.685 CenterY=-1.149e-13 CenterZ=0 NormalX=0 NormalY=0 NormalZ=1 MajorRadius=10 MinorRadius=3.6 AngleXU=-3.14159 StartAngle=1.5708 EndAngle=3.14159
    g4: LineSegment [constr] StartX=-196.685 StartY=-1.416e-13 StartZ=0 EndX=-176.685 EndY=-1.416e-13 EndZ=0
    g5: LineSegment [constr] StartX=-186.685 StartY=-3.6 StartZ=0 EndX=-186.685 EndY=3.6 EndZ=0
    g6: GeomPoint [constr] X=-196.015 Y=-1.43e-13 Z=0
    g7: GeomPoint [constr] X=-177.356 Y=-1.415e-13 Z=0
    g8: LineSegment StartX=-176.685 StartY=-3.6 StartZ=0 EndX=-186.685 EndY=-3.6 EndZ=0
  constraints (15):
    c: PointOnObject(g2,g-3)
    c: Coincident(g1,g-5)
    c: DistanceY(g1,g1) = 0
    c: Coincident(g0,g1)
    c: DistanceX(g2,g-5) = 10
    c: Vertical(g2)
    c: Horizontal(g2,g0)
    c: InternalAlignment(g4-g7 -> g3) x4
    c: Coincident(g3,g2)
    c: Horizontal(g4)
    c: Coincident(g3,g0)
    c: Tangent(g0,g-5) = 1.5708
    c: Coincident(g3,g2)
    c: Coincident(g8,g0)
    c: Coincident(g8,g2)
FEATURE [Sketcher::SketchObject] Sketch107  label="Sketch107 - smusso impugnatura esterno"
  ArcFitTolerance = 1e-06
  AttachmentSupport = -> [Pad008]
  ExternalGeometry = -> [Pad008]
  FullyConstrained = true
  MakeInternals = false
  MapMode = 5
  Placement = pos=(0,-1.586e-13,-80.4316) rot=(1,0,0;3.14159rad)
  sketch-geometry (9):
    g0: LineSegment [constr] StartX=-215.932 StartY=-1.416e-13 StartZ=0 EndX=-215.932 EndY=-5.02e-14 EndZ=0
    g1: LineSegment StartX=-215.932 StartY=-3.6 StartZ=0 EndX=-215.932 EndY=-5.02e-14 EndZ=0
    g2: LineSegment StartX=-215.932 StartY=-3.6 StartZ=0 EndX=-205.932 EndY=-3.6 EndZ=0
    g3: LineSegment [constr] StartX=-205.932 StartY=-3.6 StartZ=0 EndX=-205.932 EndY=-5.02e-14 EndZ=0
    g4: ArcOfEllipse CenterX=-205.932 CenterY=-5.02e-14 CenterZ=0 NormalX=0 NormalY=0 NormalZ=1 MajorRadius=10 MinorRadius=3.6 AngleXU=-3.14159 StartAngle=-2.66e-14 EndAngle=1.5708
    g5: LineSegment [constr] StartX=-215.932 StartY=-1.416e-13 StartZ=0 EndX=-195.932 EndY=-1.416e-13 EndZ=0
    g6: LineSegment [constr] StartX=-205.932 StartY=-3.6 StartZ=0 EndX=-205.932 EndY=3.6 EndZ=0
    g7: GeomPoint [constr] X=-215.262 Y=-1.425e-13 Z=0
    g8: GeomPoint [constr] X=-196.602 Y=-1.551e-13 Z=0
  constraints (16):
    c: Coincident(g0,g-6)
    c: PointOnObject(g0,g-6)
    c: DistanceY(g0,g0) = 0
    c: Coincident(g1,g-6)
    c: Coincident(g1,g0)
    c: Tangent(g2,g-3)
    c: DistanceX(g2,g2) = 10
    c: Coincident(g3,g2)
    c: Vertical(g3)
    c: Horizontal(g3,g0)
    c: InternalAlignment(g5-g8 -> g4) x4
    c: Coincident(g4,g3)
    c: Horizontal(g5)
    c: Coincident(g4,g0)
    c: Coincident(g4,g2)
    c: PointOnObject(g2,g1)
FEATURE [Sketcher::SketchObject] Sketch108
  ArcFitTolerance = 1e-06
  AttachmentOffset = pos=(0,0,-1.6) rot=(0,0,1;0rad)
  AttachmentSupport = -> [Pad008]
  ExternalGeometry = -> [Binder]
  FullyConstrained = true
  MakeInternals = false
  MapMode = 5
  Placement = pos=(0,2,4e-16) rot=(0,0.707107,0.707107;3.14159rad)
  sketch-geometry (14):
    g0: LineSegment StartX=192.176 StartY=-3.18451 StartZ=0 EndX=193.827 EndY=-6.72678 EndZ=0
    g1: LineSegment [constr] StartX=202.765 StartY=20.303 StartZ=0 EndX=181.223 EndY=20.303 EndZ=0
    g2: LineSegment [constr] StartX=181.223 StartY=20.303 StartZ=0 EndX=181.223 EndY=1.30297 EndZ=0
    g3: ArcOfCircle CenterX=181.223 CenterY=-12.6042 CenterZ=0 NormalX=0 NormalY=0 NormalZ=1 AngleXU=0 Radius=13.9072 StartAngle=0.436332 EndAngle=1.5708
    g4: ArcOfEllipse CenterX=181.223 CenterY=10.803 CenterZ=0 NormalX=0 NormalY=0 NormalZ=1 MajorRadius=14.4779 MinorRadius=9.5 AngleXU=0 StartAngle=1.5708 EndAngle=4.71239
    g5: LineSegment [constr] StartX=195.701 StartY=10.803 StartZ=0 EndX=166.745 EndY=10.803 EndZ=0
    g6: LineSegment [constr] StartX=181.223 StartY=20.303 StartZ=0 EndX=181.223 EndY=1.30297 EndZ=0
    g7: GeomPoint [constr] X=192.148 Y=10.803 Z=0
    g8: GeomPoint [constr] X=170.298 Y=10.803 Z=0
    g9: LineSegment StartX=181.223 StartY=20.303 StartZ=0 EndX=202.765 EndY=20.303 EndZ=0
    g10: ArcOfCircle CenterX=207.583 CenterY=4 CenterZ=0 NormalX=0 NormalY=0 NormalZ=1 AngleXU=0 Radius=17 StartAngle=1.85815 EndAngle=3.57792
    g11: LineSegment [constr] StartX=172.411 StartY=39.2 StartZ=0 EndX=192.176 EndY=-3.18451 EndZ=0
    g12: GeomPoint [constr] X=181.223 Y=1.30297 Z=0
    g13: GeomPoint [constr] X=181.223 Y=1.30297 Z=0
  constraints (28):
    c: Coincident(g1,g-7)
    c: Horizontal(g1)
    c: Coincident(g2,g1)
    c: Vertical(g2)
    c: Coincident(g3,g2)
    c: InternalAlignment(g5-g8 -> g4) x4
    c: Horizontal(g5)
    c: PointOnObject(g4,g2)
    c: Coincident(g4,g1)
    c: DistanceX(g-3,g5) = 19.1
    c: Coincident(g4,g2)
    c: Coincident(g9,g1)
    c: Coincident(g9,g1)
    c: Coincident(g10,g1)
    c: Coincident(g10,g0)
    c: PointOnObject(g11,g-6)
    c: PointOnObject(g1,g11)
    c: DistanceY(g2,g1) = 19
    c: Coincident(g10,g-4)
    c: PointOnObject(g12,g4)
    c: PointOnObject(g12,g3)
    c: Tangent(g11,g-5) = -1.5708
    c: Tangent(g0,g-5) = -1.5708
    c: Tangent(g3,g0) = 1.5708
    c: PointOnObject(g13,g4)
    c: PointOnObject(g13,g3)
    c: Tangent(g4,g3,g13) = 1.5708
    c: Horizontal(g11,g0)
FEATURE [Part::Part2DObjectPython] Clone2D  label="Sketch108 (2D)"  # Draft 2D object (typed FeaturePython)
  Fuse = false
  Objects = -> [Sketch108]
  Placement = pos=(0,2,4e-16) rot=(0,0.707107,0.707107;3.14159rad)
  Scale = (1,1,1)
FEATURE [Sketcher::SketchObject] Sketch109
  ArcFitTolerance = 1e-06
  AttachmentOffset = pos=(0,0,-3.5) rot=(0,0,1;0rad)
  AttachmentSupport = -> [Pad008]
  ExternalGeometry = -> [Binder]
  FullyConstrained = true
  MakeInternals = false
  MapMode = 5
  Placement = pos=(0,0.1,8e-16) rot=(0,0.707107,0.707107;3.14159rad)
  sketch-geometry (1):
    g0: GeomPoint X=197.47 Y=8.55923 Z=0
  constraints (1):
    c: Symmetric(g-7,g-5,g0)
FEATURE [PartDesign::Chamfer] Chamfer005
  Angle = 45
  Base = -> Pad009 [Edge215,Edge212]
  BaseFeature = -> Pad009
  ChamferType = 1
  FlipDirection = false
  Refine = true
  Size = 1.5
  Size2 = 2.8
  SupportTransform = false
  Suppressed = false
  UseAllEdges = false
FEATURE [Sketcher::SketchObject] Sketch111
  ArcFitTolerance = 1e-06
  AttachmentSupport = -> [Pad009]
  ExternalGeometry = -> [Pad009]
  FullyConstrained = true
  MakeInternals = false
  MapMode = 5
  Placement = pos=(0,3.6,-8e-16) rot=(0,0.707107,0.707107;3.14159rad)
  sketch-geometry (21):
    g0: LineSegment [constr] StartX=97 StartY=36.8 StartZ=0 EndX=97 EndY=26.8 EndZ=0
    g1: LineSegment StartX=97 StartY=28.6 StartZ=0 EndX=97 EndY=27.8 EndZ=0
    g2: LineSegment StartX=97 StartY=27.8 StartZ=0 EndX=108 EndY=27.8 EndZ=0
    g3: LineSegment StartX=108 StartY=27.8 StartZ=0 EndX=108 EndY=28.6 EndZ=0
    g4: LineSegment StartX=108 StartY=28.6 StartZ=0 EndX=97 EndY=28.6 EndZ=0
    g5: LineSegment StartX=97 StartY=35.8 StartZ=0 EndX=97 EndY=35 EndZ=0
    g6: LineSegment StartX=97 StartY=35 StartZ=0 EndX=108 EndY=35 EndZ=0
    g7: LineSegment StartX=108 StartY=35 StartZ=0 EndX=108 EndY=35.8 EndZ=0
    g8: LineSegment StartX=108 StartY=35.8 StartZ=0 EndX=97 EndY=35.8 EndZ=0
    g9: LineSegment StartX=97 StartY=30.4 StartZ=0 EndX=97 EndY=29.6 EndZ=0
    g10: LineSegment StartX=97 StartY=29.6 StartZ=0 EndX=108 EndY=29.6 EndZ=0
    g11: LineSegment StartX=108 StartY=29.6 StartZ=0 EndX=108 EndY=30.4 EndZ=0
    g12: LineSegment StartX=108 StartY=30.4 StartZ=0 EndX=97 EndY=30.4 EndZ=0
    g13: LineSegment StartX=97 StartY=34 StartZ=0 EndX=97 EndY=33.2 EndZ=0
    g14: LineSegment StartX=97 StartY=33.2 StartZ=0 EndX=108 EndY=33.2 EndZ=0
    g15: LineSegment StartX=108 StartY=33.2 StartZ=0 EndX=108 EndY=34 EndZ=0
    g16: LineSegment StartX=108 StartY=34 StartZ=0 EndX=97 EndY=34 EndZ=0
    g17: LineSegment StartX=97 StartY=32.2 StartZ=0 EndX=97 EndY=31.4 EndZ=0
    g18: LineSegment StartX=97 StartY=31.4 StartZ=0 EndX=108 EndY=31.4 EndZ=0
    g19: LineSegment StartX=108 StartY=31.4 StartZ=0 EndX=108 EndY=32.2 EndZ=0
    g20: LineSegment StartX=108 StartY=32.2 StartZ=0 EndX=97 EndY=32.2 EndZ=0
  constraints (54):
    c: Vertical(g0)
    c: PointOnObject(g0,g-3)
    c: PointOnObject(g0,g-4)
    c: DistanceX(g0,g-5) = 11
    c: Coincident(g1,g2)
    c: Coincident(g2,g3)
    c: Coincident(g3,g4)
    c: Coincident(g4,g1)
    c: Horizontal(g2)
    c: Horizontal(g4)
    c: Tangent(g1,g0)
    c: Tangent(g3,g-5)
    c: DistanceY(g2,g3) = 0.8
    c: Coincident(g5,g6)
    c: Coincident(g6,g7)
    c: Coincident(g7,g8)
    c: Coincident(g8,g5)
    c: Horizontal(g6)
    c: Horizontal(g8)
    c: DistanceY(g6,g7) = 0.8
    c: Coincident(g9,g10)
    c: Coincident(g10,g11)
    c: Coincident(g11,g12)
    c: Coincident(g12,g9)
    c: Horizontal(g10)
    c: Horizontal(g12)
    c: DistanceY(g10,g11) = 0.8
    c: Tangent(g5,g0)
    c: Tangent(g7,g-5)
    c: Tangent(g9,g0)
    c: Tangent(g11,g-5)
    c: Coincident(g13,g14)
    c: Coincident(g14,g15)
    c: Coincident(g15,g16)
    c: Coincident(g16,g13)
    c: Horizontal(g14)
    c: Horizontal(g16)
    c: DistanceY(g14,g15) = 0.8
    c: Tangent(g13,g0)
    c: Tangent(g15,g-5)
    c: Coincident(g17,g18)
    c: Coincident(g18,g19)
    c: Coincident(g19,g20)
    c: Coincident(g20,g17)
    c: Horizontal(g18)
    c: Horizontal(g20)
    c: DistanceY(g18,g19) = 0.8
    c: Tangent(g17,g0)
    c: Tangent(g19,g-5)
    c: DistanceY(g1,g9) = 1
    c: DistanceY(g9,g17) = 1
    c: DistanceY(g17,g13) = 1
    c: DistanceY(g13,g5) = 1
    c: DistanceY(g0,g1) = 1
FEATURE [PartDesign::Pocket] Pocket004
  BaseFeature = -> Chamfer005
  Direction = (0,-1,2e-16)
  Length = 1
  Length2 = 5
  Profile = -> Sketch111
  ReferenceAxis = -> Sketch111 [N_Axis]
  Refine = true
  Suppressed = false
  Type = 0
FEATURE [PartDesign::Pad] Pad010
  BaseFeature = -> Pocket004
  Direction = (0,1,-2e-16)
  Length = 1.2
  Length2 = 10
  Profile = -> Sketch098
  ReferenceAxis = -> Sketch098 [N_Axis]
  Refine = true
  Suppressed = false
  Type = 0
FEATURE [PartDesign::Chamfer] Chamfer006
  Angle = 45
  Base = -> Pad010 [Edge291]
  BaseFeature = -> Pad010
  ChamferType = 1
  FlipDirection = false
  Refine = true
  Size = 1
  Size2 = 6
  SupportTransform = false
  Suppressed = false
  UseAllEdges = false
FEATURE [Sketcher::SketchObject] Sketch110
  ArcFitTolerance = 1e-06
  AttachmentSupport = -> [Pad010]
  ExternalGeometry = -> [Sketch098]
  FullyConstrained = true
  MakeInternals = false
  MapMode = 5
  Placement = pos=(0,4,-9e-16) rot=(0,0.707107,0.707107;3.14159rad)
  sketch-geometry (8):
    g0: LineSegment StartX=119.69 StartY=34 StartZ=0 EndX=130.69 EndY=34 EndZ=0
    g1: LineSegment StartX=119.95 StartY=33.2 StartZ=0 EndX=130.95 EndY=33.2 EndZ=0
    g2: LineSegment StartX=119.137 StartY=35.7 StartZ=0 EndX=130.137 EndY=35.7 EndZ=0
    g3: LineSegment StartX=118.877 StartY=36.5 StartZ=0 EndX=129.877 EndY=36.5 EndZ=0
    g4: LineSegment StartX=118.877 StartY=36.5 StartZ=0 EndX=119.137 EndY=35.7 EndZ=0
    g5: LineSegment StartX=129.877 StartY=36.5 StartZ=0 EndX=130.137 EndY=35.7 EndZ=0
    g6: LineSegment StartX=119.69 StartY=34 StartZ=0 EndX=119.95 EndY=33.2 EndZ=0
    g7: LineSegment StartX=130.69 StartY=34 StartZ=0 EndX=130.95 EndY=33.2 EndZ=0
  constraints (24):
    c: Horizontal(g0)
    c: Horizontal(g1)
    c: Horizontal(g2)
    c: Horizontal(g3)
    c: Equal(g1,g-5)
    c: Equal(g0,g-5)
    c: Equal(g2,g-5)
    c: Equal(g3,g-5)
    c: PointOnObject(g0,g-3)
    c: PointOnObject(g1,g-3)
    c: PointOnObject(g2,g-3)
    c: PointOnObject(g3,g-3)
    c: Coincident(g4,g3)
    c: Coincident(g4,g2)
    c: Coincident(g5,g3)
    c: Coincident(g5,g2)
    c: Coincident(g6,g0)
    c: Coincident(g6,g1)
    c: Coincident(g7,g0)
    c: Coincident(g7,g1)
    c: DistanceY(g1,g0) = 0.8
    c: DistanceY(g2,g3) = 0.8
    c: DistanceY(g-5,g1) = 2
    c: DistanceY(g-5,g2) = 4.5
FEATURE [PartDesign::Pocket] Pocket003
  BaseFeature = -> Chamfer006
  Direction = (0,-1,2e-16)
  Length = 1
  Length2 = 5
  Profile = -> Sketch110
  ReferenceAxis = -> Sketch110 [N_Axis]
  Refine = true
  Suppressed = false
  Type = 0
FEATURE [PartDesign::SubtractivePipe] SubtractivePipe
  AuxilleryCurvelinear = true
  AuxillerySpineTangent = false
  BaseFeature = -> Pocket003
  Binormal = (0,0,0)
  Mode = 0
  Profile = -> Sketch106
  Refine = true
  Spine = -> Pad008 [Edge215]
  SpineTangent = false
  Suppressed = false
  Transformation = 0
  Transition = 0
FEATURE [PartDesign::SubtractivePipe] SubtractivePipe001
  AuxilleryCurvelinear = true
  AuxillerySpineTangent = false
  BaseFeature = -> SubtractivePipe
  Binormal = (0,0,0)
  Mode = 0
  Profile = -> Sketch107
  Refine = true
  Spine = -> Pad008 [Edge213,Edge216,Edge210]
  SpineTangent = false
  Suppressed = false
  Transformation = 0
  Transition = 0
FEATURE [PartDesign::SubtractiveLoft] SubtractiveLoft
  BaseFeature = -> SubtractivePipe001
  Closed = false
  Profile = -> Sketch099
  Refine = true
  Ruled = false
  Sections = -> [Sketch108]
  Suppressed = false
FEATURE [PartDesign::SubtractiveLoft] SubtractiveLoft001
  BaseFeature = -> SubtractiveLoft
  Closed = false
  Profile = -> Clone2D
  Refine = true
  Ruled = false
  Sections = -> [Sketch109]
  Suppressed = false
FEATURE [Sketcher::SketchObject] Sketch112
  ArcFitTolerance = 1e-06
  AttachmentSupport = -> [Pad008]
  ExternalGeometry = -> [Binder]
  FullyConstrained = true
  MakeInternals = false
  MapMode = 5
  Placement = pos=(0,3.6,0) rot=(0,0.707107,0.707107;3.14159rad)
  sketch-geometry (4):
    g0: LineSegment [constr] StartX=167.782 StartY=-53.0314 StartZ=0 EndX=215.42 EndY=-53.0314 EndZ=0
    g1: GeomPoint [constr] X=191.282 Y=-53.0314 Z=0
    g2: Circle CenterX=191.282 CenterY=-53.0314 CenterZ=0 NormalX=0 NormalY=0 NormalZ=1 AngleXU=0 Radius=11.5
    g3: Circle CenterX=191.282 CenterY=-53.0314 CenterZ=0 NormalX=0 NormalY=0 NormalZ=1 AngleXU=0 Radius=10.7
  constraints (9):
    c: Horizontal(g0)
    c: PointOnObject(g0,g-3)
    c: Diameter(g2) = 23
    c: Coincident(g2,g1)
    c: Diameter(g3) = 21.4
    c: Coincident(g3,g1)
    c: DistanceX(g0,g1) = 23.5
    c: PointOnObject(g1,g0)
    c: Coincident(g0,g-4)
FEATURE [PartDesign::Chamfer] Chamfer016
  Angle = 45
  Base = -> SubtractiveLoft001 [Edge118,Edge117,Edge119,Edge120,Edge109]
  BaseFeature = -> SubtractiveLoft001
  ChamferType = 0
  FlipDirection = false
  Refine = true
  Size = 1.5
  Size2 = 1
  SupportTransform = false
  Suppressed = false
  UseAllEdges = false
FEATURE [PartDesign::Chamfer] Chamfer017
  Angle = 45
  Base = -> Chamfer016 [Edge15]
  BaseFeature = -> Chamfer016
  ChamferType = 0
  FlipDirection = false
  Refine = true
  Size = 1.6
  Size2 = 1
  SupportTransform = false
  Suppressed = false
  UseAllEdges = false
FEATURE [PartDesign::Chamfer] Chamfer018
  Angle = 45
  Base = -> Chamfer017 [Edge10]
  BaseFeature = -> Chamfer017
  ChamferType = 0
  FlipDirection = false
  Refine = true
  Size = 3.5
  Size2 = 1
  SupportTransform = false
  Suppressed = false
  UseAllEdges = false
FEATURE [PartDesign::Chamfer] Chamfer019
  Angle = 45
  Base = -> Chamfer018 [Edge94]
  BaseFeature = -> Chamfer018
  ChamferType = 0
  FlipDirection = false
  Refine = true
  Size = 1.9
  Size2 = 1
  SupportTransform = false
  Suppressed = false
  UseAllEdges = false
FEATURE [PartDesign::Fillet] Fillet009
  Base = -> Chamfer019 [Edge83]
  BaseFeature = -> Chamfer019
  Radius = 1.1
  Refine = true
  SupportTransform = false
  Suppressed = false
  UseAllEdges = false
FEATURE [PartDesign::Fillet] Fillet010
  Base = -> Fillet009 [Edge77]
  BaseFeature = -> Fillet009
  Radius = 1.9
  Refine = true
  SupportTransform = false
  Suppressed = false
  UseAllEdges = false
FEATURE [PartDesign::Pocket] Pocket005
  BaseFeature = -> Fillet010
  Direction = (0,-1,2e-16)
  Length = 0.8
  Length2 = 5
  Profile = -> Sketch112
  ReferenceAxis = -> Sketch112 [N_Axis]
  Refine = true
  Suppressed = false
  Type = 0
FEATURE [Part::Part2DObjectPython] ShapeString001  # Draft 2D object (typed FeaturePython)
  FontFile = <path>
  Fuse = false
  Justification = 6
  JustificationReference = 0
  KeepLeftMargin = false
  MakeFace = true
  ObliqueAngle = 0
  Placement = pos=(-183.5,3.6,-57.5) rot=(0,0.707107,0.707107;3.14159rad)
  ScaleToSize = true
  Size = 10
  String = AS
  Tracking = 0
FEATURE [PartDesign::Pocket] Pocket013
  BaseFeature = -> Pocket005
  Direction = (-1e-16,-1,2e-16)
  Length = 1
  Length2 = 5
  Profile = -> ShapeString001
  ReferenceAxis = -> ShapeString001 [N_Axis]
  Refine = true
  Suppressed = false
  Type = 0
FEATURE [PartDesign::Pad] Pad020
  Direction = (0,-1,2e-16)
  Length = 25.2
  Length2 = 10
  Midplane = true
  Placement = pos=(0,0,0) rot=(1,0,0;1.5708rad)
  Profile = -> Sketch021
  ReferenceAxis = -> Sketch021 [N_Axis]
  Refine = true
  Suppressed = false
  Type = 0
FEATURE [PartDesign::Body] Body001  label="perno fermo rumble e driver solenoide"
  AllowCompound = false
  Group = -> [Sketch021,Pad020]
  Origin = -> Origin001
  Tip = -> Pad020
FEATURE [PartDesign::Pad] Pad021
  Direction = (0,-1,2e-16)
  Length = 16.8
  Length2 = 10
  Midplane = true
  Placement = pos=(0,0,0) rot=(1,0,0;1.5708rad)
  Profile = -> Sketch061
  ReferenceAxis = -> Sketch061 [N_Axis]
  Refine = true
  Suppressed = false
  Type = 0
FEATURE [PartDesign::Pocket] Pocket014
  BaseFeature = -> Pad021
  Direction = (0,1,-2e-16)
  Length = 12.8
  Length2 = 5
  Midplane = true
  Placement = pos=(0,0,0) rot=(1,0,0;1.5708rad)
  Profile = -> Sketch062
  ReferenceAxis = -> Sketch062 [N_Axis]
  Refine = true
  Suppressed = false
  Type = 0
FEATURE [PartDesign::Pad] Pad022
  BaseFeature = -> Pocket014
  Direction = (0,-1,2e-16)
  Length = 7.6
  Length2 = 10
  Midplane = true
  Placement = pos=(0,0,0) rot=(1,0,0;1.5708rad)
  Profile = -> Sketch063
  ReferenceAxis = -> Sketch063 [N_Axis]
  Refine = true
  Suppressed = false
  Type = 0
FEATURE [PartDesign::Body] Body003  label="blocco switch"
  AllowCompound = false
  Group = -> [Sketch061,Sketch062,Sketch063,Pad021,Pocket014,Pad022]
  Origin = -> Origin003
  Tip = -> Pad022
FEATURE [PartDesign::Pad] Pad024
  Direction = (0,-1,2e-16)
  Length = 17
  Length2 = 10
  Midplane = true
  Placement = pos=(0,0,0) rot=(1,0,0;1.5708rad)
  Profile = -> Sketch045
  ReferenceAxis = -> Sketch045 [N_Axis]
  Refine = true
  Suppressed = false
  Type = 0
FEATURE [PartDesign::Pocket] Pocket015
  BaseFeature = -> Pad024
  Direction = (-1,0,0)
  Length = 8
  Length2 = 5
  Placement = pos=(0,0,0) rot=(1,0,0;1.5708rad)
  Profile = -> Sketch047
  ReferenceAxis = -> Sketch047 [N_Axis]
  Refine = true
  Reversed = true
  Suppressed = false
  Type = 0
FEATURE [PartDesign::Pocket] Pocket016
  BaseFeature = -> Pocket015
  Direction = (-1,0,0)
  Length = 1
  Length2 = 5
  Placement = pos=(0,0,0) rot=(1,0,0;1.5708rad)
  Profile = -> Sketch046
  ReferenceAxis = -> Sketch046 [N_Axis]
  Refine = true
  Reversed = true
  Suppressed = false
  Type = 0
FEATURE [PartDesign::Pocket] Pocket017
  BaseFeature = -> Pocket016
  Direction = (0,1,-2e-16)
  Length = 17
  Length2 = 5
  Midplane = true
  Placement = pos=(0,0,0) rot=(1,0,0;1.5708rad)
  Profile = -> Sketch048
  ReferenceAxis = -> Sketch048 [N_Axis]
  Refine = true
  Suppressed = false
  Type = 0
FEATURE [PartDesign::Pad] Pad025
  BaseFeature = -> Pocket017
  Direction = (0,-1,2e-16)
  Length = 17
  Length2 = 10
  Midplane = true
  Placement = pos=(0,0,0) rot=(1,0,0;1.5708rad)
  Profile = -> Sketch049
  ReferenceAxis = -> Sketch049 [N_Axis]
  Refine = true
  Suppressed = false
  Type = 0
FEATURE [PartDesign::Pad] Pad026
  BaseFeature = -> Pad025
  Direction = (0,-1,2e-16)
  Length = 17
  Length2 = 10
  Midplane = true
  Placement = pos=(0,0,0) rot=(1,0,0;1.5708rad)
  Profile = -> Sketch066
  ReferenceAxis = -> Sketch066 [N_Axis]
  Refine = true
  Suppressed = false
  Type = 0
FEATURE [PartDesign::Pad] Pad027
  BaseFeature = -> Pad026
  Direction = (0,-1,2e-16)
  Length = 5
  Length2 = 10
  Midplane = true
  Placement = pos=(0,0,0) rot=(1,0,0;1.5708rad)
  Profile = -> Sketch064
  ReferenceAxis = -> Sketch064 [N_Axis]
  Refine = true
  Suppressed = false
  Type = 0
FEATURE [PartDesign::Pad] Pad028
  BaseFeature = -> Pad027
  Direction = (1,0,0)
  Length = 1
  Length2 = 10
  Placement = pos=(0,0,0) rot=(1,0,0;1.5708rad)
  Profile = -> Sketch068
  ReferenceAxis = -> Sketch068 [N_Axis]
  Refine = true
  Reversed = true
  Suppressed = false
  Type = 0
FEATURE [PartDesign::Chamfer] Chamfer020
  Angle = 45
  Base = -> Pad028 [Edge73,Edge75,Edge78,Edge77]
  BaseFeature = -> Pad028
  ChamferType = 0
  FlipDirection = false
  Placement = pos=(0,0,0) rot=(1,0,0;1.5708rad)
  Refine = true
  Size = 0.5
  Size2 = 1
  SupportTransform = false
  Suppressed = false
  UseAllEdges = false
FEATURE [PartDesign::Body] Body002  label="supporto per neopixel"
  AllowCompound = false
  Group = -> [Sketch045,Sketch047,Sketch046,Sketch048,Sketch049,Sketch066,Sketch064,Sketch068,Pad024,Pocket015,Pocket016,Pocket017,Pad025,Pad026,Pad027,Pad028,Chamfer020]
  Origin = -> Origin002
  Tip = -> Chamfer020
FEATURE [Sketcher::SketchObject] Sketch134  label="perno fermo rumble002"
  ArcFitTolerance = 1e-06
  AttachmentSupport = -> [XZ_Plane008]
  FullyConstrained = true
  MakeInternals = false
  MapMode = 5
  Placement = pos=(0,0,0) rot=(1,0,0;1.5708rad)
  sketch-geometry (16):
    g0: LineSegment StartX=0 StartY=0.45 StartZ=0 EndX=0 EndY=1.55 EndZ=0
    g1: LineSegment StartX=0.45 StartY=2 StartZ=0 EndX=1.55 EndY=2 EndZ=0
    g2: LineSegment StartX=2 StartY=1.55 StartZ=0 EndX=2 EndY=0.45 EndZ=0
    g3: LineSegment StartX=1.55 StartY=0 StartZ=0 EndX=0.45 EndY=0 EndZ=0
    g4: ArcOfCircle [constr] CenterX=0.45 CenterY=1.55 CenterZ=0 NormalX=0 NormalY=0 NormalZ=1 AngleXU=0 Radius=0.45 StartAngle=1.5708 EndAngle=3.14159
    g5: GeomPoint [constr] X=0 Y=2 Z=0
    g6: LineSegment StartX=0.45 StartY=2 StartZ=0 EndX=0 EndY=1.55 EndZ=0
    g7: ArcOfCircle [constr] CenterX=1.55 CenterY=1.55 CenterZ=0 NormalX=0 NormalY=0 NormalZ=1 AngleXU=0 Radius=0.45 StartAngle=0 EndAngle=1.5708
    g8: GeomPoint [constr] X=2 Y=2 Z=0
    g9: LineSegment StartX=2 StartY=1.55 StartZ=0 EndX=1.55 EndY=2 EndZ=0
    g10: ArcOfCircle [constr] CenterX=1.55 CenterY=0.45 CenterZ=0 NormalX=0 NormalY=0 NormalZ=1 AngleXU=0 Radius=0.45 StartAngle=4.71239 EndAngle=6.28319
    g11: GeomPoint [constr] X=2 Y=0 Z=0
    g12: LineSegment StartX=1.55 StartY=0 StartZ=0 EndX=2 EndY=0.45 EndZ=0
    g13: ArcOfCircle [constr] CenterX=0.45 CenterY=0.45 CenterZ=0 NormalX=0 NormalY=0 NormalZ=1 AngleXU=0 Radius=0.45 StartAngle=3.14159 EndAngle=4.71239
    g14: GeomPoint [constr] X=0 Y=0 Z=0
    g15: LineSegment StartX=0 StartY=0.45 StartZ=0 EndX=0.45 EndY=0 EndZ=0
  constraints (35):
    c: Coincident(g14,g-1)
    c: PointOnObject(g5,g-2)
    c: Horizontal(g1)
    c: Vertical(g2)
    c: Horizontal(g3)
    c: DistanceX(g5,g8) = 2
    c: DistanceY(g11,g8) = 2
    c: PointOnObject(g5,g0)
    c: PointOnObject(g5,g1)
    c: Tangent(g0,g4) = 1.5708
    c: Tangent(g1,g4) = 1.5708
    c: Coincident(g6,g0)
    c: Coincident(g6,g1)
    c: PointOnObject(g8,g2)
    c: PointOnObject(g8,g1)
    c: Tangent(g2,g7) = 1.5708
    c: Tangent(g1,g7) = 1.5708
    c: Coincident(g9,g2)
    c: Coincident(g9,g1)
    c: PointOnObject(g11,g2)
    c: PointOnObject(g11,g3)
    c: Tangent(g2,g10) = 1.5708
    c: Tangent(g3,g10) = 1.5708
    c: Coincident(g12,g2)
    c: Coincident(g12,g3)
    c: PointOnObject(g14,g0)
    c: PointOnObject(g14,g3)
    c: Tangent(g0,g13) = 1.5708
    c: Tangent(g3,g13) = 1.5708
    c: Coincident(g15,g0)
    c: Coincident(g15,g3)
    c: Equal(g6,g9)
    c: Equal(g9,g12)
    c: Equal(g12,g15)
    c: DistanceX(g14,g3) = 0.45
FEATURE [PartDesign::Pad] Pad029
  Direction = (0,-1,2e-16)
  Length = 17
  Length2 = 10
  Midplane = true
  Placement = pos=(0,0,0) rot=(1,0,0;1.5708rad)
  Profile = -> Sketch134
  ReferenceAxis = -> Sketch134 [N_Axis]
  Refine = true
  Suppressed = false
  Type = 0
FEATURE [PartDesign::Body] Body008  label="perno fermo neopixel"
  AllowCompound = false
  Group = -> [Sketch134,Pad029]
  Origin = -> Origin008
  Tip = -> Pad029
FEATURE [Sketcher::SketchObject] Sketch135  label="perno fermo rumble003"
  ArcFitTolerance = 1e-06
  AttachmentSupport = -> [XZ_Plane009]
  FullyConstrained = true
  MakeInternals = false
  MapMode = 5
  Placement = pos=(0,0,0) rot=(1,0,0;1.5708rad)
  sketch-geometry (16):
    g0: LineSegment StartX=4.69e-14 StartY=0.8 StartZ=0 EndX=-3.04e-14 EndY=3.1 EndZ=0
    g1: LineSegment StartX=0.8 StartY=3.9 StartZ=0 EndX=3.1 EndY=3.9 EndZ=0
    g2: LineSegment StartX=3.9 StartY=3.1 StartZ=0 EndX=3.9 EndY=0.8 EndZ=0
    g3: LineSegment StartX=3.1 StartY=0 StartZ=0 EndX=0.8 EndY=0 EndZ=0
    g4: ArcOfCircle [constr] CenterX=0.8 CenterY=3.1 CenterZ=0 NormalX=0 NormalY=0 NormalZ=1 AngleXU=0 Radius=0.8 StartAngle=1.5708 EndAngle=3.14159
    g5: GeomPoint [constr] X=0 Y=3.9 Z=0
    g6: LineSegment StartX=0.8 StartY=3.9 StartZ=0 EndX=-3.04e-14 EndY=3.1 EndZ=0
    g7: ArcOfCircle [constr] CenterX=3.1 CenterY=3.1 CenterZ=0 NormalX=0 NormalY=0 NormalZ=1 AngleXU=0 Radius=0.8 StartAngle=-2.4e-14 EndAngle=1.5708
    g8: GeomPoint [constr] X=3.9 Y=3.9 Z=0
    g9: LineSegment StartX=3.9 StartY=3.1 StartZ=0 EndX=3.1 EndY=3.9 EndZ=0
    g10: ArcOfCircle [constr] CenterX=3.1 CenterY=0.8 CenterZ=0 NormalX=0 NormalY=0 NormalZ=1 AngleXU=0 Radius=0.8 StartAngle=4.71239 EndAngle=6.28319
    g11: GeomPoint [constr] X=3.9 Y=0 Z=0
    g12: LineSegment StartX=3.1 StartY=0 StartZ=0 EndX=3.9 EndY=0.8 EndZ=0
    g13: ArcOfCircle [constr] CenterX=0.8 CenterY=0.8 CenterZ=0 NormalX=0 NormalY=0 NormalZ=1 AngleXU=0 Radius=0.8 StartAngle=3.14159 EndAngle=4.71239
    g14: GeomPoint [constr] X=0 Y=0 Z=0
    g15: LineSegment StartX=4.69e-14 StartY=0.8 StartZ=0 EndX=0.8 EndY=0 EndZ=0
  constraints (35):
    c: Coincident(g14,g-1)
    c: PointOnObject(g5,g-2)
    c: Horizontal(g1)
    c: Vertical(g2)
    c: Horizontal(g3)
    c: DistanceX(g5,g8) = 3.9
    c: DistanceY(g11,g8) = 3.9
    c: PointOnObject(g5,g0)
    c: PointOnObject(g5,g1)
    c: Tangent(g0,g4) = 1.5708
    c: Tangent(g1,g4) = 1.5708
    c: Coincident(g6,g0)
    c: Coincident(g6,g1)
    c: PointOnObject(g8,g2)
    c: PointOnObject(g8,g1)
    c: Tangent(g2,g7) = 1.5708
    c: Tangent(g1,g7) = 1.5708
    c: Coincident(g9,g2)
    c: Coincident(g9,g1)
    c: PointOnObject(g11,g2)
    c: PointOnObject(g11,g3)
    c: Tangent(g2,g10) = 1.5708
    c: Tangent(g3,g10) = 1.5708
    c: Coincident(g12,g2)
    c: Coincident(g12,g3)
    c: PointOnObject(g14,g0)
    c: PointOnObject(g14,g3)
    c: Tangent(g0,g13) = 1.5708
    c: Tangent(g3,g13) = 1.5708
    c: Coincident(g15,g0)
    c: Coincident(g15,g3)
    c: Equal(g6,g9)
    c: Equal(g9,g12)
    c: Equal(g12,g15)
    c: DistanceX(g14,g3) = 0.8
FEATURE [PartDesign::Pad] Pad030
  Direction = (0,-1,2e-16)
  Length = 25.2
  Length2 = 10
  Midplane = true
  Placement = pos=(0,0,0) rot=(1,0,0;1.5708rad)
  Profile = -> Sketch135
  ReferenceAxis = -> Sketch135 [N_Axis]
  Refine = true
  Suppressed = false
  Type = 0
FEATURE [PartDesign::Body] Body009  label="perno fermo switch - caricabatterie - grilletto"
  AllowCompound = false
  Group = -> [Sketch135,Pad030]
  Origin = -> Origin009
  Tip = -> Pad030
FEATURE [Sketcher::SketchObject] Sketch136  label="scavo_rele"
  ArcFitTolerance = 1e-06
  AttachmentSupport = -> [XZ_Plane]
  ExternalGeometry = -> [Sketch]
  FullyConstrained = true
  MakeInternals = false
  MapMode = 5
  Placement = pos=(0,0,0) rot=(1,0,0;1.5708rad)
  sketch-geometry (7):
    g0: LineSegment [constr] StartX=-172.456 StartY=-60.9321 StartZ=0 EndX=-176.597 EndY=-73.6763 EndZ=0
    g1: LineSegment [constr] StartX=-172.456 StartY=-60.9321 StartZ=0 EndX=-170.364 EndY=-61.612 EndZ=0
    g2: LineSegment [constr] StartX=-172.456 StartY=-60.9321 StartZ=0 EndX=-176.07 EndY=-59.7579 EndZ=0
    g3: LineSegment StartX=-176.07 StartY=-59.7579 StartZ=0 EndX=-170.364 EndY=-61.612 EndZ=0
    g4: LineSegment StartX=-176.07 StartY=-59.7579 StartZ=0 EndX=-180.211 EndY=-72.502 EndZ=0
    g5: LineSegment StartX=-170.364 StartY=-61.612 StartZ=0 EndX=-174.505 EndY=-74.3561 EndZ=0
    g6: LineSegment StartX=-180.211 StartY=-72.502 StartZ=0 EndX=-174.505 EndY=-74.3561 EndZ=0
  constraints (19):
    c: Tangent(g0,g-3)
    c: Distance(g0,g-3) = 87.2
    c: Distance(g0,g0) = 13.4
    c: Coincident(g1,g0)
    c: Coincident(g2,g0)
    c: Distance(g2) = 3.8
    c: Distance(g1) = 2.2
    c: Perpendicular(g0,g1)
    c: Perpendicular(g0,g2)
    c: Coincident(g3,g2)
    c: Coincident(g3,g1)
    c: Equal(g4,g0)
    c: Equal(g5,g0)
    c: Parallel(g4,g0)
    c: Parallel(g5,g0)
    c: Coincident(g4,g2)
    c: Coincident(g5,g1)
    c: Coincident(g6,g4)
    c: Coincident(g6,g5)
FEATURE [Part::Extrusion] Extrude076  label="Extrude076 - scavo_rele"
  Base = -> Sketch136
  Dir = (0,-1,2e-16)
  DirMode = 2
  FaceMakerClass = Part::FaceMakerBullseye
  FaceMakerMode = 3
  LengthFwd = 18.2
  LengthRev = 0
  Solid = true
  Symmetric = true
FEATURE [Sketcher::SketchObject] Sketch137  label="scavo_nuovo_driver"
  ArcFitTolerance = 1e-06
  AttachmentSupport = -> [XZ_Plane]
  ExternalGeometry = -> [Sketch]
  FullyConstrained = true
  MakeInternals = false
  MapMode = 5
  Placement = pos=(0,0,0) rot=(1,0,0;1.5708rad)
  sketch-geometry (7):
    g0: LineSegment [constr] StartX=-160.034 StartY=-22.6997 StartZ=0 EndX=-164.854 EndY=-37.5361 EndZ=0
    g1: LineSegment [constr] StartX=-160.034 StartY=-22.6997 StartZ=0 EndX=-156.99 EndY=-23.6885 EndZ=0
    g2: LineSegment [constr] StartX=-160.034 StartY=-22.6997 StartZ=0 EndX=-163.648 EndY=-21.5254 EndZ=0
    g3: LineSegment StartX=-163.648 StartY=-21.5254 StartZ=0 EndX=-156.99 EndY=-23.6885 EndZ=0
    g4: LineSegment StartX=-163.648 StartY=-21.5254 StartZ=0 EndX=-168.468 EndY=-36.3619 EndZ=0
    g5: LineSegment StartX=-156.99 StartY=-23.6885 StartZ=0 EndX=-161.811 EndY=-38.525 EndZ=0
    g6: LineSegment StartX=-168.468 StartY=-36.3619 StartZ=0 EndX=-161.811 EndY=-38.525 EndZ=0
  constraints (19):
    c: Distance(g0,g-3) = 47
    c: Distance(g0) = 15.6
    c: Tangent(g0,g-3)
    c: Coincident(g1,g0)
    c: Coincident(g2,g0)
    c: Distance(g1) = 3.2
    c: Distance(g2) = 3.8
    c: Perpendicular(g0,g1)
    c: Perpendicular(g0,g2)
    c: Coincident(g3,g2)
    c: Coincident(g3,g1)
    c: Equal(g4,g0)
    c: Equal(g5,g0)
    c: Parallel(g4,g0)
    c: Parallel(g5,g0)
    c: Coincident(g4,g2)
    c: Coincident(g5,g1)
    c: Coincident(g6,g4)
    c: Coincident(g6,g5)
FEATURE [Part::Extrusion] Extrude077  label="Extrude077 - scavo_nuovo_driver"
  Base = -> Sketch137
  Dir = (0,-1,2e-16)
  DirMode = 2
  FaceMakerClass = Part::FaceMakerBullseye
  FaceMakerMode = 3
  LengthFwd = 20.8
  LengthRev = 0
  Solid = true
  Symmetric = true
FEATURE [Sketcher::SketchObject] Sketch138  label="scavo_nuovo_driver_alto"
  ArcFitTolerance = 1e-06
  AttachmentSupport = -> [XZ_Plane]
  ExternalGeometry = -> [Sketch]
  FullyConstrained = true
  MakeInternals = false
  MapMode = 5
  Placement = pos=(0,0,0) rot=(1,0,0;1.5708rad)
  sketch-geometry (7):
    g0: LineSegment [constr] StartX=-188.796 StartY=17.7274 StartZ=0 EndX=-187.75 EndY=4.97025 EndZ=0
    g1: LineSegment StartX=-187.75 StartY=4.97025 StartZ=0 EndX=-189.743 EndY=4.8067 EndZ=0
    g2: LineSegment StartX=-187.75 StartY=4.97025 StartZ=0 EndX=-182.766 EndY=5.37913 EndZ=0
    g3: LineSegment StartX=-190.79 StartY=17.5638 StartZ=0 EndX=-189.743 EndY=4.8067 EndZ=0
    g4: LineSegment StartX=-183.813 StartY=18.1363 StartZ=0 EndX=-182.766 EndY=5.37913 EndZ=0
    g5: LineSegment StartX=-190.79 StartY=17.5638 StartZ=0 EndX=-188.796 EndY=17.7274 EndZ=0
    g6: LineSegment StartX=-188.796 StartY=17.7274 StartZ=0 EndX=-183.813 EndY=18.1363 EndZ=0
  constraints (20):
    c: Distance(g0) = 12.8
    c: DistanceY(g-3,g0) = 9
    c: PointOnObject(g0,g-4)
    c: PointOnObject(g0,g-4)
    c: Coincident(g1,g0)
    c: Coincident(g2,g0)
    c: Distance(g1) = 2
    c: Distance(g2) = 5
    c: Perpendicular(g0,g1)
    c: Perpendicular(g0,g2)
    c: Equal(g3,g0)
    c: Parallel(g3,g0)
    c: Coincident(g3,g1)
    c: Equal(g4,g0)
    c: Parallel(g4,g0)
    c: Coincident(g4,g2)
    c: Coincident(g5,g3)
    c: Coincident(g5,g0)
    c: Coincident(g6,g0)
    c: Coincident(g6,g4)
FEATURE [Part::Extrusion] Extrude078  label="Extrude078 - scavo_nuovo_driver_alto"
  Base = -> Sketch138
  Dir = (0,-1,2e-16)
  DirMode = 2
  FaceMakerClass = Part::FaceMakerBullseye
  FaceMakerMode = 3
  LengthFwd = 16.6
  LengthRev = 0
  Solid = true
  Symmetric = true
FEATURE [Sketcher::SketchObject] Sketch139  label="fermi_nuovo_driver_alto"
  ArcFitTolerance = 1e-06
  AttachmentSupport = -> [XZ_Plane]
  ExternalGeometry = -> [Sketch138,Sketch]
  FullyConstrained = true
  MakeInternals = false
  MapMode = 5
  Placement = pos=(0,0,0) rot=(1,0,0;1.5708rad)
  sketch-geometry (17):
    g0: LineSegment [constr] StartX=-188.314 StartY=16.4295 StartZ=0 EndX=-187.885 EndY=13.7638 EndZ=0
    g1: LineSegment [constr] StartX=-187.885 StartY=13.7638 StartZ=0 EndX=-187.456 EndY=11.0981 EndZ=0
    g2: LineSegment StartX=-187.885 StartY=13.7638 StartZ=0 EndX=-187.71 EndY=12.6778 EndZ=0
    g3: LineSegment StartX=-187.885 StartY=13.7638 StartZ=0 EndX=-188.06 EndY=14.8499 EndZ=0
    g4: LineSegment StartX=-187.71 StartY=12.6778 StartZ=0 EndX=-185.538 EndY=13.0274 EndZ=0
    g5: LineSegment StartX=-188.06 StartY=14.8499 StartZ=0 EndX=-185.888 EndY=15.1994 EndZ=0
    g6: LineSegment StartX=-185.888 StartY=15.1994 StartZ=0 EndX=-185.538 EndY=13.0274 EndZ=0
    g7: LineSegment StartX=-187.456 StartY=11.0981 StartZ=0 EndX=-189.035 EndY=10.8439 EndZ=0
    g8: LineSegment StartX=-188.314 StartY=16.4295 StartZ=0 EndX=-189.893 EndY=16.1753 EndZ=0
    g9: LineSegment StartX=-189.893 StartY=16.1753 StartZ=0 EndX=-189.035 EndY=10.8439 EndZ=0
    g10: LineSegment StartX=-187.456 StartY=11.0981 StartZ=0 EndX=-185.284 EndY=11.4477 EndZ=0
    g11: LineSegment StartX=-188.314 StartY=16.4295 StartZ=0 EndX=-186.142 EndY=16.7791 EndZ=0
    g12: LineSegment StartX=-184.308 StartY=15.4537 StartZ=0 EndX=-183.958 EndY=13.2816 EndZ=0
    g13: ArcOfCircle CenterX=-185.888 CenterY=15.1994 CenterZ=0 NormalX=0 NormalY=0 NormalZ=1 AngleXU=0 Radius=1.6 StartAngle=0.15957 EndAngle=1.73037
    g14: GeomPoint [constr] X=-184.562 Y=17.0333 Z=0
    g15: ArcOfCircle CenterX=-185.538 CenterY=13.0274 CenterZ=0 NormalX=0 NormalY=0 NormalZ=1 AngleXU=0 Radius=1.6 StartAngle=4.87196 EndAngle=6.44276
    g16: GeomPoint [constr] X=-183.704 Y=11.7019 Z=0
  constraints (43):
    c: Tangent(g1,g0) = -1.5708
    c: Distance(g0) = 2.7
    c: Equal(g1,g0)
    c: Tangent(g1,g-5)
    c: Coincident(g2,g0)
    c: Coincident(g3,g0)
    c: Distance(g2) = 1.1
    c: Equal(g3,g2)
    c: PointOnObject(g3,g2)
    c: Coincident(g4,g2)
    c: Coincident(g5,g3)
    c: Distance(g4) = 2.2
    c: Equal(g4,g5)
    c: Perpendicular(g1,g4)
    c: Perpendicular(g0,g5)
    c: Coincident(g6,g5)
    c: Coincident(g6,g4)
    c: Coincident(g7,g1)
    c: Coincident(g8,g0)
    c: Distance(g7) = 1.6
    c: Equal(g7,g8)
    c: Perpendicular(g1,g7)
    c: Perpendicular(g8,g0)
    c: Coincident(g9,g8)
    c: Coincident(g9,g7)
    c: Coincident(g10,g1)
    c: Coincident(g11,g0)
    c: Distance(g10,g16) = 3.8
    c: Perpendicular(g1,g10)
    c: Perpendicular(g1,g11)
    c: DistanceY(g0,g-4) = 3.8
    c: PointOnObject(g14,g12)
    c: PointOnObject(g14,g11)
    c: Tangent(g12,g13) = 1.5708
    c: Tangent(g11,g13) = 1.5708
    c: PointOnObject(g16,g12)
    c: PointOnObject(g16,g10)
    c: Tangent(g12,g15) = 1.5708
    c: Tangent(g10,g15) = -1.5708
    c: Equal(g13,g15)
    c: Coincident(g13,g5)
    c: Parallel(g2,g0)
    c: PointOnObject(g0,g-5)
FEATURE [Part::Extrusion] Extrude079  label="Extrude079 - fermi_nuovo_driver_alto"
  Base = -> Sketch139
  Dir = (0,-1,2e-16)
  DirMode = 2
  FaceMakerClass = Part::FaceMakerBullseye
  FaceMakerMode = 3
  LengthFwd = 25.2
  LengthRev = 0
  Solid = true
  Symmetric = true
FEATURE [Sketcher::SketchObject] Sketch140  label="scavo_diodo_nuovo_driver_alto"
  ArcFitTolerance = 1e-06
  AttachmentSupport = -> [XZ_Plane]
  ExternalGeometry = -> [Sketch138]
  FullyConstrained = true
  MakeInternals = false
  MapMode = 5
  Placement = pos=(0,0,0) rot=(1,0,0;1.5708rad)
  sketch-geometry (4):
    g0: LineSegment StartX=-190.79 StartY=17.5638 StartZ=0 EndX=-189.743 EndY=4.8067 EndZ=0
    g1: LineSegment StartX=-193.78 StartY=17.3185 StartZ=0 EndX=-192.733 EndY=4.56137 EndZ=0
    g2: LineSegment StartX=-190.79 StartY=17.5638 StartZ=0 EndX=-193.78 EndY=17.3185 EndZ=0
    g3: LineSegment StartX=-192.733 StartY=4.56137 StartZ=0 EndX=-189.743 EndY=4.8067 EndZ=0
  constraints (11):
    c: Equal(g0,g-3)
    c: Parallel(g0,g-3)
    c: Equal(g1,g-3)
    c: Parallel(g1,g-3)
    c: Coincident(g2,g0)
    c: Distance(g2) = 3
    c: Perpendicular(g0,g2)
    c: Coincident(g1,g2)
    c: Coincident(g3,g1)
    c: Coincident(g3,g0)
    c: Coincident(g0,g-3)
FEATURE [Part::Extrusion] Extrude080  label="Extrude080 - scavo_diodo_nuovo_driver_alto"
  Base = -> Sketch140
  Dir = (0,-1,2e-16)
  DirMode = 2
  FaceMakerClass = Part::FaceMakerBullseye
  FaceMakerMode = 3
  LengthFwd = 4
  LengthRev = 0
  Placement = pos=(0,7.8,0) rot=(0,0,1;0rad)
  Solid = true
  Symmetric = false
FEATURE [Part::MultiFuse] Fusion001
  Refine = true
  Shapes = -> [Cut043,Extrude079]
FEATURE [Part::Cut] Cut044
  Base = -> Fusion001
  Refine = true
  Tool = -> Extrude078
FEATURE [Part::Cut] Cut045
  Base = -> Cut044
  Refine = true
  Tool = -> Extrude080
FEATURE [Sketcher::SketchObject] Sketch141  label="fermi_nuovo_driver"
  ArcFitTolerance = 1e-06
  AttachmentSupport = -> [XZ_Plane]
  ExternalGeometry = -> [Sketch,Sketch137]
  FullyConstrained = true
  MakeInternals = false
  MapMode = 5
  Placement = pos=(0,0,0) rot=(1,0,0;1.5708rad)
  sketch-geometry (17):
    g0: LineSegment [constr] StartX=-156.99 StartY=-23.6885 StartZ=0 EndX=-160.034 EndY=-22.6997 EndZ=0
    g1: LineSegment [constr] StartX=-160.034 StartY=-22.6997 StartZ=0 EndX=-162.815 EndY=-31.2592 EndZ=0
    g2: LineSegment [constr] StartX=-162.815 StartY=-31.2592 StartZ=0 EndX=-164.484 EndY=-36.3949 EndZ=0
    g3: LineSegment StartX=-164.484 StartY=-36.3949 StartZ=0 EndX=-166.576 EndY=-35.715 EndZ=0
    g4: LineSegment StartX=-167.603 StartY=-33.6989 StartZ=0 EndX=-166.923 EndY=-31.6066 EndZ=0
    g5: LineSegment StartX=-164.907 StartY=-30.5793 StartZ=0 EndX=-161.293 EndY=-31.7536 EndZ=0
    g6: LineSegment StartX=-161.293 StartY=-31.7536 StartZ=0 EndX=-162.962 EndY=-36.8893 EndZ=0
    g7: LineSegment StartX=-164.484 StartY=-36.3949 StartZ=0 EndX=-162.962 EndY=-36.8893 EndZ=0
    g8: LineSegment StartX=-165.402 StartY=-32.101 StartZ=0 EndX=-166.082 EndY=-34.1933 EndZ=0
    g9: LineSegment StartX=-166.082 StartY=-34.1933 StartZ=0 EndX=-163.989 EndY=-34.8732 EndZ=0
    g10: LineSegment StartX=-163.989 StartY=-34.8732 StartZ=0 EndX=-163.309 EndY=-32.7809 EndZ=0
    g11: LineSegment StartX=-163.309 StartY=-32.7809 StartZ=0 EndX=-165.402 EndY=-32.101 EndZ=0
    g12: ArcOfCircle CenterX=-165.402 CenterY=-32.101 CenterZ=0 NormalX=0 NormalY=0 NormalZ=1 AngleXU=0 Radius=1.6 StartAngle=1.25664 EndAngle=2.82743
    g13: GeomPoint [constr] X=-166.429 Y=-30.0849 Z=0
    g14: ArcOfCircle CenterX=-166.082 CenterY=-34.1933 CenterZ=0 NormalX=0 NormalY=0 NormalZ=1 AngleXU=0 Radius=1.6 StartAngle=2.82743 EndAngle=4.39823
    g15: GeomPoint [constr] X=-168.098 Y=-35.2206 Z=0
    g16: LineSegment [constr] StartX=-160.034 StartY=-22.6997 StartZ=0 EndX=-164.854 EndY=-37.5361 EndZ=0
  constraints (44):
    c: Coincident(g0,g-4)
    c: PointOnObject(g0,g-3)
    c: Parallel(g0,g-4)
    c: Coincident(g1,g0)
    c: Parallel(g1,g-3)
    c: Coincident(g2,g1)
    c: Distance(g2) = 5.4
    c: Coincident(g3,g2)
    c: Parallel(g2,g-3)
    c: Distance(g15,g13) = 5.4
    c: Perpendicular(g3,g2)
    c: Parallel(g4,g2)
    c: Distance(g5,g13) = 5.4
    c: Distance(g3,g15) = 3.8
    c: Perpendicular(g4,g5)
    c: Coincident(g6,g5)
    c: Distance(g6) = 5.4
    c: Parallel(g6,g4)
    c: Coincident(g7,g2)
    c: Coincident(g7,g6)
    c: Coincident(g8,g9)
    c: Coincident(g9,g10)
    c: Coincident(g10,g11)
    c: Coincident(g11,g8)
    c: Distance(g8,g10) = 2.2
    c: Distance(g9,g11) = 2.2
    c: Perpendicular(g11,g8)
    c: Equal(g8,g10)
    c: Equal(g11,g9)
    c: Tangent(g10,g2)
    c: Distance(g10,g1) = 1.6
    c: PointOnObject(g13,g4)
    c: PointOnObject(g13,g5)
    c: Tangent(g4,g12) = 1.5708
    c: Tangent(g5,g12) = 1.5708
    c: PointOnObject(g15,g4)
    c: Tangent(g4,g14) = 1.5708
    c: Tangent(g3,g14) = 1.5708
    c: Equal(g14,g12)
    c: Coincident(g12,g8)
    c: Coincident(g16,g0)
    c: PointOnObject(g16,g-5)
    c: Parallel(g16,g-3)
    c: Distance(g16,g2) = 1.2
FEATURE [Part::Extrusion] Extrude081  label="Extrude081 - fermi_nuovo_driver"
  Base = -> Sketch141
  Dir = (0,-1,2e-16)
  DirMode = 2
  FaceMakerClass = Part::FaceMakerBullseye
  FaceMakerMode = 3
  LengthFwd = 25.2
  LengthRev = 0
  Solid = true
  Symmetric = true
FEATURE [Part::MultiFuse] Fusion002
  Refine = true
  Shapes = -> [Cut045,Extrude081]
FEATURE [Part::Cut] Cut046
  Base = -> Fusion002
  Refine = true
  Tool = -> Extrude077
FEATURE [Sketcher::SketchObject] Sketch142  label="fermi_rele"
  ArcFitTolerance = 1e-06
  AttachmentSupport = -> [XZ_Plane]
  ExternalGeometry = -> [Sketch,Sketch136]
  FullyConstrained = true
  MakeInternals = false
  MapMode = 5
  Placement = pos=(0,0,0) rot=(1,0,0;1.5708rad)
  sketch-geometry (15):
    g0: LineSegment StartX=-176.936 StartY=-62.4208 StartZ=0 EndX=-177.615 EndY=-64.5131 EndZ=0
    g1: LineSegment StartX=-174.919 StartY=-61.3936 StartZ=0 EndX=-171.305 EndY=-62.5678 EndZ=0
    g2: LineSegment StartX=-171.305 StartY=-62.5678 StartZ=0 EndX=-172.974 EndY=-67.7035 EndZ=0
    g3: LineSegment StartX=-176.588 StartY=-66.5293 StartZ=0 EndX=-172.974 EndY=-67.7035 EndZ=0
    g4: LineSegment StartX=-175.414 StartY=-62.9152 StartZ=0 EndX=-173.322 EndY=-63.5951 EndZ=0
    g5: LineSegment StartX=-175.414 StartY=-62.9152 StartZ=0 EndX=-176.094 EndY=-65.0076 EndZ=0
    g6: LineSegment StartX=-173.322 StartY=-63.5951 StartZ=0 EndX=-174.001 EndY=-65.6874 EndZ=0
    g7: LineSegment StartX=-176.094 StartY=-65.0076 StartZ=0 EndX=-174.001 EndY=-65.6874 EndZ=0
    g8: LineSegment [constr] StartX=-173.322 StartY=-63.5951 StartZ=0 EndX=-172.827 EndY=-62.0734 EndZ=0
    g9: LineSegment [constr] StartX=-173.322 StartY=-63.5951 StartZ=0 EndX=-171.8 EndY=-64.0895 EndZ=0
    g10: LineSegment [constr] StartX=-170.364 StartY=-61.612 StartZ=0 EndX=-172.456 EndY=-60.9321 EndZ=0
    g11: ArcOfCircle CenterX=-175.414 CenterY=-62.9152 CenterZ=0 NormalX=0 NormalY=0 NormalZ=1 AngleXU=0 Radius=1.6 StartAngle=1.25664 EndAngle=2.82743
    g12: GeomPoint [constr] X=-176.441 Y=-60.8991 Z=0
    g13: ArcOfCircle CenterX=-176.094 CenterY=-65.0076 CenterZ=0 NormalX=0 NormalY=0 NormalZ=1 AngleXU=0 Radius=1.6 StartAngle=2.82743 EndAngle=4.39823
    g14: GeomPoint [constr] X=-178.11 Y=-66.0348 Z=0
  constraints (39):
    c: Distance(g14,g12) = 5.4
    c: Distance(g1,g12) = 5.4
    c: Perpendicular(g1,g0)
    c: Coincident(g2,g1)
    c: Parallel(g2,g0)
    c: Coincident(g3,g2)
    c: Parallel(g2,g-3)
    c: Coincident(g5,g4)
    c: Distance(g5) = 2.2
    c: Distance(g4) = 2.2
    c: Perpendicular(g4,g5)
    c: Coincident(g6,g4)
    c: Equal(g6,g5)
    c: Parallel(g6,g5)
    c: Coincident(g7,g5)
    c: Coincident(g7,g6)
    c: Coincident(g8,g4)
    c: Coincident(g9,g4)
    c: Distance(g8) = 1.6
    c: Distance(g9) = 1.6
    c: Parallel(g8,g6)
    c: Parallel(g9,g4)
    c: PointOnObject(g8,g1)
    c: PointOnObject(g9,g2)
    c: Coincident(g10,g-4)
    c: Parallel(g10,g-4)
    c: PointOnObject(g10,g-3)
    c: Tangent(g6,g-3) = 1.5708
    c: Distance(g4,g10) = 2.8
    c: PointOnObject(g12,g1)
    c: Tangent(g1,g11) = 1.5708
    c: Tangent(g0,g11) = -1.5708
    c: PointOnObject(g14,g3)
    c: PointOnObject(g14,g0)
    c: Tangent(g3,g13) = -1.5708
    c: Tangent(g0,g13) = -1.5708
    c: Equal(g11,g13)
    c: Coincident(g11,g4)
    c: Parallel(g3,g1)
FEATURE [Part::Extrusion] Extrude082  label="Extrude082 - fermi_rele"
  Base = -> Sketch142
  Dir = (0,-1,2e-16)
  DirMode = 2
  FaceMakerClass = Part::FaceMakerBullseye
  FaceMakerMode = 3
  LengthFwd = 25.2
  LengthRev = 0
  Solid = true
  Symmetric = true
FEATURE [Part::MultiFuse] Fusion003
  Refine = true
  Shapes = -> [Cut046,Extrude082]
FEATURE [Part::Cut] Cut047
  Base = -> Fusion003
  Refine = true
  Tool = -> Extrude076
FEATURE [Sketcher::SketchObject] Sketch143  label="foro_passaggio_cavi_led_batteria"
  ArcFitTolerance = 1e-06
  AttachmentSupport = -> [XZ_Plane]
  ExternalGeometry = -> [Sketch,Sketch042,Sketch036]
  FullyConstrained = true
  MakeInternals = false
  MapMode = 5
  Placement = pos=(0,0,0) rot=(1,0,0;1.5708rad)
  sketch-geometry (4):
    g0: LineSegment StartX=-207.775 StartY=-41.3701 StartZ=0 EndX=-213.607 EndY=-53.8767 EndZ=0
    g1: LineSegment StartX=-213.607 StartY=-53.8767 StartZ=0 EndX=-211.843 EndY=-59.5559 EndZ=0
    g2: LineSegment StartX=-207.775 StartY=-41.3701 StartZ=0 EndX=-207.775 EndY=-50.8316 EndZ=0
    g3: LineSegment StartX=-207.775 StartY=-50.8316 StartZ=0 EndX=-211.843 EndY=-59.5559 EndZ=0
  constraints (9):
    c: Coincident(g0,g-3)
    c: PointOnObject(g1,g-6)
    c: Coincident(g1,g0)
    c: Coincident(g2,g0)
    c: Coincident(g2,g-7)
    c: Coincident(g3,g2)
    c: Parallel(g3,g0)
    c: Coincident(g3,g1)
    c: Coincident(g0,g-5)
FEATURE [Part::Extrusion] Extrude083  label="Extrude083 - foro_passaggio_cavi_led_batteria"
  Base = -> Sketch143
  Dir = (0,-1,2e-16)
  DirMode = 2
  FaceMakerClass = Part::FaceMakerBullseye
  FaceMakerMode = 3
  LengthFwd = 6
  LengthRev = 0
  Solid = true
  Symmetric = true
FEATURE [Part::Cut] Cut048
  Base = -> Cut047
  Refine = true
  Tool = -> Extrude083
FEATURE [Sketcher::SketchObject] Sketch144  label="foro_areazione_alimentatore"
  ArcFitTolerance = 1e-06
  AttachmentSupport = -> [XZ_Plane]
  ExternalGeometry = -> [Sketch036]
  FullyConstrained = true
  MakeInternals = false
  MapMode = 5
  Placement = pos=(0,0,0) rot=(1,0,0;1.5708rad)
  sketch-geometry (4):
    g0: LineSegment StartX=-211.843 StartY=-60.3701 StartZ=0 EndX=-207.775 EndY=-60.3701 EndZ=0
    g1: LineSegment StartX=-207.775 StartY=-60.3701 StartZ=0 EndX=-207.775 EndY=-70.3701 EndZ=0
    g2: LineSegment StartX=-211.843 StartY=-60.3701 StartZ=0 EndX=-211.843 EndY=-70.3701 EndZ=0
    g3: LineSegment StartX=-207.775 StartY=-70.3701 StartZ=0 EndX=-211.843 EndY=-70.3701 EndZ=0
  constraints (11):
    c: Horizontal(g0)
    c: Distance(g1) = 10
    c: Coincident(g1,g0)
    c: Tangent(g1,g-3)
    c: PointOnObject(g0,g-4)
    c: Coincident(g2,g0)
    c: PointOnObject(g2,g-4)
    c: Coincident(g3,g1)
    c: Horizontal(g3)
    c: Coincident(g3,g2)
    c: DistanceY(g0,g-3) = 19
FEATURE [Part::Extrusion] Extrude084  label="Extrude084 - foro_areazione_alimentatore"
  Base = -> Sketch144
  Dir = (0,-1,2e-16)
  DirMode = 2
  FaceMakerClass = Part::FaceMakerBullseye
  FaceMakerMode = 3
  LengthFwd = 10
  LengthRev = 0
  Solid = true
  Symmetric = true
FEATURE [Part::Cut] Cut049
  Base = -> Cut048
  Refine = true
  Tool = -> Extrude084
FEATURE [Sketcher::SketchObject] Sketch145  label="foro_per_condesatore"
  ArcFitTolerance = 1e-06
  AttachmentSupport = -> [XZ_Plane]
  ExternalGeometry = -> [Sketch,Sketch139]
  FullyConstrained = true
  MakeInternals = false
  MapMode = 5
  Placement = pos=(0,0,0) rot=(1,0,0;1.5708rad)
  sketch-geometry (1):
    g0: Circle CenterX=-182.345 CenterY=7.02342 CenterZ=0 NormalX=0 NormalY=0 NormalZ=1 AngleXU=0 Radius=5.2
  constraints (3):
    c: Diameter(g0) = 10.4
    c: Tangent(g0,g-3)
    c: Tangent(g0,g-4)
FEATURE [Part::Extrusion] Extrude085  label="Extrude085 - foro_per_condesatore"
  Base = -> Sketch145
  Dir = (0,-1,2e-16)
  DirMode = 2
  FaceMakerClass = Part::FaceMakerBullseye
  FaceMakerMode = 3
  LengthFwd = 25.2
  LengthRev = 0
  Solid = true
  Symmetric = true
FEATURE [Part::Cut] Cut050
  Base = -> Cut049
  Refine = true
  Tool = -> Extrude085
FEATURE [Sketcher::SketchObject] Sketch146  label="scavo_pulsante_6x6_per_led_batteria"
  ArcFitTolerance = 1e-06
  AttachmentSupport = -> [XZ_Plane]
  ExternalGeometry = -> [Sketch016]
  FullyConstrained = true
  MakeInternals = false
  MapMode = 5
  Placement = pos=(0,0,0) rot=(1,0,0;1.5708rad)
  sketch-geometry (5):
    g0: LineSegment StartX=-216.643 StartY=-65.8316 StartZ=0 EndX=-216.643 EndY=-72.8316 EndZ=0
    g1: LineSegment StartX=-216.643 StartY=-72.8316 StartZ=0 EndX=-210.243 EndY=-72.8316 EndZ=0
    g2: LineSegment StartX=-210.243 StartY=-72.8316 StartZ=0 EndX=-210.243 EndY=-65.8316 EndZ=0
    g3: LineSegment StartX=-210.243 StartY=-65.8316 StartZ=0 EndX=-216.643 EndY=-65.8316 EndZ=0
    g4: GeomPoint [constr] X=-213.443 Y=-69.3316 Z=0
  constraints (13):
    c: Coincident(g0,g1)
    c: Coincident(g1,g2)
    c: Coincident(g2,g3)
    c: Coincident(g3,g0)
    c: Vertical(g0)
    c: Vertical(g2)
    c: Horizontal(g1)
    c: Horizontal(g3)
    c: Distance(g0,g2) = 6.4
    c: Distance(g1,g3) = 7
    c: Tangent(g1,g-3)
    c: Symmetric(g0,g2,g4)
    c: Vertical(g-3,g4)
FEATURE [Part::Extrusion] Extrude086  label="Extrude086 - scavo_pulsante_6x6_per_led_batteria"
  Base = -> Sketch146
  Dir = (0,-1,2e-16)
  DirMode = 2
  FaceMakerClass = Part::FaceMakerBullseye
  FaceMakerMode = 3
  LengthFwd = 4
  LengthRev = 0
  Placement = pos=(0,12.6,0) rot=(0,0,1;0rad)
  Solid = true
  Symmetric = false
FEATURE [Sketcher::SketchObject] Sketch147  label="scavo_led_stato_batteria"
  ArcFitTolerance = 1e-06
  AttachmentSupport = -> [XZ_Plane]
  ExternalGeometry = -> [Sketch016]
  FullyConstrained = true
  MakeInternals = false
  MapMode = 5
  Placement = pos=(0,0,0) rot=(1,0,0;1.5708rad)
  sketch-geometry (5):
    g0: LineSegment StartX=-215.843 StartY=-56.2316 StartZ=0 EndX=-215.843 EndY=-65.4316 EndZ=0
    g1: LineSegment StartX=-215.843 StartY=-65.4316 StartZ=0 EndX=-211.043 EndY=-65.4316 EndZ=0
    g2: LineSegment StartX=-211.043 StartY=-65.4316 StartZ=0 EndX=-211.043 EndY=-56.2316 EndZ=0
    g3: LineSegment StartX=-211.043 StartY=-56.2316 StartZ=0 EndX=-215.843 EndY=-56.2316 EndZ=0
    g4: GeomPoint [constr] X=-213.443 Y=-60.8316 Z=0
  constraints (13):
    c: Coincident(g0,g1)
    c: Coincident(g1,g2)
    c: Coincident(g2,g3)
    c: Coincident(g3,g0)
    c: Distance(g0,g2) = 4.8
    c: Distance(g1,g3) = 9.2
    c: Equal(g0,g2)
    c: Equal(g1,g3)
    c: Perpendicular(g3,g0)
    c: DistanceY(g-3,g0) = 11.4
    c: Vertical(g2)
    c: Symmetric(g0,g2,g4)
    c: Vertical(g4,g-3)
FEATURE [Part::Extrusion] Extrude087  label="Extrude087 - scavo_led_stato_batteria"
  Base = -> Sketch147
  Dir = (0,-1,2e-16)
  DirMode = 2
  FaceMakerClass = Part::FaceMakerBullseye
  FaceMakerMode = 3
  LengthFwd = 2.2
  LengthRev = 0
  Placement = pos=(0,12.6,0) rot=(0,0,1;0rad)
  Solid = true
  Symmetric = false
FEATURE [Sketcher::SketchObject] Sketch148
  ArcFitTolerance = 1e-06
  AttachmentSupport = -> [Pad016]
  ExternalGeometry = -> [Pad016]
  FullyConstrained = true
  MakeInternals = false
  MapMode = 5
  Placement = pos=(0,0,-80.4316) rot=(1,0,0;3.14159rad)
  sketch-geometry (8):
    g0: LineSegment StartX=-176.685 StartY=3.6 StartZ=0 EndX=-186.685 EndY=3.6 EndZ=0
    g1: LineSegment StartX=-176.685 StartY=3.6 StartZ=0 EndX=-176.685 EndY=-9e-16 EndZ=0
    g2: LineSegment [constr] StartX=-186.685 StartY=3.6 StartZ=0 EndX=-186.685 EndY=-9e-16 EndZ=0
    g3: ArcOfEllipse CenterX=-186.685 CenterY=-9e-16 CenterZ=0 NormalX=0 NormalY=0 NormalZ=1 MajorRadius=10 MinorRadius=3.6 AngleXU=0 StartAngle=0 EndAngle=1.5708
    g4: LineSegment [constr] StartX=-176.685 StartY=-1e-15 StartZ=0 EndX=-196.685 EndY=-1e-15 EndZ=0
    g5: LineSegment [constr] StartX=-186.685 StartY=3.6 StartZ=0 EndX=-186.685 EndY=-3.6 EndZ=0
    g6: GeomPoint [constr] X=-177.356 Y=-1e-15 Z=0
    g7: GeomPoint [constr] X=-196.015 Y=-1e-15 Z=0
  constraints (13):
    c: Distance(g0) = 10
    c: Coincident(g0,g-5)
    c: PointOnObject(g0,g-3)
    c: Coincident(g1,g0)
    c: Coincident(g1,g-5)
    c: Coincident(g2,g0)
    c: Vertical(g2)
    c: PointOnObject(g2,g-4)
    c: InternalAlignment(g4-g7 -> g3) x4
    c: Coincident(g3,g2)
    c: Coincident(g3,g0)
    c: Coincident(g3,g1)
    c: Horizontal(g4)
FEATURE [PartDesign::SubtractivePipe] SubtractivePipe004
  AuxilleryCurvelinear = true
  AuxillerySpineTangent = false
  BaseFeature = -> Pad016
  Binormal = (0,0,0)
  Mode = 0
  Profile = -> Sketch148
  Refine = true
  Spine = -> Pad016 [Edge253]
  SpineTangent = false
  Suppressed = false
  Transformation = 0
  Transition = 0
FEATURE [Sketcher::SketchObject] Sketch149
  ArcFitTolerance = 1e-06
  AttachmentSupport = -> [Pad016]
  ExternalGeometry = -> [Pad016]
  FullyConstrained = true
  MakeInternals = false
  MapMode = 5
  Placement = pos=(0,0,-80.4316) rot=(1,0,0;3.14159rad)
  sketch-geometry (8):
    g0: LineSegment StartX=-215.932 StartY=3.6 StartZ=0 EndX=-205.932 EndY=3.6 EndZ=0
    g1: LineSegment StartX=-215.932 StartY=3.6 StartZ=0 EndX=-215.932 EndY=-4e-16 EndZ=0
    g2: LineSegment [constr] StartX=-205.932 StartY=3.6 StartZ=0 EndX=-205.932 EndY=-9e-16 EndZ=0
    g3: ArcOfEllipse CenterX=-205.932 CenterY=-1e-15 CenterZ=0 NormalX=0 NormalY=0 NormalZ=1 MajorRadius=10 MinorRadius=3.6 AngleXU=-3.14159 StartAngle=4.71239 EndAngle=6.28319
    g4: LineSegment [constr] StartX=-215.932 StartY=-1e-15 StartZ=0 EndX=-195.932 EndY=-1e-15 EndZ=0
    g5: LineSegment [constr] StartX=-205.932 StartY=-3.6 StartZ=0 EndX=-205.932 EndY=3.6 EndZ=0
    g6: GeomPoint [constr] X=-215.262 Y=-2.1e-15 Z=0
    g7: GeomPoint [constr] X=-196.602 Y=-9e-16 Z=0
  constraints (13):
    c: Distance(g0) = 10
    c: Coincident(g0,g-5)
    c: PointOnObject(g0,g-5)
    c: Coincident(g1,g0)
    c: Coincident(g1,g-4)
    c: Coincident(g2,g0)
    c: Vertical(g2)
    c: PointOnObject(g2,g-3)
    c: InternalAlignment(g4-g7 -> g3) x4
    c: Coincident(g3,g2)
    c: Coincident(g3,g0)
    c: Coincident(g3,g1)
    c: Horizontal(g4)
FEATURE [PartDesign::SubtractivePipe] SubtractivePipe005
  AuxilleryCurvelinear = true
  AuxillerySpineTangent = false
  BaseFeature = -> SubtractivePipe004
  Binormal = (0,0,0)
  Mode = 0
  Profile = -> Sketch149
  Refine = true
  Spine = -> Pad016 [Edge251,Edge256,Edge255]
  SpineTangent = false
  Suppressed = false
  Transformation = 0
  Transition = 0
FEATURE [PartDesign::SubtractiveLoft] SubtractiveLoft002
  BaseFeature = -> SubtractivePipe005
  Closed = false
  Profile = -> Sketch129
  Refine = true
  Ruled = false
  Sections = -> [Sketch130]
  Suppressed = false
FEATURE [PartDesign::SubtractiveLoft] SubtractiveLoft003
  BaseFeature = -> SubtractiveLoft002
  Closed = false
  Profile = -> Clone2D001
  Refine = true
  Ruled = false
  Sections = -> [Sketch131]
  Suppressed = false
FEATURE [PartDesign::Chamfer] Chamfer010
  Angle = 45
  Base = -> SubtractiveLoft003 [Edge203,Edge204,Edge202,Edge201,Edge195]
  BaseFeature = -> SubtractiveLoft003
  ChamferType = 0
  FlipDirection = false
  Refine = true
  Size = 1.5
  Size2 = 1
  SupportTransform = false
  Suppressed = false
  UseAllEdges = false
FEATURE [PartDesign::Chamfer] Chamfer011
  Angle = 45
  Base = -> Chamfer010 [Edge15]
  BaseFeature = -> Chamfer010
  ChamferType = 0
  FlipDirection = false
  Refine = true
  Size = 1.6
  Size2 = 1
  SupportTransform = false
  Suppressed = false
  UseAllEdges = false
FEATURE [PartDesign::Chamfer] Chamfer012
  Angle = 45
  Base = -> Chamfer011 [Edge10]
  BaseFeature = -> Chamfer011
  ChamferType = 0
  FlipDirection = false
  Refine = true
  Size = 3.5
  Size2 = 1
  SupportTransform = false
  Suppressed = false
  UseAllEdges = false
FEATURE [PartDesign::Chamfer] Chamfer013
  Angle = 45
  Base = -> Chamfer012 [Edge94]
  BaseFeature = -> Chamfer012
  ChamferType = 0
  FlipDirection = false
  Refine = true
  Size = 1.9
  Size2 = 1
  SupportTransform = false
  Suppressed = false
  UseAllEdges = false
FEATURE [PartDesign::Fillet] Fillet007
  Base = -> Chamfer013 [Edge83]
  BaseFeature = -> Chamfer013
  Radius = 1.1
  Refine = true
  SupportTransform = false
  Suppressed = false
  UseAllEdges = false
FEATURE [PartDesign::Fillet] Fillet008
  Base = -> Fillet007 [Edge75]
  BaseFeature = -> Fillet007
  Radius = 1.9
  Refine = true
  SupportTransform = false
  Suppressed = false
  UseAllEdges = false
FEATURE [PartDesign::Pocket] Pocket011
  BaseFeature = -> Fillet008
  Direction = (0,1,-2e-16)
  Length = 0.8
  Length2 = 5
  Profile = -> Sketch132
  ReferenceAxis = -> Sketch132 [N_Axis]
  Refine = true
  Suppressed = false
  Type = 0
FEATURE [PartDesign::Pocket] Pocket012
  BaseFeature = -> Pocket011
  Direction = (0,1,0)
  Length = 1
  Length2 = 5
  Profile = -> ShapeString
  ReferenceAxis = -> ShapeString [N_Axis]
  Refine = true
  Suppressed = false
  Type = 0
FEATURE [Sketcher::SketchObject] Sketch150
  ArcFitTolerance = 1e-06
  AttachmentSupport = -> [Pad008]
  ExternalGeometry = -> [Pad008]
  FullyConstrained = true
  MakeInternals = false
  MapMode = 5
  Placement = pos=(0,3.6,0) rot=(0,0.707107,0.707107;3.14159rad)
  sketch-geometry (7):
    g0: LineSegment [constr] StartX=210.343 StartY=-66.0316 StartZ=0 EndX=210.343 EndY=-72.8316 EndZ=0
    g1: LineSegment [constr] StartX=210.343 StartY=-72.8316 StartZ=0 EndX=216.543 EndY=-72.8316 EndZ=0
    g2: LineSegment [constr] StartX=216.543 StartY=-72.8316 StartZ=0 EndX=216.543 EndY=-66.0316 EndZ=0
    g3: LineSegment [constr] StartX=216.543 StartY=-66.0316 StartZ=0 EndX=210.343 EndY=-66.0316 EndZ=0
    g4: LineSegment [constr] StartX=210.343 StartY=-72.8316 StartZ=0 EndX=216.543 EndY=-66.0316 EndZ=0
    g5: LineSegment [constr] StartX=210.343 StartY=-66.0316 StartZ=0 EndX=213.443 EndY=-69.4316 EndZ=0
    g6: Circle CenterX=213.443 CenterY=-69.4316 CenterZ=0 NormalX=0 NormalY=0 NormalZ=1 AngleXU=0 Radius=2
  constraints (18):
    c: Coincident(g0,g1)
    c: Coincident(g1,g2)
    c: Coincident(g2,g3)
    c: Coincident(g3,g0)
    c: Vertical(g0)
    c: Vertical(g2)
    c: Horizontal(g1)
    c: Horizontal(g3)
    c: Distance(g0,g2) = 6.2
    c: Distance(g1,g3) = 6.8
    c: DistanceY(g-3,g1) = 4
    c: Coincident(g4,g0)
    c: Coincident(g4,g2)
    c: Coincident(g5,g0)
    c: Symmetric(g0,g2,g5)
    c: Diameter(g6) = 4
    c: Coincident(g6,g5)
    c: Vertical(g5,g-3)
FEATURE [Sketcher::SketchObject] Sketch151
  ArcFitTolerance = 1e-06
  AttachmentSupport = -> [Pad008]
  ExternalGeometry = -> [Pad008]
  FullyConstrained = true
  MakeInternals = false
  MapMode = 5
  Placement = pos=(0,3.6,0) rot=(0,0.707107,0.707107;3.14159rad)
  sketch-geometry (10):
    g0: LineSegment [constr] StartX=211.143 StartY=-56.2316 StartZ=0 EndX=211.143 EndY=-65.4316 EndZ=0
    g1: LineSegment [constr] StartX=211.143 StartY=-65.4316 StartZ=0 EndX=215.743 EndY=-65.4316 EndZ=0
    g2: LineSegment [constr] StartX=215.743 StartY=-65.4316 StartZ=0 EndX=215.743 EndY=-56.2316 EndZ=0
    g3: LineSegment [constr] StartX=215.743 StartY=-56.2316 StartZ=0 EndX=211.143 EndY=-56.2316 EndZ=0
    g4: LineSegment StartX=212.243 StartY=-63.8316 StartZ=0 EndX=214.643 EndY=-63.8316 EndZ=0
    g5: LineSegment StartX=214.643 StartY=-63.8316 StartZ=0 EndX=214.643 EndY=-57.0316 EndZ=0
    g6: LineSegment StartX=214.643 StartY=-57.0316 StartZ=0 EndX=212.243 EndY=-57.0316 EndZ=0
    g7: LineSegment StartX=212.243 StartY=-57.0316 StartZ=0 EndX=212.243 EndY=-63.8316 EndZ=0
    g8: GeomPoint [constr] X=213.443 Y=-60.4316 Z=0
    g9: GeomPoint [constr] X=213.443 Y=-60.8316 Z=0
  constraints (26):
    c: Coincident(g0,g1)
    c: Coincident(g1,g2)
    c: Coincident(g2,g3)
    c: Coincident(g3,g0)
    c: Vertical(g0)
    c: Vertical(g2)
    c: Horizontal(g1)
    c: Horizontal(g3)
    c: Distance(g0,g2) = 4.6
    c: Distance(g1,g3) = 9.2
    c: DistanceY(g-3,g1) = 11.4
    c: Coincident(g4,g5)
    c: Coincident(g5,g6)
    c: Coincident(g6,g7)
    c: Coincident(g7,g4)
    c: Horizontal(g4)
    c: Horizontal(g6)
    c: Vertical(g5)
    c: Vertical(g7)
    c: Symmetric(g6,g4,g8)
    c: Distance(g5,g7) = 2.4
    c: Distance(g4,g6) = 6.8
    c: Symmetric(g2,g0,g9)
    c: Vertical(g8,g9)
    c: DistanceY(g1,g4) = 1.6
    c: Vertical(g9,g-3)
FEATURE [PartDesign::Pocket] Pocket019
  BaseFeature = -> Pocket013
  Direction = (0,-1,2e-16)
  Length = 3.6
  Length2 = 5
  Profile = -> Sketch151
  ReferenceAxis = -> Sketch151 [N_Axis]
  Refine = true
  Suppressed = false
  Type = 0
FEATURE [PartDesign::Pocket] Pocket018
  BaseFeature = -> Pocket019
  Direction = (0,-1,2e-16)
  Length = 3.6
  Length2 = 5
  Profile = -> Sketch150
  ReferenceAxis = -> Sketch150 [N_Axis]
  Refine = true
  Suppressed = false
  Type = 0
FEATURE [PartDesign::Point] DatumPoint
  AttacherType = Attacher::AttachEnginePoint
  AttachmentSupport = -> [Sketch150]
  MapMode = 36
  Placement = pos=(-213.443,3.6,-69.4316) rot=(0,1,0;3.14159rad)
FEATURE [PartDesign::Plane] DatumPlane002
  AttachmentSupport = -> [DatumPoint]
  Length = 260.281
  MapMode = 1
  Placement = pos=(-213.443,3.6,-69.4316) rot=(0,0,1;0rad)
  ResizeMode = 0
  Width = 71.8377
FEATURE [Sketcher::SketchObject] Sketch152
  ArcFitTolerance = 1e-06
  AttachmentSupport = -> [DatumPlane002]
  ExternalGeometry = -> [Sketch150]
  FullyConstrained = true
  MakeInternals = false
  MapMode = 5
  Placement = pos=(-213.443,3.6,-69.4316) rot=(0,0,1;0rad)
  sketch-geometry (7):
    g0: LineSegment StartX=0 StartY=0 StartZ=0 EndX=-4 EndY=5.1e-15 EndZ=0
    g1: ArcOfEllipse CenterX=0 CenterY=0 CenterZ=0 NormalX=0 NormalY=0 NormalZ=1 MajorRadius=4 MinorRadius=3.6 AngleXU=3.14159 StartAngle=2e-16 EndAngle=1.5708
    g2: LineSegment [constr] StartX=-4 StartY=9e-16 StartZ=0 EndX=4 EndY=-9e-16 EndZ=0
    g3: LineSegment [constr] StartX=0 StartY=-3.6 StartZ=0 EndX=0 EndY=3.6 EndZ=0
    g4: GeomPoint [constr] X=-1.74356 Y=2.5e-15 Z=0
    g5: GeomPoint [constr] X=1.74356 Y=-2e-15 Z=0
    g6: LineSegment StartX=0 StartY=0 StartZ=0 EndX=-5.5e-15 EndY=-3.6 EndZ=0
  constraints (11):
    c: PointOnObject(g1,g-2)
    c: Distance(g0) = 4
    c: PointOnObject(g0,g-1)
    c: InternalAlignment(g2-g5 -> g1) x4
    c: Coincident(g1,g0)
    c: Vertical(g3)
    c: Coincident(g1,g-1)
    c: Distance(g6) = 3.6
    c: Coincident(g6,g1)
    c: Coincident(g1,g6)
    c: Coincident(g0,g1)
FEATURE [PartDesign::Groove] Groove
  Angle = 360
  Angle2 = 60
  Axis = (0,1,0)
  Base = (-213.443,3.6,-69.4316)
  BaseFeature = -> Pocket018
  Profile = -> Sketch152
  ReferenceAxis = -> Sketch152 [V_Axis]
  Refine = true
  Reversed = true
  Suppressed = false
  Type = 0
FEATURE [PartDesign::Body] Body006  label="lato SX"
  AllowCompound = false
  Group = -> [Binder,Pad019,Chamfer015,Pocket002,Sketch133,Sketch091,Pad005,Sketch092,Pocket001,Sketch093,Sketch094,Pad006,Sketch095,Pad007,Sketch096,Pad008,Sketch097,Pad009,Chamfer005,Pocket004,Sketch098,Pad010,Chamfer006,Pocket003,SubtractivePipe,SubtractivePipe001,Sketch099,Sketch106,Sketch107,Sketch108,Clone2D,Sketch109,SubtractiveLoft,SubtractiveLoft001,Sketch110,Sketch111,Sketch112,Chamfer016,Chamfer017,+15 more]
  Origin = -> Origin006
  Tip = -> Groove
FEATURE [Sketcher::SketchObject] Sketch153  label="ripieno_per_sostegno_led_batteria"
  ArcFitTolerance = 1e-06
  AttachmentSupport = -> [XZ_Plane]
  ExternalGeometry = -> [Sketch036]
  FullyConstrained = true
  MakeInternals = false
  MapMode = 5
  Placement = pos=(0,0,0) rot=(1,0,0;1.5708rad)
  sketch-geometry (4):
    g0: LineSegment StartX=-217.343 StartY=-54.5944 StartZ=0 EndX=-217.343 EndY=-63.1944 EndZ=0
    g1: LineSegment StartX=-217.343 StartY=-63.1944 StartZ=0 EndX=-211.843 EndY=-63.1944 EndZ=0
    g2: LineSegment StartX=-211.843 StartY=-63.1944 StartZ=0 EndX=-211.843 EndY=-54.5944 EndZ=0
    g3: LineSegment StartX=-211.843 StartY=-54.5944 StartZ=0 EndX=-217.343 EndY=-54.5944 EndZ=0
  constraints (11):
    c: Coincident(g0,g1)
    c: Coincident(g1,g2)
    c: Coincident(g2,g3)
    c: Coincident(g3,g0)
    c: Vertical(g0)
    c: Horizontal(g1)
    c: Horizontal(g3)
    c: Tangent(g2,g-3)
    c: DistanceY(g2,g-3) = 4.5
    c: DistanceX(g3,g3) = 5.5
    c: DistanceY(g0,g0) = 8.6
FEATURE [PartDesign::Body] Body  label="Struttura pistola"
  AllowCompound = false
  Group = -> [Sketch,Sketch002,Sketch004,DatumPlane,Sketch005,DatumPlane001,CopyCut,Sketch008,Sketch009,Sketch010,Sketch011,Sketch012,Sketch013,Sketch014,Sketch015,Sketch016,Sketch017,Sketch018,Sketch019,Sketch020,Sketch022,Sketch023,Sketch024,Sketch025,Sketch026,Sketch027,Sketch029,Sketch030,Sketch031,Sketch032,Sketch033,Sketch034,Sketch035,Sketch036,Sketch037,Sketch038,Sketch039,Sketch040,Sketch041,Sketch042,+28 more]
  Origin = -> Origin
FEATURE [Part::Extrusion] Extrude088  label="Extrude088 - ripieno_per_sostegno_led_batteria"
  Base = -> Sketch153
  Dir = (0,-1,2e-16)
  DirMode = 2
  FaceMakerClass = Part::FaceMakerBullseye
  FaceMakerMode = 3
  LengthFwd = 4
  LengthRev = 0
  Placement = pos=(0,12.6,0) rot=(0,0,1;0rad)
  Solid = true
  Symmetric = false
FEATURE [Part::MultiFuse] Fusion004
  Refine = true
  Shapes = -> [Cut050,Extrude088]
FEATURE [Part::Cut] Cut051
  Base = -> Fusion004
  Refine = true
  Tool = -> Extrude087
FEATURE [Part::Cut] Cut052
  Base = -> Cut051
  Refine = true
  Tool = -> Extrude086
FEATURE [Sketcher::SketchObject] Sketch154
  ArcFitTolerance = 1e-06
  AttachmentSupport = -> [Pad016]
  ExternalGeometry = -> [Binder001]
  FullyConstrained = true
  MakeInternals = false
  MapMode = 5
  Placement = pos=(0,-3.6,0) rot=(1,0,0;1.5708rad)
  sketch-geometry (25):
    g0: LineSegment StartX=-214.643 StartY=-72.4316 StartZ=0 EndX=-212.243 EndY=-72.4316 EndZ=0
    g1: LineSegment StartX=-212.243 StartY=-72.4316 StartZ=0 EndX=-212.243 EndY=-71.2316 EndZ=0
    g2: LineSegment StartX=-212.243 StartY=-71.2316 StartZ=0 EndX=-214.643 EndY=-71.2316 EndZ=0
    g3: LineSegment StartX=-214.643 StartY=-71.2316 StartZ=0 EndX=-214.643 EndY=-72.4316 EndZ=0
    g4: GeomPoint [constr] X=-213.443 Y=-71.8316 Z=0
    g5: LineSegment StartX=-214.643 StartY=-69.6316 StartZ=0 EndX=-212.243 EndY=-69.6316 EndZ=0
    g6: LineSegment StartX=-212.243 StartY=-69.6316 StartZ=0 EndX=-212.243 EndY=-68.4316 EndZ=0
    g7: LineSegment StartX=-212.243 StartY=-68.4316 StartZ=0 EndX=-214.643 EndY=-68.4316 EndZ=0
    g8: LineSegment StartX=-214.643 StartY=-68.4316 StartZ=0 EndX=-214.643 EndY=-69.6316 EndZ=0
    g9: GeomPoint [constr] X=-213.443 Y=-69.0316 Z=0
    g10: LineSegment StartX=-214.643 StartY=-66.8316 StartZ=0 EndX=-212.243 EndY=-66.8316 EndZ=0
    g11: LineSegment StartX=-212.243 StartY=-66.8316 StartZ=0 EndX=-212.243 EndY=-65.6316 EndZ=0
    g12: LineSegment StartX=-212.243 StartY=-65.6316 StartZ=0 EndX=-214.643 EndY=-65.6316 EndZ=0
    g13: LineSegment StartX=-214.643 StartY=-65.6316 StartZ=0 EndX=-214.643 EndY=-66.8316 EndZ=0
    g14: GeomPoint [constr] X=-213.443 Y=-66.2316 Z=0
    g15: LineSegment StartX=-214.643 StartY=-64.0316 StartZ=0 EndX=-212.243 EndY=-64.0316 EndZ=0
    g16: LineSegment StartX=-212.243 StartY=-64.0316 StartZ=0 EndX=-212.243 EndY=-62.8316 EndZ=0
    g17: LineSegment StartX=-212.243 StartY=-62.8316 StartZ=0 EndX=-214.643 EndY=-62.8316 EndZ=0
    g18: LineSegment StartX=-214.643 StartY=-62.8316 StartZ=0 EndX=-214.643 EndY=-64.0316 EndZ=0
    g19: GeomPoint [constr] X=-213.443 Y=-63.4316 Z=0
    g20: LineSegment StartX=-214.643 StartY=-61.2316 StartZ=0 EndX=-212.243 EndY=-61.2316 EndZ=0
    g21: LineSegment StartX=-212.243 StartY=-61.2316 StartZ=0 EndX=-212.243 EndY=-60.0316 EndZ=0
    g22: LineSegment StartX=-212.243 StartY=-60.0316 StartZ=0 EndX=-214.643 EndY=-60.0316 EndZ=0
    g23: LineSegment StartX=-214.643 StartY=-60.0316 StartZ=0 EndX=-214.643 EndY=-61.2316 EndZ=0
    g24: GeomPoint [constr] X=-213.443 Y=-60.6316 Z=0
  constraints (65):
    c: Coincident(g0,g1)
    c: Coincident(g1,g2)
    c: Coincident(g2,g3)
    c: Coincident(g3,g0)
    c: Horizontal(g0)
    c: Horizontal(g2)
    c: Vertical(g1)
    c: Vertical(g3)
    c: Symmetric(g2,g0,g4)
    c: Distance(g1,g3) = 2.4
    c: Distance(g0,g2) = 1.2
    c: Coincident(g5,g6)
    c: Coincident(g6,g7)
    c: Coincident(g7,g8)
    c: Coincident(g8,g5)
    c: Horizontal(g5)
    c: Horizontal(g7)
    c: Vertical(g6)
    c: Vertical(g8)
    c: Symmetric(g7,g5,g9)
    c: Distance(g6,g8) = 2.4
    c: Distance(g5,g7) = 1.2
    c: Coincident(g10,g11)
    c: Coincident(g11,g12)
    c: Coincident(g12,g13)
    c: Coincident(g13,g10)
    c: Horizontal(g10)
    c: Horizontal(g12)
    c: Vertical(g11)
    c: Vertical(g13)
    c: Symmetric(g12,g10,g14)
    c: Distance(g11,g13) = 2.4
    c: Distance(g10,g12) = 1.2
    c: Coincident(g15,g16)
    c: Coincident(g16,g17)
    c: Coincident(g17,g18)
    c: Coincident(g18,g15)
    c: Horizontal(g15)
    c: Horizontal(g17)
    c: Vertical(g16)
    c: Vertical(g18)
    c: Symmetric(g17,g15,g19)
    c: Distance(g16,g18) = 2.4
    c: Distance(g15,g17) = 1.2
    c: Vertical(g4,g-3)
    c: Vertical(g9,g-3)
    c: Vertical(g14,g-3)
    c: Vertical(g19,g-3)
    c: DistanceY(g-3,g4) = 5
    c: DistanceY(g4,g9) = 2.8
    c: DistanceY(g9,g14) = 2.8
    c: DistanceY(g14,g19) = 2.8
    c: Coincident(g20,g21)
    c: Coincident(g21,g22)
    c: Coincident(g22,g23)
    c: Coincident(g23,g20)
    c: Horizontal(g20)
    c: Horizontal(g22)
    c: Vertical(g21)
    c: Vertical(g23)
    c: Symmetric(g22,g20,g24)
    c: Distance(g21,g23) = 2.4
    c: Distance(g20,g22) = 1.2
    c: DistanceY(g19,g24) = 2.8
    c: Vertical(g-3,g24)
FEATURE [PartDesign::Pocket] Pocket020
  BaseFeature = -> Pocket012
  Direction = (0,1,-2e-16)
  Length = 3.6
  Length2 = 5
  Profile = -> Sketch154
  ReferenceAxis = -> Sketch154 [N_Axis]
  Refine = true
  Suppressed = false
  Type = 0
FEATURE [PartDesign::Body] Body007  label="lato DX"
  AllowCompound = false
  Group = -> [Binder001,Sketch114,Pad011,Chamfer014,Sketch115,Pocket006,Sketch116,Pad012,Sketch117,Pocket007,Sketch118,Pad013,Sketch119,Pocket008,Pad017,Chamfer009,Pocket009,Sketch123,Sketch120,Pad014,Pad018,Chamfer008,Pocket010,Sketch121,Pad015,Sketch122,Pad016,SubtractivePipe004,SubtractivePipe005,Sketch149,Sketch148,Sketch124,Sketch125,Sketch126,Sketch129,Sketch130,Clone2D001,Sketch131,SubtractiveLoft002,+13 more]
  Origin = -> Origin007
  Tip = -> Pocket020
note: 2 file-system paths scrubbed to <path> (originals preserved in the JSON sidecar)
